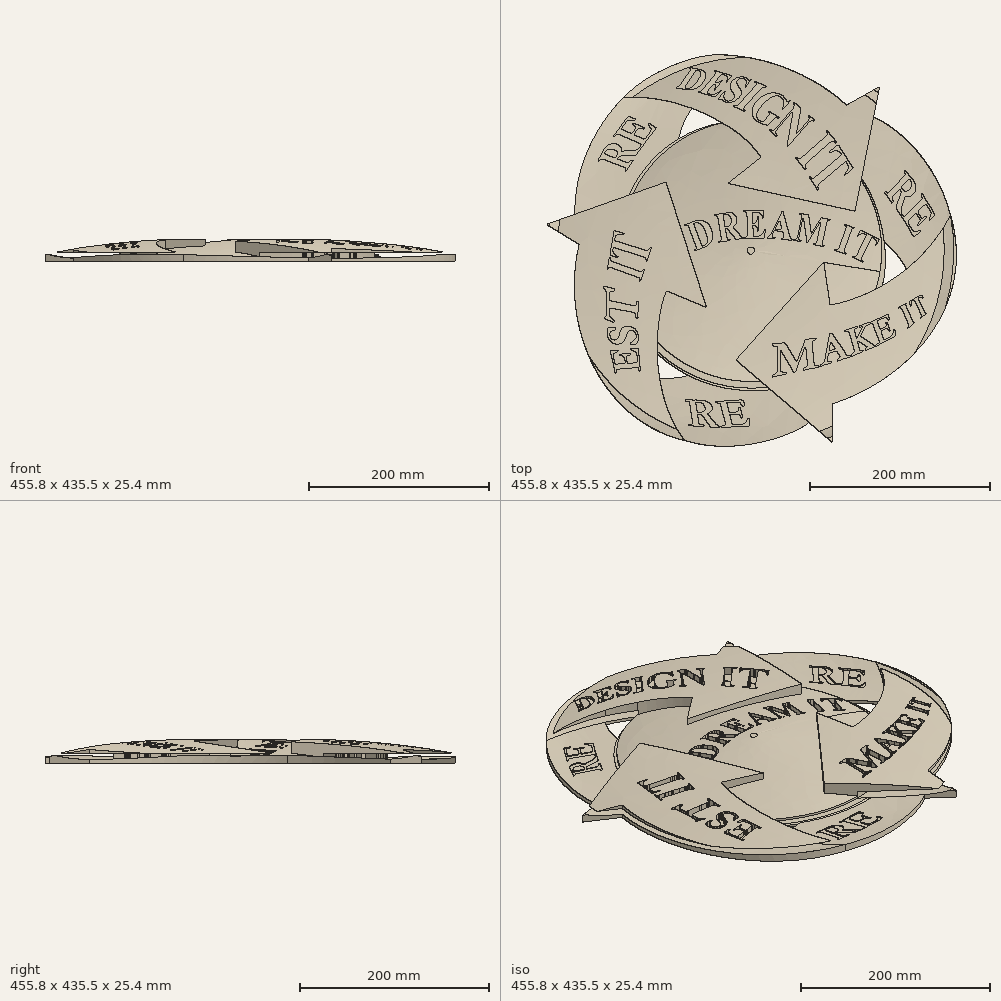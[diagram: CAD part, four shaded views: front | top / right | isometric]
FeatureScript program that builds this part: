
annotation { "Feature Type Name" : "Feature", "Feature Type Description" : "" }
export const myFeature = defineFeature(function(context is Context, id is Id, definition is map)
    precondition{}
    {
        {
            var Q0;
            Q0=qCreatedBy(makeId("Top.planeOp"),FACE);
            var sketch = newSketch(context, id + "F0", { "sketchPlane" : qUnion([Q0])});
            skLineSegment(sketch, "E0", {"start": v(-151.8, -139.59) * mm, "end": v(-151.75, -139.73) * mm});
            skLineSegment(sketch, "E1", {"start": v(-151.75, -139.73) * mm, "end": v(-151.63, -140.16) * mm});
            skLineSegment(sketch, "E2", {"start": v(-151.63, -140.16) * mm, "end": v(-151.45, -140.65) * mm});
            skLineSegment(sketch, "E3", {"start": v(-151.45, -140.65) * mm, "end": v(-151.17, -140.98) * mm});
            skLineSegment(sketch, "E4", {"start": v(-151.17, -140.98) * mm, "end": v(-150.8, -141.1) * mm});
            skLineSegment(sketch, "E5", {"start": v(-150.8, -141.1) * mm, "end": v(-150.68, -141.1) * mm});
            skLineSegment(sketch, "E6", {"start": v(-150.68, -141.1) * mm, "end": v(-150.47, -141.09) * mm});
            skLineSegment(sketch, "E7", {"start": v(-150.47, -141.09) * mm, "end": v(-149.83, -141.24) * mm});
            skLineSegment(sketch, "E8", {"start": v(-149.83, -141.24) * mm, "end": v(-149.27, -141.68) * mm});
            skLineSegment(sketch, "E9", {"start": v(-149.27, -141.68) * mm, "end": v(-148.9, -142.3) * mm});
            skLineSegment(sketch, "E10", {"start": v(-148.9, -142.3) * mm, "end": v(-148.7, -142.85) * mm});
            skLineSegment(sketch, "E11", {"start": v(-148.7, -142.85) * mm, "end": v(-148.64, -143.03) * mm});
            skLineSegment(sketch, "E12", {"start": v(-148.64, -143.03) * mm, "end": v(-148.31, -144.03) * mm});
            skLineSegment(sketch, "E13", {"start": v(-148.31, -144.03) * mm, "end": v(-145.08, -154.14) * mm});
            skLineSegment(sketch, "E14", {"start": v(-145.08, -154.14) * mm, "end": v(-144.77, -155.15) * mm});
            skLineSegment(sketch, "E15", {"start": v(-144.77, -155.15) * mm, "end": v(-144.7, -155.39) * mm});
            skLineSegment(sketch, "E16", {"start": v(-144.7, -155.39) * mm, "end": v(-144.47, -156.1) * mm});
            skLineSegment(sketch, "E17", {"start": v(-144.47, -156.1) * mm, "end": v(-144.28, -157.04) * mm});
            skLineSegment(sketch, "E18", {"start": v(-144.28, -157.04) * mm, "end": v(-144.42, -158) * mm});
            skLineSegment(sketch, "E19", {"start": v(-144.42, -158) * mm, "end": v(-144.88, -158.74) * mm});
            skLineSegment(sketch, "E20", {"start": v(-144.88, -158.74) * mm, "end": v(-145.09, -158.93) * mm});
            skLineSegment(sketch, "E21", {"start": v(-145.09, -158.93) * mm, "end": v(-145.16, -159) * mm});
            skLineSegment(sketch, "E22", {"start": v(-145.16, -159) * mm, "end": v(-145.3, -159.3) * mm});
            skLineSegment(sketch, "E23", {"start": v(-145.3, -159.3) * mm, "end": v(-145.19, -159.68) * mm});
            skLineSegment(sketch, "E24", {"start": v(-145.19, -159.68) * mm, "end": v(-144.84, -159.95) * mm});
            skLineSegment(sketch, "E25", {"start": v(-144.84, -159.95) * mm, "end": v(-144.44, -160.04) * mm});
            skLineSegment(sketch, "E26", {"start": v(-144.44, -160.04) * mm, "end": v(-144.3, -160.03) * mm});
            skLineSegment(sketch, "E27", {"start": v(-144.3, -160.03) * mm, "end": v(-144, -160) * mm});
            skLineSegment(sketch, "E28", {"start": v(-144, -160) * mm, "end": v(-142.46, -160) * mm});
            skLineSegment(sketch, "E29", {"start": v(-142.46, -160) * mm, "end": v(-140.92, -160.1) * mm});
            skLineSegment(sketch, "E30", {"start": v(-140.92, -160.1) * mm, "end": v(-140.61, -160.1) * mm});
            skLineSegment(sketch, "E31", {"start": v(-140.61, -160.1) * mm, "end": v(-140.44, -160.11) * mm});
            skLineSegment(sketch, "E32", {"start": v(-140.44, -160.11) * mm, "end": v(-138.74, -160.21) * mm});
            skLineSegment(sketch, "E33", {"start": v(-138.74, -160.21) * mm, "end": v(-138.56, -160.22) * mm});
            skLineSegment(sketch, "E34", {"start": v(-138.56, -160.22) * mm, "end": v(-138.47, -160.23) * mm});
            skLineSegment(sketch, "E35", {"start": v(-138.47, -160.23) * mm, "end": v(-138.2, -160.22) * mm});
            skLineSegment(sketch, "E36", {"start": v(-138.2, -160.22) * mm, "end": v(-137.86, -160.15) * mm});
            skLineSegment(sketch, "E37", {"start": v(-137.86, -160.15) * mm, "end": v(-137.59, -159.97) * mm});
            skLineSegment(sketch, "E38", {"start": v(-137.59, -159.97) * mm, "end": v(-137.45, -159.7) * mm});
            skLineSegment(sketch, "E39", {"start": v(-137.45, -159.7) * mm, "end": v(-137.43, -159.61) * mm});
            skLineSegment(sketch, "E40", {"start": v(-137.43, -159.61) * mm, "end": v(-137.4, -159.5) * mm});
            skLineSegment(sketch, "E41", {"start": v(-137.4, -159.5) * mm, "end": v(-137.44, -159.15) * mm});
            skLineSegment(sketch, "E42", {"start": v(-137.44, -159.15) * mm, "end": v(-137.65, -158.86) * mm});
            skLineSegment(sketch, "E43", {"start": v(-137.65, -158.86) * mm, "end": v(-138, -158.68) * mm});
            skLineSegment(sketch, "E44", {"start": v(-138, -158.68) * mm, "end": v(-138.3, -158.6) * mm});
            skLineSegment(sketch, "E45", {"start": v(-138.3, -158.6) * mm, "end": v(-138.4, -158.57) * mm});
            skLineSegment(sketch, "E46", {"start": v(-138.4, -158.57) * mm, "end": v(-138.41, -158.57) * mm});
            skLineSegment(sketch, "E47", {"start": v(-138.41, -158.57) * mm, "end": v(-138.58, -158.54) * mm});
            skLineSegment(sketch, "E48", {"start": v(-138.58, -158.54) * mm, "end": v(-138.6, -158.53) * mm});
            skLineSegment(sketch, "E49", {"start": v(-138.6, -158.53) * mm, "end": v(-139.01, -158.48) * mm});
            skLineSegment(sketch, "E50", {"start": v(-139.01, -158.48) * mm, "end": v(-140.22, -158.08) * mm});
            skLineSegment(sketch, "E51", {"start": v(-140.22, -158.08) * mm, "end": v(-141.43, -157.24) * mm});
            skLineSegment(sketch, "E52", {"start": v(-141.43, -157.24) * mm, "end": v(-142.24, -156) * mm});
            skLineSegment(sketch, "E53", {"start": v(-142.24, -156) * mm, "end": v(-142.6, -154.79) * mm});
            skLineSegment(sketch, "E54", {"start": v(-142.6, -154.79) * mm, "end": v(-142.65, -154.38) * mm});
            skLineSegment(sketch, "E55", {"start": v(-142.65, -154.38) * mm, "end": v(-142.66, -154.3) * mm});
            skLineSegment(sketch, "E56", {"start": v(-142.66, -154.3) * mm, "end": v(-142.89, -153.47) * mm});
            skLineSegment(sketch, "E57", {"start": v(-142.89, -153.47) * mm, "end": v(-142.91, -153.38) * mm});
            skLineSegment(sketch, "E58", {"start": v(-142.91, -153.38) * mm, "end": v(-142.96, -153.18) * mm});
            skLineSegment(sketch, "E59", {"start": v(-142.96, -153.18) * mm, "end": v(-143.1, -152.55) * mm});
            skLineSegment(sketch, "E60", {"start": v(-143.1, -152.55) * mm, "end": v(-143.03, -152.06) * mm});
            skLineSegment(sketch, "E61", {"start": v(-143.03, -152.06) * mm, "end": v(-142.65, -151.78) * mm});
            skLineSegment(sketch, "E62", {"start": v(-142.65, -151.78) * mm, "end": v(-142.06, -151.62) * mm});
            skLineSegment(sketch, "E63", {"start": v(-142.06, -151.62) * mm, "end": v(-141.85, -151.58) * mm});
            skLineSegment(sketch, "E64", {"start": v(-141.85, -151.58) * mm, "end": v(-140.51, -151.31) * mm});
            skLineSegment(sketch, "E65", {"start": v(-140.51, -151.31) * mm, "end": v(-127.08, -148.66) * mm});
            skLineSegment(sketch, "E66", {"start": v(-127.08, -148.66) * mm, "end": v(-125.74, -148.38) * mm});
            skLineSegment(sketch, "E67", {"start": v(-125.74, -148.38) * mm, "end": v(-125.4, -148.3) * mm});
            skLineSegment(sketch, "E68", {"start": v(-125.4, -148.3) * mm, "end": v(-124.31, -148.2) * mm});
            skLineSegment(sketch, "E69", {"start": v(-124.31, -148.2) * mm, "end": v(-123.07, -148.35) * mm});
            skLineSegment(sketch, "E70", {"start": v(-123.07, -148.35) * mm, "end": v(-122.03, -149) * mm});
            skLineSegment(sketch, "E71", {"start": v(-122.03, -149) * mm, "end": v(-121.37, -149.93) * mm});
            skLineSegment(sketch, "E72", {"start": v(-121.37, -149.93) * mm, "end": v(-121.23, -150.27) * mm});
            skLineSegment(sketch, "E73", {"start": v(-121.23, -150.27) * mm, "end": v(-121.18, -150.4) * mm});
            skLineSegment(sketch, "E74", {"start": v(-121.18, -150.4) * mm, "end": v(-121, -150.73) * mm});
            skLineSegment(sketch, "E75", {"start": v(-121, -150.73) * mm, "end": v(-120.67, -151.14) * mm});
            skLineSegment(sketch, "E76", {"start": v(-120.67, -151.14) * mm, "end": v(-120.24, -151.37) * mm});
            skLineSegment(sketch, "E77", {"start": v(-120.24, -151.37) * mm, "end": v(-119.82, -151.36) * mm});
            skLineSegment(sketch, "E78", {"start": v(-119.82, -151.36) * mm, "end": v(-119.7, -151.3) * mm});
            skLineSegment(sketch, "E79", {"start": v(-119.7, -151.3) * mm, "end": v(-119.58, -151.26) * mm});
            skLineSegment(sketch, "E80", {"start": v(-119.58, -151.26) * mm, "end": v(-119.27, -150.96) * mm});
            skLineSegment(sketch, "E81", {"start": v(-119.27, -150.96) * mm, "end": v(-119.2, -150.51) * mm});
            skLineSegment(sketch, "E82", {"start": v(-119.2, -150.51) * mm, "end": v(-119.34, -150.02) * mm});
            skLineSegment(sketch, "E83", {"start": v(-119.34, -150.02) * mm, "end": v(-119.46, -149.65) * mm});
            skLineSegment(sketch, "E84", {"start": v(-119.46, -149.65) * mm, "end": v(-119.49, -149.52) * mm});
            skLineSegment(sketch, "E85", {"start": v(-119.49, -149.52) * mm, "end": v(-119.5, -149.5) * mm});
            skLineSegment(sketch, "E86", {"start": v(-119.5, -149.5) * mm, "end": v(-119.6, -149.16) * mm});
            skLineSegment(sketch, "E87", {"start": v(-119.6, -149.16) * mm, "end": v(-119.61, -149.13) * mm});
            skLineSegment(sketch, "E88", {"start": v(-119.61, -149.13) * mm, "end": v(-119.84, -148.5) * mm});
            skLineSegment(sketch, "E89", {"start": v(-119.84, -148.5) * mm, "end": v(-120.65, -145.27) * mm});
            skLineSegment(sketch, "E90", {"start": v(-120.65, -145.27) * mm, "end": v(-121.15, -141.98) * mm});
            skLineSegment(sketch, "E91", {"start": v(-121.15, -141.98) * mm, "end": v(-121.24, -141.32) * mm});
            skLineSegment(sketch, "E92", {"start": v(-121.24, -141.32) * mm, "end": v(-121.26, -141.19) * mm});
            skLineSegment(sketch, "E93", {"start": v(-121.26, -141.19) * mm, "end": v(-121.23, -140.77) * mm});
            skLineSegment(sketch, "E94", {"start": v(-121.23, -140.77) * mm, "end": v(-121.23, -140.2) * mm});
            skLineSegment(sketch, "E95", {"start": v(-121.23, -140.2) * mm, "end": v(-121.43, -139.74) * mm});
            skLineSegment(sketch, "E96", {"start": v(-121.43, -139.74) * mm, "end": v(-121.87, -139.53) * mm});
            skLineSegment(sketch, "E97", {"start": v(-121.87, -139.53) * mm, "end": v(-122.02, -139.52) * mm});
            skLineSegment(sketch, "E98", {"start": v(-122.02, -139.52) * mm, "end": v(-122.2, -139.51) * mm});
            skLineSegment(sketch, "E99", {"start": v(-122.2, -139.51) * mm, "end": v(-122.73, -139.67) * mm});
            skLineSegment(sketch, "E100", {"start": v(-122.73, -139.67) * mm, "end": v(-123.01, -140.12) * mm});
            skLineSegment(sketch, "E101", {"start": v(-123.01, -140.12) * mm, "end": v(-123.04, -140.72) * mm});
            skLineSegment(sketch, "E102", {"start": v(-123.04, -140.72) * mm, "end": v(-123.01, -141.18) * mm});
            skLineSegment(sketch, "E103", {"start": v(-123.01, -141.18) * mm, "end": v(-123.01, -141.33) * mm});
            skLineSegment(sketch, "E104", {"start": v(-123.01, -141.33) * mm, "end": v(-123.01, -141.53) * mm});
            skLineSegment(sketch, "E105", {"start": v(-123.01, -141.53) * mm, "end": v(-123.1, -142.15) * mm});
            skLineSegment(sketch, "E106", {"start": v(-123.1, -142.15) * mm, "end": v(-123.4, -142.78) * mm});
            skLineSegment(sketch, "E107", {"start": v(-123.4, -142.78) * mm, "end": v(-123.92, -143.22) * mm});
            skLineSegment(sketch, "E108", {"start": v(-123.92, -143.22) * mm, "end": v(-124.51, -143.44) * mm});
            skLineSegment(sketch, "E109", {"start": v(-124.51, -143.44) * mm, "end": v(-124.71, -143.47) * mm});
            skLineSegment(sketch, "E110", {"start": v(-124.71, -143.47) * mm, "end": v(-124.83, -143.48) * mm});
            skLineSegment(sketch, "E111", {"start": v(-124.83, -143.48) * mm, "end": v(-125.99, -143.77) * mm});
            skLineSegment(sketch, "E112", {"start": v(-125.99, -143.77) * mm, "end": v(-126.1, -143.79) * mm});
            skLineSegment(sketch, "E113", {"start": v(-126.1, -143.79) * mm, "end": v(-126.78, -143.92) * mm});
            skLineSegment(sketch, "E114", {"start": v(-126.78, -143.92) * mm, "end": v(-133.5, -145.17) * mm});
            skLineSegment(sketch, "E115", {"start": v(-133.5, -145.17) * mm, "end": v(-134.18, -145.3) * mm});
            skLineSegment(sketch, "E116", {"start": v(-134.18, -145.3) * mm, "end": v(-134.94, -145.44) * mm});
            skLineSegment(sketch, "E117", {"start": v(-134.94, -145.44) * mm, "end": v(-142.5, -146.82) * mm});
            skLineSegment(sketch, "E118", {"start": v(-142.5, -146.82) * mm, "end": v(-143.26, -146.96) * mm});
            skLineSegment(sketch, "E119", {"start": v(-143.26, -146.96) * mm, "end": v(-143.48, -147) * mm});
            skLineSegment(sketch, "E120", {"start": v(-143.48, -147) * mm, "end": v(-144.14, -147.09) * mm});
            skLineSegment(sketch, "E121", {"start": v(-144.14, -147.09) * mm, "end": v(-144.64, -147) * mm});
            skLineSegment(sketch, "E122", {"start": v(-144.64, -147) * mm, "end": v(-144.94, -146.6) * mm});
            skLineSegment(sketch, "E123", {"start": v(-144.94, -146.6) * mm, "end": v(-145.17, -145.96) * mm});
            skLineSegment(sketch, "E124", {"start": v(-145.17, -145.96) * mm, "end": v(-145.23, -145.75) * mm});
            skLineSegment(sketch, "E125", {"start": v(-145.23, -145.75) * mm, "end": v(-145.3, -145.54) * mm});
            skLineSegment(sketch, "E126", {"start": v(-145.3, -145.54) * mm, "end": v(-146.02, -143.44) * mm});
            skLineSegment(sketch, "E127", {"start": v(-146.02, -143.44) * mm, "end": v(-146.1, -143.24) * mm});
            skLineSegment(sketch, "E128", {"start": v(-146.1, -143.24) * mm, "end": v(-146.18, -143.02) * mm});
            skLineSegment(sketch, "E129", {"start": v(-146.18, -143.02) * mm, "end": v(-146.12, -142.12) * mm});
            skLineSegment(sketch, "E130", {"start": v(-146.12, -142.12) * mm, "end": v(-145.5, -141.47) * mm});
            skLineSegment(sketch, "E131", {"start": v(-145.5, -141.47) * mm, "end": v(-145.3, -141.39) * mm});
            skLineSegment(sketch, "E132", {"start": v(-145.3, -141.39) * mm, "end": v(-145.1, -141.3) * mm});
            skLineSegment(sketch, "E133", {"start": v(-145.1, -141.3) * mm, "end": v(-144.15, -140.72) * mm});
            skLineSegment(sketch, "E134", {"start": v(-144.15, -140.72) * mm, "end": v(-143.23, -140.1) * mm});
            skLineSegment(sketch, "E135", {"start": v(-143.23, -140.1) * mm, "end": v(-143.05, -139.97) * mm});
            skLineSegment(sketch, "E136", {"start": v(-143.05, -139.97) * mm, "end": v(-142.98, -139.92) * mm});
            skLineSegment(sketch, "E137", {"start": v(-142.98, -139.92) * mm, "end": v(-142.76, -139.77) * mm});
            skLineSegment(sketch, "E138", {"start": v(-142.76, -139.77) * mm, "end": v(-142.53, -139.55) * mm});
            skLineSegment(sketch, "E139", {"start": v(-142.53, -139.55) * mm, "end": v(-142.43, -139.25) * mm});
            skLineSegment(sketch, "E140", {"start": v(-142.43, -139.25) * mm, "end": v(-142.51, -138.94) * mm});
            skLineSegment(sketch, "E141", {"start": v(-142.51, -138.94) * mm, "end": v(-142.56, -138.85) * mm});
            skLineSegment(sketch, "E142", {"start": v(-142.56, -138.85) * mm, "end": v(-142.63, -138.73) * mm});
            skLineSegment(sketch, "E143", {"start": v(-142.63, -138.73) * mm, "end": v(-143.02, -138.33) * mm});
            skLineSegment(sketch, "E144", {"start": v(-143.02, -138.33) * mm, "end": v(-143.57, -138.23) * mm});
            skLineSegment(sketch, "E145", {"start": v(-143.57, -138.23) * mm, "end": v(-143.7, -138.25) * mm});
            skLineSegment(sketch, "E146", {"start": v(-143.7, -138.25) * mm, "end": v(-144.36, -138.37) * mm});
            skLineSegment(sketch, "E147", {"start": v(-144.36, -138.37) * mm, "end": v(-151.08, -139.47) * mm});
            skLineSegment(sketch, "E148", {"start": v(-151.08, -139.47) * mm, "end": v(-151.8, -139.59) * mm});
            skLineSegment(sketch, "E149", {"start": v(105.73, 98.84) * mm, "end": v(105.54, 98.8) * mm});
            skLineSegment(sketch, "E150", {"start": v(105.54, 98.8) * mm, "end": v(104.74, 98.33) * mm});
            skLineSegment(sketch, "E151", {"start": v(104.74, 98.33) * mm, "end": v(104.04, 97.71) * mm});
            skLineSegment(sketch, "E152", {"start": v(104.04, 97.71) * mm, "end": v(103.9, 97.6) * mm});
            skLineSegment(sketch, "E153", {"start": v(103.9, 97.6) * mm, "end": v(101.67, 95.71) * mm});
            skLineSegment(sketch, "E154", {"start": v(101.67, 95.71) * mm, "end": v(79.4, 76.9) * mm});
            skLineSegment(sketch, "E155", {"start": v(79.4, 76.9) * mm, "end": v(77.18, 75) * mm});
            skLineSegment(sketch, "E156", {"start": v(77.18, 75) * mm, "end": v(77.04, 74.89) * mm});
            skLineSegment(sketch, "E157", {"start": v(77.04, 74.89) * mm, "end": v(75.67, 73.59) * mm});
            skLineSegment(sketch, "E158", {"start": v(75.67, 73.59) * mm, "end": v(75.55, 73.44) * mm});
            skLineSegment(sketch, "E159", {"start": v(75.55, 73.44) * mm, "end": v(75.35, 73.22) * mm});
            skLineSegment(sketch, "E160", {"start": v(75.35, 73.22) * mm, "end": v(74.85, 72.44) * mm});
            skLineSegment(sketch, "E161", {"start": v(74.85, 72.44) * mm, "end": v(74.5, 71.37) * mm});
            skLineSegment(sketch, "E162", {"start": v(74.5, 71.37) * mm, "end": v(74.5, 70.25) * mm});
            skLineSegment(sketch, "E163", {"start": v(74.5, 70.25) * mm, "end": v(74.75, 69.35) * mm});
            skLineSegment(sketch, "E164", {"start": v(74.75, 69.35) * mm, "end": v(74.89, 69.07) * mm});
            skLineSegment(sketch, "E165", {"start": v(74.89, 69.07) * mm, "end": v(74.94, 68.97) * mm});
            skLineSegment(sketch, "E166", {"start": v(74.94, 68.97) * mm, "end": v(75.48, 67.9) * mm});
            skLineSegment(sketch, "E167", {"start": v(75.48, 67.9) * mm, "end": v(75.52, 67.8) * mm});
            skLineSegment(sketch, "E168", {"start": v(75.52, 67.8) * mm, "end": v(75.55, 67.72) * mm});
            skLineSegment(sketch, "E169", {"start": v(75.55, 67.72) * mm, "end": v(75.51, 67.4) * mm});
            skLineSegment(sketch, "E170", {"start": v(75.51, 67.4) * mm, "end": v(75.3, 67.13) * mm});
            skLineSegment(sketch, "E171", {"start": v(75.3, 67.13) * mm, "end": v(75.23, 67.1) * mm});
            skLineSegment(sketch, "E172", {"start": v(75.23, 67.1) * mm, "end": v(75.17, 67.05) * mm});
            skLineSegment(sketch, "E173", {"start": v(75.17, 67.05) * mm, "end": v(74.84, 66.98) * mm});
            skLineSegment(sketch, "E174", {"start": v(74.84, 66.98) * mm, "end": v(74.55, 67.1) * mm});
            skLineSegment(sketch, "E175", {"start": v(74.55, 67.1) * mm, "end": v(74.5, 67.16) * mm});
            skLineSegment(sketch, "E176", {"start": v(74.5, 67.16) * mm, "end": v(74.44, 67.23) * mm});
            skLineSegment(sketch, "E177", {"start": v(74.44, 67.23) * mm, "end": v(73.93, 67.9) * mm});
            skLineSegment(sketch, "E178", {"start": v(73.93, 67.9) * mm, "end": v(73.88, 67.98) * mm});
            skLineSegment(sketch, "E179", {"start": v(73.88, 67.98) * mm, "end": v(73.17, 69.05) * mm});
            skLineSegment(sketch, "E180", {"start": v(73.17, 69.05) * mm, "end": v(69.74, 74.47) * mm});
            skLineSegment(sketch, "E181", {"start": v(69.74, 74.47) * mm, "end": v(66.2, 79.83) * mm});
            skLineSegment(sketch, "E182", {"start": v(66.2, 79.83) * mm, "end": v(65.44, 80.86) * mm});
            skLineSegment(sketch, "E183", {"start": v(65.44, 80.86) * mm, "end": v(65.4, 80.92) * mm});
            skLineSegment(sketch, "E184", {"start": v(65.4, 80.92) * mm, "end": v(65.05, 81.5) * mm});
            skLineSegment(sketch, "E185", {"start": v(65.05, 81.5) * mm, "end": v(65.01, 81.55) * mm});
            skLineSegment(sketch, "E186", {"start": v(65.01, 81.55) * mm, "end": v(64.95, 81.64) * mm});
            skLineSegment(sketch, "E187", {"start": v(64.95, 81.64) * mm, "end": v(64.91, 82.03) * mm});
            skLineSegment(sketch, "E188", {"start": v(64.91, 82.03) * mm, "end": v(65.14, 82.36) * mm});
            skLineSegment(sketch, "E189", {"start": v(65.14, 82.36) * mm, "end": v(65.2, 82.43) * mm});
            skLineSegment(sketch, "E190", {"start": v(65.2, 82.43) * mm, "end": v(65.28, 82.5) * mm});
            skLineSegment(sketch, "E191", {"start": v(65.28, 82.5) * mm, "end": v(65.66, 82.64) * mm});
            skLineSegment(sketch, "E192", {"start": v(65.66, 82.64) * mm, "end": v(66.03, 82.48) * mm});
            skLineSegment(sketch, "E193", {"start": v(66.03, 82.48) * mm, "end": v(66.1, 82.4) * mm});
            skLineSegment(sketch, "E194", {"start": v(66.1, 82.4) * mm, "end": v(66.17, 82.33) * mm});
            skLineSegment(sketch, "E195", {"start": v(66.17, 82.33) * mm, "end": v(66.8, 81.53) * mm});
            skLineSegment(sketch, "E196", {"start": v(66.8, 81.53) * mm, "end": v(66.86, 81.45) * mm});
            skLineSegment(sketch, "E197", {"start": v(66.86, 81.45) * mm, "end": v(67.04, 81.22) * mm});
            skLineSegment(sketch, "E198", {"start": v(67.04, 81.22) * mm, "end": v(67.73, 80.62) * mm});
            skLineSegment(sketch, "E199", {"start": v(67.73, 80.62) * mm, "end": v(68.66, 80.26) * mm});
            skLineSegment(sketch, "E200", {"start": v(68.66, 80.26) * mm, "end": v(69.64, 80.38) * mm});
            skLineSegment(sketch, "E201", {"start": v(69.64, 80.38) * mm, "end": v(70.47, 80.78) * mm});
            skLineSegment(sketch, "E202", {"start": v(70.47, 80.78) * mm, "end": v(70.7, 80.96) * mm});
            skLineSegment(sketch, "E203", {"start": v(70.7, 80.96) * mm, "end": v(71.53, 81.56) * mm});
            skLineSegment(sketch, "E204", {"start": v(71.53, 81.56) * mm, "end": v(75.47, 84.77) * mm});
            skLineSegment(sketch, "E205", {"start": v(75.47, 84.77) * mm, "end": v(79.35, 88.06) * mm});
            skLineSegment(sketch, "E206", {"start": v(79.35, 88.06) * mm, "end": v(80.13, 88.7) * mm});
            skLineSegment(sketch, "E207", {"start": v(80.13, 88.7) * mm, "end": v(80.9, 89.34) * mm});
            skLineSegment(sketch, "E208", {"start": v(80.9, 89.34) * mm, "end": v(88.58, 95.77) * mm});
            skLineSegment(sketch, "E209", {"start": v(88.58, 95.77) * mm, "end": v(89.34, 96.42) * mm});
            skLineSegment(sketch, "E210", {"start": v(89.34, 96.42) * mm, "end": v(90.1, 97.07) * mm});
            skLineSegment(sketch, "E211", {"start": v(90.1, 97.07) * mm, "end": v(93.95, 100.27) * mm});
            skLineSegment(sketch, "E212", {"start": v(93.95, 100.27) * mm, "end": v(97.76, 103.54) * mm});
            skLineSegment(sketch, "E213", {"start": v(97.76, 103.54) * mm, "end": v(98.5, 104.22) * mm});
            skLineSegment(sketch, "E214", {"start": v(98.5, 104.22) * mm, "end": v(98.6, 104.32) * mm});
            skLineSegment(sketch, "E215", {"start": v(98.6, 104.32) * mm, "end": v(99.65, 105.18) * mm});
            skLineSegment(sketch, "E216", {"start": v(99.65, 105.18) * mm, "end": v(99.76, 105.26) * mm});
            skLineSegment(sketch, "E217", {"start": v(99.76, 105.26) * mm, "end": v(99.92, 105.39) * mm});
            skLineSegment(sketch, "E218", {"start": v(99.92, 105.39) * mm, "end": v(100.38, 105.8) * mm});
            skLineSegment(sketch, "E219", {"start": v(100.38, 105.8) * mm, "end": v(100.67, 106.26) * mm});
            skLineSegment(sketch, "E220", {"start": v(100.67, 106.26) * mm, "end": v(100.64, 106.77) * mm});
            skLineSegment(sketch, "E221", {"start": v(100.64, 106.77) * mm, "end": v(100.4, 107.29) * mm});
            skLineSegment(sketch, "E222", {"start": v(100.4, 107.29) * mm, "end": v(100.31, 107.45) * mm});
            skLineSegment(sketch, "E223", {"start": v(100.31, 107.45) * mm, "end": v(100, 108) * mm});
            skLineSegment(sketch, "E224", {"start": v(100, 108) * mm, "end": v(98.8, 109.5) * mm});
            skLineSegment(sketch, "E225", {"start": v(98.8, 109.5) * mm, "end": v(97, 110.8) * mm});
            skLineSegment(sketch, "E226", {"start": v(97, 110.8) * mm, "end": v(94.86, 111.22) * mm});
            skLineSegment(sketch, "E227", {"start": v(94.86, 111.22) * mm, "end": v(92.94, 110.85) * mm});
            skLineSegment(sketch, "E228", {"start": v(92.94, 110.85) * mm, "end": v(92.36, 110.6) * mm});
            skLineSegment(sketch, "E229", {"start": v(92.36, 110.6) * mm, "end": v(92.05, 110.46) * mm});
            skLineSegment(sketch, "E230", {"start": v(92.05, 110.46) * mm, "end": v(88.96, 109.04) * mm});
            skLineSegment(sketch, "E231", {"start": v(88.96, 109.04) * mm, "end": v(88.65, 108.9) * mm});
            skLineSegment(sketch, "E232", {"start": v(88.65, 108.9) * mm, "end": v(88.57, 108.86) * mm});
            skLineSegment(sketch, "E233", {"start": v(88.57, 108.86) * mm, "end": v(88.17, 108.74) * mm});
            skLineSegment(sketch, "E234", {"start": v(88.17, 108.74) * mm, "end": v(87.8, 108.86) * mm});
            skLineSegment(sketch, "E235", {"start": v(87.8, 108.86) * mm, "end": v(87.74, 108.95) * mm});
            skLineSegment(sketch, "E236", {"start": v(87.74, 108.95) * mm, "end": v(87.68, 109.02) * mm});
            skLineSegment(sketch, "E237", {"start": v(87.68, 109.02) * mm, "end": v(87.6, 109.43) * mm});
            skLineSegment(sketch, "E238", {"start": v(87.6, 109.43) * mm, "end": v(87.76, 109.82) * mm});
            skLineSegment(sketch, "E239", {"start": v(87.76, 109.82) * mm, "end": v(87.82, 109.89) * mm});
            skLineSegment(sketch, "E240", {"start": v(87.82, 109.89) * mm, "end": v(87.86, 109.94) * mm});
            skLineSegment(sketch, "E241", {"start": v(87.86, 109.94) * mm, "end": v(88.34, 110.43) * mm});
            skLineSegment(sketch, "E242", {"start": v(88.34, 110.43) * mm, "end": v(88.4, 110.47) * mm});
            skLineSegment(sketch, "E243", {"start": v(88.4, 110.47) * mm, "end": v(88.97, 110.95) * mm});
            skLineSegment(sketch, "E244", {"start": v(88.97, 110.95) * mm, "end": v(94.68, 115.74) * mm});
            skLineSegment(sketch, "E245", {"start": v(94.68, 115.74) * mm, "end": v(95.25, 116.22) * mm});
            skLineSegment(sketch, "E246", {"start": v(95.25, 116.22) * mm, "end": v(95.33, 116.29) * mm});
            skLineSegment(sketch, "E247", {"start": v(95.33, 116.29) * mm, "end": v(96.17, 116.86) * mm});
            skLineSegment(sketch, "E248", {"start": v(96.17, 116.86) * mm, "end": v(96.25, 116.9) * mm});
            skLineSegment(sketch, "E249", {"start": v(96.25, 116.9) * mm, "end": v(96.38, 117) * mm});
            skLineSegment(sketch, "E250", {"start": v(96.38, 117) * mm, "end": v(96.82, 117.17) * mm});
            skLineSegment(sketch, "E251", {"start": v(96.82, 117.17) * mm, "end": v(97.27, 117.16) * mm});
            skLineSegment(sketch, "E252", {"start": v(97.27, 117.16) * mm, "end": v(97.65, 116.9) * mm});
            skLineSegment(sketch, "E253", {"start": v(97.65, 116.9) * mm, "end": v(97.94, 116.53) * mm});
            skLineSegment(sketch, "E254", {"start": v(97.94, 116.53) * mm, "end": v(98.02, 116.4) * mm});
            skLineSegment(sketch, "E255", {"start": v(98.02, 116.4) * mm, "end": v(98.65, 115.38) * mm});
            skLineSegment(sketch, "E256", {"start": v(98.65, 115.38) * mm, "end": v(105.04, 105.31) * mm});
            skLineSegment(sketch, "E257", {"start": v(105.04, 105.31) * mm, "end": v(105.7, 104.32) * mm});
            skLineSegment(sketch, "E258", {"start": v(105.7, 104.32) * mm, "end": v(106.34, 103.35) * mm});
            skLineSegment(sketch, "E259", {"start": v(106.34, 103.35) * mm, "end": v(112.65, 93.55) * mm});
            skLineSegment(sketch, "E260", {"start": v(112.65, 93.55) * mm, "end": v(113.29, 92.57) * mm});
            skLineSegment(sketch, "E261", {"start": v(113.29, 92.57) * mm, "end": v(113.39, 92.41) * mm});
            skLineSegment(sketch, "E262", {"start": v(113.39, 92.41) * mm, "end": v(113.62, 91.88) * mm});
            skLineSegment(sketch, "E263", {"start": v(113.62, 91.88) * mm, "end": v(113.66, 91.33) * mm});
            skLineSegment(sketch, "E264", {"start": v(113.66, 91.33) * mm, "end": v(113.42, 90.84) * mm});
            skLineSegment(sketch, "E265", {"start": v(113.42, 90.84) * mm, "end": v(113.06, 90.47) * mm});
            skLineSegment(sketch, "E266", {"start": v(113.06, 90.47) * mm, "end": v(112.93, 90.36) * mm});
            skLineSegment(sketch, "E267", {"start": v(112.93, 90.36) * mm, "end": v(112.3, 89.83) * mm});
            skLineSegment(sketch, "E268", {"start": v(112.3, 89.83) * mm, "end": v(106, 84.53) * mm});
            skLineSegment(sketch, "E269", {"start": v(106, 84.53) * mm, "end": v(105.37, 84) * mm});
            skLineSegment(sketch, "E270", {"start": v(105.37, 84) * mm, "end": v(105.32, 83.96) * mm});
            skLineSegment(sketch, "E271", {"start": v(105.32, 83.96) * mm, "end": v(104.76, 83.57) * mm});
            skLineSegment(sketch, "E272", {"start": v(104.76, 83.57) * mm, "end": v(104.7, 83.54) * mm});
            skLineSegment(sketch, "E273", {"start": v(104.7, 83.54) * mm, "end": v(104.65, 83.51) * mm});
            skLineSegment(sketch, "E274", {"start": v(104.65, 83.51) * mm, "end": v(104.18, 83.6) * mm});
            skLineSegment(sketch, "E275", {"start": v(104.18, 83.6) * mm, "end": v(104.15, 83.64) * mm});
            skLineSegment(sketch, "E276", {"start": v(104.15, 83.64) * mm, "end": v(104.1, 83.68) * mm});
            skLineSegment(sketch, "E277", {"start": v(104.1, 83.68) * mm, "end": v(104.03, 84.15) * mm});
            skLineSegment(sketch, "E278", {"start": v(104.03, 84.15) * mm, "end": v(104.06, 84.2) * mm});
            skLineSegment(sketch, "E279", {"start": v(104.06, 84.2) * mm, "end": v(104.12, 84.3) * mm});
            skLineSegment(sketch, "E280", {"start": v(104.12, 84.3) * mm, "end": v(104.8, 85.28) * mm});
            skLineSegment(sketch, "E281", {"start": v(104.8, 85.28) * mm, "end": v(104.88, 85.37) * mm});
            skLineSegment(sketch, "E282", {"start": v(104.88, 85.37) * mm, "end": v(105.05, 85.63) * mm});
            skLineSegment(sketch, "E283", {"start": v(105.05, 85.63) * mm, "end": v(105.97, 86.87) * mm});
            skLineSegment(sketch, "E284", {"start": v(105.97, 86.87) * mm, "end": v(106.84, 88.14) * mm});
            skLineSegment(sketch, "E285", {"start": v(106.84, 88.14) * mm, "end": v(106.98, 88.4) * mm});
            skLineSegment(sketch, "E286", {"start": v(106.98, 88.4) * mm, "end": v(107.35, 89.08) * mm});
            skLineSegment(sketch, "E287", {"start": v(107.35, 89.08) * mm, "end": v(108.2, 91.22) * mm});
            skLineSegment(sketch, "E288", {"start": v(108.2, 91.22) * mm, "end": v(108.46, 93.73) * mm});
            skLineSegment(sketch, "E289", {"start": v(108.46, 93.73) * mm, "end": v(107.67, 96.18) * mm});
            skLineSegment(sketch, "E290", {"start": v(107.67, 96.18) * mm, "end": v(106.28, 98.23) * mm});
            skLineSegment(sketch, "E291", {"start": v(106.28, 98.23) * mm, "end": v(105.73, 98.84) * mm});
            skLineSegment(sketch, "E292", {"start": v(46.57, 154.33) * mm, "end": v(46.16, 154.08) * mm});
            skLineSegment(sketch, "E293", {"start": v(46.16, 154.08) * mm, "end": v(45.72, 153.66) * mm});
            skLineSegment(sketch, "E294", {"start": v(45.72, 153.66) * mm, "end": v(45.35, 153.18) * mm});
            skLineSegment(sketch, "E295", {"start": v(45.35, 153.18) * mm, "end": v(45.07, 152.82) * mm});
            skLineSegment(sketch, "E296", {"start": v(45.07, 152.82) * mm, "end": v(44.97, 152.7) * mm});
            skLineSegment(sketch, "E297", {"start": v(44.97, 152.7) * mm, "end": v(43.76, 151.3) * mm});
            skLineSegment(sketch, "E298", {"start": v(43.76, 151.3) * mm, "end": v(31.65, 137.29) * mm});
            skLineSegment(sketch, "E299", {"start": v(31.65, 137.29) * mm, "end": v(30.44, 135.89) * mm});
            skLineSegment(sketch, "E300", {"start": v(30.44, 135.89) * mm, "end": v(30.25, 135.66) * mm});
            skLineSegment(sketch, "E301", {"start": v(30.25, 135.66) * mm, "end": v(29.33, 134.54) * mm});
            skLineSegment(sketch, "E302", {"start": v(29.33, 134.54) * mm, "end": v(28.51, 133.33) * mm});
            skLineSegment(sketch, "E303", {"start": v(28.51, 133.33) * mm, "end": v(28.37, 133.08) * mm});
            skLineSegment(sketch, "E304", {"start": v(28.37, 133.08) * mm, "end": v(28.21, 132.8) * mm});
            skLineSegment(sketch, "E305", {"start": v(28.21, 132.8) * mm, "end": v(27.87, 131.9) * mm});
            skLineSegment(sketch, "E306", {"start": v(27.87, 131.9) * mm, "end": v(27.74, 130.73) * mm});
            skLineSegment(sketch, "E307", {"start": v(27.74, 130.73) * mm, "end": v(28, 129.6) * mm});
            skLineSegment(sketch, "E308", {"start": v(28, 129.6) * mm, "end": v(28.47, 128.74) * mm});
            skLineSegment(sketch, "E309", {"start": v(28.47, 128.74) * mm, "end": v(28.68, 128.5) * mm});
            skLineSegment(sketch, "E310", {"start": v(28.68, 128.5) * mm, "end": v(28.73, 128.42) * mm});
            skLineSegment(sketch, "E311", {"start": v(28.73, 128.42) * mm, "end": v(29.24, 127.76) * mm});
            skLineSegment(sketch, "E312", {"start": v(29.24, 127.76) * mm, "end": v(29.27, 127.69) * mm});
            skLineSegment(sketch, "E313", {"start": v(29.27, 127.69) * mm, "end": v(29.29, 127.66) * mm});
            skLineSegment(sketch, "E314", {"start": v(29.29, 127.66) * mm, "end": v(29.23, 127.43) * mm});
            skLineSegment(sketch, "E315", {"start": v(29.23, 127.43) * mm, "end": v(29.1, 127.2) * mm});
            skLineSegment(sketch, "E316", {"start": v(29.1, 127.2) * mm, "end": v(29.07, 127.16) * mm});
            skLineSegment(sketch, "E317", {"start": v(29.07, 127.16) * mm, "end": v(29.04, 127.12) * mm});
            skLineSegment(sketch, "E318", {"start": v(29.04, 127.12) * mm, "end": v(28.84, 126.98) * mm});
            skLineSegment(sketch, "E319", {"start": v(28.84, 126.98) * mm, "end": v(28.59, 126.97) * mm});
            skLineSegment(sketch, "E320", {"start": v(28.59, 126.97) * mm, "end": v(28.53, 127) * mm});
            skLineSegment(sketch, "E321", {"start": v(28.53, 127) * mm, "end": v(28.5, 127.02) * mm});
            skLineSegment(sketch, "E322", {"start": v(28.5, 127.02) * mm, "end": v(28.21, 127.2) * mm});
            skLineSegment(sketch, "E323", {"start": v(28.21, 127.2) * mm, "end": v(28.19, 127.21) * mm});
            skLineSegment(sketch, "E324", {"start": v(28.19, 127.21) * mm, "end": v(27.6, 127.73) * mm});
            skLineSegment(sketch, "E325", {"start": v(27.6, 127.73) * mm, "end": v(21.75, 132.92) * mm});
            skLineSegment(sketch, "E326", {"start": v(21.75, 132.92) * mm, "end": v(21.17, 133.44) * mm});
            skLineSegment(sketch, "E327", {"start": v(21.17, 133.44) * mm, "end": v(21.1, 133.5) * mm});
            skLineSegment(sketch, "E328", {"start": v(21.1, 133.5) * mm, "end": v(20.85, 133.84) * mm});
            skLineSegment(sketch, "E329", {"start": v(20.85, 133.84) * mm, "end": v(20.85, 134.23) * mm});
            skLineSegment(sketch, "E330", {"start": v(20.85, 134.23) * mm, "end": v(20.9, 134.32) * mm});
            skLineSegment(sketch, "E331", {"start": v(20.9, 134.32) * mm, "end": v(20.98, 134.42) * mm});
            skLineSegment(sketch, "E332", {"start": v(20.98, 134.42) * mm, "end": v(21.4, 134.59) * mm});
            skLineSegment(sketch, "E333", {"start": v(21.4, 134.59) * mm, "end": v(21.88, 134.44) * mm});
            skLineSegment(sketch, "E334", {"start": v(21.88, 134.44) * mm, "end": v(21.98, 134.4) * mm});
            skLineSegment(sketch, "E335", {"start": v(21.98, 134.4) * mm, "end": v(22.4, 134.2) * mm});
            skLineSegment(sketch, "E336", {"start": v(22.4, 134.2) * mm, "end": v(23.7, 133.75) * mm});
            skLineSegment(sketch, "E337", {"start": v(23.7, 133.75) * mm, "end": v(25.05, 133.66) * mm});
            skLineSegment(sketch, "E338", {"start": v(25.05, 133.66) * mm, "end": v(26.27, 134.2) * mm});
            skLineSegment(sketch, "E339", {"start": v(26.27, 134.2) * mm, "end": v(27.3, 135.1) * mm});
            skLineSegment(sketch, "E340", {"start": v(27.3, 135.1) * mm, "end": v(27.6, 135.43) * mm});
            skLineSegment(sketch, "E341", {"start": v(27.6, 135.43) * mm, "end": v(28.47, 136.37) * mm});
            skLineSegment(sketch, "E342", {"start": v(28.47, 136.37) * mm, "end": v(36.83, 145.9) * mm});
            skLineSegment(sketch, "E343", {"start": v(36.83, 145.9) * mm, "end": v(37.67, 146.86) * mm});
            skLineSegment(sketch, "E344", {"start": v(37.67, 146.86) * mm, "end": v(38.43, 147.74) * mm});
            skLineSegment(sketch, "E345", {"start": v(38.43, 147.74) * mm, "end": v(46.04, 156.58) * mm});
            skLineSegment(sketch, "E346", {"start": v(46.04, 156.58) * mm, "end": v(46.8, 157.46) * mm});
            skLineSegment(sketch, "E347", {"start": v(46.8, 157.46) * mm, "end": v(47.22, 157.94) * mm});
            skLineSegment(sketch, "E348", {"start": v(47.22, 157.94) * mm, "end": v(48.22, 160.53) * mm});
            skLineSegment(sketch, "E349", {"start": v(48.22, 160.53) * mm, "end": v(47.77, 163.29) * mm});
            skLineSegment(sketch, "E350", {"start": v(47.77, 163.29) * mm, "end": v(47.46, 163.86) * mm});
            skLineSegment(sketch, "E351", {"start": v(47.46, 163.86) * mm, "end": v(47.4, 163.95) * mm});
            skLineSegment(sketch, "E352", {"start": v(47.4, 163.95) * mm, "end": v(47.19, 164.4) * mm});
            skLineSegment(sketch, "E353", {"start": v(47.19, 164.4) * mm, "end": v(47.3, 164.85) * mm});
            skLineSegment(sketch, "E354", {"start": v(47.3, 164.85) * mm, "end": v(47.39, 164.93) * mm});
            skLineSegment(sketch, "E355", {"start": v(47.39, 164.93) * mm, "end": v(47.49, 165.02) * mm});
            skLineSegment(sketch, "E356", {"start": v(47.49, 165.02) * mm, "end": v(47.97, 165.05) * mm});
            skLineSegment(sketch, "E357", {"start": v(47.97, 165.05) * mm, "end": v(48.38, 164.76) * mm});
            skLineSegment(sketch, "E358", {"start": v(48.38, 164.76) * mm, "end": v(48.45, 164.7) * mm});
            skLineSegment(sketch, "E359", {"start": v(48.45, 164.7) * mm, "end": v(49, 164.21) * mm});
            skLineSegment(sketch, "E360", {"start": v(49, 164.21) * mm, "end": v(54.55, 159.35) * mm});
            skLineSegment(sketch, "E361", {"start": v(54.55, 159.35) * mm, "end": v(55.12, 158.88) * mm});
            skLineSegment(sketch, "E362", {"start": v(55.12, 158.88) * mm, "end": v(55.24, 158.77) * mm});
            skLineSegment(sketch, "E363", {"start": v(55.24, 158.77) * mm, "end": v(55.55, 158.36) * mm});
            skLineSegment(sketch, "E364", {"start": v(55.55, 158.36) * mm, "end": v(55.73, 157.82) * mm});
            skLineSegment(sketch, "E365", {"start": v(55.73, 157.82) * mm, "end": v(55.73, 157.24) * mm});
            skLineSegment(sketch, "E366", {"start": v(55.73, 157.24) * mm, "end": v(55.67, 156.79) * mm});
            skLineSegment(sketch, "E367", {"start": v(55.67, 156.79) * mm, "end": v(55.64, 156.64) * mm});
            skLineSegment(sketch, "E368", {"start": v(55.64, 156.64) * mm, "end": v(55.42, 155.48) * mm});
            skLineSegment(sketch, "E369", {"start": v(55.42, 155.48) * mm, "end": v(53.24, 143.87) * mm});
            skLineSegment(sketch, "E370", {"start": v(53.24, 143.87) * mm, "end": v(53.03, 142.7) * mm});
            skLineSegment(sketch, "E371", {"start": v(53.03, 142.7) * mm, "end": v(52.85, 141.74) * mm});
            skLineSegment(sketch, "E372", {"start": v(52.85, 141.74) * mm, "end": v(51.08, 132.15) * mm});
            skLineSegment(sketch, "E373", {"start": v(51.08, 132.15) * mm, "end": v(50.9, 131.18) * mm});
            skLineSegment(sketch, "E374", {"start": v(50.9, 131.18) * mm, "end": v(50.89, 131.08) * mm});
            skLineSegment(sketch, "E375", {"start": v(50.89, 131.08) * mm, "end": v(50.79, 130.5) * mm});
            skLineSegment(sketch, "E376", {"start": v(50.79, 130.5) * mm, "end": v(50.97, 129.83) * mm});
            skLineSegment(sketch, "E377", {"start": v(50.97, 129.83) * mm, "end": v(51.1, 129.69) * mm});
            skLineSegment(sketch, "E378", {"start": v(51.1, 129.69) * mm, "end": v(51.24, 129.84) * mm});
            skLineSegment(sketch, "E379", {"start": v(51.24, 129.84) * mm, "end": v(52.62, 131.3) * mm});
            skLineSegment(sketch, "E380", {"start": v(52.62, 131.3) * mm, "end": v(52.75, 131.44) * mm});
            skLineSegment(sketch, "E381", {"start": v(52.75, 131.44) * mm, "end": v(53.53, 132.35) * mm});
            skLineSegment(sketch, "E382", {"start": v(53.53, 132.35) * mm, "end": v(61.37, 141.45) * mm});
            skLineSegment(sketch, "E383", {"start": v(61.37, 141.45) * mm, "end": v(62.14, 142.36) * mm});
            skLineSegment(sketch, "E384", {"start": v(62.14, 142.36) * mm, "end": v(62.3, 142.54) * mm});
            skLineSegment(sketch, "E385", {"start": v(62.3, 142.54) * mm, "end": v(63.75, 144.45) * mm});
            skLineSegment(sketch, "E386", {"start": v(63.75, 144.45) * mm, "end": v(63.89, 144.65) * mm});
            skLineSegment(sketch, "E387", {"start": v(63.89, 144.65) * mm, "end": v(64.08, 144.94) * mm});
            skLineSegment(sketch, "E388", {"start": v(64.08, 144.94) * mm, "end": v(64.54, 145.88) * mm});
            skLineSegment(sketch, "E389", {"start": v(64.54, 145.88) * mm, "end": v(64.77, 147.11) * mm});
            skLineSegment(sketch, "E390", {"start": v(64.77, 147.11) * mm, "end": v(64.54, 148.34) * mm});
            skLineSegment(sketch, "E391", {"start": v(64.54, 148.34) * mm, "end": v(64, 149.28) * mm});
            skLineSegment(sketch, "E392", {"start": v(64, 149.28) * mm, "end": v(63.78, 149.55) * mm});
            skLineSegment(sketch, "E393", {"start": v(63.78, 149.55) * mm, "end": v(63.73, 149.6) * mm});
            skLineSegment(sketch, "E394", {"start": v(63.73, 149.6) * mm, "end": v(63.57, 149.77) * mm});
            skLineSegment(sketch, "E395", {"start": v(63.57, 149.77) * mm, "end": v(63.4, 150) * mm});
            skLineSegment(sketch, "E396", {"start": v(63.4, 150) * mm, "end": v(63.35, 150.27) * mm});
            skLineSegment(sketch, "E397", {"start": v(63.35, 150.27) * mm, "end": v(63.46, 150.52) * mm});
            skLineSegment(sketch, "E398", {"start": v(63.46, 150.52) * mm, "end": v(63.52, 150.58) * mm});
            skLineSegment(sketch, "E399", {"start": v(63.52, 150.58) * mm, "end": v(63.62, 150.67) * mm});
            skLineSegment(sketch, "E400", {"start": v(63.62, 150.67) * mm, "end": v(64.1, 150.75) * mm});
            skLineSegment(sketch, "E401", {"start": v(64.1, 150.75) * mm, "end": v(64.55, 150.51) * mm});
            skLineSegment(sketch, "E402", {"start": v(64.55, 150.51) * mm, "end": v(64.62, 150.45) * mm});
            skLineSegment(sketch, "E403", {"start": v(64.62, 150.45) * mm, "end": v(65.16, 149.99) * mm});
            skLineSegment(sketch, "E404", {"start": v(65.16, 149.99) * mm, "end": v(70.44, 145.38) * mm});
            skLineSegment(sketch, "E405", {"start": v(70.44, 145.38) * mm, "end": v(70.97, 144.9) * mm});
            skLineSegment(sketch, "E406", {"start": v(70.97, 144.9) * mm, "end": v(71.03, 144.85) * mm});
            skLineSegment(sketch, "E407", {"start": v(71.03, 144.85) * mm, "end": v(71.28, 144.53) * mm});
            skLineSegment(sketch, "E408", {"start": v(71.28, 144.53) * mm, "end": v(71.28, 144.12) * mm});
            skLineSegment(sketch, "E409", {"start": v(71.28, 144.12) * mm, "end": v(71.23, 144.03) * mm});
            skLineSegment(sketch, "E410", {"start": v(71.23, 144.03) * mm, "end": v(71.15, 143.93) * mm});
            skLineSegment(sketch, "E411", {"start": v(71.15, 143.93) * mm, "end": v(70.73, 143.67) * mm});
            skLineSegment(sketch, "E412", {"start": v(70.73, 143.67) * mm, "end": v(70.25, 143.75) * mm});
            skLineSegment(sketch, "E413", {"start": v(70.25, 143.75) * mm, "end": v(70.15, 143.81) * mm});
            skLineSegment(sketch, "E414", {"start": v(70.15, 143.81) * mm, "end": v(69.79, 144.05) * mm});
            skLineSegment(sketch, "E415", {"start": v(69.79, 144.05) * mm, "end": v(68.5, 144.46) * mm});
            skLineSegment(sketch, "E416", {"start": v(68.5, 144.46) * mm, "end": v(67.05, 144.29) * mm});
            skLineSegment(sketch, "E417", {"start": v(67.05, 144.29) * mm, "end": v(65.77, 143.52) * mm});
            skLineSegment(sketch, "E418", {"start": v(41.97, 116.25) * mm, "end": v(41.94, 116.21) * mm});
            skLineSegment(sketch, "E419", {"start": v(41.94, 116.21) * mm, "end": v(41.6, 115.83) * mm});
            skLineSegment(sketch, "E420", {"start": v(41.6, 115.83) * mm, "end": v(41.56, 115.79) * mm});
            skLineSegment(sketch, "E421", {"start": v(41.56, 115.79) * mm, "end": v(41.5, 115.72) * mm});
            skLineSegment(sketch, "E422", {"start": v(41.5, 115.72) * mm, "end": v(41.13, 115.35) * mm});
            skLineSegment(sketch, "E423", {"start": v(41.13, 115.35) * mm, "end": v(40.67, 115.23) * mm});
            skLineSegment(sketch, "E424", {"start": v(40.67, 115.23) * mm, "end": v(40.56, 115.28) * mm});
            skLineSegment(sketch, "E425", {"start": v(40.56, 115.28) * mm, "end": v(40.44, 115.33) * mm});
            skLineSegment(sketch, "E426", {"start": v(40.44, 115.33) * mm, "end": v(40.2, 115.75) * mm});
            skLineSegment(sketch, "E427", {"start": v(40.2, 115.75) * mm, "end": v(40.25, 116.26) * mm});
            skLineSegment(sketch, "E428", {"start": v(40.25, 116.26) * mm, "end": v(40.27, 116.35) * mm});
            skLineSegment(sketch, "E429", {"start": v(40.27, 116.35) * mm, "end": v(40.33, 116.74) * mm});
            skLineSegment(sketch, "E430", {"start": v(46.64, 152.37) * mm, "end": v(46.67, 152.54) * mm});
            skLineSegment(sketch, "E431", {"start": v(46.67, 152.54) * mm, "end": v(46.81, 153.38) * mm});
            skLineSegment(sketch, "E432", {"start": v(46.81, 153.38) * mm, "end": v(46.76, 154.23) * mm});
            skLineSegment(sketch, "E433", {"start": v(1.37, 155.24) * mm, "end": v(1.38, 155.95) * mm});
            skLineSegment(sketch, "E434", {"start": v(1.38, 155.95) * mm, "end": v(2.2, 159.22) * mm});
            skLineSegment(sketch, "E435", {"start": v(2.2, 159.22) * mm, "end": v(3.74, 162.2) * mm});
            skLineSegment(sketch, "E436", {"start": v(3.74, 162.2) * mm, "end": v(4.12, 162.76) * mm});
            skLineSegment(sketch, "E437", {"start": v(4.12, 162.76) * mm, "end": v(4.94, 164.01) * mm});
            skLineSegment(sketch, "E438", {"start": v(4.94, 164.01) * mm, "end": v(7.87, 167.45) * mm});
            skLineSegment(sketch, "E439", {"start": v(7.87, 167.45) * mm, "end": v(12.3, 171.14) * mm});
            skLineSegment(sketch, "E440", {"start": v(12.3, 171.14) * mm, "end": v(17.41, 173.76) * mm});
            skLineSegment(sketch, "E441", {"start": v(17.41, 173.76) * mm, "end": v(21.77, 175.05) * mm});
            skLineSegment(sketch, "E442", {"start": v(21.77, 175.05) * mm, "end": v(23.25, 175.28) * mm});
            skLineSegment(sketch, "E443", {"start": v(23.25, 175.28) * mm, "end": v(24.03, 175.4) * mm});
            skLineSegment(sketch, "E444", {"start": v(24.03, 175.4) * mm, "end": v(26.41, 175.46) * mm});
            skLineSegment(sketch, "E445", {"start": v(26.41, 175.46) * mm, "end": v(29.44, 175.03) * mm});
            skLineSegment(sketch, "E446", {"start": v(29.44, 175.03) * mm, "end": v(32.35, 174.05) * mm});
            skLineSegment(sketch, "E447", {"start": v(32.35, 174.05) * mm, "end": v(34.47, 172.97) * mm});
            skLineSegment(sketch, "E448", {"start": v(34.47, 172.97) * mm, "end": v(35.14, 172.54) * mm});
            skLineSegment(sketch, "E449", {"start": v(35.14, 172.54) * mm, "end": v(35.56, 172.19) * mm});
            skLineSegment(sketch, "E450", {"start": v(35.56, 172.19) * mm, "end": v(37.43, 170.2) * mm});
            skLineSegment(sketch, "E451", {"start": v(37.43, 170.2) * mm, "end": v(38.98, 167.97) * mm});
            skLineSegment(sketch, "E452", {"start": v(38.98, 167.97) * mm, "end": v(39.24, 167.47) * mm});
            skLineSegment(sketch, "E453", {"start": v(39.24, 167.47) * mm, "end": v(39.4, 167.18) * mm});
            skLineSegment(sketch, "E454", {"start": v(39.4, 167.18) * mm, "end": v(39.96, 166.33) * mm});
            skLineSegment(sketch, "E455", {"start": v(39.96, 166.33) * mm, "end": v(40.66, 165.83) * mm});
            skLineSegment(sketch, "E456", {"start": v(40.66, 165.83) * mm, "end": v(41.56, 165.86) * mm});
            skLineSegment(sketch, "E457", {"start": v(41.56, 165.86) * mm, "end": v(42.55, 166.23) * mm});
            skLineSegment(sketch, "E458", {"start": v(42.55, 166.23) * mm, "end": v(42.87, 166.37) * mm});
            skLineSegment(sketch, "E459", {"start": v(42.87, 166.37) * mm, "end": v(42.94, 166.4) * mm});
            skLineSegment(sketch, "E460", {"start": v(42.94, 166.4) * mm, "end": v(43.74, 166.68) * mm});
            skLineSegment(sketch, "E461", {"start": v(43.74, 166.68) * mm, "end": v(43.82, 166.7) * mm});
            skLineSegment(sketch, "E462", {"start": v(43.82, 166.7) * mm, "end": v(43.83, 166.7) * mm});
            skLineSegment(sketch, "E463", {"start": v(43.83, 166.7) * mm, "end": v(44, 166.64) * mm});
            skLineSegment(sketch, "E464", {"start": v(44, 166.64) * mm, "end": v(44.02, 166.63) * mm});
            skLineSegment(sketch, "E465", {"start": v(44.02, 166.63) * mm, "end": v(44.07, 166.56) * mm});
            skLineSegment(sketch, "E466", {"start": v(44.07, 166.56) * mm, "end": v(44.15, 166.31) * mm});
            skLineSegment(sketch, "E467", {"start": v(44.15, 166.31) * mm, "end": v(44.07, 166.06) * mm});
            skLineSegment(sketch, "E468", {"start": v(44.07, 166.06) * mm, "end": v(43.89, 165.84) * mm});
            skLineSegment(sketch, "E469", {"start": v(43.89, 165.84) * mm, "end": v(43.73, 165.69) * mm});
            skLineSegment(sketch, "E470", {"start": v(43.73, 165.69) * mm, "end": v(43.68, 165.63) * mm});
            skLineSegment(sketch, "E471", {"start": v(43.68, 165.63) * mm, "end": v(43.09, 164.97) * mm});
            skLineSegment(sketch, "E472", {"start": v(43.09, 164.97) * mm, "end": v(37.09, 158.37) * mm});
            skLineSegment(sketch, "E473", {"start": v(37.09, 158.37) * mm, "end": v(36.49, 157.71) * mm});
            skLineSegment(sketch, "E474", {"start": v(36.49, 157.71) * mm, "end": v(36.43, 157.65) * mm});
            skLineSegment(sketch, "E475", {"start": v(36.43, 157.65) * mm, "end": v(35.82, 157.05) * mm});
            skLineSegment(sketch, "E476", {"start": v(35.82, 157.05) * mm, "end": v(35.75, 157) * mm});
            skLineSegment(sketch, "E477", {"start": v(35.75, 157) * mm, "end": v(35.71, 156.96) * mm});
            skLineSegment(sketch, "E478", {"start": v(35.71, 156.96) * mm, "end": v(35.5, 156.85) * mm});
            skLineSegment(sketch, "E479", {"start": v(35.5, 156.85) * mm, "end": v(35.25, 156.85) * mm});
            skLineSegment(sketch, "E480", {"start": v(35.25, 156.85) * mm, "end": v(35.2, 156.88) * mm});
            skLineSegment(sketch, "E481", {"start": v(35.2, 156.88) * mm, "end": v(35.11, 156.92) * mm});
            skLineSegment(sketch, "E482", {"start": v(35.11, 156.92) * mm, "end": v(34.94, 157.18) * mm});
            skLineSegment(sketch, "E483", {"start": v(34.94, 157.18) * mm, "end": v(34.98, 157.5) * mm});
            skLineSegment(sketch, "E484", {"start": v(34.98, 157.5) * mm, "end": v(35.02, 157.56) * mm});
            skLineSegment(sketch, "E485", {"start": v(35.02, 157.56) * mm, "end": v(35.2, 157.94) * mm});
            skLineSegment(sketch, "E486", {"start": v(35.2, 157.94) * mm, "end": v(36.02, 159.93) * mm});
            skLineSegment(sketch, "E487", {"start": v(36.02, 159.93) * mm, "end": v(36.62, 161.98) * mm});
            skLineSegment(sketch, "E488", {"start": v(36.62, 161.98) * mm, "end": v(36.7, 162.4) * mm});
            skLineSegment(sketch, "E489", {"start": v(36.7, 162.4) * mm, "end": v(36.86, 163.22) * mm});
            skLineSegment(sketch, "E490", {"start": v(36.86, 163.22) * mm, "end": v(36.77, 165.78) * mm});
            skLineSegment(sketch, "E491", {"start": v(36.77, 165.78) * mm, "end": v(35.67, 168.65) * mm});
            skLineSegment(sketch, "E492", {"start": v(35.67, 168.65) * mm, "end": v(33.56, 170.79) * mm});
            skLineSegment(sketch, "E493", {"start": v(33.56, 170.79) * mm, "end": v(31.34, 171.83) * mm});
            skLineSegment(sketch, "E494", {"start": v(31.34, 171.83) * mm, "end": v(30.57, 171.98) * mm});
            skLineSegment(sketch, "E495", {"start": v(30.57, 171.98) * mm, "end": v(30.15, 172.06) * mm});
            skLineSegment(sketch, "E496", {"start": v(30.15, 172.06) * mm, "end": v(28.1, 172.05) * mm});
            skLineSegment(sketch, "E497", {"start": v(28.1, 172.05) * mm, "end": v(26.1, 171.61) * mm});
            skLineSegment(sketch, "E498", {"start": v(26.1, 171.61) * mm, "end": v(25.71, 171.48) * mm});
            skLineSegment(sketch, "E499", {"start": v(25.71, 171.48) * mm, "end": v(25.33, 171.36) * mm});
            skLineSegment(sketch, "E500", {"start": v(25.33, 171.36) * mm, "end": v(23.52, 170.58) * mm});
            skLineSegment(sketch, "E501", {"start": v(23.52, 170.58) * mm, "end": v(21.81, 169.6) * mm});
            skLineSegment(sketch, "E502", {"start": v(21.81, 169.6) * mm, "end": v(21.48, 169.38) * mm});
            skLineSegment(sketch, "E503", {"start": v(21.48, 169.38) * mm, "end": v(20.17, 168.48) * mm});
            skLineSegment(sketch, "E504", {"start": v(20.17, 168.48) * mm, "end": v(14.28, 163.26) * mm});
            skLineSegment(sketch, "E505", {"start": v(14.28, 163.26) * mm, "end": v(9.34, 157.15) * mm});
            skLineSegment(sketch, "E506", {"start": v(9.34, 157.15) * mm, "end": v(8.49, 155.8) * mm});
            skLineSegment(sketch, "E507", {"start": v(8.49, 155.8) * mm, "end": v(8.3, 155.5) * mm});
            skLineSegment(sketch, "E508", {"start": v(8.3, 155.5) * mm, "end": v(7.5, 154) * mm});
            skLineSegment(sketch, "E509", {"start": v(7.5, 154) * mm, "end": v(6.88, 152.4) * mm});
            skLineSegment(sketch, "E510", {"start": v(6.88, 152.4) * mm, "end": v(6.79, 152.06) * mm});
            skLineSegment(sketch, "E511", {"start": v(6.79, 152.06) * mm, "end": v(6.63, 151.5) * mm});
            skLineSegment(sketch, "E512", {"start": v(6.63, 151.5) * mm, "end": v(6.5, 149.73) * mm});
            skLineSegment(sketch, "E513", {"start": v(6.5, 149.73) * mm, "end": v(6.98, 147.64) * mm});
            skLineSegment(sketch, "E514", {"start": v(6.98, 147.64) * mm, "end": v(8.17, 145.86) * mm});
            skLineSegment(sketch, "E515", {"start": v(8.17, 145.86) * mm, "end": v(9.56, 144.73) * mm});
            skLineSegment(sketch, "E516", {"start": v(9.56, 144.73) * mm, "end": v(10.07, 144.45) * mm});
            skLineSegment(sketch, "E517", {"start": v(10.07, 144.45) * mm, "end": v(10.2, 144.39) * mm});
            skLineSegment(sketch, "E518", {"start": v(10.2, 144.39) * mm, "end": v(11.45, 143.84) * mm});
            skLineSegment(sketch, "E519", {"start": v(11.45, 143.84) * mm, "end": v(11.57, 143.78) * mm});
            skLineSegment(sketch, "E520", {"start": v(11.57, 143.78) * mm, "end": v(11.83, 143.67) * mm});
            skLineSegment(sketch, "E521", {"start": v(11.83, 143.67) * mm, "end": v(12.68, 143.45) * mm});
            skLineSegment(sketch, "E522", {"start": v(12.68, 143.45) * mm, "end": v(13.68, 143.46) * mm});
            skLineSegment(sketch, "E523", {"start": v(13.68, 143.46) * mm, "end": v(14.61, 143.88) * mm});
            skLineSegment(sketch, "E524", {"start": v(14.61, 143.88) * mm, "end": v(15.3, 144.5) * mm});
            skLineSegment(sketch, "E525", {"start": v(15.3, 144.5) * mm, "end": v(15.49, 144.74) * mm});
            skLineSegment(sketch, "E526", {"start": v(15.49, 144.74) * mm, "end": v(15.83, 145.19) * mm});
            skLineSegment(sketch, "E527", {"start": v(15.83, 145.19) * mm, "end": v(17.72, 147.3) * mm});
            skLineSegment(sketch, "E528", {"start": v(17.72, 147.3) * mm, "end": v(19.65, 149.37) * mm});
            skLineSegment(sketch, "E529", {"start": v(19.65, 149.37) * mm, "end": v(20.02, 149.8) * mm});
            skLineSegment(sketch, "E530", {"start": v(20.02, 149.8) * mm, "end": v(20.27, 150.1) * mm});
            skLineSegment(sketch, "E531", {"start": v(20.27, 150.1) * mm, "end": v(20.95, 151.02) * mm});
            skLineSegment(sketch, "E532", {"start": v(20.95, 151.02) * mm, "end": v(21.24, 151.98) * mm});
            skLineSegment(sketch, "E533", {"start": v(21.24, 151.98) * mm, "end": v(20.89, 152.92) * mm});
            skLineSegment(sketch, "E534", {"start": v(20.89, 152.92) * mm, "end": v(20.16, 153.82) * mm});
            skLineSegment(sketch, "E535", {"start": v(20.16, 153.82) * mm, "end": v(19.9, 154.1) * mm});
            skLineSegment(sketch, "E536", {"start": v(19.9, 154.1) * mm, "end": v(19.86, 154.14) * mm});
            skLineSegment(sketch, "E537", {"start": v(19.86, 154.14) * mm, "end": v(19.69, 154.58) * mm});
            skLineSegment(sketch, "E538", {"start": v(19.69, 154.58) * mm, "end": v(19.67, 154.62) * mm});
            skLineSegment(sketch, "E539", {"start": v(19.67, 154.62) * mm, "end": v(19.77, 154.73) * mm});
            skLineSegment(sketch, "E540", {"start": v(19.77, 154.73) * mm, "end": v(20.24, 154.92) * mm});
            skLineSegment(sketch, "E541", {"start": v(20.24, 154.92) * mm, "end": v(20.72, 154.79) * mm});
            skLineSegment(sketch, "E542", {"start": v(20.72, 154.79) * mm, "end": v(20.8, 154.73) * mm});
            skLineSegment(sketch, "E543", {"start": v(20.8, 154.73) * mm, "end": v(21.65, 154.2) * mm});
            skLineSegment(sketch, "E544", {"start": v(21.65, 154.2) * mm, "end": v(30.07, 148.9) * mm});
            skLineSegment(sketch, "E545", {"start": v(30.07, 148.9) * mm, "end": v(30.91, 148.37) * mm});
            skLineSegment(sketch, "E546", {"start": v(30.91, 148.37) * mm, "end": v(30.98, 148.34) * mm});
            skLineSegment(sketch, "E547", {"start": v(30.98, 148.34) * mm, "end": v(31.17, 148.2) * mm});
            skLineSegment(sketch, "E548", {"start": v(31.17, 148.2) * mm, "end": v(31.39, 148) * mm});
            skLineSegment(sketch, "E549", {"start": v(31.39, 148) * mm, "end": v(31.5, 147.74) * mm});
            skLineSegment(sketch, "E550", {"start": v(31.5, 147.74) * mm, "end": v(31.45, 147.5) * mm});
            skLineSegment(sketch, "E551", {"start": v(31.45, 147.5) * mm, "end": v(31.41, 147.42) * mm});
            skLineSegment(sketch, "E552", {"start": v(31.41, 147.42) * mm, "end": v(31.37, 147.35) * mm});
            skLineSegment(sketch, "E553", {"start": v(31.37, 147.35) * mm, "end": v(31.17, 147.18) * mm});
            skLineSegment(sketch, "E554", {"start": v(31.17, 147.18) * mm, "end": v(30.9, 147.14) * mm});
            skLineSegment(sketch, "E555", {"start": v(30.9, 147.14) * mm, "end": v(30.6, 147.24) * mm});
            skLineSegment(sketch, "E556", {"start": v(30.6, 147.24) * mm, "end": v(30.4, 147.34) * mm});
            skLineSegment(sketch, "E557", {"start": v(30.4, 147.34) * mm, "end": v(30.33, 147.37) * mm});
            skLineSegment(sketch, "E558", {"start": v(30.33, 147.37) * mm, "end": v(30.04, 147.5) * mm});
            skLineSegment(sketch, "E559", {"start": v(30.04, 147.5) * mm, "end": v(29.1, 147.72) * mm});
            skLineSegment(sketch, "E560", {"start": v(29.1, 147.72) * mm, "end": v(28, 147.6) * mm});
            skLineSegment(sketch, "E561", {"start": v(28, 147.6) * mm, "end": v(27, 147.1) * mm});
            skLineSegment(sketch, "E562", {"start": v(27, 147.1) * mm, "end": v(26.3, 146.51) * mm});
            skLineSegment(sketch, "E563", {"start": v(26.3, 146.51) * mm, "end": v(26.08, 146.3) * mm});
            skLineSegment(sketch, "E564", {"start": v(26.08, 146.3) * mm, "end": v(25.65, 145.84) * mm});
            skLineSegment(sketch, "E565", {"start": v(25.65, 145.84) * mm, "end": v(21.35, 141.16) * mm});
            skLineSegment(sketch, "E566", {"start": v(21.35, 141.16) * mm, "end": v(20.94, 140.68) * mm});
            skLineSegment(sketch, "E567", {"start": v(20.94, 140.68) * mm, "end": v(20.8, 140.52) * mm});
            skLineSegment(sketch, "E568", {"start": v(20.8, 140.52) * mm, "end": v(20.32, 140.1) * mm});
            skLineSegment(sketch, "E569", {"start": v(20.32, 140.1) * mm, "end": v(19.65, 139.79) * mm});
            skLineSegment(sketch, "E570", {"start": v(19.65, 139.79) * mm, "end": v(18.91, 139.67) * mm});
            skLineSegment(sketch, "E571", {"start": v(18.91, 139.67) * mm, "end": v(18.28, 139.68) * mm});
            skLineSegment(sketch, "E572", {"start": v(18.28, 139.68) * mm, "end": v(18.07, 139.7) * mm});
            skLineSegment(sketch, "E573", {"start": v(18.07, 139.7) * mm, "end": v(17.14, 139.78) * mm});
            skLineSegment(sketch, "E574", {"start": v(17.14, 139.78) * mm, "end": v(14.4, 140.36) * mm});
            skLineSegment(sketch, "E575", {"start": v(14.4, 140.36) * mm, "end": v(10.99, 141.61) * mm});
            skLineSegment(sketch, "E576", {"start": v(10.99, 141.61) * mm, "end": v(7.8, 143.34) * mm});
            skLineSegment(sketch, "E577", {"start": v(7.8, 143.34) * mm, "end": v(5.5, 144.9) * mm});
            skLineSegment(sketch, "E578", {"start": v(5.5, 144.9) * mm, "end": v(4.78, 145.46) * mm});
            skLineSegment(sketch, "E579", {"start": v(4.78, 145.46) * mm, "end": v(4.52, 145.66) * mm});
            skLineSegment(sketch, "E580", {"start": v(4.52, 145.66) * mm, "end": v(3.54, 146.91) * mm});
            skLineSegment(sketch, "E581", {"start": v(3.54, 146.91) * mm, "end": v(2.78, 148.35) * mm});
            skLineSegment(sketch, "E582", {"start": v(2.78, 148.35) * mm, "end": v(2.64, 148.64) * mm});
            skLineSegment(sketch, "E583", {"start": v(2.64, 148.64) * mm, "end": v(2.38, 149.16) * mm});
            skLineSegment(sketch, "E584", {"start": v(2.38, 149.16) * mm, "end": v(1.65, 151.87) * mm});
            skLineSegment(sketch, "E585", {"start": v(1.65, 151.87) * mm, "end": v(1.4, 154.68) * mm});
            skLineSegment(sketch, "E586", {"start": v(1.4, 154.68) * mm, "end": v(1.37, 155.24) * mm});
            skLineSegment(sketch, "E587", {"start": v(85, 129.93) * mm, "end": v(85, 130.2) * mm});
            skLineSegment(sketch, "E588", {"start": v(85, 130.2) * mm, "end": v(84.65, 131.37) * mm});
            skLineSegment(sketch, "E589", {"start": v(84.65, 131.37) * mm, "end": v(84.02, 132.39) * mm});
            skLineSegment(sketch, "E590", {"start": v(84.02, 132.39) * mm, "end": v(83.88, 132.59) * mm});
            skLineSegment(sketch, "E591", {"start": v(83.88, 132.59) * mm, "end": v(83.82, 132.68) * mm});
            skLineSegment(sketch, "E592", {"start": v(83.82, 132.68) * mm, "end": v(83.67, 133.15) * mm});
            skLineSegment(sketch, "E593", {"start": v(83.67, 133.15) * mm, "end": v(83.86, 133.59) * mm});
            skLineSegment(sketch, "E594", {"start": v(83.86, 133.59) * mm, "end": v(83.96, 133.66) * mm});
            skLineSegment(sketch, "E595", {"start": v(83.96, 133.66) * mm, "end": v(84.07, 133.74) * mm});
            skLineSegment(sketch, "E596", {"start": v(84.07, 133.74) * mm, "end": v(84.55, 133.74) * mm});
            skLineSegment(sketch, "E597", {"start": v(84.55, 133.74) * mm, "end": v(84.92, 133.4) * mm});
            skLineSegment(sketch, "E598", {"start": v(84.92, 133.4) * mm, "end": v(84.99, 133.33) * mm});
            skLineSegment(sketch, "E599", {"start": v(84.99, 133.33) * mm, "end": v(85.56, 132.62) * mm});
            skLineSegment(sketch, "E600", {"start": v(85.56, 132.62) * mm, "end": v(91.3, 125.59) * mm});
            skLineSegment(sketch, "E601", {"start": v(91.3, 125.59) * mm, "end": v(91.87, 124.88) * mm});
            skLineSegment(sketch, "E602", {"start": v(91.87, 124.88) * mm, "end": v(92.12, 124.58) * mm});
            skLineSegment(sketch, "E603", {"start": v(92.12, 124.58) * mm, "end": v(94.6, 121.51) * mm});
            skLineSegment(sketch, "E604", {"start": v(94.6, 121.51) * mm, "end": v(94.84, 121.2) * mm});
            skLineSegment(sketch, "E605", {"start": v(94.84, 121.2) * mm, "end": v(94.9, 121.13) * mm});
            skLineSegment(sketch, "E606", {"start": v(94.9, 121.13) * mm, "end": v(95.1, 120.9) * mm});
            skLineSegment(sketch, "E607", {"start": v(95.1, 120.9) * mm, "end": v(95.29, 120.57) * mm});
            skLineSegment(sketch, "E608", {"start": v(95.29, 120.57) * mm, "end": v(95.3, 120.21) * mm});
            skLineSegment(sketch, "E609", {"start": v(95.3, 120.21) * mm, "end": v(95.12, 119.9) * mm});
            skLineSegment(sketch, "E610", {"start": v(95.12, 119.9) * mm, "end": v(95.04, 119.8) * mm});
            skLineSegment(sketch, "E611", {"start": v(95.04, 119.8) * mm, "end": v(94.96, 119.73) * mm});
            skLineSegment(sketch, "E612", {"start": v(94.96, 119.73) * mm, "end": v(94.64, 119.55) * mm});
            skLineSegment(sketch, "E613", {"start": v(94.64, 119.55) * mm, "end": v(94.31, 119.56) * mm});
            skLineSegment(sketch, "E614", {"start": v(94.31, 119.56) * mm, "end": v(94, 119.76) * mm});
            skLineSegment(sketch, "E615", {"start": v(94, 119.76) * mm, "end": v(93.77, 119.97) * mm});
            skLineSegment(sketch, "E616", {"start": v(93.77, 119.97) * mm, "end": v(93.7, 120.04) * mm});
            skLineSegment(sketch, "E617", {"start": v(93.7, 120.04) * mm, "end": v(93.36, 120.34) * mm});
            skLineSegment(sketch, "E618", {"start": v(93.36, 120.34) * mm, "end": v(92.29, 121.17) * mm});
            skLineSegment(sketch, "E619", {"start": v(92.29, 121.17) * mm, "end": v(91.15, 121.58) * mm});
            skLineSegment(sketch, "E620", {"start": v(91.15, 121.58) * mm, "end": v(89.96, 121.28) * mm});
            skLineSegment(sketch, "E621", {"start": v(89.96, 121.28) * mm, "end": v(88.79, 120.55) * mm});
            skLineSegment(sketch, "E622", {"start": v(88.79, 120.55) * mm, "end": v(88.42, 120.27) * mm});
            skLineSegment(sketch, "E623", {"start": v(88.42, 120.27) * mm, "end": v(88.07, 120) * mm});
            skLineSegment(sketch, "E624", {"start": v(88.07, 120) * mm, "end": v(84.68, 117.15) * mm});
            skLineSegment(sketch, "E625", {"start": v(84.68, 117.15) * mm, "end": v(84.35, 116.86) * mm});
            skLineSegment(sketch, "E626", {"start": v(84.35, 116.86) * mm, "end": v(83.28, 115.9) * mm});
            skLineSegment(sketch, "E627", {"start": v(83.28, 115.9) * mm, "end": v(72.6, 106.33) * mm});
            skLineSegment(sketch, "E628", {"start": v(72.6, 106.33) * mm, "end": v(71.52, 105.37) * mm});
            skLineSegment(sketch, "E629", {"start": v(71.52, 105.37) * mm, "end": v(70.71, 104.66) * mm});
            skLineSegment(sketch, "E630", {"start": v(70.71, 104.66) * mm, "end": v(62.64, 97.55) * mm});
            skLineSegment(sketch, "E631", {"start": v(62.64, 97.55) * mm, "end": v(61.85, 96.82) * mm});
            skLineSegment(sketch, "E632", {"start": v(61.85, 96.82) * mm, "end": v(61.54, 96.54) * mm});
            skLineSegment(sketch, "E633", {"start": v(61.54, 96.54) * mm, "end": v(60.74, 95.56) * mm});
            skLineSegment(sketch, "E634", {"start": v(60.74, 95.56) * mm, "end": v(60.28, 94.33) * mm});
            skLineSegment(sketch, "E635", {"start": v(60.28, 94.33) * mm, "end": v(60.45, 93) * mm});
            skLineSegment(sketch, "E636", {"start": v(60.45, 93) * mm, "end": v(60.97, 91.79) * mm});
            skLineSegment(sketch, "E637", {"start": v(60.97, 91.79) * mm, "end": v(61.19, 91.4) * mm});
            skLineSegment(sketch, "E638", {"start": v(61.19, 91.4) * mm, "end": v(61.27, 91.28) * mm});
            skLineSegment(sketch, "E639", {"start": v(61.27, 91.28) * mm, "end": v(61.5, 90.67) * mm});
            skLineSegment(sketch, "E640", {"start": v(61.5, 90.67) * mm, "end": v(61.26, 90.1) * mm});
            skLineSegment(sketch, "E641", {"start": v(61.26, 90.1) * mm, "end": v(61.12, 90) * mm});
            skLineSegment(sketch, "E642", {"start": v(61.12, 90) * mm, "end": v(61.02, 89.92) * mm});
            skLineSegment(sketch, "E643", {"start": v(61.02, 89.92) * mm, "end": v(60.66, 89.8) * mm});
            skLineSegment(sketch, "E644", {"start": v(60.66, 89.8) * mm, "end": v(60.32, 89.93) * mm});
            skLineSegment(sketch, "E645", {"start": v(60.32, 89.93) * mm, "end": v(60.06, 90.22) * mm});
            skLineSegment(sketch, "E646", {"start": v(60.06, 90.22) * mm, "end": v(59.9, 90.46) * mm});
            skLineSegment(sketch, "E647", {"start": v(59.9, 90.46) * mm, "end": v(59.83, 90.54) * mm});
            skLineSegment(sketch, "E648", {"start": v(59.83, 90.54) * mm, "end": v(59.06, 91.51) * mm});
            skLineSegment(sketch, "E649", {"start": v(59.06, 91.51) * mm, "end": v(51.37, 101.26) * mm});
            skLineSegment(sketch, "E650", {"start": v(51.37, 101.26) * mm, "end": v(50.6, 102.24) * mm});
            skLineSegment(sketch, "E651", {"start": v(50.6, 102.24) * mm, "end": v(50.55, 102.3) * mm});
            skLineSegment(sketch, "E652", {"start": v(50.55, 102.3) * mm, "end": v(50.06, 103) * mm});
            skLineSegment(sketch, "E653", {"start": v(50.06, 103) * mm, "end": v(50.02, 103.08) * mm});
            skLineSegment(sketch, "E654", {"start": v(50.02, 103.08) * mm, "end": v(49.97, 103.17) * mm});
            skLineSegment(sketch, "E655", {"start": v(49.97, 103.17) * mm, "end": v(49.98, 103.58) * mm});
            skLineSegment(sketch, "E656", {"start": v(49.98, 103.58) * mm, "end": v(50.24, 103.9) * mm});
            skLineSegment(sketch, "E657", {"start": v(50.24, 103.9) * mm, "end": v(50.32, 103.96) * mm});
            skLineSegment(sketch, "E658", {"start": v(50.32, 103.96) * mm, "end": v(50.38, 104) * mm});
            skLineSegment(sketch, "E659", {"start": v(50.38, 104) * mm, "end": v(50.7, 104.05) * mm});
            skLineSegment(sketch, "E660", {"start": v(50.7, 104.05) * mm, "end": v(50.99, 103.9) * mm});
            skLineSegment(sketch, "E661", {"start": v(50.99, 103.9) * mm, "end": v(51.04, 103.85) * mm});
            skLineSegment(sketch, "E662", {"start": v(51.04, 103.85) * mm, "end": v(51.07, 103.83) * mm});
            skLineSegment(sketch, "E663", {"start": v(51.07, 103.83) * mm, "end": v(51.29, 103.57) * mm});
            skLineSegment(sketch, "E664", {"start": v(51.29, 103.57) * mm, "end": v(51.31, 103.54) * mm});
            skLineSegment(sketch, "E665", {"start": v(51.31, 103.54) * mm, "end": v(51.63, 103.24) * mm});
            skLineSegment(sketch, "E666", {"start": v(51.63, 103.24) * mm, "end": v(52.7, 102.43) * mm});
            skLineSegment(sketch, "E667", {"start": v(52.7, 102.43) * mm, "end": v(53.9, 102) * mm});
            skLineSegment(sketch, "E668", {"start": v(53.9, 102) * mm, "end": v(55.13, 102.3) * mm});
            skLineSegment(sketch, "E669", {"start": v(55.13, 102.3) * mm, "end": v(56.28, 103.04) * mm});
            skLineSegment(sketch, "E670", {"start": v(56.28, 103.04) * mm, "end": v(56.62, 103.32) * mm});
            skLineSegment(sketch, "E671", {"start": v(56.62, 103.32) * mm, "end": v(57.25, 103.83) * mm});
            skLineSegment(sketch, "E672", {"start": v(57.25, 103.83) * mm, "end": v(63.31, 109.12) * mm});
            skLineSegment(sketch, "E673", {"start": v(63.31, 109.12) * mm, "end": v(63.92, 109.65) * mm});
            skLineSegment(sketch, "E674", {"start": v(63.92, 109.65) * mm, "end": v(65.35, 110.9) * mm});
            skLineSegment(sketch, "E675", {"start": v(65.35, 110.9) * mm, "end": v(79.6, 123.5) * mm});
            skLineSegment(sketch, "E676", {"start": v(79.6, 123.5) * mm, "end": v(81.01, 124.76) * mm});
            skLineSegment(sketch, "E677", {"start": v(81.01, 124.76) * mm, "end": v(81.27, 124.99) * mm});
            skLineSegment(sketch, "E678", {"start": v(81.27, 124.99) * mm, "end": v(83.75, 127.36) * mm});
            skLineSegment(sketch, "E679", {"start": v(83.75, 127.36) * mm, "end": v(83.99, 127.6) * mm});
            skLineSegment(sketch, "E680", {"start": v(83.99, 127.6) * mm, "end": v(84.15, 127.76) * mm});
            skLineSegment(sketch, "E681", {"start": v(84.15, 127.76) * mm, "end": v(84.75, 128.67) * mm});
            skLineSegment(sketch, "E682", {"start": v(84.75, 128.67) * mm, "end": v(85, 129.7) * mm});
            skLineSegment(sketch, "E683", {"start": v(85, 129.7) * mm, "end": v(85, 129.93) * mm});
            skLineSegment(sketch, "E684", {"start": v(-131.23, -60.85) * mm, "end": v(-131.2, -60.86) * mm});
            skLineSegment(sketch, "E685", {"start": v(-131.2, -60.86) * mm, "end": v(-130.88, -61) * mm});
            skLineSegment(sketch, "E686", {"start": v(-130.88, -61) * mm, "end": v(-130.85, -61) * mm});
            skLineSegment(sketch, "E687", {"start": v(-130.85, -61) * mm, "end": v(-130.6, -61.04) * mm});
            skLineSegment(sketch, "E688", {"start": v(-130.6, -61.04) * mm, "end": v(-129.87, -61.14) * mm});
            skLineSegment(sketch, "E689", {"start": v(-129.87, -61.14) * mm, "end": v(-129.12, -61.21) * mm});
            skLineSegment(sketch, "E690", {"start": v(-129.12, -61.21) * mm, "end": v(-128.55, -61.18) * mm});
            skLineSegment(sketch, "E691", {"start": v(-128.55, -61.18) * mm, "end": v(-128.13, -61.02) * mm});
            skLineSegment(sketch, "E692", {"start": v(-128.13, -61.02) * mm, "end": v(-127.8, -60.7) * mm});
            skLineSegment(sketch, "E693", {"start": v(-127.8, -60.7) * mm, "end": v(-127.55, -60.2) * mm});
            skLineSegment(sketch, "E694", {"start": v(-127.55, -60.2) * mm, "end": v(-127.3, -59.5) * mm});
            skLineSegment(sketch, "E695", {"start": v(-127.3, -59.5) * mm, "end": v(-127.11, -58.8) * mm});
            skLineSegment(sketch, "E696", {"start": v(-127.11, -58.8) * mm, "end": v(-127.05, -58.57) * mm});
            skLineSegment(sketch, "E697", {"start": v(-127.05, -58.57) * mm, "end": v(-127.02, -58.47) * mm});
            skLineSegment(sketch, "E698", {"start": v(-127.02, -58.47) * mm, "end": v(-126.76, -57.48) * mm});
            skLineSegment(sketch, "E699", {"start": v(-126.76, -57.48) * mm, "end": v(-126.75, -57.38) * mm});
            skLineSegment(sketch, "E700", {"start": v(-126.75, -57.38) * mm, "end": v(-126.72, -57.18) * mm});
            skLineSegment(sketch, "E701", {"start": v(-126.72, -57.18) * mm, "end": v(-126.36, -56.58) * mm});
            skLineSegment(sketch, "E702", {"start": v(-126.36, -56.58) * mm, "end": v(-125.66, -56.43) * mm});
            skLineSegment(sketch, "E703", {"start": v(-125.66, -56.43) * mm, "end": v(-125.47, -56.46) * mm});
            skLineSegment(sketch, "E704", {"start": v(-125.47, -56.46) * mm, "end": v(-125.28, -56.49) * mm});
            skLineSegment(sketch, "E705", {"start": v(-125.28, -56.49) * mm, "end": v(-124.67, -56.86) * mm});
            skLineSegment(sketch, "E706", {"start": v(-124.67, -56.86) * mm, "end": v(-124.49, -57.54) * mm});
            skLineSegment(sketch, "E707", {"start": v(-124.49, -57.54) * mm, "end": v(-124.5, -57.73) * mm});
            skLineSegment(sketch, "E708", {"start": v(-124.5, -57.73) * mm, "end": v(-124.56, -58.34) * mm});
            skLineSegment(sketch, "E709", {"start": v(-124.56, -58.34) * mm, "end": v(-125.11, -64.47) * mm});
            skLineSegment(sketch, "E710", {"start": v(-125.11, -64.47) * mm, "end": v(-125.17, -65.09) * mm});
            skLineSegment(sketch, "E711", {"start": v(-125.17, -65.09) * mm, "end": v(-125.24, -65.85) * mm});
            skLineSegment(sketch, "E712", {"start": v(-125.24, -65.85) * mm, "end": v(-125.53, -69.68) * mm});
            skLineSegment(sketch, "E713", {"start": v(-125.53, -69.68) * mm, "end": v(-125.5, -73.52) * mm});
            skLineSegment(sketch, "E714", {"start": v(-125.5, -73.52) * mm, "end": v(-125.4, -74.3) * mm});
            skLineSegment(sketch, "E715", {"start": v(-125.4, -74.3) * mm, "end": v(-125.4, -74.39) * mm});
            skLineSegment(sketch, "E716", {"start": v(-125.4, -74.39) * mm, "end": v(-125.35, -74.68) * mm});
            skLineSegment(sketch, "E717", {"start": v(-125.35, -74.68) * mm, "end": v(-125.31, -75.09) * mm});
            skLineSegment(sketch, "E718", {"start": v(-125.31, -75.09) * mm, "end": v(-125.43, -75.45) * mm});
            skLineSegment(sketch, "E719", {"start": v(-125.43, -75.45) * mm, "end": v(-125.72, -75.65) * mm});
            skLineSegment(sketch, "E720", {"start": v(-125.72, -75.65) * mm, "end": v(-125.83, -75.67) * mm});
            skLineSegment(sketch, "E721", {"start": v(-125.83, -75.67) * mm, "end": v(-125.99, -75.7) * mm});
            skLineSegment(sketch, "E722", {"start": v(-125.99, -75.7) * mm, "end": v(-126.7, -75.52) * mm});
            skLineSegment(sketch, "E723", {"start": v(-126.7, -75.52) * mm, "end": v(-127.26, -74.98) * mm});
            skLineSegment(sketch, "E724", {"start": v(-127.26, -74.98) * mm, "end": v(-127.34, -74.84) * mm});
            skLineSegment(sketch, "E725", {"start": v(-127.34, -74.84) * mm, "end": v(-127.48, -74.6) * mm});
            skLineSegment(sketch, "E726", {"start": v(-127.48, -74.6) * mm, "end": v(-127.83, -73.38) * mm});
            skLineSegment(sketch, "E727", {"start": v(-127.83, -73.38) * mm, "end": v(-128.02, -72.11) * mm});
            skLineSegment(sketch, "E728", {"start": v(-128.02, -72.11) * mm, "end": v(-128.08, -71.87) * mm});
            skLineSegment(sketch, "E729", {"start": v(-128.08, -71.87) * mm, "end": v(-128.13, -71.64) * mm});
            skLineSegment(sketch, "E730", {"start": v(-128.13, -71.64) * mm, "end": v(-128.3, -70.96) * mm});
            skLineSegment(sketch, "E731", {"start": v(-128.3, -70.96) * mm, "end": v(-128.5, -70.27) * mm});
            skLineSegment(sketch, "E732", {"start": v(-128.5, -70.27) * mm, "end": v(-128.7, -69.76) * mm});
            skLineSegment(sketch, "E733", {"start": v(-128.7, -69.76) * mm, "end": v(-128.96, -69.38) * mm});
            skLineSegment(sketch, "E734", {"start": v(-128.96, -69.38) * mm, "end": v(-129.32, -69.1) * mm});
            skLineSegment(sketch, "E735", {"start": v(-129.32, -69.1) * mm, "end": v(-129.8, -68.9) * mm});
            skLineSegment(sketch, "E736", {"start": v(-129.8, -68.9) * mm, "end": v(-130.46, -68.71) * mm});
            skLineSegment(sketch, "E737", {"start": v(-130.46, -68.71) * mm, "end": v(-131.1, -68.57) * mm});
            skLineSegment(sketch, "E738", {"start": v(-131.1, -68.57) * mm, "end": v(-131.33, -68.52) * mm});
            skLineSegment(sketch, "E739", {"start": v(-131.33, -68.52) * mm, "end": v(-131.72, -68.43) * mm});
            skLineSegment(sketch, "E740", {"start": v(-131.72, -68.43) * mm, "end": v(-133.7, -67.93) * mm});
            skLineSegment(sketch, "E741", {"start": v(-133.7, -67.93) * mm, "end": v(-135.72, -67.59) * mm});
            skLineSegment(sketch, "E742", {"start": v(-135.72, -67.59) * mm, "end": v(-136.14, -67.58) * mm});
            skLineSegment(sketch, "E743", {"start": v(-136.14, -67.58) * mm, "end": v(-136.95, -67.34) * mm});
            skLineSegment(sketch, "E744", {"start": v(-136.95, -67.34) * mm, "end": v(-141.05, -66.49) * mm});
            skLineSegment(sketch, "E745", {"start": v(-141.05, -66.49) * mm, "end": v(-145.19, -65.8) * mm});
            skLineSegment(sketch, "E746", {"start": v(-145.19, -65.8) * mm, "end": v(-146.01, -65.63) * mm});
            skLineSegment(sketch, "E747", {"start": v(-146.01, -65.63) * mm, "end": v(-146.77, -65.48) * mm});
            skLineSegment(sketch, "E748", {"start": v(-146.77, -65.48) * mm, "end": v(-154.37, -64.18) * mm});
            skLineSegment(sketch, "E749", {"start": v(-154.37, -64.18) * mm, "end": v(-155.13, -64.05) * mm});
            skLineSegment(sketch, "E750", {"start": v(-155.13, -64.05) * mm, "end": v(-155.38, -64) * mm});
            skLineSegment(sketch, "E751", {"start": v(-155.38, -64) * mm, "end": v(-156.15, -63.94) * mm});
            skLineSegment(sketch, "E752", {"start": v(-156.15, -63.94) * mm, "end": v(-156.76, -64.1) * mm});
            skLineSegment(sketch, "E753", {"start": v(-156.76, -64.1) * mm, "end": v(-157.05, -64.65) * mm});
            skLineSegment(sketch, "E754", {"start": v(-157.05, -64.65) * mm, "end": v(-157.12, -65.4) * mm});
            skLineSegment(sketch, "E755", {"start": v(-157.12, -65.4) * mm, "end": v(-157.12, -65.65) * mm});
            skLineSegment(sketch, "E756", {"start": v(-157.12, -65.65) * mm, "end": v(-157.11, -66.16) * mm});
            skLineSegment(sketch, "E757", {"start": v(-157.11, -66.16) * mm, "end": v(-156.87, -71.3) * mm});
            skLineSegment(sketch, "E758", {"start": v(-156.87, -71.3) * mm, "end": v(-156.84, -71.81) * mm});
            skLineSegment(sketch, "E759", {"start": v(-156.84, -71.81) * mm, "end": v(-156.83, -72.05) * mm});
            skLineSegment(sketch, "E760", {"start": v(-156.83, -72.05) * mm, "end": v(-156.68, -72.75) * mm});
            skLineSegment(sketch, "E761", {"start": v(-156.68, -72.75) * mm, "end": v(-156.3, -73.58) * mm});
            skLineSegment(sketch, "E762", {"start": v(-156.3, -73.58) * mm, "end": v(-155.78, -74.32) * mm});
            skLineSegment(sketch, "E763", {"start": v(-155.78, -74.32) * mm, "end": v(-155.3, -74.84) * mm});
            skLineSegment(sketch, "E764", {"start": v(-155.3, -74.84) * mm, "end": v(-155.14, -75) * mm});
            skLineSegment(sketch, "E765", {"start": v(-155.14, -75) * mm, "end": v(-154.9, -75.24) * mm});
            skLineSegment(sketch, "E766", {"start": v(-154.9, -75.24) * mm, "end": v(-152.38, -77.57) * mm});
            skLineSegment(sketch, "E767", {"start": v(-152.38, -77.57) * mm, "end": v(-152.13, -77.8) * mm});
            skLineSegment(sketch, "E768", {"start": v(-152.13, -77.8) * mm, "end": v(-152.02, -77.9) * mm});
            skLineSegment(sketch, "E769", {"start": v(-152.02, -77.9) * mm, "end": v(-151.67, -78.41) * mm});
            skLineSegment(sketch, "E770", {"start": v(-151.67, -78.41) * mm, "end": v(-151.76, -79.03) * mm});
            skLineSegment(sketch, "E771", {"start": v(-151.76, -79.03) * mm, "end": v(-151.87, -79.19) * mm});
            skLineSegment(sketch, "E772", {"start": v(-151.87, -79.19) * mm, "end": v(-151.98, -79.34) * mm});
            skLineSegment(sketch, "E773", {"start": v(-151.98, -79.34) * mm, "end": v(-152.51, -79.76) * mm});
            skLineSegment(sketch, "E774", {"start": v(-152.51, -79.76) * mm, "end": v(-153.2, -79.7) * mm});
            skLineSegment(sketch, "E775", {"start": v(-153.2, -79.7) * mm, "end": v(-153.38, -79.62) * mm});
            skLineSegment(sketch, "E776", {"start": v(-153.38, -79.62) * mm, "end": v(-153.94, -79.35) * mm});
            skLineSegment(sketch, "E777", {"start": v(-153.94, -79.35) * mm, "end": v(-156.8, -78.06) * mm});
            skLineSegment(sketch, "E778", {"start": v(-156.8, -78.06) * mm, "end": v(-159.73, -77) * mm});
            skLineSegment(sketch, "E779", {"start": v(-159.73, -77) * mm, "end": v(-160.34, -76.83) * mm});
            skLineSegment(sketch, "E780", {"start": v(-160.34, -76.83) * mm, "end": v(-160.47, -76.8) * mm});
            skLineSegment(sketch, "E781", {"start": v(-160.47, -76.8) * mm, "end": v(-161.05, -76.48) * mm});
            skLineSegment(sketch, "E782", {"start": v(-161.05, -76.48) * mm, "end": v(-161.57, -76.04) * mm});
            skLineSegment(sketch, "E783", {"start": v(-161.57, -76.04) * mm, "end": v(-161.66, -75.94) * mm});
            skLineSegment(sketch, "E784", {"start": v(-161.66, -75.94) * mm, "end": v(-161.8, -75.8) * mm});
            skLineSegment(sketch, "E785", {"start": v(-161.8, -75.8) * mm, "end": v(-162.13, -75.3) * mm});
            skLineSegment(sketch, "E786", {"start": v(-162.13, -75.3) * mm, "end": v(-162.26, -74.67) * mm});
            skLineSegment(sketch, "E787", {"start": v(-162.26, -74.67) * mm, "end": v(-162.03, -74.1) * mm});
            skLineSegment(sketch, "E788", {"start": v(-162.03, -74.1) * mm, "end": v(-161.6, -73.77) * mm});
            skLineSegment(sketch, "E789", {"start": v(-161.6, -73.77) * mm, "end": v(-161.44, -73.7) * mm});
            skLineSegment(sketch, "E790", {"start": v(-161.44, -73.7) * mm, "end": v(-161.23, -73.62) * mm});
            skLineSegment(sketch, "E791", {"start": v(-161.23, -73.62) * mm, "end": v(-160.65, -73.24) * mm});
            skLineSegment(sketch, "E792", {"start": v(-160.65, -73.24) * mm, "end": v(-160.22, -72.64) * mm});
            skLineSegment(sketch, "E793", {"start": v(-160.22, -72.64) * mm, "end": v(-160.06, -71.92) * mm});
            skLineSegment(sketch, "E794", {"start": v(-160.06, -71.92) * mm, "end": v(-160.04, -71.3) * mm});
            skLineSegment(sketch, "E795", {"start": v(-160.04, -71.3) * mm, "end": v(-160.05, -71.1) * mm});
            skLineSegment(sketch, "E796", {"start": v(-160.05, -71.1) * mm, "end": v(-160.1, -69.81) * mm});
            skLineSegment(sketch, "E797", {"start": v(-160.1, -69.81) * mm, "end": v(-160.52, -56.96) * mm});
            skLineSegment(sketch, "E798", {"start": v(-160.52, -56.96) * mm, "end": v(-160.56, -55.68) * mm});
            skLineSegment(sketch, "E799", {"start": v(-160.56, -55.68) * mm, "end": v(-160.59, -54.94) * mm});
            skLineSegment(sketch, "E800", {"start": v(-160.59, -54.94) * mm, "end": v(-160.86, -47.57) * mm});
            skLineSegment(sketch, "E801", {"start": v(-160.86, -47.57) * mm, "end": v(-160.88, -46.83) * mm});
            skLineSegment(sketch, "E802", {"start": v(-160.88, -46.83) * mm, "end": v(-160.89, -46.63) * mm});
            skLineSegment(sketch, "E803", {"start": v(-160.89, -46.63) * mm, "end": v(-161.1, -44.59) * mm});
            skLineSegment(sketch, "E804", {"start": v(-161.1, -44.59) * mm, "end": v(-161.13, -44.38) * mm});
            skLineSegment(sketch, "E805", {"start": v(-161.13, -44.38) * mm, "end": v(-161.16, -44.18) * mm});
            skLineSegment(sketch, "E806", {"start": v(-161.16, -44.18) * mm, "end": v(-161.48, -43.3) * mm});
            skLineSegment(sketch, "E807", {"start": v(-161.48, -43.3) * mm, "end": v(-162.1, -42.66) * mm});
            skLineSegment(sketch, "E808", {"start": v(-162.1, -42.66) * mm, "end": v(-162.29, -42.58) * mm});
            skLineSegment(sketch, "E809", {"start": v(-162.29, -42.58) * mm, "end": v(-162.51, -42.48) * mm});
            skLineSegment(sketch, "E810", {"start": v(-162.51, -42.48) * mm, "end": v(-163.12, -42.03) * mm});
            skLineSegment(sketch, "E811", {"start": v(-163.12, -42.03) * mm, "end": v(-163.6, -41.33) * mm});
            skLineSegment(sketch, "E812", {"start": v(-163.6, -41.33) * mm, "end": v(-163.76, -40.47) * mm});
            skLineSegment(sketch, "E813", {"start": v(-163.76, -40.47) * mm, "end": v(-163.7, -39.7) * mm});
            skLineSegment(sketch, "E814", {"start": v(-163.7, -39.7) * mm, "end": v(-163.65, -39.45) * mm});
            skLineSegment(sketch, "E815", {"start": v(-163.65, -39.45) * mm, "end": v(-163.24, -39.46) * mm});
            skLineSegment(sketch, "E816", {"start": v(-163.24, -39.46) * mm, "end": v(-161.31, -39.81) * mm});
            skLineSegment(sketch, "E817", {"start": v(-161.31, -39.81) * mm, "end": v(-159.43, -40.3) * mm});
            skLineSegment(sketch, "E818", {"start": v(-159.43, -40.3) * mm, "end": v(-159.06, -40.39) * mm});
            skLineSegment(sketch, "E819", {"start": v(-159.06, -40.39) * mm, "end": v(-158.54, -40.5) * mm});
            skLineSegment(sketch, "E820", {"start": v(-158.54, -40.5) * mm, "end": v(-153.37, -41.72) * mm});
            skLineSegment(sketch, "E821", {"start": v(-153.37, -41.72) * mm, "end": v(-152.85, -41.83) * mm});
            skLineSegment(sketch, "E822", {"start": v(-152.85, -41.83) * mm, "end": v(-152.67, -41.86) * mm});
            skLineSegment(sketch, "E823", {"start": v(-152.67, -41.86) * mm, "end": v(-152.17, -42.06) * mm});
            skLineSegment(sketch, "E824", {"start": v(-152.17, -42.06) * mm, "end": v(-151.68, -42.43) * mm});
            skLineSegment(sketch, "E825", {"start": v(-151.68, -42.43) * mm, "end": v(-151.35, -42.94) * mm});
            skLineSegment(sketch, "E826", {"start": v(-151.35, -42.94) * mm, "end": v(-151.17, -43.42) * mm});
            skLineSegment(sketch, "E827", {"start": v(-151.17, -43.42) * mm, "end": v(-151.12, -43.58) * mm});
            skLineSegment(sketch, "E828", {"start": v(-151.12, -43.58) * mm, "end": v(-151.08, -43.74) * mm});
            skLineSegment(sketch, "E829", {"start": v(-151.08, -43.74) * mm, "end": v(-151.12, -44.38) * mm});
            skLineSegment(sketch, "E830", {"start": v(-151.12, -44.38) * mm, "end": v(-151.58, -44.8) * mm});
            skLineSegment(sketch, "E831", {"start": v(-151.58, -44.8) * mm, "end": v(-151.74, -44.85) * mm});
            skLineSegment(sketch, "E832", {"start": v(-151.74, -44.85) * mm, "end": v(-152.06, -44.94) * mm});
            skLineSegment(sketch, "E833", {"start": v(-152.06, -44.94) * mm, "end": v(-153.6, -45.4) * mm});
            skLineSegment(sketch, "E834", {"start": v(-153.6, -45.4) * mm, "end": v(-155.2, -45.76) * mm});
            skLineSegment(sketch, "E835", {"start": v(-155.2, -45.76) * mm, "end": v(-155.52, -45.8) * mm});
            skLineSegment(sketch, "E836", {"start": v(-155.52, -45.8) * mm, "end": v(-155.78, -45.83) * mm});
            skLineSegment(sketch, "E837", {"start": v(-155.78, -45.83) * mm, "end": v(-156.56, -46) * mm});
            skLineSegment(sketch, "E838", {"start": v(-156.56, -46) * mm, "end": v(-157.16, -46.35) * mm});
            skLineSegment(sketch, "E839", {"start": v(-157.16, -46.35) * mm, "end": v(-157.45, -47) * mm});
            skLineSegment(sketch, "E840", {"start": v(-157.45, -47) * mm, "end": v(-157.55, -47.77) * mm});
            skLineSegment(sketch, "E841", {"start": v(-157.55, -47.77) * mm, "end": v(-157.56, -48.03) * mm});
            skLineSegment(sketch, "E842", {"start": v(-157.56, -48.03) * mm, "end": v(-157.59, -48.58) * mm});
            skLineSegment(sketch, "E843", {"start": v(-157.59, -48.58) * mm, "end": v(-157.45, -51.32) * mm});
            skLineSegment(sketch, "E844", {"start": v(-157.45, -51.32) * mm, "end": v(-157.21, -54.05) * mm});
            skLineSegment(sketch, "E845", {"start": v(-157.21, -54.05) * mm, "end": v(-157.19, -54.6) * mm});
            skLineSegment(sketch, "E846", {"start": v(-157.19, -54.6) * mm, "end": v(-157.18, -54.72) * mm});
            skLineSegment(sketch, "E847", {"start": v(-157.18, -54.72) * mm, "end": v(-157.07, -55.1) * mm});
            skLineSegment(sketch, "E848", {"start": v(-157.07, -55.1) * mm, "end": v(-156.8, -55.4) * mm});
            skLineSegment(sketch, "E849", {"start": v(-156.8, -55.4) * mm, "end": v(-156.43, -55.56) * mm});
            skLineSegment(sketch, "E850", {"start": v(-156.43, -55.56) * mm, "end": v(-156.1, -55.64) * mm});
            skLineSegment(sketch, "E851", {"start": v(-156.1, -55.64) * mm, "end": v(-155.98, -55.67) * mm});
            skLineSegment(sketch, "E852", {"start": v(-155.98, -55.67) * mm, "end": v(-154.53, -55.97) * mm});
            skLineSegment(sketch, "E853", {"start": v(-154.53, -55.97) * mm, "end": v(-140.12, -59.02) * mm});
            skLineSegment(sketch, "E854", {"start": v(-140.12, -59.02) * mm, "end": v(-138.68, -59.32) * mm});
            skLineSegment(sketch, "E855", {"start": v(-138.68, -59.32) * mm, "end": v(-138.06, -59.45) * mm});
            skLineSegment(sketch, "E856", {"start": v(-138.06, -59.45) * mm, "end": v(-131.85, -60.72) * mm});
            skLineSegment(sketch, "E857", {"start": v(-131.85, -60.72) * mm, "end": v(-131.23, -60.85) * mm});
            skLineSegment(sketch, "E858", {"start": v(-151.99, 21.92) * mm, "end": v(-151.9, 22) * mm});
            skLineSegment(sketch, "E859", {"start": v(-151.9, 22) * mm, "end": v(-151.43, 22.15) * mm});
            skLineSegment(sketch, "E860", {"start": v(-151.43, 22.15) * mm, "end": v(-150.93, 22.09) * mm});
            skLineSegment(sketch, "E861", {"start": v(-150.93, 22.09) * mm, "end": v(-150.83, 22.06) * mm});
            skLineSegment(sketch, "E862", {"start": v(-150.83, 22.06) * mm, "end": v(-150.07, 21.84) * mm});
            skLineSegment(sketch, "E863", {"start": v(-150.07, 21.84) * mm, "end": v(-142.51, 19.63) * mm});
            skLineSegment(sketch, "E864", {"start": v(-142.51, 19.63) * mm, "end": v(-141.76, 19.4) * mm});
            skLineSegment(sketch, "E865", {"start": v(-141.76, 19.4) * mm, "end": v(-141.72, 19.4) * mm});
            skLineSegment(sketch, "E866", {"start": v(-141.72, 19.4) * mm, "end": v(-141.4, 19.31) * mm});
            skLineSegment(sketch, "E867", {"start": v(-141.4, 19.31) * mm, "end": v(-141.36, 19.3) * mm});
            skLineSegment(sketch, "E868", {"start": v(-141.36, 19.3) * mm, "end": v(-141.27, 19.28) * mm});
            skLineSegment(sketch, "E869", {"start": v(-141.27, 19.28) * mm, "end": v(-140.9, 19.08) * mm});
            skLineSegment(sketch, "E870", {"start": v(-140.9, 19.08) * mm, "end": v(-140.73, 18.72) * mm});
            skLineSegment(sketch, "E871", {"start": v(-140.73, 18.72) * mm, "end": v(-140.74, 18.62) * mm});
            skLineSegment(sketch, "E872", {"start": v(-140.74, 18.62) * mm, "end": v(-140.75, 18.51) * mm});
            skLineSegment(sketch, "E873", {"start": v(-140.75, 18.51) * mm, "end": v(-141, 18.2) * mm});
            skLineSegment(sketch, "E874", {"start": v(-141, 18.2) * mm, "end": v(-141.4, 18.1) * mm});
            skLineSegment(sketch, "E875", {"start": v(-141.4, 18.1) * mm, "end": v(-141.5, 18.11) * mm});
            skLineSegment(sketch, "E876", {"start": v(-141.5, 18.11) * mm, "end": v(-141.7, 18.13) * mm});
            skLineSegment(sketch, "E877", {"start": v(-141.7, 18.13) * mm, "end": v(-143.74, 18.33) * mm});
            skLineSegment(sketch, "E878", {"start": v(-143.74, 18.33) * mm, "end": v(-143.94, 18.35) * mm});
            skLineSegment(sketch, "E879", {"start": v(-143.94, 18.35) * mm, "end": v(-144.3, 18.39) * mm});
            skLineSegment(sketch, "E880", {"start": v(-144.3, 18.39) * mm, "end": v(-145.98, 18.35) * mm});
            skLineSegment(sketch, "E881", {"start": v(-145.98, 18.35) * mm, "end": v(-147.64, 17.95) * mm});
            skLineSegment(sketch, "E882", {"start": v(-147.64, 17.95) * mm, "end": v(-147.96, 17.8) * mm});
            skLineSegment(sketch, "E883", {"start": v(-147.96, 17.8) * mm, "end": v(-148.29, 17.66) * mm});
            skLineSegment(sketch, "E884", {"start": v(-148.29, 17.66) * mm, "end": v(-149.2, 17.09) * mm});
            skLineSegment(sketch, "E885", {"start": v(-149.2, 17.09) * mm, "end": v(-150.13, 16.16) * mm});
            skLineSegment(sketch, "E886", {"start": v(-150.13, 16.16) * mm, "end": v(-150.74, 15) * mm});
            skLineSegment(sketch, "E887", {"start": v(-150.74, 15) * mm, "end": v(-151, 13.94) * mm});
            skLineSegment(sketch, "E888", {"start": v(-151, 13.94) * mm, "end": v(-151.03, 13.58) * mm});
            skLineSegment(sketch, "E889", {"start": v(-151.03, 13.58) * mm, "end": v(-151.05, 13.37) * mm});
            skLineSegment(sketch, "E890", {"start": v(-151.05, 13.37) * mm, "end": v(-151.1, 12.77) * mm});
            skLineSegment(sketch, "E891", {"start": v(-151.1, 12.77) * mm, "end": v(-151.13, 12.15) * mm});
            skLineSegment(sketch, "E892", {"start": v(-151.13, 12.15) * mm, "end": v(-151.09, 11.7) * mm});
            skLineSegment(sketch, "E893", {"start": v(-151.09, 11.7) * mm, "end": v(-150.96, 11.35) * mm});
            skLineSegment(sketch, "E894", {"start": v(-150.96, 11.35) * mm, "end": v(-150.7, 11.08) * mm});
            skLineSegment(sketch, "E895", {"start": v(-150.7, 11.08) * mm, "end": v(-150.3, 10.87) * mm});
            skLineSegment(sketch, "E896", {"start": v(-150.3, 10.87) * mm, "end": v(-149.74, 10.65) * mm});
            skLineSegment(sketch, "E897", {"start": v(-149.74, 10.65) * mm, "end": v(-149.16, 10.47) * mm});
            skLineSegment(sketch, "E898", {"start": v(-149.16, 10.47) * mm, "end": v(-148.96, 10.4) * mm});
            skLineSegment(sketch, "E899", {"start": v(-148.96, 10.4) * mm, "end": v(-146.58, 9.67) * mm});
            skLineSegment(sketch, "E900", {"start": v(-146.58, 9.67) * mm, "end": v(-122.74, 2.29) * mm});
            skLineSegment(sketch, "E901", {"start": v(-122.74, 2.29) * mm, "end": v(-120.36, 1.55) * mm});
            skLineSegment(sketch, "E902", {"start": v(-120.36, 1.55) * mm, "end": v(-120, 1.44) * mm});
            skLineSegment(sketch, "E903", {"start": v(-120, 1.44) * mm, "end": v(-118.24, 0.8) * mm});
            skLineSegment(sketch, "E904", {"start": v(-118.24, 0.8) * mm, "end": v(-116.43, 0.32) * mm});
            skLineSegment(sketch, "E905", {"start": v(-116.43, 0.32) * mm, "end": v(-116.05, 0.28) * mm});
            skLineSegment(sketch, "E906", {"start": v(-116.05, 0.28) * mm, "end": v(-115.7, 0.25) * mm});
            skLineSegment(sketch, "E907", {"start": v(-115.7, 0.25) * mm, "end": v(-114.67, 0.26) * mm});
            skLineSegment(sketch, "E908", {"start": v(-114.67, 0.26) * mm, "end": v(-113.65, 0.58) * mm});
            skLineSegment(sketch, "E909", {"start": v(-113.65, 0.58) * mm, "end": v(-112.88, 1.31) * mm});
            skLineSegment(sketch, "E910", {"start": v(-112.88, 1.31) * mm, "end": v(-112.37, 2.22) * mm});
            skLineSegment(sketch, "E911", {"start": v(-112.37, 2.22) * mm, "end": v(-112.24, 2.53) * mm});
            skLineSegment(sketch, "E912", {"start": v(-112.24, 2.53) * mm, "end": v(-112.21, 2.6) * mm});
            skLineSegment(sketch, "E913", {"start": v(-112.21, 2.6) * mm, "end": v(-111.98, 3.24) * mm});
            skLineSegment(sketch, "E914", {"start": v(-111.98, 3.24) * mm, "end": v(-111.95, 3.3) * mm});
            skLineSegment(sketch, "E915", {"start": v(-111.95, 3.3) * mm, "end": v(-111.9, 3.4) * mm});
            skLineSegment(sketch, "E916", {"start": v(-111.9, 3.4) * mm, "end": v(-111.57, 3.6) * mm});
            skLineSegment(sketch, "E917", {"start": v(-111.57, 3.6) * mm, "end": v(-111.16, 3.57) * mm});
            skLineSegment(sketch, "E918", {"start": v(-111.16, 3.57) * mm, "end": v(-111.07, 3.54) * mm});
            skLineSegment(sketch, "E919", {"start": v(-111.07, 3.54) * mm, "end": v(-111, 3.51) * mm});
            skLineSegment(sketch, "E920", {"start": v(-111, 3.51) * mm, "end": v(-110.74, 3.3) * mm});
            skLineSegment(sketch, "E921", {"start": v(-110.74, 3.3) * mm, "end": v(-110.64, 2.99) * mm});
            skLineSegment(sketch, "E922", {"start": v(-110.64, 2.99) * mm, "end": v(-110.65, 2.92) * mm});
            skLineSegment(sketch, "E923", {"start": v(-110.65, 2.92) * mm, "end": v(-110.67, 2.82) * mm});
            skLineSegment(sketch, "E924", {"start": v(-110.67, 2.82) * mm, "end": v(-110.96, 1.83) * mm});
            skLineSegment(sketch, "E925", {"start": v(-110.96, 1.83) * mm, "end": v(-110.99, 1.73) * mm});
            skLineSegment(sketch, "E926", {"start": v(-110.99, 1.73) * mm, "end": v(-111.34, 0.6) * mm});
            skLineSegment(sketch, "E927", {"start": v(-111.34, 0.6) * mm, "end": v(-114.87, -10.65) * mm});
            skLineSegment(sketch, "E928", {"start": v(-114.87, -10.65) * mm, "end": v(-115.22, -11.77) * mm});
            skLineSegment(sketch, "E929", {"start": v(-115.22, -11.77) * mm, "end": v(-115.25, -11.85) * mm});
            skLineSegment(sketch, "E930", {"start": v(-115.25, -11.85) * mm, "end": v(-115.32, -12.1) * mm});
            skLineSegment(sketch, "E931", {"start": v(-115.32, -12.1) * mm, "end": v(-115.46, -12.42) * mm});
            skLineSegment(sketch, "E932", {"start": v(-115.46, -12.42) * mm, "end": v(-115.7, -12.62) * mm});
            skLineSegment(sketch, "E933", {"start": v(-115.7, -12.62) * mm, "end": v(-116.03, -12.63) * mm});
            skLineSegment(sketch, "E934", {"start": v(-116.03, -12.63) * mm, "end": v(-116.13, -12.6) * mm});
            skLineSegment(sketch, "E935", {"start": v(-116.13, -12.6) * mm, "end": v(-116.22, -12.57) * mm});
            skLineSegment(sketch, "E936", {"start": v(-116.22, -12.57) * mm, "end": v(-116.48, -12.4) * mm});
            skLineSegment(sketch, "E937", {"start": v(-116.48, -12.4) * mm, "end": v(-116.58, -12.13) * mm});
            skLineSegment(sketch, "E938", {"start": v(-116.58, -12.13) * mm, "end": v(-116.55, -11.8) * mm});
            skLineSegment(sketch, "E939", {"start": v(-116.55, -11.8) * mm, "end": v(-116.5, -11.53) * mm});
            skLineSegment(sketch, "E940", {"start": v(-116.5, -11.53) * mm, "end": v(-116.48, -11.44) * mm});
            skLineSegment(sketch, "E941", {"start": v(-116.48, -11.44) * mm, "end": v(-116.43, -11.06) * mm});
            skLineSegment(sketch, "E942", {"start": v(-116.43, -11.06) * mm, "end": v(-116.41, -9.9) * mm});
            skLineSegment(sketch, "E943", {"start": v(-116.41, -9.9) * mm, "end": v(-116.76, -8.79) * mm});
            skLineSegment(sketch, "E944", {"start": v(-116.76, -8.79) * mm, "end": v(-117.6, -7.96) * mm});
            skLineSegment(sketch, "E945", {"start": v(-117.6, -7.96) * mm, "end": v(-118.68, -7.4) * mm});
            skLineSegment(sketch, "E946", {"start": v(-118.68, -7.4) * mm, "end": v(-119.05, -7.26) * mm});
            skLineSegment(sketch, "E947", {"start": v(-119.05, -7.26) * mm, "end": v(-120.62, -6.65) * mm});
            skLineSegment(sketch, "E948", {"start": v(-120.62, -6.65) * mm, "end": v(-128.57, -3.96) * mm});
            skLineSegment(sketch, "E949", {"start": v(-128.57, -3.96) * mm, "end": v(-136.57, -1.45) * mm});
            skLineSegment(sketch, "E950", {"start": v(-136.57, -1.45) * mm, "end": v(-138.16, -0.92) * mm});
            skLineSegment(sketch, "E951", {"start": v(-138.16, -0.92) * mm, "end": v(-139.26, -0.55) * mm});
            skLineSegment(sketch, "E952", {"start": v(-139.26, -0.55) * mm, "end": v(-150.35, 2.99) * mm});
            skLineSegment(sketch, "E953", {"start": v(-150.35, 2.99) * mm, "end": v(-151.46, 3.34) * mm});
            skLineSegment(sketch, "E954", {"start": v(-151.46, 3.34) * mm, "end": v(-151.65, 3.4) * mm});
            skLineSegment(sketch, "E955", {"start": v(-151.65, 3.4) * mm, "end": v(-152.22, 3.55) * mm});
            skLineSegment(sketch, "E956", {"start": v(-152.22, 3.55) * mm, "end": v(-152.64, 3.52) * mm});
            skLineSegment(sketch, "E957", {"start": v(-152.64, 3.52) * mm, "end": v(-152.86, 3.18) * mm});
            skLineSegment(sketch, "E958", {"start": v(-152.86, 3.18) * mm, "end": v(-153, 2.62) * mm});
            skLineSegment(sketch, "E959", {"start": v(-153, 2.62) * mm, "end": v(-153.04, 2.44) * mm});
            skLineSegment(sketch, "E960", {"start": v(-153.04, 2.44) * mm, "end": v(-153.07, 2.3) * mm});
            skLineSegment(sketch, "E961", {"start": v(-153.07, 2.3) * mm, "end": v(-153.39, 0.98) * mm});
            skLineSegment(sketch, "E962", {"start": v(-153.39, 0.98) * mm, "end": v(-153.4, 0.84) * mm});
            skLineSegment(sketch, "E963", {"start": v(-153.4, 0.84) * mm, "end": v(-153.46, 0.52) * mm});
            skLineSegment(sketch, "E964", {"start": v(-153.46, 0.52) * mm, "end": v(-153.39, -0.97) * mm});
            skLineSegment(sketch, "E965", {"start": v(-153.39, -0.97) * mm, "end": v(-152.8, -2.37) * mm});
            skLineSegment(sketch, "E966", {"start": v(-152.8, -2.37) * mm, "end": v(-152.6, -2.64) * mm});
            skLineSegment(sketch, "E967", {"start": v(-152.6, -2.64) * mm, "end": v(-152.26, -3.1) * mm});
            skLineSegment(sketch, "E968", {"start": v(-152.26, -3.1) * mm, "end": v(-150.36, -5.05) * mm});
            skLineSegment(sketch, "E969", {"start": v(-150.36, -5.05) * mm, "end": v(-148.12, -6.59) * mm});
            skLineSegment(sketch, "E970", {"start": v(-148.12, -6.59) * mm, "end": v(-147.62, -6.83) * mm});
            skLineSegment(sketch, "E971", {"start": v(-147.62, -6.83) * mm, "end": v(-147.52, -6.88) * mm});
            skLineSegment(sketch, "E972", {"start": v(-147.52, -6.88) * mm, "end": v(-147.2, -7) * mm});
            skLineSegment(sketch, "E973", {"start": v(-147.2, -7) * mm, "end": v(-146.8, -7.18) * mm});
            skLineSegment(sketch, "E974", {"start": v(-146.8, -7.18) * mm, "end": v(-146.41, -7.45) * mm});
            skLineSegment(sketch, "E975", {"start": v(-146.41, -7.45) * mm, "end": v(-146.18, -7.78) * mm});
            skLineSegment(sketch, "E976", {"start": v(-146.18, -7.78) * mm, "end": v(-146.13, -7.9) * mm});
            skLineSegment(sketch, "E977", {"start": v(-146.13, -7.9) * mm, "end": v(-146.25, -8) * mm});
            skLineSegment(sketch, "E978", {"start": v(-146.25, -8) * mm, "end": v(-146.74, -8.12) * mm});
            skLineSegment(sketch, "E979", {"start": v(-146.74, -8.12) * mm, "end": v(-147.31, -8) * mm});
            skLineSegment(sketch, "E980", {"start": v(-147.31, -8) * mm, "end": v(-147.87, -7.77) * mm});
            skLineSegment(sketch, "E981", {"start": v(-147.87, -7.77) * mm, "end": v(-148.3, -7.7) * mm});
            skLineSegment(sketch, "E982", {"start": v(-148.3, -7.7) * mm, "end": v(-148.43, -7.73) * mm});
            skLineSegment(sketch, "E983", {"start": v(-148.43, -7.73) * mm, "end": v(-149, -7.52) * mm});
            skLineSegment(sketch, "E984", {"start": v(-149, -7.52) * mm, "end": v(-154.82, -5.48) * mm});
            skLineSegment(sketch, "E985", {"start": v(-154.82, -5.48) * mm, "end": v(-155.4, -5.28) * mm});
            skLineSegment(sketch, "E986", {"start": v(-155.4, -5.28) * mm, "end": v(-155.57, -5.23) * mm});
            skLineSegment(sketch, "E987", {"start": v(-155.57, -5.23) * mm, "end": v(-156.04, -5) * mm});
            skLineSegment(sketch, "E988", {"start": v(-156.04, -5) * mm, "end": v(-156.42, -4.65) * mm});
            skLineSegment(sketch, "E989", {"start": v(-156.42, -4.65) * mm, "end": v(-156.58, -4.12) * mm});
            skLineSegment(sketch, "E990", {"start": v(-156.58, -4.12) * mm, "end": v(-156.55, -3.56) * mm});
            skLineSegment(sketch, "E991", {"start": v(-156.55, -3.56) * mm, "end": v(-156.52, -3.38) * mm});
            skLineSegment(sketch, "E992", {"start": v(-156.52, -3.38) * mm, "end": v(-156.12, -1.27) * mm});
            skLineSegment(sketch, "E993", {"start": v(-156.12, -1.27) * mm, "end": v(-152.36, 19.81) * mm});
            skLineSegment(sketch, "E994", {"start": v(-152.36, 19.81) * mm, "end": v(-151.99, 21.92) * mm});
            skLineSegment(sketch, "E995", {"start": v(-126.28, -109) * mm, "end": v(-126.13, -109.02) * mm});
            skLineSegment(sketch, "E996", {"start": v(-126.13, -109.02) * mm, "end": v(-125.65, -109.14) * mm});
            skLineSegment(sketch, "E997", {"start": v(-125.65, -109.14) * mm, "end": v(-125.21, -109.44) * mm});
            skLineSegment(sketch, "E998", {"start": v(-125.21, -109.44) * mm, "end": v(-124.94, -109.91) * mm});
            skLineSegment(sketch, "E999", {"start": v(-124.94, -109.91) * mm, "end": v(-124.83, -110.4) * mm});
            skLineSegment(sketch, "E1000", {"start": v(-124.83, -110.4) * mm, "end": v(-124.82, -110.56) * mm});
            skLineSegment(sketch, "E1001", {"start": v(-124.82, -110.56) * mm, "end": v(-124.79, -111.14) * mm});
            skLineSegment(sketch, "E1002", {"start": v(-124.79, -111.14) * mm, "end": v(-124.34, -116.94) * mm});
            skLineSegment(sketch, "E1003", {"start": v(-124.34, -116.94) * mm, "end": v(-124.3, -117.53) * mm});
            skLineSegment(sketch, "E1004", {"start": v(-124.3, -117.53) * mm, "end": v(-124.28, -117.71) * mm});
            skLineSegment(sketch, "E1005", {"start": v(-124.28, -117.71) * mm, "end": v(-124.11, -119.58) * mm});
            skLineSegment(sketch, "E1006", {"start": v(-124.11, -119.58) * mm, "end": v(-124.1, -119.77) * mm});
            skLineSegment(sketch, "E1007", {"start": v(-124.1, -119.77) * mm, "end": v(-124.05, -120.62) * mm});
            skLineSegment(sketch, "E1008", {"start": v(-124.05, -120.62) * mm, "end": v(-123.76, -124.9) * mm});
            skLineSegment(sketch, "E1009", {"start": v(-123.76, -124.9) * mm, "end": v(-123.2, -129.13) * mm});
            skLineSegment(sketch, "E1010", {"start": v(-123.2, -129.13) * mm, "end": v(-123.01, -129.97) * mm});
            skLineSegment(sketch, "E1011", {"start": v(-123.01, -129.97) * mm, "end": v(-122.96, -130.22) * mm});
            skLineSegment(sketch, "E1012", {"start": v(-122.96, -130.22) * mm, "end": v(-122.62, -132.77) * mm});
            skLineSegment(sketch, "E1013", {"start": v(-122.62, -132.77) * mm, "end": v(-122.6, -133.03) * mm});
            skLineSegment(sketch, "E1014", {"start": v(-122.6, -133.03) * mm, "end": v(-122.58, -133.14) * mm});
            skLineSegment(sketch, "E1015", {"start": v(-122.58, -133.14) * mm, "end": v(-122.7, -133.6) * mm});
            skLineSegment(sketch, "E1016", {"start": v(-122.7, -133.6) * mm, "end": v(-123.12, -133.85) * mm});
            skLineSegment(sketch, "E1017", {"start": v(-123.12, -133.85) * mm, "end": v(-123.26, -133.86) * mm});
            skLineSegment(sketch, "E1018", {"start": v(-123.26, -133.86) * mm, "end": v(-123.36, -133.86) * mm});
            skLineSegment(sketch, "E1019", {"start": v(-123.36, -133.86) * mm, "end": v(-123.84, -133.8) * mm});
            skLineSegment(sketch, "E1020", {"start": v(-123.84, -133.8) * mm, "end": v(-124.18, -133.47) * mm});
            skLineSegment(sketch, "E1021", {"start": v(-124.18, -133.47) * mm, "end": v(-124.21, -133.34) * mm});
            skLineSegment(sketch, "E1022", {"start": v(-124.21, -133.34) * mm, "end": v(-124.27, -133.14) * mm});
            skLineSegment(sketch, "E1023", {"start": v(-124.27, -133.14) * mm, "end": v(-124.85, -131.17) * mm});
            skLineSegment(sketch, "E1024", {"start": v(-124.85, -131.17) * mm, "end": v(-124.9, -130.98) * mm});
            skLineSegment(sketch, "E1025", {"start": v(-124.9, -130.98) * mm, "end": v(-124.95, -130.83) * mm});
            skLineSegment(sketch, "E1026", {"start": v(-124.95, -130.83) * mm, "end": v(-125.14, -130.43) * mm});
            skLineSegment(sketch, "E1027", {"start": v(-125.14, -130.43) * mm, "end": v(-125.47, -130.07) * mm});
            skLineSegment(sketch, "E1028", {"start": v(-125.47, -130.07) * mm, "end": v(-125.94, -129.9) * mm});
            skLineSegment(sketch, "E1029", {"start": v(-125.94, -129.9) * mm, "end": v(-126.41, -129.87) * mm});
            skLineSegment(sketch, "E1030", {"start": v(-126.41, -129.87) * mm, "end": v(-126.57, -129.9) * mm});
            skLineSegment(sketch, "E1031", {"start": v(-126.57, -129.9) * mm, "end": v(-128.34, -130.1) * mm});
            skLineSegment(sketch, "E1032", {"start": v(-128.34, -130.1) * mm, "end": v(-137.2, -130.92) * mm});
            skLineSegment(sketch, "E1033", {"start": v(-137.2, -130.92) * mm, "end": v(-146.09, -131.64) * mm});
            skLineSegment(sketch, "E1034", {"start": v(-146.09, -131.64) * mm, "end": v(-147.86, -131.8) * mm});
            skLineSegment(sketch, "E1035", {"start": v(-147.86, -131.8) * mm, "end": v(-148.11, -131.83) * mm});
            skLineSegment(sketch, "E1036", {"start": v(-148.11, -131.83) * mm, "end": v(-148.84, -132) * mm});
            skLineSegment(sketch, "E1037", {"start": v(-148.84, -132) * mm, "end": v(-149.38, -132.47) * mm});
            skLineSegment(sketch, "E1038", {"start": v(-149.38, -132.47) * mm, "end": v(-149.57, -133.34) * mm});
            skLineSegment(sketch, "E1039", {"start": v(-149.57, -133.34) * mm, "end": v(-149.52, -134.42) * mm});
            skLineSegment(sketch, "E1040", {"start": v(-149.52, -134.42) * mm, "end": v(-149.48, -134.77) * mm});
            skLineSegment(sketch, "E1041", {"start": v(-149.48, -134.77) * mm, "end": v(-149.47, -134.94) * mm});
            skLineSegment(sketch, "E1042", {"start": v(-149.47, -134.94) * mm, "end": v(-149.5, -135.43) * mm});
            skLineSegment(sketch, "E1043", {"start": v(-149.5, -135.43) * mm, "end": v(-149.7, -135.86) * mm});
            skLineSegment(sketch, "E1044", {"start": v(-149.7, -135.86) * mm, "end": v(-150.1, -136.06) * mm});
            skLineSegment(sketch, "E1045", {"start": v(-150.1, -136.06) * mm, "end": v(-150.54, -136.06) * mm});
            skLineSegment(sketch, "E1046", {"start": v(-150.54, -136.06) * mm, "end": v(-150.67, -136.03) * mm});
            skLineSegment(sketch, "E1047", {"start": v(-150.67, -136.03) * mm, "end": v(-150.8, -136) * mm});
            skLineSegment(sketch, "E1048", {"start": v(-150.8, -136) * mm, "end": v(-151.19, -135.7) * mm});
            skLineSegment(sketch, "E1049", {"start": v(-151.19, -135.7) * mm, "end": v(-151.34, -135.25) * mm});
            skLineSegment(sketch, "E1050", {"start": v(-151.34, -135.25) * mm, "end": v(-151.35, -135.14) * mm});
            skLineSegment(sketch, "E1051", {"start": v(-151.35, -135.14) * mm, "end": v(-151.46, -133.8) * mm});
            skLineSegment(sketch, "E1052", {"start": v(-151.46, -133.8) * mm, "end": v(-152.06, -129.84) * mm});
            skLineSegment(sketch, "E1053", {"start": v(-152.06, -129.84) * mm, "end": v(-153.16, -124.62) * mm});
            skLineSegment(sketch, "E1054", {"start": v(-153.16, -124.62) * mm, "end": v(-154.45, -119.44) * mm});
            skLineSegment(sketch, "E1055", {"start": v(-154.45, -119.44) * mm, "end": v(-155.4, -115.56) * mm});
            skLineSegment(sketch, "E1056", {"start": v(-155.4, -115.56) * mm, "end": v(-155.68, -114.25) * mm});
            skLineSegment(sketch, "E1057", {"start": v(-155.68, -114.25) * mm, "end": v(-155.73, -114) * mm});
            skLineSegment(sketch, "E1058", {"start": v(-155.73, -114) * mm, "end": v(-155.88, -113.23) * mm});
            skLineSegment(sketch, "E1059", {"start": v(-155.88, -113.23) * mm, "end": v(-155.96, -112.43) * mm});
            skLineSegment(sketch, "E1060", {"start": v(-155.96, -112.43) * mm, "end": v(-155.9, -111.82) * mm});
            skLineSegment(sketch, "E1061", {"start": v(-155.9, -111.82) * mm, "end": v(-155.69, -111.39) * mm});
            skLineSegment(sketch, "E1062", {"start": v(-155.69, -111.39) * mm, "end": v(-155.3, -111.09) * mm});
            skLineSegment(sketch, "E1063", {"start": v(-155.3, -111.09) * mm, "end": v(-154.7, -110.9) * mm});
            skLineSegment(sketch, "E1064", {"start": v(-154.7, -110.9) * mm, "end": v(-153.9, -110.8) * mm});
            skLineSegment(sketch, "E1065", {"start": v(-153.9, -110.8) * mm, "end": v(-153.1, -110.76) * mm});
            skLineSegment(sketch, "E1066", {"start": v(-153.1, -110.76) * mm, "end": v(-152.84, -110.75) * mm});
            skLineSegment(sketch, "E1067", {"start": v(-152.84, -110.75) * mm, "end": v(-152.5, -110.75) * mm});
            skLineSegment(sketch, "E1068", {"start": v(-152.5, -110.75) * mm, "end": v(-149.07, -110.61) * mm});
            skLineSegment(sketch, "E1069", {"start": v(-149.07, -110.61) * mm, "end": v(-148.73, -110.6) * mm});
            skLineSegment(sketch, "E1070", {"start": v(-148.73, -110.6) * mm, "end": v(-148.64, -110.6) * mm});
            skLineSegment(sketch, "E1071", {"start": v(-148.64, -110.6) * mm, "end": v(-148.37, -110.6) * mm});
            skLineSegment(sketch, "E1072", {"start": v(-148.37, -110.6) * mm, "end": v(-148.05, -110.67) * mm});
            skLineSegment(sketch, "E1073", {"start": v(-148.05, -110.67) * mm, "end": v(-147.79, -110.85) * mm});
            skLineSegment(sketch, "E1074", {"start": v(-147.79, -110.85) * mm, "end": v(-147.65, -111.14) * mm});
            skLineSegment(sketch, "E1075", {"start": v(-147.65, -111.14) * mm, "end": v(-147.63, -111.24) * mm});
            skLineSegment(sketch, "E1076", {"start": v(-147.63, -111.24) * mm, "end": v(-147.6, -111.38) * mm});
            skLineSegment(sketch, "E1077", {"start": v(-147.6, -111.38) * mm, "end": v(-147.7, -111.94) * mm});
            skLineSegment(sketch, "E1078", {"start": v(-147.7, -111.94) * mm, "end": v(-148.08, -112.35) * mm});
            skLineSegment(sketch, "E1079", {"start": v(-148.08, -112.35) * mm, "end": v(-148.2, -112.42) * mm});
            skLineSegment(sketch, "E1080", {"start": v(-148.2, -112.42) * mm, "end": v(-148.36, -112.49) * mm});
            skLineSegment(sketch, "E1081", {"start": v(-148.36, -112.49) * mm, "end": v(-149.9, -113.24) * mm});
            skLineSegment(sketch, "E1082", {"start": v(-149.9, -113.24) * mm, "end": v(-150.05, -113.3) * mm});
            skLineSegment(sketch, "E1083", {"start": v(-150.05, -113.3) * mm, "end": v(-150.24, -113.4) * mm});
            skLineSegment(sketch, "E1084", {"start": v(-150.24, -113.4) * mm, "end": v(-150.8, -113.65) * mm});
            skLineSegment(sketch, "E1085", {"start": v(-150.8, -113.65) * mm, "end": v(-151.37, -113.98) * mm});
            skLineSegment(sketch, "E1086", {"start": v(-151.37, -113.98) * mm, "end": v(-151.8, -114.3) * mm});
            skLineSegment(sketch, "E1087", {"start": v(-151.8, -114.3) * mm, "end": v(-152.1, -114.67) * mm});
            skLineSegment(sketch, "E1088", {"start": v(-152.1, -114.67) * mm, "end": v(-152.3, -115.1) * mm});
            skLineSegment(sketch, "E1089", {"start": v(-152.3, -115.1) * mm, "end": v(-152.42, -115.62) * mm});
            skLineSegment(sketch, "E1090", {"start": v(-152.42, -115.62) * mm, "end": v(-152.47, -116.27) * mm});
            skLineSegment(sketch, "E1091", {"start": v(-152.47, -116.27) * mm, "end": v(-152.49, -116.87) * mm});
            skLineSegment(sketch, "E1092", {"start": v(-152.49, -116.87) * mm, "end": v(-152.49, -117.08) * mm});
            skLineSegment(sketch, "E1093", {"start": v(-152.49, -117.08) * mm, "end": v(-152.5, -117.75) * mm});
            skLineSegment(sketch, "E1094", {"start": v(-152.5, -117.75) * mm, "end": v(-152.08, -121.06) * mm});
            skLineSegment(sketch, "E1095", {"start": v(-152.08, -121.06) * mm, "end": v(-151.38, -124.32) * mm});
            skLineSegment(sketch, "E1096", {"start": v(-151.38, -124.32) * mm, "end": v(-151.25, -124.97) * mm});
            skLineSegment(sketch, "E1097", {"start": v(-151.25, -124.97) * mm, "end": v(-151.22, -125.1) * mm});
            skLineSegment(sketch, "E1098", {"start": v(-151.22, -125.1) * mm, "end": v(-151.1, -125.47) * mm});
            skLineSegment(sketch, "E1099", {"start": v(-151.1, -125.47) * mm, "end": v(-150.85, -125.84) * mm});
            skLineSegment(sketch, "E1100", {"start": v(-150.85, -125.84) * mm, "end": v(-150.46, -126.07) * mm});
            skLineSegment(sketch, "E1101", {"start": v(-150.46, -126.07) * mm, "end": v(-150.02, -126.13) * mm});
            skLineSegment(sketch, "E1102", {"start": v(-150.02, -126.13) * mm, "end": v(-149.88, -126.12) * mm});
            skLineSegment(sketch, "E1103", {"start": v(-149.88, -126.12) * mm, "end": v(-149.09, -126.06) * mm});
            skLineSegment(sketch, "E1104", {"start": v(-149.09, -126.06) * mm, "end": v(-141.22, -125.61) * mm});
            skLineSegment(sketch, "E1105", {"start": v(-141.22, -125.61) * mm, "end": v(-140.43, -125.57) * mm});
            skLineSegment(sketch, "E1106", {"start": v(-140.43, -125.57) * mm, "end": v(-140.3, -125.56) * mm});
            skLineSegment(sketch, "E1107", {"start": v(-140.3, -125.56) * mm, "end": v(-139.92, -125.47) * mm});
            skLineSegment(sketch, "E1108", {"start": v(-139.92, -125.47) * mm, "end": v(-139.61, -125.23) * mm});
            skLineSegment(sketch, "E1109", {"start": v(-139.61, -125.23) * mm, "end": v(-139.5, -124.86) * mm});
            skLineSegment(sketch, "E1110", {"start": v(-139.5, -124.86) * mm, "end": v(-139.5, -124.48) * mm});
            skLineSegment(sketch, "E1111", {"start": v(-139.5, -124.48) * mm, "end": v(-139.52, -124.36) * mm});
            skLineSegment(sketch, "E1112", {"start": v(-139.52, -124.36) * mm, "end": v(-139.58, -124.04) * mm});
            skLineSegment(sketch, "E1113", {"start": v(-139.58, -124.04) * mm, "end": v(-140.1, -120.83) * mm});
            skLineSegment(sketch, "E1114", {"start": v(-140.1, -120.83) * mm, "end": v(-140.13, -120.5) * mm});
            skLineSegment(sketch, "E1115", {"start": v(-140.13, -120.5) * mm, "end": v(-140.17, -120.12) * mm});
            skLineSegment(sketch, "E1116", {"start": v(-140.17, -120.12) * mm, "end": v(-140.52, -118.96) * mm});
            skLineSegment(sketch, "E1117", {"start": v(-140.52, -118.96) * mm, "end": v(-141.3, -117.83) * mm});
            skLineSegment(sketch, "E1118", {"start": v(-141.3, -117.83) * mm, "end": v(-142.46, -117.1) * mm});
            skLineSegment(sketch, "E1119", {"start": v(-142.46, -117.1) * mm, "end": v(-143.6, -116.79) * mm});
            skLineSegment(sketch, "E1120", {"start": v(-143.6, -116.79) * mm, "end": v(-144, -116.75) * mm});
            skLineSegment(sketch, "E1121", {"start": v(-144, -116.75) * mm, "end": v(-144.11, -116.73) * mm});
            skLineSegment(sketch, "E1122", {"start": v(-144.11, -116.73) * mm, "end": v(-145.3, -116.54) * mm});
            skLineSegment(sketch, "E1123", {"start": v(-145.3, -116.54) * mm, "end": v(-145.41, -116.52) * mm});
            skLineSegment(sketch, "E1124", {"start": v(-145.41, -116.52) * mm, "end": v(-145.54, -116.49) * mm});
            skLineSegment(sketch, "E1125", {"start": v(-145.54, -116.49) * mm, "end": v(-145.87, -116.14) * mm});
            skLineSegment(sketch, "E1126", {"start": v(-145.87, -116.14) * mm, "end": v(-145.96, -115.64) * mm});
            skLineSegment(sketch, "E1127", {"start": v(-145.96, -115.64) * mm, "end": v(-145.96, -115.54) * mm});
            skLineSegment(sketch, "E1128", {"start": v(-145.96, -115.54) * mm, "end": v(-145.97, -115.43) * mm});
            skLineSegment(sketch, "E1129", {"start": v(-145.97, -115.43) * mm, "end": v(-145.77, -115.09) * mm});
            skLineSegment(sketch, "E1130", {"start": v(-145.77, -115.09) * mm, "end": v(-145.38, -114.96) * mm});
            skLineSegment(sketch, "E1131", {"start": v(-145.38, -114.96) * mm, "end": v(-145.29, -114.96) * mm});
            skLineSegment(sketch, "E1132", {"start": v(-145.29, -114.96) * mm, "end": v(-144.4, -114.91) * mm});
            skLineSegment(sketch, "E1133", {"start": v(-144.4, -114.91) * mm, "end": v(-135.5, -114.47) * mm});
            skLineSegment(sketch, "E1134", {"start": v(-135.5, -114.47) * mm, "end": v(-134.6, -114.43) * mm});
            skLineSegment(sketch, "E1135", {"start": v(-134.6, -114.43) * mm, "end": v(-134.5, -114.42) * mm});
            skLineSegment(sketch, "E1136", {"start": v(-134.5, -114.42) * mm, "end": v(-134.03, -114.52) * mm});
            skLineSegment(sketch, "E1137", {"start": v(-134.03, -114.52) * mm, "end": v(-133.72, -114.9) * mm});
            skLineSegment(sketch, "E1138", {"start": v(-133.72, -114.9) * mm, "end": v(-133.7, -115.03) * mm});
            skLineSegment(sketch, "E1139", {"start": v(-133.7, -115.03) * mm, "end": v(-133.67, -115.18) * mm});
            skLineSegment(sketch, "E1140", {"start": v(-133.67, -115.18) * mm, "end": v(-133.83, -115.73) * mm});
            skLineSegment(sketch, "E1141", {"start": v(-133.83, -115.73) * mm, "end": v(-134.3, -116.04) * mm});
            skLineSegment(sketch, "E1142", {"start": v(-134.3, -116.04) * mm, "end": v(-134.43, -116.08) * mm});
            skLineSegment(sketch, "E1143", {"start": v(-134.43, -116.08) * mm, "end": v(-134.61, -116.13) * mm});
            skLineSegment(sketch, "E1144", {"start": v(-134.61, -116.13) * mm, "end": v(-136.44, -116.56) * mm});
            skLineSegment(sketch, "E1145", {"start": v(-136.44, -116.56) * mm, "end": v(-136.63, -116.6) * mm});
            skLineSegment(sketch, "E1146", {"start": v(-136.63, -116.6) * mm, "end": v(-136.86, -116.67) * mm});
            skLineSegment(sketch, "E1147", {"start": v(-136.86, -116.67) * mm, "end": v(-137.52, -116.92) * mm});
            skLineSegment(sketch, "E1148", {"start": v(-137.52, -116.92) * mm, "end": v(-138.06, -117.36) * mm});
            skLineSegment(sketch, "E1149", {"start": v(-138.06, -117.36) * mm, "end": v(-138.31, -118) * mm});
            skLineSegment(sketch, "E1150", {"start": v(-138.31, -118) * mm, "end": v(-138.34, -118.7) * mm});
            skLineSegment(sketch, "E1151", {"start": v(-138.34, -118.7) * mm, "end": v(-138.32, -118.94) * mm});
            skLineSegment(sketch, "E1152", {"start": v(-138.32, -118.94) * mm, "end": v(-138.3, -119.38) * mm});
            skLineSegment(sketch, "E1153", {"start": v(-138.3, -119.38) * mm, "end": v(-137.97, -121.58) * mm});
            skLineSegment(sketch, "E1154", {"start": v(-137.97, -121.58) * mm, "end": v(-137.53, -123.77) * mm});
            skLineSegment(sketch, "E1155", {"start": v(-137.53, -123.77) * mm, "end": v(-137.44, -124.2) * mm});
            skLineSegment(sketch, "E1156", {"start": v(-137.44, -124.2) * mm, "end": v(-137.41, -124.34) * mm});
            skLineSegment(sketch, "E1157", {"start": v(-137.41, -124.34) * mm, "end": v(-137.26, -124.75) * mm});
            skLineSegment(sketch, "E1158", {"start": v(-137.26, -124.75) * mm, "end": v(-136.98, -125.1) * mm});
            skLineSegment(sketch, "E1159", {"start": v(-136.98, -125.1) * mm, "end": v(-136.58, -125.25) * mm});
            skLineSegment(sketch, "E1160", {"start": v(-136.58, -125.25) * mm, "end": v(-136.16, -125.26) * mm});
            skLineSegment(sketch, "E1161", {"start": v(-136.16, -125.26) * mm, "end": v(-136.03, -125.24) * mm});
            skLineSegment(sketch, "E1162", {"start": v(-136.03, -125.24) * mm, "end": v(-135.37, -125.15) * mm});
            skLineSegment(sketch, "E1163", {"start": v(-135.37, -125.15) * mm, "end": v(-128.7, -124.75) * mm});
            skLineSegment(sketch, "E1164", {"start": v(-128.7, -124.75) * mm, "end": v(-128.03, -124.72) * mm});
            skLineSegment(sketch, "E1165", {"start": v(-128.03, -124.72) * mm, "end": v(-127.77, -124.7) * mm});
            skLineSegment(sketch, "E1166", {"start": v(-127.77, -124.7) * mm, "end": v(-126.97, -124.56) * mm});
            skLineSegment(sketch, "E1167", {"start": v(-126.97, -124.56) * mm, "end": v(-126.34, -124.17) * mm});
            skLineSegment(sketch, "E1168", {"start": v(-126.34, -124.17) * mm, "end": v(-126.08, -123.47) * mm});
            skLineSegment(sketch, "E1169", {"start": v(-126.08, -123.47) * mm, "end": v(-126.07, -122.65) * mm});
            skLineSegment(sketch, "E1170", {"start": v(-126.07, -122.65) * mm, "end": v(-126.1, -122.38) * mm});
            skLineSegment(sketch, "E1171", {"start": v(-126.1, -122.38) * mm, "end": v(-126.15, -121.88) * mm});
            skLineSegment(sketch, "E1172", {"start": v(-126.15, -121.88) * mm, "end": v(-126.58, -116.94) * mm});
            skLineSegment(sketch, "E1173", {"start": v(-126.58, -116.94) * mm, "end": v(-126.65, -116.45) * mm});
            skLineSegment(sketch, "E1174", {"start": v(-126.65, -116.45) * mm, "end": v(-126.71, -116.03) * mm});
            skLineSegment(sketch, "E1175", {"start": v(-126.71, -116.03) * mm, "end": v(-127.09, -114.79) * mm});
            skLineSegment(sketch, "E1176", {"start": v(-127.09, -114.79) * mm, "end": v(-127.84, -113.4) * mm});
            skLineSegment(sketch, "E1177", {"start": v(-127.84, -113.4) * mm, "end": v(-128.93, -112.27) * mm});
            skLineSegment(sketch, "E1178", {"start": v(-128.93, -112.27) * mm, "end": v(-129.97, -111.56) * mm});
            skLineSegment(sketch, "E1179", {"start": v(-129.97, -111.56) * mm, "end": v(-130.34, -111.37) * mm});
            skLineSegment(sketch, "E1180", {"start": v(-130.34, -111.37) * mm, "end": v(-130.54, -111.27) * mm});
            skLineSegment(sketch, "E1181", {"start": v(-130.54, -111.27) * mm, "end": v(-132.6, -110.43) * mm});
            skLineSegment(sketch, "E1182", {"start": v(-132.6, -110.43) * mm, "end": v(-132.8, -110.35) * mm});
            skLineSegment(sketch, "E1183", {"start": v(-132.8, -110.35) * mm, "end": v(-132.94, -110.3) * mm});
            skLineSegment(sketch, "E1184", {"start": v(-132.94, -110.3) * mm, "end": v(-133.47, -109.9) * mm});
            skLineSegment(sketch, "E1185", {"start": v(-133.47, -109.9) * mm, "end": v(-133.73, -109.3) * mm});
            skLineSegment(sketch, "E1186", {"start": v(-133.73, -109.3) * mm, "end": v(-133.73, -109.15) * mm});
            skLineSegment(sketch, "E1187", {"start": v(-133.73, -109.15) * mm, "end": v(-133.73, -109.04) * mm});
            skLineSegment(sketch, "E1188", {"start": v(-133.73, -109.04) * mm, "end": v(-133.71, -108.72) * mm});
            skLineSegment(sketch, "E1189", {"start": v(-133.71, -108.72) * mm, "end": v(-133.59, -108.41) * mm});
            skLineSegment(sketch, "E1190", {"start": v(-133.59, -108.41) * mm, "end": v(-133.3, -108.26) * mm});
            skLineSegment(sketch, "E1191", {"start": v(-133.3, -108.26) * mm, "end": v(-132.94, -108.24) * mm});
            skLineSegment(sketch, "E1192", {"start": v(-132.94, -108.24) * mm, "end": v(-132.82, -108.26) * mm});
            skLineSegment(sketch, "E1193", {"start": v(-132.82, -108.26) * mm, "end": v(-132.28, -108.33) * mm});
            skLineSegment(sketch, "E1194", {"start": v(-132.28, -108.33) * mm, "end": v(-126.83, -108.95) * mm});
            skLineSegment(sketch, "E1195", {"start": v(-126.83, -108.95) * mm, "end": v(-126.28, -109) * mm});
            skLineSegment(sketch, "E1196", {"start": v(-132.85, -84.54) * mm, "end": v(-132.57, -84.7) * mm});
            skLineSegment(sketch, "E1197", {"start": v(-132.57, -84.7) * mm, "end": v(-131.7, -85.14) * mm});
            skLineSegment(sketch, "E1198", {"start": v(-131.7, -85.14) * mm, "end": v(-130.54, -85.75) * mm});
            skLineSegment(sketch, "E1199", {"start": v(-130.54, -85.75) * mm, "end": v(-129.44, -86.47) * mm});
            skLineSegment(sketch, "E1200", {"start": v(-129.44, -86.47) * mm, "end": v(-128.66, -87.12) * mm});
            skLineSegment(sketch, "E1201", {"start": v(-128.66, -87.12) * mm, "end": v(-128.44, -87.37) * mm});
            skLineSegment(sketch, "E1202", {"start": v(-128.44, -87.37) * mm, "end": v(-127.8, -88.06) * mm});
            skLineSegment(sketch, "E1203", {"start": v(-127.8, -88.06) * mm, "end": v(-126.3, -90.49) * mm});
            skLineSegment(sketch, "E1204", {"start": v(-126.3, -90.49) * mm, "end": v(-125.24, -93.82) * mm});
            skLineSegment(sketch, "E1205", {"start": v(-125.24, -93.82) * mm, "end": v(-125.07, -97.32) * mm});
            skLineSegment(sketch, "E1206", {"start": v(-125.07, -97.32) * mm, "end": v(-125.4, -100.07) * mm});
            skLineSegment(sketch, "E1207", {"start": v(-125.4, -100.07) * mm, "end": v(-125.58, -100.97) * mm});
            skLineSegment(sketch, "E1208", {"start": v(-125.58, -100.97) * mm, "end": v(-125.65, -101.26) * mm});
            skLineSegment(sketch, "E1209", {"start": v(-125.65, -101.26) * mm, "end": v(-126.11, -102.7) * mm});
            skLineSegment(sketch, "E1210", {"start": v(-126.11, -102.7) * mm, "end": v(-126.87, -104.02) * mm});
            skLineSegment(sketch, "E1211", {"start": v(-126.87, -104.02) * mm, "end": v(-127.08, -104.26) * mm});
            skLineSegment(sketch, "E1212", {"start": v(-127.08, -104.26) * mm, "end": v(-127.53, -104.25) * mm});
            skLineSegment(sketch, "E1213", {"start": v(-127.53, -104.25) * mm, "end": v(-131.99, -104.21) * mm});
            skLineSegment(sketch, "E1214", {"start": v(-131.99, -104.21) * mm, "end": v(-132.43, -104.2) * mm});
            skLineSegment(sketch, "E1215", {"start": v(-132.43, -104.2) * mm, "end": v(-132.53, -104.2) * mm});
            skLineSegment(sketch, "E1216", {"start": v(-132.53, -104.2) * mm, "end": v(-132.83, -104.22) * mm});
            skLineSegment(sketch, "E1217", {"start": v(-132.83, -104.22) * mm, "end": v(-133.23, -104.2) * mm});
            skLineSegment(sketch, "E1218", {"start": v(-133.23, -104.2) * mm, "end": v(-133.56, -104.02) * mm});
            skLineSegment(sketch, "E1219", {"start": v(-133.56, -104.02) * mm, "end": v(-133.73, -103.7) * mm});
            skLineSegment(sketch, "E1220", {"start": v(-133.73, -103.7) * mm, "end": v(-133.75, -103.6) * mm});
            skLineSegment(sketch, "E1221", {"start": v(-133.75, -103.6) * mm, "end": v(-133.77, -103.45) * mm});
            skLineSegment(sketch, "E1222", {"start": v(-133.77, -103.45) * mm, "end": v(-133.8, -103.02) * mm});
            skLineSegment(sketch, "E1223", {"start": v(-133.8, -103.02) * mm, "end": v(-133.7, -102.51) * mm});
            skLineSegment(sketch, "E1224", {"start": v(-133.7, -102.51) * mm, "end": v(-133.41, -102.1) * mm});
            skLineSegment(sketch, "E1225", {"start": v(-133.41, -102.1) * mm, "end": v(-133, -101.85) * mm});
            skLineSegment(sketch, "E1226", {"start": v(-133, -101.85) * mm, "end": v(-132.85, -101.8) * mm});
            skLineSegment(sketch, "E1227", {"start": v(-132.85, -101.8) * mm, "end": v(-132.55, -101.71) * mm});
            skLineSegment(sketch, "E1228", {"start": v(-132.55, -101.71) * mm, "end": v(-131.15, -101.07) * mm});
            skLineSegment(sketch, "E1229", {"start": v(-131.15, -101.07) * mm, "end": v(-129.87, -100.22) * mm});
            skLineSegment(sketch, "E1230", {"start": v(-129.87, -100.22) * mm, "end": v(-129.63, -100.02) * mm});
            skLineSegment(sketch, "E1231", {"start": v(-129.63, -100.02) * mm, "end": v(-129.24, -99.7) * mm});
            skLineSegment(sketch, "E1232", {"start": v(-129.24, -99.7) * mm, "end": v(-128.26, -98.5) * mm});
            skLineSegment(sketch, "E1233", {"start": v(-128.26, -98.5) * mm, "end": v(-127.49, -96.74) * mm});
            skLineSegment(sketch, "E1234", {"start": v(-127.49, -96.74) * mm, "end": v(-127.33, -94.81) * mm});
            skLineSegment(sketch, "E1235", {"start": v(-127.33, -94.81) * mm, "end": v(-127.63, -93.3) * mm});
            skLineSegment(sketch, "E1236", {"start": v(-127.63, -93.3) * mm, "end": v(-127.82, -92.83) * mm});
            skLineSegment(sketch, "E1237", {"start": v(-127.82, -92.83) * mm, "end": v(-127.87, -92.7) * mm});
            skLineSegment(sketch, "E1238", {"start": v(-127.87, -92.7) * mm, "end": v(-128.44, -91.46) * mm});
            skLineSegment(sketch, "E1239", {"start": v(-128.44, -91.46) * mm, "end": v(-128.5, -91.34) * mm});
            skLineSegment(sketch, "E1240", {"start": v(-128.5, -91.34) * mm, "end": v(-128.67, -91.04) * mm});
            skLineSegment(sketch, "E1241", {"start": v(-128.67, -91.04) * mm, "end": v(-129.27, -90.2) * mm});
            skLineSegment(sketch, "E1242", {"start": v(-129.27, -90.2) * mm, "end": v(-130.21, -89.33) * mm});
            skLineSegment(sketch, "E1243", {"start": v(-130.21, -89.33) * mm, "end": v(-131.37, -88.8) * mm});
            skLineSegment(sketch, "E1244", {"start": v(-131.37, -88.8) * mm, "end": v(-132.41, -88.63) * mm});
            skLineSegment(sketch, "E1245", {"start": v(-132.41, -88.63) * mm, "end": v(-132.76, -88.64) * mm});
            skLineSegment(sketch, "E1246", {"start": v(-132.76, -88.64) * mm, "end": v(-133.12, -88.64) * mm});
            skLineSegment(sketch, "E1247", {"start": v(-133.12, -88.64) * mm, "end": v(-134.2, -88.84) * mm});
            skLineSegment(sketch, "E1248", {"start": v(-134.2, -88.84) * mm, "end": v(-135.4, -89.39) * mm});
            skLineSegment(sketch, "E1249", {"start": v(-135.4, -89.39) * mm, "end": v(-136.38, -90.28) * mm});
            skLineSegment(sketch, "E1250", {"start": v(-136.38, -90.28) * mm, "end": v(-136.98, -91.18) * mm});
            skLineSegment(sketch, "E1251", {"start": v(-136.98, -91.18) * mm, "end": v(-137.12, -91.5) * mm});
            skLineSegment(sketch, "E1252", {"start": v(-137.12, -91.5) * mm, "end": v(-137.26, -91.82) * mm});
            skLineSegment(sketch, "E1253", {"start": v(-137.26, -91.82) * mm, "end": v(-138.44, -95.03) * mm});
            skLineSegment(sketch, "E1254", {"start": v(-138.44, -95.03) * mm, "end": v(-138.56, -95.35) * mm});
            skLineSegment(sketch, "E1255", {"start": v(-138.56, -95.35) * mm, "end": v(-138.65, -95.6) * mm});
            skLineSegment(sketch, "E1256", {"start": v(-138.65, -95.6) * mm, "end": v(-139.57, -98) * mm});
            skLineSegment(sketch, "E1257", {"start": v(-139.57, -98) * mm, "end": v(-139.64, -98.24) * mm});
            skLineSegment(sketch, "E1258", {"start": v(-139.64, -98.24) * mm, "end": v(-139.86, -98.95) * mm});
            skLineSegment(sketch, "E1259", {"start": v(-139.86, -98.95) * mm, "end": v(-141.06, -100.95) * mm});
            skLineSegment(sketch, "E1260", {"start": v(-141.06, -100.95) * mm, "end": v(-143.16, -102.74) * mm});
            skLineSegment(sketch, "E1261", {"start": v(-143.16, -102.74) * mm, "end": v(-145.7, -103.7) * mm});
            skLineSegment(sketch, "E1262", {"start": v(-145.7, -103.7) * mm, "end": v(-147.73, -103.97) * mm});
            skLineSegment(sketch, "E1263", {"start": v(-147.73, -103.97) * mm, "end": v(-148.4, -103.95) * mm});
            skLineSegment(sketch, "E1264", {"start": v(-148.4, -103.95) * mm, "end": v(-149.27, -103.92) * mm});
            skLineSegment(sketch, "E1265", {"start": v(-149.27, -103.92) * mm, "end": v(-151.86, -103.37) * mm});
            skLineSegment(sketch, "E1266", {"start": v(-151.86, -103.37) * mm, "end": v(-154.8, -101.88) * mm});
            skLineSegment(sketch, "E1267", {"start": v(-154.8, -101.88) * mm, "end": v(-157.12, -99.52) * mm});
            skLineSegment(sketch, "E1268", {"start": v(-157.12, -99.52) * mm, "end": v(-158.43, -97.18) * mm});
            skLineSegment(sketch, "E1269", {"start": v(-158.43, -97.18) * mm, "end": v(-158.7, -96.34) * mm});
            skLineSegment(sketch, "E1270", {"start": v(-158.7, -96.34) * mm, "end": v(-158.95, -95.58) * mm});
            skLineSegment(sketch, "E1271", {"start": v(-158.95, -95.58) * mm, "end": v(-159.57, -91.71) * mm});
            skLineSegment(sketch, "E1272", {"start": v(-159.57, -91.71) * mm, "end": v(-159.34, -87.8) * mm});
            skLineSegment(sketch, "E1273", {"start": v(-159.34, -87.8) * mm, "end": v(-159.16, -87) * mm});
            skLineSegment(sketch, "E1274", {"start": v(-159.16, -87) * mm, "end": v(-159.1, -86.78) * mm});
            skLineSegment(sketch, "E1275", {"start": v(-159.1, -86.78) * mm, "end": v(-158.91, -86.09) * mm});
            skLineSegment(sketch, "E1276", {"start": v(-158.91, -86.09) * mm, "end": v(-158.59, -85.59) * mm});
            skLineSegment(sketch, "E1277", {"start": v(-158.59, -85.59) * mm, "end": v(-158.04, -85.38) * mm});
            skLineSegment(sketch, "E1278", {"start": v(-158.04, -85.38) * mm, "end": v(-157.33, -85.35) * mm});
            skLineSegment(sketch, "E1279", {"start": v(-157.33, -85.35) * mm, "end": v(-157.1, -85.35) * mm});
            skLineSegment(sketch, "E1280", {"start": v(-157.1, -85.35) * mm, "end": v(-156.64, -85.36) * mm});
            skLineSegment(sketch, "E1281", {"start": v(-156.64, -85.36) * mm, "end": v(-154.33, -85.3) * mm});
            skLineSegment(sketch, "E1282", {"start": v(-154.33, -85.3) * mm, "end": v(-152.02, -85.4) * mm});
            skLineSegment(sketch, "E1283", {"start": v(-152.02, -85.4) * mm, "end": v(-151.55, -85.47) * mm});
            skLineSegment(sketch, "E1284", {"start": v(-151.55, -85.47) * mm, "end": v(-151.43, -85.5) * mm});
            skLineSegment(sketch, "E1285", {"start": v(-151.43, -85.5) * mm, "end": v(-151.05, -85.58) * mm});
            skLineSegment(sketch, "E1286", {"start": v(-151.05, -85.58) * mm, "end": v(-150.63, -85.77) * mm});
            skLineSegment(sketch, "E1287", {"start": v(-150.63, -85.77) * mm, "end": v(-150.34, -86.11) * mm});
            skLineSegment(sketch, "E1288", {"start": v(-150.34, -86.11) * mm, "end": v(-150.24, -86.55) * mm});
            skLineSegment(sketch, "E1289", {"start": v(-150.24, -86.55) * mm, "end": v(-150.24, -86.7) * mm});
            skLineSegment(sketch, "E1290", {"start": v(-150.24, -86.7) * mm, "end": v(-150.24, -86.84) * mm});
            skLineSegment(sketch, "E1291", {"start": v(-150.24, -86.84) * mm, "end": v(-150.27, -87.28) * mm});
            skLineSegment(sketch, "E1292", {"start": v(-150.27, -87.28) * mm, "end": v(-150.42, -87.74) * mm});
            skLineSegment(sketch, "E1293", {"start": v(-150.42, -87.74) * mm, "end": v(-150.76, -88.08) * mm});
            skLineSegment(sketch, "E1294", {"start": v(-150.76, -88.08) * mm, "end": v(-151.2, -88.25) * mm});
            skLineSegment(sketch, "E1295", {"start": v(-151.2, -88.25) * mm, "end": v(-151.36, -88.28) * mm});
            skLineSegment(sketch, "E1296", {"start": v(-151.36, -88.28) * mm, "end": v(-151.57, -88.3) * mm});
            skLineSegment(sketch, "E1297", {"start": v(-151.57, -88.3) * mm, "end": v(-153.52, -88.94) * mm});
            skLineSegment(sketch, "E1298", {"start": v(-153.52, -88.94) * mm, "end": v(-153.7, -89.02) * mm});
            skLineSegment(sketch, "E1299", {"start": v(-153.7, -89.02) * mm, "end": v(-154.1, -89.19) * mm});
            skLineSegment(sketch, "E1300", {"start": v(-154.1, -89.19) * mm, "end": v(-155.16, -89.95) * mm});
            skLineSegment(sketch, "E1301", {"start": v(-155.16, -89.95) * mm, "end": v(-156.17, -91.25) * mm});
            skLineSegment(sketch, "E1302", {"start": v(-156.17, -91.25) * mm, "end": v(-156.66, -92.81) * mm});
            skLineSegment(sketch, "E1303", {"start": v(-156.66, -92.81) * mm, "end": v(-156.7, -94.12) * mm});
            skLineSegment(sketch, "E1304", {"start": v(-156.7, -94.12) * mm, "end": v(-156.6, -94.54) * mm});
            skLineSegment(sketch, "E1305", {"start": v(-156.6, -94.54) * mm, "end": v(-156.54, -94.89) * mm});
            skLineSegment(sketch, "E1306", {"start": v(-156.54, -94.89) * mm, "end": v(-156.18, -95.9) * mm});
            skLineSegment(sketch, "E1307", {"start": v(-156.18, -95.9) * mm, "end": v(-155.5, -97.07) * mm});
            skLineSegment(sketch, "E1308", {"start": v(-155.5, -97.07) * mm, "end": v(-154.55, -98.05) * mm});
            skLineSegment(sketch, "E1309", {"start": v(-154.55, -98.05) * mm, "end": v(-153.7, -98.68) * mm});
            skLineSegment(sketch, "E1310", {"start": v(-153.7, -98.68) * mm, "end": v(-153.4, -98.85) * mm});
            skLineSegment(sketch, "E1311", {"start": v(-153.4, -98.85) * mm, "end": v(-153.02, -99.06) * mm});
            skLineSegment(sketch, "E1312", {"start": v(-153.02, -99.06) * mm, "end": v(-151.72, -99.38) * mm});
            skLineSegment(sketch, "E1313", {"start": v(-151.72, -99.38) * mm, "end": v(-150.04, -99.2) * mm});
            skLineSegment(sketch, "E1314", {"start": v(-150.04, -99.2) * mm, "end": v(-148.53, -98.4) * mm});
            skLineSegment(sketch, "E1315", {"start": v(-148.53, -98.4) * mm, "end": v(-147.6, -97.42) * mm});
            skLineSegment(sketch, "E1316", {"start": v(-147.6, -97.42) * mm, "end": v(-147.4, -97.03) * mm});
            skLineSegment(sketch, "E1317", {"start": v(-147.4, -97.03) * mm, "end": v(-147.25, -96.78) * mm});
            skLineSegment(sketch, "E1318", {"start": v(-147.25, -96.78) * mm, "end": v(-146.67, -95.44) * mm});
            skLineSegment(sketch, "E1319", {"start": v(-146.67, -95.44) * mm, "end": v(-146.25, -94.05) * mm});
            skLineSegment(sketch, "E1320", {"start": v(-146.25, -94.05) * mm, "end": v(-146.19, -93.77) * mm});
            skLineSegment(sketch, "E1321", {"start": v(-146.19, -93.77) * mm, "end": v(-146.1, -93.38) * mm});
            skLineSegment(sketch, "E1322", {"start": v(-146.1, -93.38) * mm, "end": v(-145.5, -91.51) * mm});
            skLineSegment(sketch, "E1323", {"start": v(-145.5, -91.51) * mm, "end": v(-144.78, -89.69) * mm});
            skLineSegment(sketch, "E1324", {"start": v(-144.78, -89.69) * mm, "end": v(-144.64, -89.32) * mm});
            skLineSegment(sketch, "E1325", {"start": v(-144.64, -89.32) * mm, "end": v(-144.36, -88.52) * mm});
            skLineSegment(sketch, "E1326", {"start": v(-144.36, -88.52) * mm, "end": v(-142.88, -86.36) * mm});
            skLineSegment(sketch, "E1327", {"start": v(-142.88, -86.36) * mm, "end": v(-140.43, -84.67) * mm});
            skLineSegment(sketch, "E1328", {"start": v(-140.43, -84.67) * mm, "end": v(-137.6, -84.02) * mm});
            skLineSegment(sketch, "E1329", {"start": v(-137.6, -84.02) * mm, "end": v(-135.38, -84.05) * mm});
            skLineSegment(sketch, "E1330", {"start": v(-135.38, -84.05) * mm, "end": v(-134.66, -84.16) * mm});
            skLineSegment(sketch, "E1331", {"start": v(-134.66, -84.16) * mm, "end": v(-134.51, -84.19) * mm});
            skLineSegment(sketch, "E1332", {"start": v(-134.51, -84.19) * mm, "end": v(-133, -84.5) * mm});
            skLineSegment(sketch, "E1333", {"start": v(-133, -84.5) * mm, "end": v(-132.85, -84.54) * mm});
            skLineSegment(sketch, "E1334", {"start": v(-148.17, -14.1) * mm, "end": v(-147.47, -14.43) * mm});
            skLineSegment(sketch, "E1335", {"start": v(-147.47, -14.43) * mm, "end": v(-143.89, -15.79) * mm});
            skLineSegment(sketch, "E1336", {"start": v(-143.89, -15.79) * mm, "end": v(-140.25, -17.02) * mm});
            skLineSegment(sketch, "E1337", {"start": v(-140.25, -17.02) * mm, "end": v(-139.53, -17.28) * mm});
            skLineSegment(sketch, "E1338", {"start": v(-139.53, -17.28) * mm, "end": v(-138.3, -17.74) * mm});
            skLineSegment(sketch, "E1339", {"start": v(-138.3, -17.74) * mm, "end": v(-132.08, -19.9) * mm});
            skLineSegment(sketch, "E1340", {"start": v(-132.08, -19.9) * mm, "end": v(-125.9, -22.12) * mm});
            skLineSegment(sketch, "E1341", {"start": v(-125.9, -22.12) * mm, "end": v(-124.67, -22.61) * mm});
            skLineSegment(sketch, "E1342", {"start": v(-124.67, -22.61) * mm, "end": v(-124.53, -22.67) * mm});
            skLineSegment(sketch, "E1343", {"start": v(-124.53, -22.67) * mm, "end": v(-123.05, -23.09) * mm});
            skLineSegment(sketch, "E1344", {"start": v(-123.05, -23.09) * mm, "end": v(-122.9, -23.11) * mm});
            skLineSegment(sketch, "E1345", {"start": v(-122.9, -23.11) * mm, "end": v(-122.64, -23.15) * mm});
            skLineSegment(sketch, "E1346", {"start": v(-122.64, -23.15) * mm, "end": v(-121.84, -23.12) * mm});
            skLineSegment(sketch, "E1347", {"start": v(-121.84, -23.12) * mm, "end": v(-120.94, -22.82) * mm});
            skLineSegment(sketch, "E1348", {"start": v(-120.94, -22.82) * mm, "end": v(-120.17, -22.24) * mm});
            skLineSegment(sketch, "E1349", {"start": v(-120.17, -22.24) * mm, "end": v(-119.67, -21.6) * mm});
            skLineSegment(sketch, "E1350", {"start": v(-119.67, -21.6) * mm, "end": v(-119.54, -21.37) * mm});
            skLineSegment(sketch, "E1351", {"start": v(-119.54, -21.37) * mm, "end": v(-119.5, -21.29) * mm});
            skLineSegment(sketch, "E1352", {"start": v(-119.5, -21.29) * mm, "end": v(-119.4, -21.01) * mm});
            skLineSegment(sketch, "E1353", {"start": v(-119.4, -21.01) * mm, "end": v(-119.27, -20.64) * mm});
            skLineSegment(sketch, "E1354", {"start": v(-119.27, -20.64) * mm, "end": v(-119.01, -20.41) * mm});
            skLineSegment(sketch, "E1355", {"start": v(-119.01, -20.41) * mm, "end": v(-118.63, -20.45) * mm});
            skLineSegment(sketch, "E1356", {"start": v(-118.63, -20.45) * mm, "end": v(-118.52, -20.5) * mm});
            skLineSegment(sketch, "E1357", {"start": v(-118.52, -20.5) * mm, "end": v(-118.41, -20.55) * mm});
            skLineSegment(sketch, "E1358", {"start": v(-118.41, -20.55) * mm, "end": v(-118.15, -20.82) * mm});
            skLineSegment(sketch, "E1359", {"start": v(-118.15, -20.82) * mm, "end": v(-118.13, -21.18) * mm});
            skLineSegment(sketch, "E1360", {"start": v(-118.13, -21.18) * mm, "end": v(-118.27, -21.56) * mm});
            skLineSegment(sketch, "E1361", {"start": v(-118.27, -21.56) * mm, "end": v(-118.4, -21.83) * mm});
            skLineSegment(sketch, "E1362", {"start": v(-118.4, -21.83) * mm, "end": v(-118.42, -21.92) * mm});
            skLineSegment(sketch, "E1363", {"start": v(-118.42, -21.92) * mm, "end": v(-118.56, -22.36) * mm});
            skLineSegment(sketch, "E1364", {"start": v(-118.56, -22.36) * mm, "end": v(-119.97, -26.76) * mm});
            skLineSegment(sketch, "E1365", {"start": v(-119.97, -26.76) * mm, "end": v(-120.11, -27.2) * mm});
            skLineSegment(sketch, "E1366", {"start": v(-120.11, -27.2) * mm, "end": v(-120.3, -27.73) * mm});
            skLineSegment(sketch, "E1367", {"start": v(-120.3, -27.73) * mm, "end": v(-122.07, -33.03) * mm});
            skLineSegment(sketch, "E1368", {"start": v(-122.07, -33.03) * mm, "end": v(-122.2, -33.58) * mm});
            skLineSegment(sketch, "E1369", {"start": v(-122.2, -33.58) * mm, "end": v(-122.22, -33.66) * mm});
            skLineSegment(sketch, "E1370", {"start": v(-122.22, -33.66) * mm, "end": v(-122.42, -34.04) * mm});
            skLineSegment(sketch, "E1371", {"start": v(-122.42, -34.04) * mm, "end": v(-122.77, -34.22) * mm});
            skLineSegment(sketch, "E1372", {"start": v(-122.77, -34.22) * mm, "end": v(-122.87, -34.2) * mm});
            skLineSegment(sketch, "E1373", {"start": v(-122.87, -34.2) * mm, "end": v(-122.98, -34.2) * mm});
            skLineSegment(sketch, "E1374", {"start": v(-122.98, -34.2) * mm, "end": v(-123.27, -33.93) * mm});
            skLineSegment(sketch, "E1375", {"start": v(-123.27, -33.93) * mm, "end": v(-123.3, -33.52) * mm});
            skLineSegment(sketch, "E1376", {"start": v(-123.3, -33.52) * mm, "end": v(-123.28, -33.43) * mm});
            skLineSegment(sketch, "E1377", {"start": v(-123.28, -33.43) * mm, "end": v(-123.26, -33.31) * mm});
            skLineSegment(sketch, "E1378", {"start": v(-123.26, -33.31) * mm, "end": v(-123.18, -32.13) * mm});
            skLineSegment(sketch, "E1379", {"start": v(-123.18, -32.13) * mm, "end": v(-123.2, -32) * mm});
            skLineSegment(sketch, "E1380", {"start": v(-123.2, -32) * mm, "end": v(-123.24, -31.79) * mm});
            skLineSegment(sketch, "E1381", {"start": v(-123.24, -31.79) * mm, "end": v(-123.63, -30.85) * mm});
            skLineSegment(sketch, "E1382", {"start": v(-123.63, -30.85) * mm, "end": v(-124.37, -30.2) * mm});
            skLineSegment(sketch, "E1383", {"start": v(-124.37, -30.2) * mm, "end": v(-124.58, -30.12) * mm});
            skLineSegment(sketch, "E1384", {"start": v(-124.58, -30.12) * mm, "end": v(-125.76, -29.67) * mm});
            skLineSegment(sketch, "E1385", {"start": v(-125.76, -29.67) * mm, "end": v(-131.58, -27.39) * mm});
            skLineSegment(sketch, "E1386", {"start": v(-131.58, -27.39) * mm, "end": v(-137.44, -25.2) * mm});
            skLineSegment(sketch, "E1387", {"start": v(-137.44, -25.2) * mm, "end": v(-138.63, -24.8) * mm});
            skLineSegment(sketch, "E1388", {"start": v(-138.63, -24.8) * mm, "end": v(-138.66, -24.8) * mm});
            skLineSegment(sketch, "E1389", {"start": v(-138.66, -24.8) * mm, "end": v(-139, -24.8) * mm});
            skLineSegment(sketch, "E1390", {"start": v(-139, -24.8) * mm, "end": v(-139.03, -24.8) * mm});
            skLineSegment(sketch, "E1391", {"start": v(-139.03, -24.8) * mm, "end": v(-140.35, -24.27) * mm});
            skLineSegment(sketch, "E1392", {"start": v(-140.35, -24.27) * mm, "end": v(-153.7, -19.44) * mm});
            skLineSegment(sketch, "E1393", {"start": v(-153.7, -19.44) * mm, "end": v(-155.04, -19.02) * mm});
            skLineSegment(sketch, "E1394", {"start": v(-155.04, -19.02) * mm, "end": v(-155.24, -18.96) * mm});
            skLineSegment(sketch, "E1395", {"start": v(-155.24, -18.96) * mm, "end": v(-155.83, -18.79) * mm});
            skLineSegment(sketch, "E1396", {"start": v(-155.83, -18.79) * mm, "end": v(-156.45, -18.66) * mm});
            skLineSegment(sketch, "E1397", {"start": v(-156.45, -18.66) * mm, "end": v(-156.93, -18.64) * mm});
            skLineSegment(sketch, "E1398", {"start": v(-156.93, -18.64) * mm, "end": v(-157.32, -18.75) * mm});
            skLineSegment(sketch, "E1399", {"start": v(-157.32, -18.75) * mm, "end": v(-157.64, -19) * mm});
            skLineSegment(sketch, "E1400", {"start": v(-157.64, -19) * mm, "end": v(-157.93, -19.4) * mm});
            skLineSegment(sketch, "E1401", {"start": v(-157.93, -19.4) * mm, "end": v(-158.23, -19.96) * mm});
            skLineSegment(sketch, "E1402", {"start": v(-158.23, -19.96) * mm, "end": v(-158.49, -20.53) * mm});
            skLineSegment(sketch, "E1403", {"start": v(-158.49, -20.53) * mm, "end": v(-158.57, -20.71) * mm});
            skLineSegment(sketch, "E1404", {"start": v(-158.57, -20.71) * mm, "end": v(-158.6, -20.8) * mm});
            skLineSegment(sketch, "E1405", {"start": v(-158.6, -20.8) * mm, "end": v(-158.84, -21.14) * mm});
            skLineSegment(sketch, "E1406", {"start": v(-158.84, -21.14) * mm, "end": v(-159.22, -21.32) * mm});
            skLineSegment(sketch, "E1407", {"start": v(-159.22, -21.32) * mm, "end": v(-159.33, -21.32) * mm});
            skLineSegment(sketch, "E1408", {"start": v(-159.33, -21.32) * mm, "end": v(-159.44, -21.26) * mm});
            skLineSegment(sketch, "E1409", {"start": v(-159.44, -21.26) * mm, "end": v(-159.63, -20.84) * mm});
            skLineSegment(sketch, "E1410", {"start": v(-159.63, -20.84) * mm, "end": v(-159.58, -20.37) * mm});
            skLineSegment(sketch, "E1411", {"start": v(-159.58, -20.37) * mm, "end": v(-159.56, -20.28) * mm});
            skLineSegment(sketch, "E1412", {"start": v(-159.56, -20.28) * mm, "end": v(-159.39, -19.32) * mm});
            skLineSegment(sketch, "E1413", {"start": v(-159.39, -19.32) * mm, "end": v(-157.62, -9.73) * mm});
            skLineSegment(sketch, "E1414", {"start": v(-157.62, -9.73) * mm, "end": v(-157.44, -8.77) * mm});
            skLineSegment(sketch, "E1415", {"start": v(-157.44, -8.77) * mm, "end": v(-157.42, -8.68) * mm});
            skLineSegment(sketch, "E1416", {"start": v(-157.42, -8.68) * mm, "end": v(-157.39, -8.38) * mm});
            skLineSegment(sketch, "E1417", {"start": v(-157.39, -8.38) * mm, "end": v(-157.31, -7.96) * mm});
            skLineSegment(sketch, "E1418", {"start": v(-157.31, -7.96) * mm, "end": v(-157.12, -7.64) * mm});
            skLineSegment(sketch, "E1419", {"start": v(-157.12, -7.64) * mm, "end": v(-156.8, -7.54) * mm});
            skLineSegment(sketch, "E1420", {"start": v(-156.8, -7.54) * mm, "end": v(-156.71, -7.55) * mm});
            skLineSegment(sketch, "E1421", {"start": v(-156.71, -7.55) * mm, "end": v(-156.6, -7.56) * mm});
            skLineSegment(sketch, "E1422", {"start": v(-156.6, -7.56) * mm, "end": v(-156.31, -7.73) * mm});
            skLineSegment(sketch, "E1423", {"start": v(-156.31, -7.73) * mm, "end": v(-156.22, -8.07) * mm});
            skLineSegment(sketch, "E1424", {"start": v(-156.22, -8.07) * mm, "end": v(-156.28, -8.48) * mm});
            skLineSegment(sketch, "E1425", {"start": v(-156.28, -8.48) * mm, "end": v(-156.34, -8.79) * mm});
            skLineSegment(sketch, "E1426", {"start": v(-156.34, -8.79) * mm, "end": v(-156.34, -8.9) * mm});
            skLineSegment(sketch, "E1427", {"start": v(-156.34, -8.9) * mm, "end": v(-156.35, -9.19) * mm});
            skLineSegment(sketch, "E1428", {"start": v(-156.35, -9.19) * mm, "end": v(-156.27, -10.07) * mm});
            skLineSegment(sketch, "E1429", {"start": v(-156.27, -10.07) * mm, "end": v(-155.9, -11) * mm});
            skLineSegment(sketch, "E1430", {"start": v(-155.9, -11) * mm, "end": v(-155.17, -11.72) * mm});
            skLineSegment(sketch, "E1431", {"start": v(-155.17, -11.72) * mm, "end": v(-154.32, -12.17) * mm});
            skLineSegment(sketch, "E1432", {"start": v(-154.32, -12.17) * mm, "end": v(-154.02, -12.28) * mm});
            skLineSegment(sketch, "E1433", {"start": v(-154.02, -12.28) * mm, "end": v(-153.54, -12.46) * mm});
            skLineSegment(sketch, "E1434", {"start": v(-153.54, -12.46) * mm, "end": v(-148.66, -13.95) * mm});
            skLineSegment(sketch, "E1435", {"start": v(-148.66, -13.95) * mm, "end": v(-148.17, -14.1) * mm});
            skLineSegment(sketch, "E1436", {"start": v(-151.8, -139.59) * mm, "end": v(-151.08, -139.47) * mm});
            skLineSegment(sketch, "E1437", {"start": v(-151.08, -139.47) * mm, "end": v(-144.36, -138.37) * mm});
            skLineSegment(sketch, "E1438", {"start": v(-144.36, -138.37) * mm, "end": v(-143.7, -138.25) * mm});
            skLineSegment(sketch, "E1439", {"start": v(-143.7, -138.25) * mm, "end": v(-143.57, -138.23) * mm});
            skLineSegment(sketch, "E1440", {"start": v(-143.57, -138.23) * mm, "end": v(-143.02, -138.33) * mm});
            skLineSegment(sketch, "E1441", {"start": v(-143.02, -138.33) * mm, "end": v(-142.63, -138.73) * mm});
            skLineSegment(sketch, "E1442", {"start": v(-142.63, -138.73) * mm, "end": v(-142.56, -138.85) * mm});
            skLineSegment(sketch, "E1443", {"start": v(-142.56, -138.85) * mm, "end": v(-142.51, -138.94) * mm});
            skLineSegment(sketch, "E1444", {"start": v(-142.51, -138.94) * mm, "end": v(-142.43, -139.25) * mm});
            skLineSegment(sketch, "E1445", {"start": v(-142.43, -139.25) * mm, "end": v(-142.53, -139.55) * mm});
            skLineSegment(sketch, "E1446", {"start": v(-142.53, -139.55) * mm, "end": v(-142.76, -139.77) * mm});
            skLineSegment(sketch, "E1447", {"start": v(-142.76, -139.77) * mm, "end": v(-142.98, -139.92) * mm});
            skLineSegment(sketch, "E1448", {"start": v(-142.98, -139.92) * mm, "end": v(-143.05, -139.97) * mm});
            skLineSegment(sketch, "E1449", {"start": v(-143.05, -139.97) * mm, "end": v(-143.23, -140.1) * mm});
            skLineSegment(sketch, "E1450", {"start": v(-143.23, -140.1) * mm, "end": v(-144.15, -140.72) * mm});
            skLineSegment(sketch, "E1451", {"start": v(-144.15, -140.72) * mm, "end": v(-145.1, -141.3) * mm});
            skLineSegment(sketch, "E1452", {"start": v(-145.1, -141.3) * mm, "end": v(-145.3, -141.39) * mm});
            skLineSegment(sketch, "E1453", {"start": v(-145.3, -141.39) * mm, "end": v(-145.5, -141.47) * mm});
            skLineSegment(sketch, "E1454", {"start": v(-145.5, -141.47) * mm, "end": v(-146.12, -142.12) * mm});
            skLineSegment(sketch, "E1455", {"start": v(-146.12, -142.12) * mm, "end": v(-146.18, -143.02) * mm});
            skLineSegment(sketch, "E1456", {"start": v(-146.18, -143.02) * mm, "end": v(-146.1, -143.24) * mm});
            skLineSegment(sketch, "E1457", {"start": v(-146.1, -143.24) * mm, "end": v(-146.02, -143.44) * mm});
            skLineSegment(sketch, "E1458", {"start": v(-146.02, -143.44) * mm, "end": v(-145.3, -145.54) * mm});
            skLineSegment(sketch, "E1459", {"start": v(-145.3, -145.54) * mm, "end": v(-145.23, -145.75) * mm});
            skLineSegment(sketch, "E1460", {"start": v(-145.23, -145.75) * mm, "end": v(-145.17, -145.96) * mm});
            skLineSegment(sketch, "E1461", {"start": v(-145.17, -145.96) * mm, "end": v(-144.94, -146.6) * mm});
            skLineSegment(sketch, "E1462", {"start": v(-144.94, -146.6) * mm, "end": v(-144.64, -147) * mm});
            skLineSegment(sketch, "E1463", {"start": v(-144.64, -147) * mm, "end": v(-144.14, -147.09) * mm});
            skLineSegment(sketch, "E1464", {"start": v(-144.14, -147.09) * mm, "end": v(-143.48, -147) * mm});
            skLineSegment(sketch, "E1465", {"start": v(-143.48, -147) * mm, "end": v(-143.26, -146.96) * mm});
            skLineSegment(sketch, "E1466", {"start": v(-143.26, -146.96) * mm, "end": v(-142.5, -146.82) * mm});
            skLineSegment(sketch, "E1467", {"start": v(-142.5, -146.82) * mm, "end": v(-134.94, -145.44) * mm});
            skLineSegment(sketch, "E1468", {"start": v(-134.94, -145.44) * mm, "end": v(-134.18, -145.3) * mm});
            skLineSegment(sketch, "E1469", {"start": v(-134.18, -145.3) * mm, "end": v(-133.5, -145.17) * mm});
            skLineSegment(sketch, "E1470", {"start": v(-133.5, -145.17) * mm, "end": v(-126.78, -143.92) * mm});
            skLineSegment(sketch, "E1471", {"start": v(-126.78, -143.92) * mm, "end": v(-126.1, -143.79) * mm});
            skLineSegment(sketch, "E1472", {"start": v(-126.1, -143.79) * mm, "end": v(-125.99, -143.77) * mm});
            skLineSegment(sketch, "E1473", {"start": v(-125.99, -143.77) * mm, "end": v(-124.83, -143.48) * mm});
            skLineSegment(sketch, "E1474", {"start": v(-124.83, -143.48) * mm, "end": v(-124.71, -143.47) * mm});
            skLineSegment(sketch, "E1475", {"start": v(-124.71, -143.47) * mm, "end": v(-124.51, -143.44) * mm});
            skLineSegment(sketch, "E1476", {"start": v(-124.51, -143.44) * mm, "end": v(-123.92, -143.22) * mm});
            skLineSegment(sketch, "E1477", {"start": v(-123.92, -143.22) * mm, "end": v(-123.4, -142.78) * mm});
            skLineSegment(sketch, "E1478", {"start": v(-123.4, -142.78) * mm, "end": v(-123.1, -142.15) * mm});
            skLineSegment(sketch, "E1479", {"start": v(-123.1, -142.15) * mm, "end": v(-123.01, -141.53) * mm});
            skLineSegment(sketch, "E1480", {"start": v(-123.01, -141.53) * mm, "end": v(-123.01, -141.33) * mm});
            skLineSegment(sketch, "E1481", {"start": v(-123.01, -141.33) * mm, "end": v(-123.01, -141.18) * mm});
            skLineSegment(sketch, "E1482", {"start": v(-123.01, -141.18) * mm, "end": v(-123.04, -140.72) * mm});
            skLineSegment(sketch, "E1483", {"start": v(-123.04, -140.72) * mm, "end": v(-123.01, -140.12) * mm});
            skLineSegment(sketch, "E1484", {"start": v(-123.01, -140.12) * mm, "end": v(-122.73, -139.67) * mm});
            skLineSegment(sketch, "E1485", {"start": v(-122.73, -139.67) * mm, "end": v(-122.2, -139.51) * mm});
            skLineSegment(sketch, "E1486", {"start": v(-122.2, -139.51) * mm, "end": v(-122.02, -139.52) * mm});
            skLineSegment(sketch, "E1487", {"start": v(-122.02, -139.52) * mm, "end": v(-121.87, -139.53) * mm});
            skLineSegment(sketch, "E1488", {"start": v(-121.87, -139.53) * mm, "end": v(-121.43, -139.74) * mm});
            skLineSegment(sketch, "E1489", {"start": v(-121.43, -139.74) * mm, "end": v(-121.23, -140.2) * mm});
            skLineSegment(sketch, "E1490", {"start": v(-121.23, -140.2) * mm, "end": v(-121.23, -140.77) * mm});
            skLineSegment(sketch, "E1491", {"start": v(-121.23, -140.77) * mm, "end": v(-121.26, -141.19) * mm});
            skLineSegment(sketch, "E1492", {"start": v(-121.26, -141.19) * mm, "end": v(-121.24, -141.32) * mm});
            skLineSegment(sketch, "E1493", {"start": v(-121.24, -141.32) * mm, "end": v(-121.15, -141.98) * mm});
            skLineSegment(sketch, "E1494", {"start": v(-121.15, -141.98) * mm, "end": v(-120.65, -145.27) * mm});
            skLineSegment(sketch, "E1495", {"start": v(-120.65, -145.27) * mm, "end": v(-119.84, -148.5) * mm});
            skLineSegment(sketch, "E1496", {"start": v(-119.84, -148.5) * mm, "end": v(-119.61, -149.13) * mm});
            skLineSegment(sketch, "E1497", {"start": v(-119.61, -149.13) * mm, "end": v(-119.6, -149.16) * mm});
            skLineSegment(sketch, "E1498", {"start": v(-119.6, -149.16) * mm, "end": v(-119.5, -149.5) * mm});
            skLineSegment(sketch, "E1499", {"start": v(-119.5, -149.5) * mm, "end": v(-119.49, -149.52) * mm});
            skLineSegment(sketch, "E1500", {"start": v(-119.49, -149.52) * mm, "end": v(-119.46, -149.65) * mm});
            skLineSegment(sketch, "E1501", {"start": v(-119.46, -149.65) * mm, "end": v(-119.34, -150.02) * mm});
            skLineSegment(sketch, "E1502", {"start": v(-119.34, -150.02) * mm, "end": v(-119.2, -150.51) * mm});
            skLineSegment(sketch, "E1503", {"start": v(-119.2, -150.51) * mm, "end": v(-119.27, -150.96) * mm});
            skLineSegment(sketch, "E1504", {"start": v(-119.27, -150.96) * mm, "end": v(-119.58, -151.26) * mm});
            skLineSegment(sketch, "E1505", {"start": v(-119.58, -151.26) * mm, "end": v(-119.7, -151.3) * mm});
            skLineSegment(sketch, "E1506", {"start": v(-119.7, -151.3) * mm, "end": v(-119.82, -151.36) * mm});
            skLineSegment(sketch, "E1507", {"start": v(-119.82, -151.36) * mm, "end": v(-120.24, -151.37) * mm});
            skLineSegment(sketch, "E1508", {"start": v(-120.24, -151.37) * mm, "end": v(-120.67, -151.14) * mm});
            skLineSegment(sketch, "E1509", {"start": v(-120.67, -151.14) * mm, "end": v(-121, -150.73) * mm});
            skLineSegment(sketch, "E1510", {"start": v(-121, -150.73) * mm, "end": v(-121.18, -150.4) * mm});
            skLineSegment(sketch, "E1511", {"start": v(-121.18, -150.4) * mm, "end": v(-121.23, -150.27) * mm});
            skLineSegment(sketch, "E1512", {"start": v(-121.23, -150.27) * mm, "end": v(-121.37, -149.93) * mm});
            skLineSegment(sketch, "E1513", {"start": v(-121.37, -149.93) * mm, "end": v(-122.03, -149) * mm});
            skLineSegment(sketch, "E1514", {"start": v(-122.03, -149) * mm, "end": v(-123.07, -148.35) * mm});
            skLineSegment(sketch, "E1515", {"start": v(-123.07, -148.35) * mm, "end": v(-124.31, -148.2) * mm});
            skLineSegment(sketch, "E1516", {"start": v(-124.31, -148.2) * mm, "end": v(-125.4, -148.3) * mm});
            skLineSegment(sketch, "E1517", {"start": v(-125.4, -148.3) * mm, "end": v(-125.74, -148.38) * mm});
            skLineSegment(sketch, "E1518", {"start": v(-125.74, -148.38) * mm, "end": v(-127.08, -148.66) * mm});
            skLineSegment(sketch, "E1519", {"start": v(-127.08, -148.66) * mm, "end": v(-140.51, -151.31) * mm});
            skLineSegment(sketch, "E1520", {"start": v(-140.51, -151.31) * mm, "end": v(-141.85, -151.58) * mm});
            skLineSegment(sketch, "E1521", {"start": v(-141.85, -151.58) * mm, "end": v(-142.06, -151.62) * mm});
            skLineSegment(sketch, "E1522", {"start": v(-142.06, -151.62) * mm, "end": v(-142.65, -151.78) * mm});
            skLineSegment(sketch, "E1523", {"start": v(-142.65, -151.78) * mm, "end": v(-143.03, -152.06) * mm});
            skLineSegment(sketch, "E1524", {"start": v(-143.03, -152.06) * mm, "end": v(-143.1, -152.55) * mm});
            skLineSegment(sketch, "E1525", {"start": v(-143.1, -152.55) * mm, "end": v(-142.96, -153.18) * mm});
            skLineSegment(sketch, "E1526", {"start": v(-142.96, -153.18) * mm, "end": v(-142.91, -153.38) * mm});
            skLineSegment(sketch, "E1527", {"start": v(-142.91, -153.38) * mm, "end": v(-142.89, -153.47) * mm});
            skLineSegment(sketch, "E1528", {"start": v(-142.89, -153.47) * mm, "end": v(-142.66, -154.3) * mm});
            skLineSegment(sketch, "E1529", {"start": v(-142.66, -154.3) * mm, "end": v(-142.65, -154.38) * mm});
            skLineSegment(sketch, "E1530", {"start": v(-142.65, -154.38) * mm, "end": v(-142.6, -154.79) * mm});
            skLineSegment(sketch, "E1531", {"start": v(-142.6, -154.79) * mm, "end": v(-142.24, -156) * mm});
            skLineSegment(sketch, "E1532", {"start": v(-142.24, -156) * mm, "end": v(-141.43, -157.24) * mm});
            skLineSegment(sketch, "E1533", {"start": v(-141.43, -157.24) * mm, "end": v(-140.22, -158.08) * mm});
            skLineSegment(sketch, "E1534", {"start": v(-140.22, -158.08) * mm, "end": v(-139.01, -158.48) * mm});
            skLineSegment(sketch, "E1535", {"start": v(-139.01, -158.48) * mm, "end": v(-138.6, -158.53) * mm});
            skLineSegment(sketch, "E1536", {"start": v(-138.6, -158.53) * mm, "end": v(-138.58, -158.54) * mm});
            skLineSegment(sketch, "E1537", {"start": v(-138.58, -158.54) * mm, "end": v(-138.41, -158.57) * mm});
            skLineSegment(sketch, "E1538", {"start": v(-138.41, -158.57) * mm, "end": v(-138.4, -158.57) * mm});
            skLineSegment(sketch, "E1539", {"start": v(-138.4, -158.57) * mm, "end": v(-138.3, -158.6) * mm});
            skLineSegment(sketch, "E1540", {"start": v(-138.3, -158.6) * mm, "end": v(-138, -158.68) * mm});
            skLineSegment(sketch, "E1541", {"start": v(-138, -158.68) * mm, "end": v(-137.65, -158.86) * mm});
            skLineSegment(sketch, "E1542", {"start": v(-137.65, -158.86) * mm, "end": v(-137.44, -159.15) * mm});
            skLineSegment(sketch, "E1543", {"start": v(-137.44, -159.15) * mm, "end": v(-137.4, -159.5) * mm});
            skLineSegment(sketch, "E1544", {"start": v(-137.4, -159.5) * mm, "end": v(-137.43, -159.61) * mm});
            skLineSegment(sketch, "E1545", {"start": v(-137.43, -159.61) * mm, "end": v(-137.45, -159.7) * mm});
            skLineSegment(sketch, "E1546", {"start": v(-137.45, -159.7) * mm, "end": v(-137.59, -159.97) * mm});
            skLineSegment(sketch, "E1547", {"start": v(-137.59, -159.97) * mm, "end": v(-137.86, -160.15) * mm});
            skLineSegment(sketch, "E1548", {"start": v(-137.86, -160.15) * mm, "end": v(-138.2, -160.22) * mm});
            skLineSegment(sketch, "E1549", {"start": v(-138.2, -160.22) * mm, "end": v(-138.47, -160.23) * mm});
            skLineSegment(sketch, "E1550", {"start": v(-138.47, -160.23) * mm, "end": v(-138.56, -160.22) * mm});
            skLineSegment(sketch, "E1551", {"start": v(-138.56, -160.22) * mm, "end": v(-138.74, -160.21) * mm});
            skLineSegment(sketch, "E1552", {"start": v(-138.74, -160.21) * mm, "end": v(-140.44, -160.11) * mm});
            skLineSegment(sketch, "E1553", {"start": v(-140.44, -160.11) * mm, "end": v(-140.61, -160.1) * mm});
            skLineSegment(sketch, "E1554", {"start": v(-140.61, -160.1) * mm, "end": v(-140.92, -160.1) * mm});
            skLineSegment(sketch, "E1555", {"start": v(-140.92, -160.1) * mm, "end": v(-142.46, -160) * mm});
            skLineSegment(sketch, "E1556", {"start": v(-142.46, -160) * mm, "end": v(-144, -160) * mm});
            skLineSegment(sketch, "E1557", {"start": v(-144, -160) * mm, "end": v(-144.3, -160.03) * mm});
            skLineSegment(sketch, "E1558", {"start": v(-144.3, -160.03) * mm, "end": v(-144.44, -160.04) * mm});
            skLineSegment(sketch, "E1559", {"start": v(-144.44, -160.04) * mm, "end": v(-144.84, -159.95) * mm});
            skLineSegment(sketch, "E1560", {"start": v(-144.84, -159.95) * mm, "end": v(-145.19, -159.68) * mm});
            skLineSegment(sketch, "E1561", {"start": v(-145.19, -159.68) * mm, "end": v(-145.3, -159.3) * mm});
            skLineSegment(sketch, "E1562", {"start": v(-145.3, -159.3) * mm, "end": v(-145.16, -159) * mm});
            skLineSegment(sketch, "E1563", {"start": v(-145.16, -159) * mm, "end": v(-145.09, -158.93) * mm});
            skLineSegment(sketch, "E1564", {"start": v(-145.09, -158.93) * mm, "end": v(-144.88, -158.74) * mm});
            skLineSegment(sketch, "E1565", {"start": v(-144.88, -158.74) * mm, "end": v(-144.42, -158) * mm});
            skLineSegment(sketch, "E1566", {"start": v(-144.42, -158) * mm, "end": v(-144.28, -157.04) * mm});
            skLineSegment(sketch, "E1567", {"start": v(-144.28, -157.04) * mm, "end": v(-144.47, -156.1) * mm});
            skLineSegment(sketch, "E1568", {"start": v(-144.47, -156.1) * mm, "end": v(-144.7, -155.39) * mm});
            skLineSegment(sketch, "E1569", {"start": v(-144.7, -155.39) * mm, "end": v(-144.77, -155.15) * mm});
            skLineSegment(sketch, "E1570", {"start": v(-144.77, -155.15) * mm, "end": v(-145.08, -154.14) * mm});
            skLineSegment(sketch, "E1571", {"start": v(-145.08, -154.14) * mm, "end": v(-148.31, -144.03) * mm});
            skLineSegment(sketch, "E1572", {"start": v(-148.31, -144.03) * mm, "end": v(-148.64, -143.03) * mm});
            skLineSegment(sketch, "E1573", {"start": v(-148.64, -143.03) * mm, "end": v(-148.7, -142.85) * mm});
            skLineSegment(sketch, "E1574", {"start": v(-148.7, -142.85) * mm, "end": v(-148.9, -142.3) * mm});
            skLineSegment(sketch, "E1575", {"start": v(-148.9, -142.3) * mm, "end": v(-149.27, -141.68) * mm});
            skLineSegment(sketch, "E1576", {"start": v(-149.27, -141.68) * mm, "end": v(-149.83, -141.24) * mm});
            skLineSegment(sketch, "E1577", {"start": v(-149.83, -141.24) * mm, "end": v(-150.47, -141.09) * mm});
            skLineSegment(sketch, "E1578", {"start": v(-150.47, -141.09) * mm, "end": v(-150.68, -141.1) * mm});
            skLineSegment(sketch, "E1579", {"start": v(-150.68, -141.1) * mm, "end": v(-150.8, -141.1) * mm});
            skLineSegment(sketch, "E1580", {"start": v(-150.8, -141.1) * mm, "end": v(-151.17, -140.98) * mm});
            skLineSegment(sketch, "E1581", {"start": v(-151.17, -140.98) * mm, "end": v(-151.45, -140.65) * mm});
            skLineSegment(sketch, "E1582", {"start": v(-151.45, -140.65) * mm, "end": v(-151.63, -140.16) * mm});
            skLineSegment(sketch, "E1583", {"start": v(-151.63, -140.16) * mm, "end": v(-151.75, -139.73) * mm});
            skLineSegment(sketch, "E1584", {"start": v(-151.75, -139.73) * mm, "end": v(-151.8, -139.59) * mm});
            skLineSegment(sketch, "E1585", {"start": v(-56.74, -179.54) * mm, "end": v(-56.4, -179.56) * mm});
            skLineSegment(sketch, "E1586", {"start": v(-56.4, -179.56) * mm, "end": v(-54.8, -179.47) * mm});
            skLineSegment(sketch, "E1587", {"start": v(-54.8, -179.47) * mm, "end": v(-53.37, -179.13) * mm});
            skLineSegment(sketch, "E1588", {"start": v(-53.37, -179.13) * mm, "end": v(-53.1, -179.04) * mm});
            skLineSegment(sketch, "E1589", {"start": v(-53.1, -179.04) * mm, "end": v(-52.87, -178.97) * mm});
            skLineSegment(sketch, "E1590", {"start": v(-52.87, -178.97) * mm, "end": v(-52.23, -178.66) * mm});
            skLineSegment(sketch, "E1591", {"start": v(-52.23, -178.66) * mm, "end": v(-51.54, -178.1) * mm});
            skLineSegment(sketch, "E1592", {"start": v(-51.54, -178.1) * mm, "end": v(-51.06, -177.35) * mm});
            skLineSegment(sketch, "E1593", {"start": v(-51.06, -177.35) * mm, "end": v(-50.84, -176.65) * mm});
            skLineSegment(sketch, "E1594", {"start": v(-50.84, -176.65) * mm, "end": v(-50.8, -176.42) * mm});
            skLineSegment(sketch, "E1595", {"start": v(-50.8, -176.42) * mm, "end": v(-50.75, -175.91) * mm});
            skLineSegment(sketch, "E1596", {"start": v(-50.75, -175.91) * mm, "end": v(-50.92, -174.36) * mm});
            skLineSegment(sketch, "E1597", {"start": v(-50.92, -174.36) * mm, "end": v(-51.65, -172.28) * mm});
            skLineSegment(sketch, "E1598", {"start": v(-51.65, -172.28) * mm, "end": v(-52.9, -170.48) * mm});
            skLineSegment(sketch, "E1599", {"start": v(-52.9, -170.48) * mm, "end": v(-54.14, -169.45) * mm});
            skLineSegment(sketch, "E1600", {"start": v(-54.14, -169.45) * mm, "end": v(-54.6, -169.23) * mm});
            skLineSegment(sketch, "E1601", {"start": v(-54.6, -169.23) * mm, "end": v(-55.1, -169) * mm});
            skLineSegment(sketch, "E1602", {"start": v(-55.1, -169) * mm, "end": v(-57.6, -168.49) * mm});
            skLineSegment(sketch, "E1603", {"start": v(-57.6, -168.49) * mm, "end": v(-60.12, -168.28) * mm});
            skLineSegment(sketch, "E1604", {"start": v(-60.12, -168.28) * mm, "end": v(-60.63, -168.21) * mm});
            skLineSegment(sketch, "E1605", {"start": v(-60.63, -168.21) * mm, "end": v(-60.73, -168.2) * mm});
            skLineSegment(sketch, "E1606", {"start": v(-60.73, -168.2) * mm, "end": v(-61.08, -168.38) * mm});
            skLineSegment(sketch, "E1607", {"start": v(-61.08, -168.38) * mm, "end": v(-61.2, -168.78) * mm});
            skLineSegment(sketch, "E1608", {"start": v(-61.2, -168.78) * mm, "end": v(-61.2, -168.88) * mm});
            skLineSegment(sketch, "E1609", {"start": v(-61.2, -168.88) * mm, "end": v(-61.18, -169.01) * mm});
            skLineSegment(sketch, "E1610", {"start": v(-61.18, -169.01) * mm, "end": v(-61.02, -170.37) * mm});
            skLineSegment(sketch, "E1611", {"start": v(-61.02, -170.37) * mm, "end": v(-61, -170.5) * mm});
            skLineSegment(sketch, "E1612", {"start": v(-61, -170.5) * mm, "end": v(-60.91, -171.08) * mm});
            skLineSegment(sketch, "E1613", {"start": v(-60.91, -171.08) * mm, "end": v(-60.05, -176.82) * mm});
            skLineSegment(sketch, "E1614", {"start": v(-60.05, -176.82) * mm, "end": v(-59.97, -177.4) * mm});
            skLineSegment(sketch, "E1615", {"start": v(-59.97, -177.4) * mm, "end": v(-59.94, -177.66) * mm});
            skLineSegment(sketch, "E1616", {"start": v(-59.94, -177.66) * mm, "end": v(-59.81, -178.45) * mm});
            skLineSegment(sketch, "E1617", {"start": v(-59.81, -178.45) * mm, "end": v(-59.53, -179.06) * mm});
            skLineSegment(sketch, "E1618", {"start": v(-59.53, -179.06) * mm, "end": v(-58.97, -179.36) * mm});
            skLineSegment(sketch, "E1619", {"start": v(-58.97, -179.36) * mm, "end": v(-58.21, -179.5) * mm});
            skLineSegment(sketch, "E1620", {"start": v(-58.21, -179.5) * mm, "end": v(-57.96, -179.52) * mm});
            skLineSegment(sketch, "E1621", {"start": v(-57.96, -179.52) * mm, "end": v(-57.84, -179.54) * mm});
            skLineSegment(sketch, "E1622", {"start": v(-57.84, -179.54) * mm, "end": v(-57.27, -179.55) * mm});
            skLineSegment(sketch, "E1623", {"start": v(-57.27, -179.55) * mm, "end": v(-56.87, -179.54) * mm});
            skLineSegment(sketch, "E1624", {"start": v(-56.87, -179.54) * mm, "end": v(-56.74, -179.54) * mm});
            skLineSegment(sketch, "E1625", {"start": v(-48.13, -181.51) * mm, "end": v(-47.66, -182.08) * mm});
            skLineSegment(sketch, "E1626", {"start": v(-47.66, -182.08) * mm, "end": v(-43.08, -187.52) * mm});
            skLineSegment(sketch, "E1627", {"start": v(-43.08, -187.52) * mm, "end": v(-42.63, -188.05) * mm});
            skLineSegment(sketch, "E1628", {"start": v(-42.63, -188.05) * mm, "end": v(-42.43, -188.3) * mm});
            skLineSegment(sketch, "E1629", {"start": v(-42.43, -188.3) * mm, "end": v(-41.41, -189.45) * mm});
            skLineSegment(sketch, "E1630", {"start": v(-41.41, -189.45) * mm, "end": v(-40.43, -190.64) * mm});
            skLineSegment(sketch, "E1631", {"start": v(-40.43, -190.64) * mm, "end": v(-40.25, -190.9) * mm});
            skLineSegment(sketch, "E1632", {"start": v(-40.25, -190.9) * mm, "end": v(-40, -191.24) * mm});
            skLineSegment(sketch, "E1633", {"start": v(-40, -191.24) * mm, "end": v(-39.2, -192.24) * mm});
            skLineSegment(sketch, "E1634", {"start": v(-39.2, -192.24) * mm, "end": v(-38.03, -193.43) * mm});
            skLineSegment(sketch, "E1635", {"start": v(-38.03, -193.43) * mm, "end": v(-36.67, -194.38) * mm});
            skLineSegment(sketch, "E1636", {"start": v(-36.67, -194.38) * mm, "end": v(-35.48, -194.9) * mm});
            skLineSegment(sketch, "E1637", {"start": v(-35.48, -194.9) * mm, "end": v(-35.06, -195.01) * mm});
            skLineSegment(sketch, "E1638", {"start": v(-35.06, -195.01) * mm, "end": v(-35.04, -195.02) * mm});
            skLineSegment(sketch, "E1639", {"start": v(-35.04, -195.02) * mm, "end": v(-34.9, -195.1) * mm});
            skLineSegment(sketch, "E1640", {"start": v(-34.9, -195.1) * mm, "end": v(-34.88, -195.11) * mm});
            skLineSegment(sketch, "E1641", {"start": v(-34.88, -195.11) * mm, "end": v(-34.77, -195.18) * mm});
            skLineSegment(sketch, "E1642", {"start": v(-34.77, -195.18) * mm, "end": v(-34.43, -195.37) * mm});
            skLineSegment(sketch, "E1643", {"start": v(-34.43, -195.37) * mm, "end": v(-33.98, -195.65) * mm});
            skLineSegment(sketch, "E1644", {"start": v(-33.98, -195.65) * mm, "end": v(-33.7, -196) * mm});
            skLineSegment(sketch, "E1645", {"start": v(-33.7, -196) * mm, "end": v(-33.68, -196.42) * mm});
            skLineSegment(sketch, "E1646", {"start": v(-33.68, -196.42) * mm, "end": v(-33.72, -196.54) * mm});
            skLineSegment(sketch, "E1647", {"start": v(-33.72, -196.54) * mm, "end": v(-33.76, -196.63) * mm});
            skLineSegment(sketch, "E1648", {"start": v(-33.76, -196.63) * mm, "end": v(-34.01, -196.86) * mm});
            skLineSegment(sketch, "E1649", {"start": v(-34.01, -196.86) * mm, "end": v(-34.43, -196.92) * mm});
            skLineSegment(sketch, "E1650", {"start": v(-34.43, -196.92) * mm, "end": v(-34.9, -196.84) * mm});
            skLineSegment(sketch, "E1651", {"start": v(-34.9, -196.84) * mm, "end": v(-35.25, -196.77) * mm});
            skLineSegment(sketch, "E1652", {"start": v(-35.25, -196.77) * mm, "end": v(-35.37, -196.75) * mm});
            skLineSegment(sketch, "E1653", {"start": v(-35.37, -196.75) * mm, "end": v(-36.01, -196.68) * mm});
            skLineSegment(sketch, "E1654", {"start": v(-36.01, -196.68) * mm, "end": v(-39.24, -196.28) * mm});
            skLineSegment(sketch, "E1655", {"start": v(-39.24, -196.28) * mm, "end": v(-42.48, -196.1) * mm});
            skLineSegment(sketch, "E1656", {"start": v(-42.48, -196.1) * mm, "end": v(-43.13, -196.15) * mm});
            skLineSegment(sketch, "E1657", {"start": v(-43.13, -196.15) * mm, "end": v(-43.33, -196.16) * mm});
            skLineSegment(sketch, "E1658", {"start": v(-43.33, -196.16) * mm, "end": v(-43.94, -196.12) * mm});
            skLineSegment(sketch, "E1659", {"start": v(-43.94, -196.12) * mm, "end": v(-44.62, -195.9) * mm});
            skLineSegment(sketch, "E1660", {"start": v(-44.62, -195.9) * mm, "end": v(-45.2, -195.5) * mm});
            skLineSegment(sketch, "E1661", {"start": v(-45.2, -195.5) * mm, "end": v(-45.6, -195.07) * mm});
            skLineSegment(sketch, "E1662", {"start": v(-45.6, -195.07) * mm, "end": v(-45.7, -194.9) * mm});
            skLineSegment(sketch, "E1663", {"start": v(-45.7, -194.9) * mm, "end": v(-46.14, -194.27) * mm});
            skLineSegment(sketch, "E1664", {"start": v(-46.14, -194.27) * mm, "end": v(-50.51, -187.91) * mm});
            skLineSegment(sketch, "E1665", {"start": v(-50.51, -187.91) * mm, "end": v(-50.95, -187.28) * mm});
            skLineSegment(sketch, "E1666", {"start": v(-50.95, -187.28) * mm, "end": v(-51.2, -186.93) * mm});
            skLineSegment(sketch, "E1667", {"start": v(-51.2, -186.93) * mm, "end": v(-53.75, -183.5) * mm});
            skLineSegment(sketch, "E1668", {"start": v(-53.75, -183.5) * mm, "end": v(-54, -183.15) * mm});
            skLineSegment(sketch, "E1669", {"start": v(-54, -183.15) * mm, "end": v(-54.2, -182.9) * mm});
            skLineSegment(sketch, "E1670", {"start": v(-54.2, -182.9) * mm, "end": v(-54.95, -182.26) * mm});
            skLineSegment(sketch, "E1671", {"start": v(-54.95, -182.26) * mm, "end": v(-56.04, -181.8) * mm});
            skLineSegment(sketch, "E1672", {"start": v(-56.04, -181.8) * mm, "end": v(-57.23, -181.62) * mm});
            skLineSegment(sketch, "E1673", {"start": v(-57.23, -181.62) * mm, "end": v(-58.16, -181.6) * mm});
            skLineSegment(sketch, "E1674", {"start": v(-58.16, -181.6) * mm, "end": v(-58.47, -181.6) * mm});
            skLineSegment(sketch, "E1675", {"start": v(-58.47, -181.6) * mm, "end": v(-58.57, -181.6) * mm});
            skLineSegment(sketch, "E1676", {"start": v(-58.57, -181.6) * mm, "end": v(-58.87, -181.7) * mm});
            skLineSegment(sketch, "E1677", {"start": v(-58.87, -181.7) * mm, "end": v(-59.08, -181.93) * mm});
            skLineSegment(sketch, "E1678", {"start": v(-59.08, -181.93) * mm, "end": v(-59.15, -182.26) * mm});
            skLineSegment(sketch, "E1679", {"start": v(-59.15, -182.26) * mm, "end": v(-59.14, -182.54) * mm});
            skLineSegment(sketch, "E1680", {"start": v(-59.14, -182.54) * mm, "end": v(-59.13, -182.63) * mm});
            skLineSegment(sketch, "E1681", {"start": v(-59.13, -182.63) * mm, "end": v(-59.09, -182.93) * mm});
            skLineSegment(sketch, "E1682", {"start": v(-59.09, -182.93) * mm, "end": v(-58.64, -185.98) * mm});
            skLineSegment(sketch, "E1683", {"start": v(-58.64, -185.98) * mm, "end": v(-58.59, -186.29) * mm});
            skLineSegment(sketch, "E1684", {"start": v(-58.59, -186.29) * mm, "end": v(-58.53, -186.64) * mm});
            skLineSegment(sketch, "E1685", {"start": v(-58.53, -186.64) * mm, "end": v(-57.94, -190.18) * mm});
            skLineSegment(sketch, "E1686", {"start": v(-57.94, -190.18) * mm, "end": v(-57.9, -190.54) * mm});
            skLineSegment(sketch, "E1687", {"start": v(-57.9, -190.54) * mm, "end": v(-57.87, -190.77) * mm});
            skLineSegment(sketch, "E1688", {"start": v(-57.87, -190.77) * mm, "end": v(-57.72, -191.44) * mm});
            skLineSegment(sketch, "E1689", {"start": v(-57.72, -191.44) * mm, "end": v(-57.36, -192.14) * mm});
            skLineSegment(sketch, "E1690", {"start": v(-57.36, -192.14) * mm, "end": v(-56.77, -192.64) * mm});
            skLineSegment(sketch, "E1691", {"start": v(-56.77, -192.64) * mm, "end": v(-56.1, -192.88) * mm});
            skLineSegment(sketch, "E1692", {"start": v(-56.1, -192.88) * mm, "end": v(-55.86, -192.91) * mm});
            skLineSegment(sketch, "E1693", {"start": v(-55.86, -192.91) * mm, "end": v(-55.64, -192.94) * mm});
            skLineSegment(sketch, "E1694", {"start": v(-55.64, -192.94) * mm, "end": v(-54.57, -193.24) * mm});
            skLineSegment(sketch, "E1695", {"start": v(-54.57, -193.24) * mm, "end": v(-53.51, -193.61) * mm});
            skLineSegment(sketch, "E1696", {"start": v(-53.51, -193.61) * mm, "end": v(-53.3, -193.68) * mm});
            skLineSegment(sketch, "E1697", {"start": v(-53.3, -193.68) * mm, "end": v(-53.22, -193.7) * mm});
            skLineSegment(sketch, "E1698", {"start": v(-53.22, -193.7) * mm, "end": v(-52.44, -194.06) * mm});
            skLineSegment(sketch, "E1699", {"start": v(-52.44, -194.06) * mm, "end": v(-52.38, -194.11) * mm});
            skLineSegment(sketch, "E1700", {"start": v(-52.38, -194.11) * mm, "end": v(-52.28, -194.2) * mm});
            skLineSegment(sketch, "E1701", {"start": v(-52.28, -194.2) * mm, "end": v(-51.95, -194.68) * mm});
            skLineSegment(sketch, "E1702", {"start": v(-51.95, -194.68) * mm, "end": v(-51.92, -195.27) * mm});
            skLineSegment(sketch, "E1703", {"start": v(-51.92, -195.27) * mm, "end": v(-51.97, -195.39) * mm});
            skLineSegment(sketch, "E1704", {"start": v(-51.97, -195.39) * mm, "end": v(-52, -195.48) * mm});
            skLineSegment(sketch, "E1705", {"start": v(-52, -195.48) * mm, "end": v(-52.34, -195.68) * mm});
            skLineSegment(sketch, "E1706", {"start": v(-52.34, -195.68) * mm, "end": v(-52.78, -195.7) * mm});
            skLineSegment(sketch, "E1707", {"start": v(-52.78, -195.7) * mm, "end": v(-52.86, -195.7) * mm});
            skLineSegment(sketch, "E1708", {"start": v(-52.86, -195.7) * mm, "end": v(-53.2, -195.73) * mm});
            skLineSegment(sketch, "E1709", {"start": v(-53.2, -195.73) * mm, "end": v(-54.91, -195.58) * mm});
            skLineSegment(sketch, "E1710", {"start": v(-54.91, -195.58) * mm, "end": v(-56.6, -195.3) * mm});
            skLineSegment(sketch, "E1711", {"start": v(-56.6, -195.3) * mm, "end": v(-56.94, -195.25) * mm});
            skLineSegment(sketch, "E1712", {"start": v(-56.94, -195.25) * mm, "end": v(-57.7, -195.14) * mm});
            skLineSegment(sketch, "E1713", {"start": v(-57.7, -195.14) * mm, "end": v(-65.4, -194.82) * mm});
            skLineSegment(sketch, "E1714", {"start": v(-65.4, -194.82) * mm, "end": v(-66.17, -194.85) * mm});
            skLineSegment(sketch, "E1715", {"start": v(-66.17, -194.85) * mm, "end": v(-66.34, -194.85) * mm});
            skLineSegment(sketch, "E1716", {"start": v(-66.34, -194.85) * mm, "end": v(-68.05, -194.77) * mm});
            skLineSegment(sketch, "E1717", {"start": v(-68.05, -194.77) * mm, "end": v(-68.22, -194.75) * mm});
            skLineSegment(sketch, "E1718", {"start": v(-68.22, -194.75) * mm, "end": v(-68.34, -194.74) * mm});
            skLineSegment(sketch, "E1719", {"start": v(-68.34, -194.74) * mm, "end": v(-68.72, -194.43) * mm});
            skLineSegment(sketch, "E1720", {"start": v(-68.72, -194.43) * mm, "end": v(-68.88, -193.94) * mm});
            skLineSegment(sketch, "E1721", {"start": v(-68.88, -193.94) * mm, "end": v(-68.88, -193.83) * mm});
            skLineSegment(sketch, "E1722", {"start": v(-68.88, -193.83) * mm, "end": v(-68.89, -193.74) * mm});
            skLineSegment(sketch, "E1723", {"start": v(-68.89, -193.74) * mm, "end": v(-68.7, -193.37) * mm});
            skLineSegment(sketch, "E1724", {"start": v(-68.7, -193.37) * mm, "end": v(-68.34, -193.16) * mm});
            skLineSegment(sketch, "E1725", {"start": v(-68.34, -193.16) * mm, "end": v(-68.25, -193.14) * mm});
            skLineSegment(sketch, "E1726", {"start": v(-68.25, -193.14) * mm, "end": v(-68.1, -193.11) * mm});
            skLineSegment(sketch, "E1727", {"start": v(-68.1, -193.11) * mm, "end": v(-66.59, -192.84) * mm});
            skLineSegment(sketch, "E1728", {"start": v(-66.59, -192.84) * mm, "end": v(-66.43, -192.83) * mm});
            skLineSegment(sketch, "E1729", {"start": v(-66.43, -192.83) * mm, "end": v(-66.18, -192.8) * mm});
            skLineSegment(sketch, "E1730", {"start": v(-66.18, -192.8) * mm, "end": v(-65.42, -192.68) * mm});
            skLineSegment(sketch, "E1731", {"start": v(-65.42, -192.68) * mm, "end": v(-64.9, -192.41) * mm});
            skLineSegment(sketch, "E1732", {"start": v(-64.9, -192.41) * mm, "end": v(-64.75, -191.84) * mm});
            skLineSegment(sketch, "E1733", {"start": v(-64.75, -191.84) * mm, "end": v(-64.81, -191.05) * mm});
            skLineSegment(sketch, "E1734", {"start": v(-64.81, -191.05) * mm, "end": v(-64.85, -190.79) * mm});
            skLineSegment(sketch, "E1735", {"start": v(-64.85, -190.79) * mm, "end": v(-64.9, -190.31) * mm});
            skLineSegment(sketch, "E1736", {"start": v(-64.9, -190.31) * mm, "end": v(-65.64, -185.58) * mm});
            skLineSegment(sketch, "E1737", {"start": v(-65.64, -185.58) * mm, "end": v(-65.7, -185.1) * mm});
            skLineSegment(sketch, "E1738", {"start": v(-65.7, -185.1) * mm, "end": v(-65.9, -183.87) * mm});
            skLineSegment(sketch, "E1739", {"start": v(-65.9, -183.87) * mm, "end": v(-67.84, -171.52) * mm});
            skLineSegment(sketch, "E1740", {"start": v(-67.84, -171.52) * mm, "end": v(-68.05, -170.29) * mm});
            skLineSegment(sketch, "E1741", {"start": v(-68.05, -170.29) * mm, "end": v(-68.08, -170.09) * mm});
            skLineSegment(sketch, "E1742", {"start": v(-68.08, -170.09) * mm, "end": v(-68.2, -169.5) * mm});
            skLineSegment(sketch, "E1743", {"start": v(-68.2, -169.5) * mm, "end": v(-68.33, -168.9) * mm});
            skLineSegment(sketch, "E1744", {"start": v(-68.33, -168.9) * mm, "end": v(-68.5, -168.46) * mm});
            skLineSegment(sketch, "E1745", {"start": v(-68.5, -168.46) * mm, "end": v(-68.74, -168.15) * mm});
            skLineSegment(sketch, "E1746", {"start": v(-68.74, -168.15) * mm, "end": v(-69.07, -167.95) * mm});
            skLineSegment(sketch, "E1747", {"start": v(-69.07, -167.95) * mm, "end": v(-69.52, -167.8) * mm});
            skLineSegment(sketch, "E1748", {"start": v(-69.52, -167.8) * mm, "end": v(-70.12, -167.7) * mm});
            skLineSegment(sketch, "E1749", {"start": v(-70.12, -167.7) * mm, "end": v(-70.7, -167.63) * mm});
            skLineSegment(sketch, "E1750", {"start": v(-70.7, -167.63) * mm, "end": v(-70.9, -167.6) * mm});
            skLineSegment(sketch, "E1751", {"start": v(-70.9, -167.6) * mm, "end": v(-71.03, -167.58) * mm});
            skLineSegment(sketch, "E1752", {"start": v(-71.03, -167.58) * mm, "end": v(-72.37, -167.3) * mm});
            skLineSegment(sketch, "E1753", {"start": v(-72.37, -167.3) * mm, "end": v(-72.5, -167.25) * mm});
            skLineSegment(sketch, "E1754", {"start": v(-72.5, -167.25) * mm, "end": v(-72.6, -167.21) * mm});
            skLineSegment(sketch, "E1755", {"start": v(-72.6, -167.21) * mm, "end": v(-72.93, -166.85) * mm});
            skLineSegment(sketch, "E1756", {"start": v(-72.93, -166.85) * mm, "end": v(-73.03, -166.34) * mm});
            skLineSegment(sketch, "E1757", {"start": v(-73.03, -166.34) * mm, "end": v(-73.03, -166.24) * mm});
            skLineSegment(sketch, "E1758", {"start": v(-73.03, -166.24) * mm, "end": v(-73.03, -166.15) * mm});
            skLineSegment(sketch, "E1759", {"start": v(-73.03, -166.15) * mm, "end": v(-72.95, -165.9) * mm});
            skLineSegment(sketch, "E1760", {"start": v(-72.95, -165.9) * mm, "end": v(-72.75, -165.7) * mm});
            skLineSegment(sketch, "E1761", {"start": v(-72.75, -165.7) * mm, "end": v(-72.48, -165.62) * mm});
            skLineSegment(sketch, "E1762", {"start": v(-72.48, -165.62) * mm, "end": v(-72.25, -165.6) * mm});
            skLineSegment(sketch, "E1763", {"start": v(-72.25, -165.6) * mm, "end": v(-72.17, -165.6) * mm});
            skLineSegment(sketch, "E1764", {"start": v(-72.17, -165.6) * mm, "end": v(-71.86, -165.6) * mm});
            skLineSegment(sketch, "E1765", {"start": v(-71.86, -165.6) * mm, "end": v(-70.3, -165.54) * mm});
            skLineSegment(sketch, "E1766", {"start": v(-70.3, -165.54) * mm, "end": v(-68.77, -165.6) * mm});
            skLineSegment(sketch, "E1767", {"start": v(-68.77, -165.6) * mm, "end": v(-68.47, -165.65) * mm});
            skLineSegment(sketch, "E1768", {"start": v(-68.47, -165.65) * mm, "end": v(-67.74, -165.8) * mm});
            skLineSegment(sketch, "E1769", {"start": v(-67.74, -165.8) * mm, "end": v(-64.06, -166) * mm});
            skLineSegment(sketch, "E1770", {"start": v(-64.06, -166) * mm, "end": v(-60.39, -165.97) * mm});
            skLineSegment(sketch, "E1771", {"start": v(-60.39, -165.97) * mm, "end": v(-59.65, -166) * mm});
            skLineSegment(sketch, "E1772", {"start": v(-59.65, -166) * mm, "end": v(-58.95, -166.01) * mm});
            skLineSegment(sketch, "E1773", {"start": v(-58.95, -166.01) * mm, "end": v(-55.45, -166.2) * mm});
            skLineSegment(sketch, "E1774", {"start": v(-55.45, -166.2) * mm, "end": v(-51.97, -166.67) * mm});
            skLineSegment(sketch, "E1775", {"start": v(-51.97, -166.67) * mm, "end": v(-51.28, -166.85) * mm});
            skLineSegment(sketch, "E1776", {"start": v(-51.28, -166.85) * mm, "end": v(-50.62, -167.01) * mm});
            skLineSegment(sketch, "E1777", {"start": v(-50.62, -167.01) * mm, "end": v(-47.6, -168.39) * mm});
            skLineSegment(sketch, "E1778", {"start": v(-47.6, -168.39) * mm, "end": v(-45, -170.46) * mm});
            skLineSegment(sketch, "E1779", {"start": v(-45, -170.46) * mm, "end": v(-44.56, -170.98) * mm});
            skLineSegment(sketch, "E1780", {"start": v(-44.56, -170.98) * mm, "end": v(-44.43, -171.14) * mm});
            skLineSegment(sketch, "E1781", {"start": v(-44.43, -171.14) * mm, "end": v(-43.27, -172.84) * mm});
            skLineSegment(sketch, "E1782", {"start": v(-43.27, -172.84) * mm, "end": v(-43.19, -173.02) * mm});
            skLineSegment(sketch, "E1783", {"start": v(-43.19, -173.02) * mm, "end": v(-42.95, -173.51) * mm});
            skLineSegment(sketch, "E1784", {"start": v(-42.95, -173.51) * mm, "end": v(-42.62, -175.17) * mm});
            skLineSegment(sketch, "E1785", {"start": v(-42.62, -175.17) * mm, "end": v(-42.9, -177.2) * mm});
            skLineSegment(sketch, "E1786", {"start": v(-42.9, -177.2) * mm, "end": v(-43.96, -178.99) * mm});
            skLineSegment(sketch, "E1787", {"start": v(-43.96, -178.99) * mm, "end": v(-45.25, -180.1) * mm});
            skLineSegment(sketch, "E1788", {"start": v(-45.25, -180.1) * mm, "end": v(-45.74, -180.35) * mm});
            skLineSegment(sketch, "E1789", {"start": v(-45.74, -180.35) * mm, "end": v(-45.92, -180.44) * mm});
            skLineSegment(sketch, "E1790", {"start": v(-45.92, -180.44) * mm, "end": v(-46.9, -180.78) * mm});
            skLineSegment(sketch, "E1791", {"start": v(-46.9, -180.78) * mm, "end": v(-47.93, -181.32) * mm});
            skLineSegment(sketch, "E1792", {"start": v(-47.93, -181.32) * mm, "end": v(-48.13, -181.51) * mm});
            skLineSegment(sketch, "E1793", {"start": v(-26.56, -169.23) * mm, "end": v(-26.36, -170.05) * mm});
            skLineSegment(sketch, "E1794", {"start": v(-26.36, -170.05) * mm, "end": v(-24.36, -178.3) * mm});
            skLineSegment(sketch, "E1795", {"start": v(-24.36, -178.3) * mm, "end": v(-24.16, -179.14) * mm});
            skLineSegment(sketch, "E1796", {"start": v(-24.16, -179.14) * mm, "end": v(-24.12, -179.3) * mm});
            skLineSegment(sketch, "E1797", {"start": v(-24.12, -179.3) * mm, "end": v(-23.76, -179.83) * mm});
            skLineSegment(sketch, "E1798", {"start": v(-23.76, -179.83) * mm, "end": v(-23.16, -180) * mm});
            skLineSegment(sketch, "E1799", {"start": v(-23.16, -180) * mm, "end": v(-23, -180) * mm});
            skLineSegment(sketch, "E1800", {"start": v(-23, -180) * mm, "end": v(-22.4, -180) * mm});
            skLineSegment(sketch, "E1801", {"start": v(-22.4, -180) * mm, "end": v(-16.44, -179.48) * mm});
            skLineSegment(sketch, "E1802", {"start": v(-16.44, -179.48) * mm, "end": v(-15.84, -179.38) * mm});
            skLineSegment(sketch, "E1803", {"start": v(-15.84, -179.38) * mm, "end": v(-15.59, -179.34) * mm});
            skLineSegment(sketch, "E1804", {"start": v(-15.59, -179.34) * mm, "end": v(-14.82, -179.1) * mm});
            skLineSegment(sketch, "E1805", {"start": v(-14.82, -179.1) * mm, "end": v(-14.2, -178.65) * mm});
            skLineSegment(sketch, "E1806", {"start": v(-14.2, -178.65) * mm, "end": v(-13.88, -177.93) * mm});
            skLineSegment(sketch, "E1807", {"start": v(-13.88, -177.93) * mm, "end": v(-13.76, -177.12) * mm});
            skLineSegment(sketch, "E1808", {"start": v(-13.76, -177.12) * mm, "end": v(-13.75, -176.85) * mm});
            skLineSegment(sketch, "E1809", {"start": v(-13.75, -176.85) * mm, "end": v(-13.74, -176.73) * mm});
            skLineSegment(sketch, "E1810", {"start": v(-13.74, -176.73) * mm, "end": v(-13.7, -175.53) * mm});
            skLineSegment(sketch, "E1811", {"start": v(-13.7, -175.53) * mm, "end": v(-13.7, -175.41) * mm});
            skLineSegment(sketch, "E1812", {"start": v(-13.7, -175.41) * mm, "end": v(-13.71, -175.24) * mm});
            skLineSegment(sketch, "E1813", {"start": v(-13.71, -175.24) * mm, "end": v(-13.5, -174.65) * mm});
            skLineSegment(sketch, "E1814", {"start": v(-13.5, -174.65) * mm, "end": v(-12.93, -174.34) * mm});
            skLineSegment(sketch, "E1815", {"start": v(-12.93, -174.34) * mm, "end": v(-12.76, -174.32) * mm});
            skLineSegment(sketch, "E1816", {"start": v(-12.76, -174.32) * mm, "end": v(-12.65, -174.31) * mm});
            skLineSegment(sketch, "E1817", {"start": v(-12.65, -174.31) * mm, "end": v(-12.3, -174.35) * mm});
            skLineSegment(sketch, "E1818", {"start": v(-12.3, -174.35) * mm, "end": v(-12, -174.53) * mm});
            skLineSegment(sketch, "E1819", {"start": v(-12, -174.53) * mm, "end": v(-11.8, -174.84) * mm});
            skLineSegment(sketch, "E1820", {"start": v(-11.8, -174.84) * mm, "end": v(-11.69, -175.15) * mm});
            skLineSegment(sketch, "E1821", {"start": v(-11.69, -175.15) * mm, "end": v(-11.66, -175.25) * mm});
            skLineSegment(sketch, "E1822", {"start": v(-11.66, -175.25) * mm, "end": v(-11.54, -175.71) * mm});
            skLineSegment(sketch, "E1823", {"start": v(-11.54, -175.71) * mm, "end": v(-10.34, -180.35) * mm});
            skLineSegment(sketch, "E1824", {"start": v(-10.34, -180.35) * mm, "end": v(-10.22, -180.82) * mm});
            skLineSegment(sketch, "E1825", {"start": v(-10.22, -180.82) * mm, "end": v(-10.14, -181.17) * mm});
            skLineSegment(sketch, "E1826", {"start": v(-10.14, -181.17) * mm, "end": v(-9.3, -184.67) * mm});
            skLineSegment(sketch, "E1827", {"start": v(-9.3, -184.67) * mm, "end": v(-9.22, -185.02) * mm});
            skLineSegment(sketch, "E1828", {"start": v(-9.22, -185.02) * mm, "end": v(-9.2, -185.1) * mm});
            skLineSegment(sketch, "E1829", {"start": v(-9.2, -185.1) * mm, "end": v(-9.13, -185.3) * mm});
            skLineSegment(sketch, "E1830", {"start": v(-9.13, -185.3) * mm, "end": v(-9.05, -185.6) * mm});
            skLineSegment(sketch, "E1831", {"start": v(-9.05, -185.6) * mm, "end": v(-9.08, -185.88) * mm});
            skLineSegment(sketch, "E1832", {"start": v(-9.08, -185.88) * mm, "end": v(-9.27, -186.06) * mm});
            skLineSegment(sketch, "E1833", {"start": v(-9.27, -186.06) * mm, "end": v(-9.34, -186.09) * mm});
            skLineSegment(sketch, "E1834", {"start": v(-9.34, -186.09) * mm, "end": v(-9.46, -186.14) * mm});
            skLineSegment(sketch, "E1835", {"start": v(-9.46, -186.14) * mm, "end": v(-10.14, -186.25) * mm});
            skLineSegment(sketch, "E1836", {"start": v(-10.14, -186.25) * mm, "end": v(-10.77, -186.02) * mm});
            skLineSegment(sketch, "E1837", {"start": v(-10.77, -186.02) * mm, "end": v(-10.87, -185.9) * mm});
            skLineSegment(sketch, "E1838", {"start": v(-10.87, -185.9) * mm, "end": v(-10.97, -185.78) * mm});
            skLineSegment(sketch, "E1839", {"start": v(-10.97, -185.78) * mm, "end": v(-11.74, -184.45) * mm});
            skLineSegment(sketch, "E1840", {"start": v(-11.74, -184.45) * mm, "end": v(-11.79, -184.3) * mm});
            skLineSegment(sketch, "E1841", {"start": v(-11.79, -184.3) * mm, "end": v(-11.91, -183.94) * mm});
            skLineSegment(sketch, "E1842", {"start": v(-11.91, -183.94) * mm, "end": v(-12.48, -182.93) * mm});
            skLineSegment(sketch, "E1843", {"start": v(-12.48, -182.93) * mm, "end": v(-13.45, -182.04) * mm});
            skLineSegment(sketch, "E1844", {"start": v(-13.45, -182.04) * mm, "end": v(-14.7, -181.6) * mm});
            skLineSegment(sketch, "E1845", {"start": v(-14.7, -181.6) * mm, "end": v(-15.86, -181.55) * mm});
            skLineSegment(sketch, "E1846", {"start": v(-15.86, -181.55) * mm, "end": v(-16.24, -181.6) * mm});
            skLineSegment(sketch, "E1847", {"start": v(-16.24, -181.6) * mm, "end": v(-16.73, -181.65) * mm});
            skLineSegment(sketch, "E1848", {"start": v(-16.73, -181.65) * mm, "end": v(-21.7, -181.98) * mm});
            skLineSegment(sketch, "E1849", {"start": v(-21.7, -181.98) * mm, "end": v(-22.19, -182) * mm});
            skLineSegment(sketch, "E1850", {"start": v(-22.19, -182) * mm, "end": v(-22.33, -182.01) * mm});
            skLineSegment(sketch, "E1851", {"start": v(-22.33, -182.01) * mm, "end": v(-22.76, -182.1) * mm});
            skLineSegment(sketch, "E1852", {"start": v(-22.76, -182.1) * mm, "end": v(-23.13, -182.32) * mm});
            skLineSegment(sketch, "E1853", {"start": v(-23.13, -182.32) * mm, "end": v(-23.3, -182.7) * mm});
            skLineSegment(sketch, "E1854", {"start": v(-23.3, -182.7) * mm, "end": v(-23.27, -183.14) * mm});
            skLineSegment(sketch, "E1855", {"start": v(-23.27, -183.14) * mm, "end": v(-23.24, -183.28) * mm});
            skLineSegment(sketch, "E1856", {"start": v(-23.24, -183.28) * mm, "end": v(-23.05, -184.03) * mm});
            skLineSegment(sketch, "E1857", {"start": v(-23.05, -184.03) * mm, "end": v(-21.15, -191.5) * mm});
            skLineSegment(sketch, "E1858", {"start": v(-21.15, -191.5) * mm, "end": v(-20.97, -192.24) * mm});
            skLineSegment(sketch, "E1859", {"start": v(-20.97, -192.24) * mm, "end": v(-20.93, -192.4) * mm});
            skLineSegment(sketch, "E1860", {"start": v(-20.93, -192.4) * mm, "end": v(-20.7, -192.85) * mm});
            skLineSegment(sketch, "E1861", {"start": v(-20.7, -192.85) * mm, "end": v(-20.3, -193.27) * mm});
            skLineSegment(sketch, "E1862", {"start": v(-20.3, -193.27) * mm, "end": v(-19.78, -193.51) * mm});
            skLineSegment(sketch, "E1863", {"start": v(-19.78, -193.51) * mm, "end": v(-19.31, -193.6) * mm});
            skLineSegment(sketch, "E1864", {"start": v(-19.31, -193.6) * mm, "end": v(-19.15, -193.6) * mm});
            skLineSegment(sketch, "E1865", {"start": v(-19.15, -193.6) * mm, "end": v(-18.31, -193.6) * mm});
            skLineSegment(sketch, "E1866", {"start": v(-18.31, -193.6) * mm, "end": v(-14.12, -193.55) * mm});
            skLineSegment(sketch, "E1867", {"start": v(-14.12, -193.55) * mm, "end": v(-9.95, -193.15) * mm});
            skLineSegment(sketch, "E1868", {"start": v(-9.95, -193.15) * mm, "end": v(-9.12, -193) * mm});
            skLineSegment(sketch, "E1869", {"start": v(-9.12, -193) * mm, "end": v(-8.63, -192.9) * mm});
            skLineSegment(sketch, "E1870", {"start": v(-8.63, -192.9) * mm, "end": v(-7.22, -192.37) * mm});
            skLineSegment(sketch, "E1871", {"start": v(-7.22, -192.37) * mm, "end": v(-5.74, -191.33) * mm});
            skLineSegment(sketch, "E1872", {"start": v(-5.74, -191.33) * mm, "end": v(-4.66, -189.9) * mm});
            skLineSegment(sketch, "E1873", {"start": v(-4.66, -189.9) * mm, "end": v(-4.07, -188.54) * mm});
            skLineSegment(sketch, "E1874", {"start": v(-4.07, -188.54) * mm, "end": v(-3.94, -188.07) * mm});
            skLineSegment(sketch, "E1875", {"start": v(-3.94, -188.07) * mm, "end": v(-3.91, -187.98) * mm});
            skLineSegment(sketch, "E1876", {"start": v(-3.91, -187.98) * mm, "end": v(-3.7, -187.16) * mm});
            skLineSegment(sketch, "E1877", {"start": v(-3.7, -187.16) * mm, "end": v(-3.65, -187.08) * mm});
            skLineSegment(sketch, "E1878", {"start": v(-3.65, -187.08) * mm, "end": v(-3.6, -186.98) * mm});
            skLineSegment(sketch, "E1879", {"start": v(-3.6, -186.98) * mm, "end": v(-3.33, -186.7) * mm});
            skLineSegment(sketch, "E1880", {"start": v(-3.33, -186.7) * mm, "end": v(-2.93, -186.55) * mm});
            skLineSegment(sketch, "E1881", {"start": v(-2.93, -186.55) * mm, "end": v(-2.47, -186.53) * mm});
            skLineSegment(sketch, "E1882", {"start": v(-2.47, -186.53) * mm, "end": v(-2.13, -186.56) * mm});
            skLineSegment(sketch, "E1883", {"start": v(-2.13, -186.56) * mm, "end": v(-2.02, -186.57) * mm});
            skLineSegment(sketch, "E1884", {"start": v(-2.02, -186.57) * mm, "end": v(-1.94, -186.57) * mm});
            skLineSegment(sketch, "E1885", {"start": v(-1.94, -186.57) * mm, "end": v(-1.7, -186.67) * mm});
            skLineSegment(sketch, "E1886", {"start": v(-1.7, -186.67) * mm, "end": v(-1.53, -186.89) * mm});
            skLineSegment(sketch, "E1887", {"start": v(-1.53, -186.89) * mm, "end": v(-1.46, -187.18) * mm});
            skLineSegment(sketch, "E1888", {"start": v(-1.46, -187.18) * mm, "end": v(-1.44, -187.41) * mm});
            skLineSegment(sketch, "E1889", {"start": v(-1.44, -187.41) * mm, "end": v(-1.44, -187.5) * mm});
            skLineSegment(sketch, "E1890", {"start": v(-1.44, -187.5) * mm, "end": v(-1.4, -188.02) * mm});
            skLineSegment(sketch, "E1891", {"start": v(-1.4, -188.02) * mm, "end": v(-1.09, -193.32) * mm});
            skLineSegment(sketch, "E1892", {"start": v(-1.09, -193.32) * mm, "end": v(-1.05, -193.85) * mm});
            skLineSegment(sketch, "E1893", {"start": v(-1.05, -193.85) * mm, "end": v(-1.04, -194) * mm});
            skLineSegment(sketch, "E1894", {"start": v(-1.04, -194) * mm, "end": v(-1.07, -194.46) * mm});
            skLineSegment(sketch, "E1895", {"start": v(-1.07, -194.46) * mm, "end": v(-1.28, -194.88) * mm});
            skLineSegment(sketch, "E1896", {"start": v(-1.28, -194.88) * mm, "end": v(-1.68, -195.13) * mm});
            skLineSegment(sketch, "E1897", {"start": v(-1.68, -195.13) * mm, "end": v(-2.15, -195.22) * mm});
            skLineSegment(sketch, "E1898", {"start": v(-2.15, -195.22) * mm, "end": v(-2.3, -195.22) * mm});
            skLineSegment(sketch, "E1899", {"start": v(-2.3, -195.22) * mm, "end": v(-3.06, -195.24) * mm});
            skLineSegment(sketch, "E1900", {"start": v(-3.06, -195.24) * mm, "end": v(-10.6, -195.6) * mm});
            skLineSegment(sketch, "E1901", {"start": v(-10.6, -195.6) * mm, "end": v(-11.35, -195.6) * mm});
            skLineSegment(sketch, "E1902", {"start": v(-11.35, -195.6) * mm, "end": v(-12.9, -195.62) * mm});
            skLineSegment(sketch, "E1903", {"start": v(-12.9, -195.62) * mm, "end": v(-20.7, -195.91) * mm});
            skLineSegment(sketch, "E1904", {"start": v(-20.7, -195.91) * mm, "end": v(-28.46, -196.59) * mm});
            skLineSegment(sketch, "E1905", {"start": v(-28.46, -196.59) * mm, "end": v(-30, -196.8) * mm});
            skLineSegment(sketch, "E1906", {"start": v(-30, -196.8) * mm, "end": v(-30.18, -196.82) * mm});
            skLineSegment(sketch, "E1907", {"start": v(-30.18, -196.82) * mm, "end": v(-31.9, -196.91) * mm});
            skLineSegment(sketch, "E1908", {"start": v(-31.9, -196.91) * mm, "end": v(-32.06, -196.92) * mm});
            skLineSegment(sketch, "E1909", {"start": v(-32.06, -196.92) * mm, "end": v(-32.17, -196.93) * mm});
            skLineSegment(sketch, "E1910", {"start": v(-32.17, -196.93) * mm, "end": v(-32.49, -196.9) * mm});
            skLineSegment(sketch, "E1911", {"start": v(-32.49, -196.9) * mm, "end": v(-32.84, -196.78) * mm});
            skLineSegment(sketch, "E1912", {"start": v(-32.84, -196.78) * mm, "end": v(-33.08, -196.52) * mm});
            skLineSegment(sketch, "E1913", {"start": v(-33.08, -196.52) * mm, "end": v(-33.18, -196.18) * mm});
            skLineSegment(sketch, "E1914", {"start": v(-33.18, -196.18) * mm, "end": v(-33.19, -196.07) * mm});
            skLineSegment(sketch, "E1915", {"start": v(-33.19, -196.07) * mm, "end": v(-33.2, -195.9) * mm});
            skLineSegment(sketch, "E1916", {"start": v(-33.2, -195.9) * mm, "end": v(-32.98, -195.4) * mm});
            skLineSegment(sketch, "E1917", {"start": v(-32.98, -195.4) * mm, "end": v(-32.47, -195.17) * mm});
            skLineSegment(sketch, "E1918", {"start": v(-32.47, -195.17) * mm, "end": v(-32.34, -195.15) * mm});
            skLineSegment(sketch, "E1919", {"start": v(-32.34, -195.15) * mm, "end": v(-32.15, -195.12) * mm});
            skLineSegment(sketch, "E1920", {"start": v(-32.15, -195.12) * mm, "end": v(-30.3, -194.74) * mm});
            skLineSegment(sketch, "E1921", {"start": v(-30.3, -194.74) * mm, "end": v(-30.12, -194.7) * mm});
            skLineSegment(sketch, "E1922", {"start": v(-30.12, -194.7) * mm, "end": v(-29.95, -194.66) * mm});
            skLineSegment(sketch, "E1923", {"start": v(-29.95, -194.66) * mm, "end": v(-29.42, -194.51) * mm});
            skLineSegment(sketch, "E1924", {"start": v(-29.42, -194.51) * mm, "end": v(-28.89, -194.33) * mm});
            skLineSegment(sketch, "E1925", {"start": v(-28.89, -194.33) * mm, "end": v(-28.5, -194.13) * mm});
            skLineSegment(sketch, "E1926", {"start": v(-28.5, -194.13) * mm, "end": v(-28.26, -193.88) * mm});
            skLineSegment(sketch, "E1927", {"start": v(-28.26, -193.88) * mm, "end": v(-28.15, -193.55) * mm});
            skLineSegment(sketch, "E1928", {"start": v(-28.15, -193.55) * mm, "end": v(-28.14, -193.13) * mm});
            skLineSegment(sketch, "E1929", {"start": v(-28.14, -193.13) * mm, "end": v(-28.22, -192.59) * mm});
            skLineSegment(sketch, "E1930", {"start": v(-28.22, -192.59) * mm, "end": v(-28.33, -192.07) * mm});
            skLineSegment(sketch, "E1931", {"start": v(-28.33, -192.07) * mm, "end": v(-28.38, -191.9) * mm});
            skLineSegment(sketch, "E1932", {"start": v(-28.38, -191.9) * mm, "end": v(-28.72, -190.55) * mm});
            skLineSegment(sketch, "E1933", {"start": v(-28.72, -190.55) * mm, "end": v(-32.1, -177.1) * mm});
            skLineSegment(sketch, "E1934", {"start": v(-32.1, -177.1) * mm, "end": v(-32.43, -175.75) * mm});
            skLineSegment(sketch, "E1935", {"start": v(-32.43, -175.75) * mm, "end": v(-32.52, -175.39) * mm});
            skLineSegment(sketch, "E1936", {"start": v(-32.52, -175.39) * mm, "end": v(-33.47, -171.74) * mm});
            skLineSegment(sketch, "E1937", {"start": v(-33.47, -171.74) * mm, "end": v(-33.56, -171.38) * mm});
            skLineSegment(sketch, "E1938", {"start": v(-33.56, -171.38) * mm, "end": v(-33.63, -171.12) * mm});
            skLineSegment(sketch, "E1939", {"start": v(-33.63, -171.12) * mm, "end": v(-33.87, -170.37) * mm});
            skLineSegment(sketch, "E1940", {"start": v(-33.87, -170.37) * mm, "end": v(-34.24, -169.8) * mm});
            skLineSegment(sketch, "E1941", {"start": v(-34.24, -169.8) * mm, "end": v(-34.86, -169.52) * mm});
            skLineSegment(sketch, "E1942", {"start": v(-34.86, -169.52) * mm, "end": v(-35.65, -169.4) * mm});
            skLineSegment(sketch, "E1943", {"start": v(-35.65, -169.4) * mm, "end": v(-35.9, -169.37) * mm});
            skLineSegment(sketch, "E1944", {"start": v(-35.9, -169.37) * mm, "end": v(-36.13, -169.35) * mm});
            skLineSegment(sketch, "E1945", {"start": v(-36.13, -169.35) * mm, "end": v(-38.36, -169.26) * mm});
            skLineSegment(sketch, "E1946", {"start": v(-38.36, -169.26) * mm, "end": v(-38.58, -169.26) * mm});
            skLineSegment(sketch, "E1947", {"start": v(-38.58, -169.26) * mm, "end": v(-38.72, -169.25) * mm});
            skLineSegment(sketch, "E1948", {"start": v(-38.72, -169.25) * mm, "end": v(-39.25, -169.04) * mm});
            skLineSegment(sketch, "E1949", {"start": v(-39.25, -169.04) * mm, "end": v(-39.56, -168.57) * mm});
            skLineSegment(sketch, "E1950", {"start": v(-39.56, -168.57) * mm, "end": v(-39.6, -168.44) * mm});
            skLineSegment(sketch, "E1951", {"start": v(-39.6, -168.44) * mm, "end": v(-39.63, -168.33) * mm});
            skLineSegment(sketch, "E1952", {"start": v(-39.63, -168.33) * mm, "end": v(-39.67, -167.99) * mm});
            skLineSegment(sketch, "E1953", {"start": v(-39.67, -167.99) * mm, "end": v(-39.58, -167.65) * mm});
            skLineSegment(sketch, "E1954", {"start": v(-39.58, -167.65) * mm, "end": v(-39.32, -167.42) * mm});
            skLineSegment(sketch, "E1955", {"start": v(-39.32, -167.42) * mm, "end": v(-38.98, -167.34) * mm});
            skLineSegment(sketch, "E1956", {"start": v(-38.98, -167.34) * mm, "end": v(-38.86, -167.34) * mm});
            skLineSegment(sketch, "E1957", {"start": v(-38.86, -167.34) * mm, "end": v(-38.76, -167.34) * mm});
            skLineSegment(sketch, "E1958", {"start": v(-38.76, -167.34) * mm, "end": v(-37.73, -167.32) * mm});
            skLineSegment(sketch, "E1959", {"start": v(-37.73, -167.32) * mm, "end": v(-37.63, -167.34) * mm});
            skLineSegment(sketch, "E1960", {"start": v(-37.63, -167.34) * mm, "end": v(-36.54, -167.47) * mm});
            skLineSegment(sketch, "E1961", {"start": v(-36.54, -167.47) * mm, "end": v(-31.16, -167.31) * mm});
            skLineSegment(sketch, "E1962", {"start": v(-31.16, -167.31) * mm, "end": v(-25.8, -166.74) * mm});
            skLineSegment(sketch, "E1963", {"start": v(-25.8, -166.74) * mm, "end": v(-24.72, -166.67) * mm});
            skLineSegment(sketch, "E1964", {"start": v(-24.72, -166.67) * mm, "end": v(-23.53, -166.59) * mm});
            skLineSegment(sketch, "E1965", {"start": v(-23.53, -166.59) * mm, "end": v(-17.55, -166.15) * mm});
            skLineSegment(sketch, "E1966", {"start": v(-17.55, -166.15) * mm, "end": v(-11.55, -165.94) * mm});
            skLineSegment(sketch, "E1967", {"start": v(-11.55, -165.94) * mm, "end": v(-10.35, -165.98) * mm});
            skLineSegment(sketch, "E1968", {"start": v(-10.35, -165.98) * mm, "end": v(-10.2, -165.98) * mm});
            skLineSegment(sketch, "E1969", {"start": v(-10.2, -165.98) * mm, "end": v(-9.7, -166) * mm});
            skLineSegment(sketch, "E1970", {"start": v(-9.7, -166) * mm, "end": v(-9.21, -166.04) * mm});
            skLineSegment(sketch, "E1971", {"start": v(-9.21, -166.04) * mm, "end": v(-8.84, -166.13) * mm});
            skLineSegment(sketch, "E1972", {"start": v(-8.84, -166.13) * mm, "end": v(-8.57, -166.28) * mm});
            skLineSegment(sketch, "E1973", {"start": v(-8.57, -166.28) * mm, "end": v(-8.37, -166.52) * mm});
            skLineSegment(sketch, "E1974", {"start": v(-8.37, -166.52) * mm, "end": v(-8.2, -166.87) * mm});
            skLineSegment(sketch, "E1975", {"start": v(-8.2, -166.87) * mm, "end": v(-8.05, -167.35) * mm});
            skLineSegment(sketch, "E1976", {"start": v(-8.05, -167.35) * mm, "end": v(-7.92, -167.83) * mm});
            skLineSegment(sketch, "E1977", {"start": v(-7.92, -167.83) * mm, "end": v(-7.88, -167.99) * mm});
            skLineSegment(sketch, "E1978", {"start": v(-7.88, -167.99) * mm, "end": v(-7.8, -168.3) * mm});
            skLineSegment(sketch, "E1979", {"start": v(-7.8, -168.3) * mm, "end": v(-7.04, -171.47) * mm});
            skLineSegment(sketch, "E1980", {"start": v(-7.04, -171.47) * mm, "end": v(-6.97, -171.79) * mm});
            skLineSegment(sketch, "E1981", {"start": v(-6.97, -171.79) * mm, "end": v(-6.95, -171.89) * mm});
            skLineSegment(sketch, "E1982", {"start": v(-6.95, -171.89) * mm, "end": v(-6.87, -172.19) * mm});
            skLineSegment(sketch, "E1983", {"start": v(-6.87, -172.19) * mm, "end": v(-6.8, -172.6) * mm});
            skLineSegment(sketch, "E1984", {"start": v(-6.8, -172.6) * mm, "end": v(-6.86, -172.98) * mm});
            skLineSegment(sketch, "E1985", {"start": v(-6.86, -172.98) * mm, "end": v(-7.08, -173.22) * mm});
            skLineSegment(sketch, "E1986", {"start": v(-7.08, -173.22) * mm, "end": v(-7.18, -173.26) * mm});
            skLineSegment(sketch, "E1987", {"start": v(-7.18, -173.26) * mm, "end": v(-7.34, -173.34) * mm});
            skLineSegment(sketch, "E1988", {"start": v(-7.34, -173.34) * mm, "end": v(-8.14, -173.4) * mm});
            skLineSegment(sketch, "E1989", {"start": v(-8.14, -173.4) * mm, "end": v(-8.89, -172.97) * mm});
            skLineSegment(sketch, "E1990", {"start": v(-8.89, -172.97) * mm, "end": v(-9.01, -172.8) * mm});
            skLineSegment(sketch, "E1991", {"start": v(-9.01, -172.8) * mm, "end": v(-9.16, -172.62) * mm});
            skLineSegment(sketch, "E1992", {"start": v(-9.16, -172.62) * mm, "end": v(-10.72, -170.79) * mm});
            skLineSegment(sketch, "E1993", {"start": v(-10.72, -170.79) * mm, "end": v(-10.88, -170.6) * mm});
            skLineSegment(sketch, "E1994", {"start": v(-10.88, -170.6) * mm, "end": v(-10.98, -170.5) * mm});
            skLineSegment(sketch, "E1995", {"start": v(-10.98, -170.5) * mm, "end": v(-12.02, -169.35) * mm});
            skLineSegment(sketch, "E1996", {"start": v(-12.02, -169.35) * mm, "end": v(-12.12, -169.24) * mm});
            skLineSegment(sketch, "E1997", {"start": v(-12.12, -169.24) * mm, "end": v(-12.26, -169.1) * mm});
            skLineSegment(sketch, "E1998", {"start": v(-12.26, -169.1) * mm, "end": v(-13.05, -168.64) * mm});
            skLineSegment(sketch, "E1999", {"start": v(-13.05, -168.64) * mm, "end": v(-13.96, -168.44) * mm});
            skLineSegment(sketch, "E2000", {"start": v(-13.96, -168.44) * mm, "end": v(-14.16, -168.44) * mm});
            skLineSegment(sketch, "E2001", {"start": v(-14.16, -168.44) * mm, "end": v(-15.16, -168.42) * mm});
            skLineSegment(sketch, "E2002", {"start": v(-15.16, -168.42) * mm, "end": v(-25.09, -168.84) * mm});
            skLineSegment(sketch, "E2003", {"start": v(-25.09, -168.84) * mm, "end": v(-26.08, -168.94) * mm});
            skLineSegment(sketch, "E2004", {"start": v(-26.08, -168.94) * mm, "end": v(-26.1, -168.94) * mm});
            skLineSegment(sketch, "E2005", {"start": v(-26.1, -168.94) * mm, "end": v(-26.26, -169.03) * mm});
            skLineSegment(sketch, "E2006", {"start": v(-26.26, -169.03) * mm, "end": v(-26.5, -169.2) * mm});
            skLineSegment(sketch, "E2007", {"start": v(-26.5, -169.2) * mm, "end": v(-26.56, -169.23) * mm});
            skLineSegment(sketch, "E2008", {"start": v(178.98, 73.13) * mm, "end": v(178.97, 73.51) * mm});
            skLineSegment(sketch, "E2009", {"start": v(178.97, 73.51) * mm, "end": v(178.83, 74.66) * mm});
            skLineSegment(sketch, "E2010", {"start": v(178.83, 74.66) * mm, "end": v(178.44, 76.1) * mm});
            skLineSegment(sketch, "E2011", {"start": v(178.44, 76.1) * mm, "end": v(177.83, 77.41) * mm});
            skLineSegment(sketch, "E2012", {"start": v(177.83, 77.41) * mm, "end": v(177.26, 78.31) * mm});
            skLineSegment(sketch, "E2013", {"start": v(177.26, 78.31) * mm, "end": v(177.04, 78.59) * mm});
            skLineSegment(sketch, "E2014", {"start": v(177.04, 78.59) * mm, "end": v(176.93, 78.74) * mm});
            skLineSegment(sketch, "E2015", {"start": v(176.93, 78.74) * mm, "end": v(176.54, 79.15) * mm});
            skLineSegment(sketch, "E2016", {"start": v(176.54, 79.15) * mm, "end": v(176.12, 79.36) * mm});
            skLineSegment(sketch, "E2017", {"start": v(176.12, 79.36) * mm, "end": v(175.7, 79.22) * mm});
            skLineSegment(sketch, "E2018", {"start": v(175.7, 79.22) * mm, "end": v(175.27, 78.85) * mm});
            skLineSegment(sketch, "E2019", {"start": v(175.27, 78.85) * mm, "end": v(175.14, 78.72) * mm});
            skLineSegment(sketch, "E2020", {"start": v(175.14, 78.72) * mm, "end": v(174.65, 78.2) * mm});
            skLineSegment(sketch, "E2021", {"start": v(174.65, 78.2) * mm, "end": v(169.74, 72.94) * mm});
            skLineSegment(sketch, "E2022", {"start": v(169.74, 72.94) * mm, "end": v(169.25, 72.42) * mm});
            skLineSegment(sketch, "E2023", {"start": v(169.25, 72.42) * mm, "end": v(169.05, 72.21) * mm});
            skLineSegment(sketch, "E2024", {"start": v(169.05, 72.21) * mm, "end": v(168.47, 71.57) * mm});
            skLineSegment(sketch, "E2025", {"start": v(168.47, 71.57) * mm, "end": v(167.92, 70.89) * mm});
            skLineSegment(sketch, "E2026", {"start": v(167.92, 70.89) * mm, "end": v(167.6, 70.32) * mm});
            skLineSegment(sketch, "E2027", {"start": v(167.6, 70.32) * mm, "end": v(167.5, 69.8) * mm});
            skLineSegment(sketch, "E2028", {"start": v(167.5, 69.8) * mm, "end": v(167.63, 69.3) * mm});
            skLineSegment(sketch, "E2029", {"start": v(167.63, 69.3) * mm, "end": v(168, 68.75) * mm});
            skLineSegment(sketch, "E2030", {"start": v(168, 68.75) * mm, "end": v(168.6, 68.1) * mm});
            skLineSegment(sketch, "E2031", {"start": v(168.6, 68.1) * mm, "end": v(169.24, 67.5) * mm});
            skLineSegment(sketch, "E2032", {"start": v(169.24, 67.5) * mm, "end": v(169.45, 67.3) * mm});
            skLineSegment(sketch, "E2033", {"start": v(169.45, 67.3) * mm, "end": v(169.54, 67.23) * mm});
            skLineSegment(sketch, "E2034", {"start": v(169.54, 67.23) * mm, "end": v(170.5, 66.5) * mm});
            skLineSegment(sketch, "E2035", {"start": v(170.5, 66.5) * mm, "end": v(170.6, 66.44) * mm});
            skLineSegment(sketch, "E2036", {"start": v(170.6, 66.44) * mm, "end": v(170.82, 66.29) * mm});
            skLineSegment(sketch, "E2037", {"start": v(170.82, 66.29) * mm, "end": v(171.56, 65.94) * mm});
            skLineSegment(sketch, "E2038", {"start": v(171.56, 65.94) * mm, "end": v(172.55, 65.74) * mm});
            skLineSegment(sketch, "E2039", {"start": v(172.55, 65.74) * mm, "end": v(173.52, 65.84) * mm});
            skLineSegment(sketch, "E2040", {"start": v(173.52, 65.84) * mm, "end": v(174.25, 66.14) * mm});
            skLineSegment(sketch, "E2041", {"start": v(174.25, 66.14) * mm, "end": v(174.46, 66.29) * mm});
            skLineSegment(sketch, "E2042", {"start": v(174.46, 66.29) * mm, "end": v(174.93, 66.6) * mm});
            skLineSegment(sketch, "E2043", {"start": v(174.93, 66.6) * mm, "end": v(176.23, 67.73) * mm});
            skLineSegment(sketch, "E2044", {"start": v(176.23, 67.73) * mm, "end": v(177.6, 69.38) * mm});
            skLineSegment(sketch, "E2045", {"start": v(177.6, 69.38) * mm, "end": v(178.52, 71.2) * mm});
            skLineSegment(sketch, "E2046", {"start": v(178.52, 71.2) * mm, "end": v(178.93, 72.64) * mm});
            skLineSegment(sketch, "E2047", {"start": v(178.93, 72.64) * mm, "end": v(178.98, 73.13) * mm});
            skLineSegment(sketch, "E2048", {"start": v(171.73, 60.86) * mm, "end": v(171.36, 59.6) * mm});
            skLineSegment(sketch, "E2049", {"start": v(171.36, 59.6) * mm, "end": v(167.5, 47.12) * mm});
            skLineSegment(sketch, "E2050", {"start": v(167.5, 47.12) * mm, "end": v(167.14, 45.87) * mm});
            skLineSegment(sketch, "E2051", {"start": v(167.14, 45.87) * mm, "end": v(166.99, 45.33) * mm});
            skLineSegment(sketch, "E2052", {"start": v(166.99, 45.33) * mm, "end": v(166.9, 43.6) * mm});
            skLineSegment(sketch, "E2053", {"start": v(166.9, 43.6) * mm, "end": v(167.44, 41.6) * mm});
            skLineSegment(sketch, "E2054", {"start": v(167.44, 41.6) * mm, "end": v(168.6, 39.88) * mm});
            skLineSegment(sketch, "E2055", {"start": v(168.6, 39.88) * mm, "end": v(169.76, 38.72) * mm});
            skLineSegment(sketch, "E2056", {"start": v(169.76, 38.72) * mm, "end": v(170.19, 38.37) * mm});
            skLineSegment(sketch, "E2057", {"start": v(170.19, 38.37) * mm, "end": v(170.3, 38.3) * mm});
            skLineSegment(sketch, "E2058", {"start": v(170.3, 38.3) * mm, "end": v(170.69, 38.11) * mm});
            skLineSegment(sketch, "E2059", {"start": v(170.69, 38.11) * mm, "end": v(171.15, 38.12) * mm});
            skLineSegment(sketch, "E2060", {"start": v(171.15, 38.12) * mm, "end": v(171.59, 38.32) * mm});
            skLineSegment(sketch, "E2061", {"start": v(171.59, 38.32) * mm, "end": v(171.9, 38.56) * mm});
            skLineSegment(sketch, "E2062", {"start": v(171.9, 38.56) * mm, "end": v(172, 38.65) * mm});
            skLineSegment(sketch, "E2063", {"start": v(172, 38.65) * mm, "end": v(172.23, 38.86) * mm});
            skLineSegment(sketch, "E2064", {"start": v(172.23, 38.86) * mm, "end": v(174.5, 40.95) * mm});
            skLineSegment(sketch, "E2065", {"start": v(174.5, 40.95) * mm, "end": v(174.72, 41.16) * mm});
            skLineSegment(sketch, "E2066", {"start": v(174.72, 41.16) * mm, "end": v(175.71, 42.14) * mm});
            skLineSegment(sketch, "E2067", {"start": v(175.71, 42.14) * mm, "end": v(185.6, 51.88) * mm});
            skLineSegment(sketch, "E2068", {"start": v(185.6, 51.88) * mm, "end": v(186.59, 52.87) * mm});
            skLineSegment(sketch, "E2069", {"start": v(186.59, 52.87) * mm, "end": v(186.9, 53.17) * mm});
            skLineSegment(sketch, "E2070", {"start": v(186.9, 53.17) * mm, "end": v(188.34, 54.75) * mm});
            skLineSegment(sketch, "E2071", {"start": v(188.34, 54.75) * mm, "end": v(189.77, 56.34) * mm});
            skLineSegment(sketch, "E2072", {"start": v(189.77, 56.34) * mm, "end": v(190.08, 56.64) * mm});
            skLineSegment(sketch, "E2073", {"start": v(190.08, 56.64) * mm, "end": v(190.26, 56.83) * mm});
            skLineSegment(sketch, "E2074", {"start": v(190.26, 56.83) * mm, "end": v(190.71, 57.8) * mm});
            skLineSegment(sketch, "E2075", {"start": v(190.71, 57.8) * mm, "end": v(190.56, 58.82) * mm});
            skLineSegment(sketch, "E2076", {"start": v(190.56, 58.82) * mm, "end": v(190.45, 59.05) * mm});
            skLineSegment(sketch, "E2077", {"start": v(190.45, 59.05) * mm, "end": v(190.37, 59.2) * mm});
            skLineSegment(sketch, "E2078", {"start": v(190.37, 59.2) * mm, "end": v(189.69, 60.77) * mm});
            skLineSegment(sketch, "E2079", {"start": v(189.69, 60.77) * mm, "end": v(189.62, 60.93) * mm});
            skLineSegment(sketch, "E2080", {"start": v(189.62, 60.93) * mm, "end": v(189.53, 61.14) * mm});
            skLineSegment(sketch, "E2081", {"start": v(189.53, 61.14) * mm, "end": v(189.29, 61.8) * mm});
            skLineSegment(sketch, "E2082", {"start": v(189.29, 61.8) * mm, "end": v(189.28, 62.34) * mm});
            skLineSegment(sketch, "E2083", {"start": v(189.28, 62.34) * mm, "end": v(189.7, 62.8) * mm});
            skLineSegment(sketch, "E2084", {"start": v(189.7, 62.8) * mm, "end": v(190.39, 63.25) * mm});
            skLineSegment(sketch, "E2085", {"start": v(190.39, 63.25) * mm, "end": v(190.62, 63.4) * mm});
            skLineSegment(sketch, "E2086", {"start": v(190.62, 63.4) * mm, "end": v(190.65, 63.38) * mm});
            skLineSegment(sketch, "E2087", {"start": v(190.65, 63.38) * mm, "end": v(190.9, 63.15) * mm});
            skLineSegment(sketch, "E2088", {"start": v(190.9, 63.15) * mm, "end": v(190.92, 63.12) * mm});
            skLineSegment(sketch, "E2089", {"start": v(190.92, 63.12) * mm, "end": v(191.34, 62.11) * mm});
            skLineSegment(sketch, "E2090", {"start": v(191.34, 62.11) * mm, "end": v(192.88, 59.2) * mm});
            skLineSegment(sketch, "E2091", {"start": v(192.88, 59.2) * mm, "end": v(195.2, 55.5) * mm});
            skLineSegment(sketch, "E2092", {"start": v(195.2, 55.5) * mm, "end": v(197.64, 51.88) * mm});
            skLineSegment(sketch, "E2093", {"start": v(197.64, 51.88) * mm, "end": v(199.43, 49.14) * mm});
            skLineSegment(sketch, "E2094", {"start": v(199.43, 49.14) * mm, "end": v(199.99, 48.2) * mm});
            skLineSegment(sketch, "E2095", {"start": v(199.99, 48.2) * mm, "end": v(200.37, 47.56) * mm});
            skLineSegment(sketch, "E2096", {"start": v(200.37, 47.56) * mm, "end": v(204.04, 40.97) * mm});
            skLineSegment(sketch, "E2097", {"start": v(204.04, 40.97) * mm, "end": v(204.42, 40.32) * mm});
            skLineSegment(sketch, "E2098", {"start": v(204.42, 40.32) * mm, "end": v(204.54, 40.1) * mm});
            skLineSegment(sketch, "E2099", {"start": v(204.54, 40.1) * mm, "end": v(204.77, 39.15) * mm});
            skLineSegment(sketch, "E2100", {"start": v(204.77, 39.15) * mm, "end": v(204.42, 38.26) * mm});
            skLineSegment(sketch, "E2101", {"start": v(204.42, 38.26) * mm, "end": v(204.24, 38.09) * mm});
            skLineSegment(sketch, "E2102", {"start": v(204.24, 38.09) * mm, "end": v(203.86, 37.72) * mm});
            skLineSegment(sketch, "E2103", {"start": v(203.86, 37.72) * mm, "end": v(200.03, 34.04) * mm});
            skLineSegment(sketch, "E2104", {"start": v(200.03, 34.04) * mm, "end": v(199.64, 33.68) * mm});
            skLineSegment(sketch, "E2105", {"start": v(199.64, 33.68) * mm, "end": v(199.58, 33.61) * mm});
            skLineSegment(sketch, "E2106", {"start": v(199.58, 33.61) * mm, "end": v(199.2, 33.4) * mm});
            skLineSegment(sketch, "E2107", {"start": v(199.2, 33.4) * mm, "end": v(198.81, 33.49) * mm});
            skLineSegment(sketch, "E2108", {"start": v(198.81, 33.49) * mm, "end": v(198.75, 33.57) * mm});
            skLineSegment(sketch, "E2109", {"start": v(198.75, 33.57) * mm, "end": v(198.7, 33.65) * mm});
            skLineSegment(sketch, "E2110", {"start": v(198.7, 33.65) * mm, "end": v(198.49, 33.89) * mm});
            skLineSegment(sketch, "E2111", {"start": v(198.49, 33.89) * mm, "end": v(198.24, 34.22) * mm});
            skLineSegment(sketch, "E2112", {"start": v(198.24, 34.22) * mm, "end": v(198.12, 34.62) * mm});
            skLineSegment(sketch, "E2113", {"start": v(198.12, 34.62) * mm, "end": v(198.17, 35) * mm});
            skLineSegment(sketch, "E2114", {"start": v(198.17, 35) * mm, "end": v(198.22, 35.12) * mm});
            skLineSegment(sketch, "E2115", {"start": v(198.22, 35.12) * mm, "end": v(198.42, 35.57) * mm});
            skLineSegment(sketch, "E2116", {"start": v(198.42, 35.57) * mm, "end": v(199.5, 37.76) * mm});
            skLineSegment(sketch, "E2117", {"start": v(199.5, 37.76) * mm, "end": v(200.37, 40.04) * mm});
            skLineSegment(sketch, "E2118", {"start": v(200.37, 40.04) * mm, "end": v(200.47, 40.53) * mm});
            skLineSegment(sketch, "E2119", {"start": v(200.47, 40.53) * mm, "end": v(200.5, 40.63) * mm});
            skLineSegment(sketch, "E2120", {"start": v(200.5, 40.63) * mm, "end": v(200.6, 41.07) * mm});
            skLineSegment(sketch, "E2121", {"start": v(200.6, 41.07) * mm, "end": v(200.56, 41.54) * mm});
            skLineSegment(sketch, "E2122", {"start": v(200.56, 41.54) * mm, "end": v(200.5, 41.65) * mm});
            skLineSegment(sketch, "E2123", {"start": v(200.5, 41.65) * mm, "end": v(200.06, 42.51) * mm});
            skLineSegment(sketch, "E2124", {"start": v(200.06, 42.51) * mm, "end": v(197.83, 46.8) * mm});
            skLineSegment(sketch, "E2125", {"start": v(197.83, 46.8) * mm, "end": v(195.35, 51.04) * mm});
            skLineSegment(sketch, "E2126", {"start": v(195.35, 51.04) * mm, "end": v(194.79, 51.87) * mm});
            skLineSegment(sketch, "E2127", {"start": v(194.79, 51.87) * mm, "end": v(194.03, 51.22) * mm});
            skLineSegment(sketch, "E2128", {"start": v(194.03, 51.22) * mm, "end": v(190.46, 47.87) * mm});
            skLineSegment(sketch, "E2129", {"start": v(190.46, 47.87) * mm, "end": v(187.02, 44.5) * mm});
            skLineSegment(sketch, "E2130", {"start": v(187.02, 44.5) * mm, "end": v(186.33, 43.84) * mm});
            skLineSegment(sketch, "E2131", {"start": v(186.33, 43.84) * mm, "end": v(186.22, 43.74) * mm});
            skLineSegment(sketch, "E2132", {"start": v(186.22, 43.74) * mm, "end": v(185.85, 43.17) * mm});
            skLineSegment(sketch, "E2133", {"start": v(185.85, 43.17) * mm, "end": v(185.88, 42.53) * mm});
            skLineSegment(sketch, "E2134", {"start": v(185.88, 42.53) * mm, "end": v(185.97, 42.39) * mm});
            skLineSegment(sketch, "E2135", {"start": v(185.97, 42.39) * mm, "end": v(186.28, 41.88) * mm});
            skLineSegment(sketch, "E2136", {"start": v(186.28, 41.88) * mm, "end": v(187.78, 39.3) * mm});
            skLineSegment(sketch, "E2137", {"start": v(187.78, 39.3) * mm, "end": v(189.5, 36.85) * mm});
            skLineSegment(sketch, "E2138", {"start": v(189.5, 36.85) * mm, "end": v(189.92, 36.41) * mm});
            skLineSegment(sketch, "E2139", {"start": v(189.92, 36.41) * mm, "end": v(190.07, 36.26) * mm});
            skLineSegment(sketch, "E2140", {"start": v(190.07, 36.26) * mm, "end": v(190.79, 35.91) * mm});
            skLineSegment(sketch, "E2141", {"start": v(190.79, 35.91) * mm, "end": v(191.53, 36.08) * mm});
            skLineSegment(sketch, "E2142", {"start": v(191.53, 36.08) * mm, "end": v(191.7, 36.2) * mm});
            skLineSegment(sketch, "E2143", {"start": v(191.7, 36.2) * mm, "end": v(191.86, 36.3) * mm});
            skLineSegment(sketch, "E2144", {"start": v(191.86, 36.3) * mm, "end": v(193.53, 37.45) * mm});
            skLineSegment(sketch, "E2145", {"start": v(193.53, 37.45) * mm, "end": v(193.7, 37.55) * mm});
            skLineSegment(sketch, "E2146", {"start": v(193.7, 37.55) * mm, "end": v(193.82, 37.61) * mm});
            skLineSegment(sketch, "E2147", {"start": v(193.82, 37.61) * mm, "end": v(194.18, 37.77) * mm});
            skLineSegment(sketch, "E2148", {"start": v(194.18, 37.77) * mm, "end": v(194.65, 37.86) * mm});
            skLineSegment(sketch, "E2149", {"start": v(194.65, 37.86) * mm, "end": v(195.11, 37.75) * mm});
            skLineSegment(sketch, "E2150", {"start": v(195.11, 37.75) * mm, "end": v(195.45, 37.49) * mm});
            skLineSegment(sketch, "E2151", {"start": v(195.45, 37.49) * mm, "end": v(195.53, 37.38) * mm});
            skLineSegment(sketch, "E2152", {"start": v(195.53, 37.38) * mm, "end": v(195.61, 37.27) * mm});
            skLineSegment(sketch, "E2153", {"start": v(195.61, 37.27) * mm, "end": v(195.75, 36.89) * mm});
            skLineSegment(sketch, "E2154", {"start": v(195.75, 36.89) * mm, "end": v(195.66, 36.48) * mm});
            skLineSegment(sketch, "E2155", {"start": v(195.66, 36.48) * mm, "end": v(195.39, 36.13) * mm});
            skLineSegment(sketch, "E2156", {"start": v(195.39, 36.13) * mm, "end": v(195.13, 35.9) * mm});
            skLineSegment(sketch, "E2157", {"start": v(195.13, 35.9) * mm, "end": v(195.05, 35.82) * mm});
            skLineSegment(sketch, "E2158", {"start": v(195.05, 35.82) * mm, "end": v(194.36, 35.23) * mm});
            skLineSegment(sketch, "E2159", {"start": v(194.36, 35.23) * mm, "end": v(191.12, 32.04) * mm});
            skLineSegment(sketch, "E2160", {"start": v(191.12, 32.04) * mm, "end": v(187.97, 28.77) * mm});
            skLineSegment(sketch, "E2161", {"start": v(187.97, 28.77) * mm, "end": v(187.32, 28.13) * mm});
            skLineSegment(sketch, "E2162", {"start": v(187.32, 28.13) * mm, "end": v(187.26, 28.07) * mm});
            skLineSegment(sketch, "E2163", {"start": v(187.26, 28.07) * mm, "end": v(187.08, 27.87) * mm});
            skLineSegment(sketch, "E2164", {"start": v(187.08, 27.87) * mm, "end": v(186.81, 27.62) * mm});
            skLineSegment(sketch, "E2165", {"start": v(186.81, 27.62) * mm, "end": v(186.5, 27.51) * mm});
            skLineSegment(sketch, "E2166", {"start": v(186.5, 27.51) * mm, "end": v(186.22, 27.6) * mm});
            skLineSegment(sketch, "E2167", {"start": v(186.22, 27.6) * mm, "end": v(186.15, 27.66) * mm});
            skLineSegment(sketch, "E2168", {"start": v(186.15, 27.66) * mm, "end": v(186.05, 27.73) * mm});
            skLineSegment(sketch, "E2169", {"start": v(186.05, 27.73) * mm, "end": v(185.82, 27.98) * mm});
            skLineSegment(sketch, "E2170", {"start": v(185.82, 27.98) * mm, "end": v(185.62, 28.36) * mm});
            skLineSegment(sketch, "E2171", {"start": v(185.62, 28.36) * mm, "end": v(185.6, 28.8) * mm});
            skLineSegment(sketch, "E2172", {"start": v(185.6, 28.8) * mm, "end": v(185.73, 29.17) * mm});
            skLineSegment(sketch, "E2173", {"start": v(185.73, 29.17) * mm, "end": v(185.8, 29.27) * mm});
            skLineSegment(sketch, "E2174", {"start": v(185.8, 29.27) * mm, "end": v(185.95, 29.49) * mm});
            skLineSegment(sketch, "E2175", {"start": v(185.95, 29.49) * mm, "end": v(187.41, 31.6) * mm});
            skLineSegment(sketch, "E2176", {"start": v(187.41, 31.6) * mm, "end": v(187.58, 31.8) * mm});
            skLineSegment(sketch, "E2177", {"start": v(187.58, 31.8) * mm, "end": v(187.8, 32.06) * mm});
            skLineSegment(sketch, "E2178", {"start": v(187.8, 32.06) * mm, "end": v(188.27, 33.4) * mm});
            skLineSegment(sketch, "E2179", {"start": v(188.27, 33.4) * mm, "end": v(188.02, 34.78) * mm});
            skLineSegment(sketch, "E2180", {"start": v(188.02, 34.78) * mm, "end": v(187.86, 35.05) * mm});
            skLineSegment(sketch, "E2181", {"start": v(187.86, 35.05) * mm, "end": v(187.56, 35.57) * mm});
            skLineSegment(sketch, "E2182", {"start": v(187.56, 35.57) * mm, "end": v(184.24, 40.71) * mm});
            skLineSegment(sketch, "E2183", {"start": v(184.24, 40.71) * mm, "end": v(183.84, 41.23) * mm});
            skLineSegment(sketch, "E2184", {"start": v(183.84, 41.23) * mm, "end": v(183.58, 41) * mm});
            skLineSegment(sketch, "E2185", {"start": v(183.58, 41) * mm, "end": v(181.2, 38.72) * mm});
            skLineSegment(sketch, "E2186", {"start": v(181.2, 38.72) * mm, "end": v(180.98, 38.5) * mm});
            skLineSegment(sketch, "E2187", {"start": v(180.98, 38.5) * mm, "end": v(180.56, 38.09) * mm});
            skLineSegment(sketch, "E2188", {"start": v(180.56, 38.09) * mm, "end": v(176.37, 34.03) * mm});
            skLineSegment(sketch, "E2189", {"start": v(176.37, 34.03) * mm, "end": v(175.96, 33.62) * mm});
            skLineSegment(sketch, "E2190", {"start": v(175.96, 33.62) * mm, "end": v(175.75, 33.41) * mm});
            skLineSegment(sketch, "E2191", {"start": v(175.75, 33.41) * mm, "end": v(175.16, 32.76) * mm});
            skLineSegment(sketch, "E2192", {"start": v(175.16, 32.76) * mm, "end": v(174.81, 32.08) * mm});
            skLineSegment(sketch, "E2193", {"start": v(174.81, 32.08) * mm, "end": v(174.89, 31.3) * mm});
            skLineSegment(sketch, "E2194", {"start": v(174.89, 31.3) * mm, "end": v(175.22, 30.48) * mm});
            skLineSegment(sketch, "E2195", {"start": v(175.22, 30.48) * mm, "end": v(175.35, 30.21) * mm});
            skLineSegment(sketch, "E2196", {"start": v(175.35, 30.21) * mm, "end": v(175.64, 29.59) * mm});
            skLineSegment(sketch, "E2197", {"start": v(175.64, 29.59) * mm, "end": v(177.34, 26.62) * mm});
            skLineSegment(sketch, "E2198", {"start": v(177.34, 26.62) * mm, "end": v(179.3, 23.8) * mm});
            skLineSegment(sketch, "E2199", {"start": v(179.3, 23.8) * mm, "end": v(179.72, 23.26) * mm});
            skLineSegment(sketch, "E2200", {"start": v(179.72, 23.26) * mm, "end": v(179.97, 22.95) * mm});
            skLineSegment(sketch, "E2201", {"start": v(179.97, 22.95) * mm, "end": v(180.9, 22.12) * mm});
            skLineSegment(sketch, "E2202", {"start": v(180.9, 22.12) * mm, "end": v(182.2, 21.48) * mm});
            skLineSegment(sketch, "E2203", {"start": v(182.2, 21.48) * mm, "end": v(183.65, 21.3) * mm});
            skLineSegment(sketch, "E2204", {"start": v(183.65, 21.3) * mm, "end": v(184.84, 21.4) * mm});
            skLineSegment(sketch, "E2205", {"start": v(184.84, 21.4) * mm, "end": v(185.22, 21.5) * mm});
            skLineSegment(sketch, "E2206", {"start": v(185.22, 21.5) * mm, "end": v(185.4, 21.54) * mm});
            skLineSegment(sketch, "E2207", {"start": v(185.4, 21.54) * mm, "end": v(187.2, 22.11) * mm});
            skLineSegment(sketch, "E2208", {"start": v(187.2, 22.11) * mm, "end": v(187.38, 22.17) * mm});
            skLineSegment(sketch, "E2209", {"start": v(187.38, 22.17) * mm, "end": v(187.56, 22.24) * mm});
            skLineSegment(sketch, "E2210", {"start": v(187.56, 22.24) * mm, "end": v(188.27, 22.16) * mm});
            skLineSegment(sketch, "E2211", {"start": v(188.27, 22.16) * mm, "end": v(188.78, 21.64) * mm});
            skLineSegment(sketch, "E2212", {"start": v(188.78, 21.64) * mm, "end": v(188.88, 21.49) * mm});
            skLineSegment(sketch, "E2213", {"start": v(188.88, 21.49) * mm, "end": v(188.94, 21.39) * mm});
            skLineSegment(sketch, "E2214", {"start": v(188.94, 21.39) * mm, "end": v(189.04, 21.03) * mm});
            skLineSegment(sketch, "E2215", {"start": v(189.04, 21.03) * mm, "end": v(188.94, 20.7) * mm});
            skLineSegment(sketch, "E2216", {"start": v(188.94, 20.7) * mm, "end": v(188.68, 20.43) * mm});
            skLineSegment(sketch, "E2217", {"start": v(188.68, 20.43) * mm, "end": v(188.44, 20.25) * mm});
            skLineSegment(sketch, "E2218", {"start": v(188.44, 20.25) * mm, "end": v(188.35, 20.19) * mm});
            skLineSegment(sketch, "E2219", {"start": v(188.35, 20.19) * mm, "end": v(187.84, 19.84) * mm});
            skLineSegment(sketch, "E2220", {"start": v(187.84, 19.84) * mm, "end": v(182.78, 16.31) * mm});
            skLineSegment(sketch, "E2221", {"start": v(182.78, 16.31) * mm, "end": v(182.28, 15.95) * mm});
            skLineSegment(sketch, "E2222", {"start": v(182.28, 15.95) * mm, "end": v(182.16, 15.87) * mm});
            skLineSegment(sketch, "E2223", {"start": v(182.16, 15.87) * mm, "end": v(181.78, 15.69) * mm});
            skLineSegment(sketch, "E2224", {"start": v(181.78, 15.69) * mm, "end": v(181.36, 15.67) * mm});
            skLineSegment(sketch, "E2225", {"start": v(181.36, 15.67) * mm, "end": v(180.98, 15.88) * mm});
            skLineSegment(sketch, "E2226", {"start": v(180.98, 15.88) * mm, "end": v(180.68, 16.18) * mm});
            skLineSegment(sketch, "E2227", {"start": v(180.68, 16.18) * mm, "end": v(180.6, 16.29) * mm});
            skLineSegment(sketch, "E2228", {"start": v(180.6, 16.29) * mm, "end": v(180.17, 16.8) * mm});
            skLineSegment(sketch, "E2229", {"start": v(180.17, 16.8) * mm, "end": v(178.45, 19.64) * mm});
            skLineSegment(sketch, "E2230", {"start": v(178.45, 19.64) * mm, "end": v(176.94, 22.59) * mm});
            skLineSegment(sketch, "E2231", {"start": v(176.94, 22.59) * mm, "end": v(176.62, 23.17) * mm});
            skLineSegment(sketch, "E2232", {"start": v(176.62, 23.17) * mm, "end": v(176.02, 24.26) * mm});
            skLineSegment(sketch, "E2233", {"start": v(176.02, 24.26) * mm, "end": v(169.5, 34.94) * mm});
            skLineSegment(sketch, "E2234", {"start": v(169.5, 34.94) * mm, "end": v(168.8, 35.98) * mm});
            skLineSegment(sketch, "E2235", {"start": v(168.8, 35.98) * mm, "end": v(168.3, 36.7) * mm});
            skLineSegment(sketch, "E2236", {"start": v(168.3, 36.7) * mm, "end": v(166.01, 40.44) * mm});
            skLineSegment(sketch, "E2237", {"start": v(166.01, 40.44) * mm, "end": v(163.55, 44.02) * mm});
            skLineSegment(sketch, "E2238", {"start": v(163.55, 44.02) * mm, "end": v(162.98, 44.67) * mm});
            skLineSegment(sketch, "E2239", {"start": v(162.98, 44.67) * mm, "end": v(162.65, 45.04) * mm});
            skLineSegment(sketch, "E2240", {"start": v(162.65, 45.04) * mm, "end": v(161.85, 46.33) * mm});
            skLineSegment(sketch, "E2241", {"start": v(161.85, 46.33) * mm, "end": v(161.43, 47.93) * mm});
            skLineSegment(sketch, "E2242", {"start": v(161.43, 47.93) * mm, "end": v(161.59, 49.57) * mm});
            skLineSegment(sketch, "E2243", {"start": v(161.59, 49.57) * mm, "end": v(162.01, 50.88) * mm});
            skLineSegment(sketch, "E2244", {"start": v(162.01, 50.88) * mm, "end": v(162.2, 51.3) * mm});
            skLineSegment(sketch, "E2245", {"start": v(162.2, 51.3) * mm, "end": v(162.52, 52.04) * mm});
            skLineSegment(sketch, "E2246", {"start": v(162.52, 52.04) * mm, "end": v(165.52, 59.51) * mm});
            skLineSegment(sketch, "E2247", {"start": v(165.52, 59.51) * mm, "end": v(165.82, 60.26) * mm});
            skLineSegment(sketch, "E2248", {"start": v(165.82, 60.26) * mm, "end": v(165.92, 60.54) * mm});
            skLineSegment(sketch, "E2249", {"start": v(165.92, 60.54) * mm, "end": v(166.9, 63.28) * mm});
            skLineSegment(sketch, "E2250", {"start": v(166.9, 63.28) * mm, "end": v(167, 63.55) * mm});
            skLineSegment(sketch, "E2251", {"start": v(167, 63.55) * mm, "end": v(167.12, 63.82) * mm});
            skLineSegment(sketch, "E2252", {"start": v(167.12, 63.82) * mm, "end": v(167.27, 64.74) * mm});
            skLineSegment(sketch, "E2253", {"start": v(167.27, 64.74) * mm, "end": v(167.05, 65.79) * mm});
            skLineSegment(sketch, "E2254", {"start": v(167.05, 65.79) * mm, "end": v(166.51, 66.73) * mm});
            skLineSegment(sketch, "E2255", {"start": v(166.51, 66.73) * mm, "end": v(166, 67.4) * mm});
            skLineSegment(sketch, "E2256", {"start": v(166, 67.4) * mm, "end": v(165.82, 67.61) * mm});
            skLineSegment(sketch, "E2257", {"start": v(165.82, 67.61) * mm, "end": v(165.74, 67.7) * mm});
            skLineSegment(sketch, "E2258", {"start": v(165.74, 67.7) * mm, "end": v(165.42, 67.9) * mm});
            skLineSegment(sketch, "E2259", {"start": v(165.42, 67.9) * mm, "end": v(165.08, 67.81) * mm});
            skLineSegment(sketch, "E2260", {"start": v(165.08, 67.81) * mm, "end": v(164.78, 67.54) * mm});
            skLineSegment(sketch, "E2261", {"start": v(164.78, 67.54) * mm, "end": v(164.58, 67.31) * mm});
            skLineSegment(sketch, "E2262", {"start": v(164.58, 67.31) * mm, "end": v(164.5, 67.24) * mm});
            skLineSegment(sketch, "E2263", {"start": v(164.5, 67.24) * mm, "end": v(164.03, 66.72) * mm});
            skLineSegment(sketch, "E2264", {"start": v(164.03, 66.72) * mm, "end": v(159.27, 61.54) * mm});
            skLineSegment(sketch, "E2265", {"start": v(159.27, 61.54) * mm, "end": v(158.8, 61.03) * mm});
            skLineSegment(sketch, "E2266", {"start": v(158.8, 61.03) * mm, "end": v(158.73, 60.95) * mm});
            skLineSegment(sketch, "E2267", {"start": v(158.73, 60.95) * mm, "end": v(158.06, 60.17) * mm});
            skLineSegment(sketch, "E2268", {"start": v(158.06, 60.17) * mm, "end": v(157.98, 60.1) * mm});
            skLineSegment(sketch, "E2269", {"start": v(157.98, 60.1) * mm, "end": v(157.82, 59.96) * mm});
            skLineSegment(sketch, "E2270", {"start": v(157.82, 59.96) * mm, "end": v(157.4, 59.46) * mm});
            skLineSegment(sketch, "E2271", {"start": v(157.4, 59.46) * mm, "end": v(157.1, 58.77) * mm});
            skLineSegment(sketch, "E2272", {"start": v(157.1, 58.77) * mm, "end": v(157.1, 58.02) * mm});
            skLineSegment(sketch, "E2273", {"start": v(157.1, 58.02) * mm, "end": v(157.28, 57.38) * mm});
            skLineSegment(sketch, "E2274", {"start": v(157.28, 57.38) * mm, "end": v(157.37, 57.18) * mm});
            skLineSegment(sketch, "E2275", {"start": v(157.37, 57.18) * mm, "end": v(157.47, 56.98) * mm});
            skLineSegment(sketch, "E2276", {"start": v(157.47, 56.98) * mm, "end": v(158.17, 54.87) * mm});
            skLineSegment(sketch, "E2277", {"start": v(158.17, 54.87) * mm, "end": v(158.25, 54.66) * mm});
            skLineSegment(sketch, "E2278", {"start": v(158.25, 54.66) * mm, "end": v(158.29, 54.53) * mm});
            skLineSegment(sketch, "E2279", {"start": v(158.29, 54.53) * mm, "end": v(158.32, 54.1) * mm});
            skLineSegment(sketch, "E2280", {"start": v(158.32, 54.1) * mm, "end": v(158.17, 53.63) * mm});
            skLineSegment(sketch, "E2281", {"start": v(158.17, 53.63) * mm, "end": v(157.87, 53.25) * mm});
            skLineSegment(sketch, "E2282", {"start": v(157.87, 53.25) * mm, "end": v(157.56, 53) * mm});
            skLineSegment(sketch, "E2283", {"start": v(157.56, 53) * mm, "end": v(157.45, 52.95) * mm});
            skLineSegment(sketch, "E2284", {"start": v(157.45, 52.95) * mm, "end": v(157.34, 52.89) * mm});
            skLineSegment(sketch, "E2285", {"start": v(157.34, 52.89) * mm, "end": v(156.96, 52.82) * mm});
            skLineSegment(sketch, "E2286", {"start": v(156.96, 52.82) * mm, "end": v(156.55, 52.96) * mm});
            skLineSegment(sketch, "E2287", {"start": v(156.55, 52.96) * mm, "end": v(156.24, 53.28) * mm});
            skLineSegment(sketch, "E2288", {"start": v(156.24, 53.28) * mm, "end": v(156.05, 53.57) * mm});
            skLineSegment(sketch, "E2289", {"start": v(156.05, 53.57) * mm, "end": v(156, 53.68) * mm});
            skLineSegment(sketch, "E2290", {"start": v(156, 53.68) * mm, "end": v(155.6, 54.6) * mm});
            skLineSegment(sketch, "E2291", {"start": v(155.6, 54.6) * mm, "end": v(153, 58.81) * mm});
            skLineSegment(sketch, "E2292", {"start": v(153, 58.81) * mm, "end": v(149.95, 62.73) * mm});
            skLineSegment(sketch, "E2293", {"start": v(149.95, 62.73) * mm, "end": v(149.32, 63.5) * mm});
            skLineSegment(sketch, "E2294", {"start": v(149.32, 63.5) * mm, "end": v(149.27, 63.55) * mm});
            skLineSegment(sketch, "E2295", {"start": v(149.27, 63.55) * mm, "end": v(148.88, 64.1) * mm});
            skLineSegment(sketch, "E2296", {"start": v(148.88, 64.1) * mm, "end": v(148.85, 64.17) * mm});
            skLineSegment(sketch, "E2297", {"start": v(148.85, 64.17) * mm, "end": v(148.8, 64.26) * mm});
            skLineSegment(sketch, "E2298", {"start": v(148.8, 64.26) * mm, "end": v(148.8, 64.66) * mm});
            skLineSegment(sketch, "E2299", {"start": v(148.8, 64.66) * mm, "end": v(149, 65.03) * mm});
            skLineSegment(sketch, "E2300", {"start": v(149, 65.03) * mm, "end": v(149.06, 65.1) * mm});
            skLineSegment(sketch, "E2301", {"start": v(149.06, 65.1) * mm, "end": v(149.14, 65.18) * mm});
            skLineSegment(sketch, "E2302", {"start": v(149.14, 65.18) * mm, "end": v(149.57, 65.44) * mm});
            skLineSegment(sketch, "E2303", {"start": v(149.57, 65.44) * mm, "end": v(150.05, 65.4) * mm});
            skLineSegment(sketch, "E2304", {"start": v(150.05, 65.4) * mm, "end": v(150.15, 65.34) * mm});
            skLineSegment(sketch, "E2305", {"start": v(150.15, 65.34) * mm, "end": v(150.24, 65.3) * mm});
            skLineSegment(sketch, "E2306", {"start": v(150.24, 65.3) * mm, "end": v(151.03, 64.65) * mm});
            skLineSegment(sketch, "E2307", {"start": v(151.03, 64.65) * mm, "end": v(151.12, 64.58) * mm});
            skLineSegment(sketch, "E2308", {"start": v(151.12, 64.58) * mm, "end": v(151.33, 64.4) * mm});
            skLineSegment(sketch, "E2309", {"start": v(151.33, 64.4) * mm, "end": v(152.02, 63.92) * mm});
            skLineSegment(sketch, "E2310", {"start": v(152.02, 63.92) * mm, "end": v(152.68, 63.73) * mm});
            skLineSegment(sketch, "E2311", {"start": v(152.68, 63.73) * mm, "end": v(153.31, 64.03) * mm});
            skLineSegment(sketch, "E2312", {"start": v(153.31, 64.03) * mm, "end": v(153.94, 64.63) * mm});
            skLineSegment(sketch, "E2313", {"start": v(153.94, 64.63) * mm, "end": v(154.14, 64.84) * mm});
            skLineSegment(sketch, "E2314", {"start": v(154.14, 64.84) * mm, "end": v(155.52, 66.35) * mm});
            skLineSegment(sketch, "E2315", {"start": v(155.52, 66.35) * mm, "end": v(169.29, 81.4) * mm});
            skLineSegment(sketch, "E2316", {"start": v(169.29, 81.4) * mm, "end": v(170.67, 82.9) * mm});
            skLineSegment(sketch, "E2317", {"start": v(170.67, 82.9) * mm, "end": v(170.88, 83.13) * mm});
            skLineSegment(sketch, "E2318", {"start": v(170.88, 83.13) * mm, "end": v(171.5, 83.85) * mm});
            skLineSegment(sketch, "E2319", {"start": v(171.5, 83.85) * mm, "end": v(171.8, 84.54) * mm});
            skLineSegment(sketch, "E2320", {"start": v(171.8, 84.54) * mm, "end": v(171.67, 85.3) * mm});
            skLineSegment(sketch, "E2321", {"start": v(171.67, 85.3) * mm, "end": v(171.26, 86.16) * mm});
            skLineSegment(sketch, "E2322", {"start": v(171.26, 86.16) * mm, "end": v(171.11, 86.45) * mm});
            skLineSegment(sketch, "E2323", {"start": v(171.11, 86.45) * mm, "end": v(171.07, 86.54) * mm});
            skLineSegment(sketch, "E2324", {"start": v(171.07, 86.54) * mm, "end": v(170.61, 87.46) * mm});
            skLineSegment(sketch, "E2325", {"start": v(170.61, 87.46) * mm, "end": v(170.58, 87.55) * mm});
            skLineSegment(sketch, "E2326", {"start": v(170.58, 87.55) * mm, "end": v(170.54, 87.66) * mm});
            skLineSegment(sketch, "E2327", {"start": v(170.54, 87.66) * mm, "end": v(170.52, 88) * mm});
            skLineSegment(sketch, "E2328", {"start": v(170.52, 88) * mm, "end": v(170.67, 88.35) * mm});
            skLineSegment(sketch, "E2329", {"start": v(170.67, 88.35) * mm, "end": v(170.94, 88.65) * mm});
            skLineSegment(sketch, "E2330", {"start": v(170.94, 88.65) * mm, "end": v(171.18, 88.83) * mm});
            skLineSegment(sketch, "E2331", {"start": v(171.18, 88.83) * mm, "end": v(171.26, 88.9) * mm});
            skLineSegment(sketch, "E2332", {"start": v(171.26, 88.9) * mm, "end": v(171.37, 88.97) * mm});
            skLineSegment(sketch, "E2333", {"start": v(171.37, 88.97) * mm, "end": v(171.85, 88.96) * mm});
            skLineSegment(sketch, "E2334", {"start": v(171.85, 88.96) * mm, "end": v(172.24, 88.64) * mm});
            skLineSegment(sketch, "E2335", {"start": v(172.24, 88.64) * mm, "end": v(172.3, 88.55) * mm});
            skLineSegment(sketch, "E2336", {"start": v(172.3, 88.55) * mm, "end": v(172.44, 88.38) * mm});
            skLineSegment(sketch, "E2337", {"start": v(172.44, 88.38) * mm, "end": v(173.81, 86.62) * mm});
            skLineSegment(sketch, "E2338", {"start": v(173.81, 86.62) * mm, "end": v(173.93, 86.44) * mm});
            skLineSegment(sketch, "E2339", {"start": v(173.93, 86.44) * mm, "end": v(174.36, 85.77) * mm});
            skLineSegment(sketch, "E2340", {"start": v(174.36, 85.77) * mm, "end": v(176.77, 82.66) * mm});
            skLineSegment(sketch, "E2341", {"start": v(176.77, 82.66) * mm, "end": v(179.36, 79.7) * mm});
            skLineSegment(sketch, "E2342", {"start": v(179.36, 79.7) * mm, "end": v(179.88, 79.1) * mm});
            skLineSegment(sketch, "E2343", {"start": v(179.88, 79.1) * mm, "end": v(180.47, 78.42) * mm});
            skLineSegment(sketch, "E2344", {"start": v(180.47, 78.42) * mm, "end": v(181.99, 76.11) * mm});
            skLineSegment(sketch, "E2345", {"start": v(181.99, 76.11) * mm, "end": v(183.22, 72.92) * mm});
            skLineSegment(sketch, "E2346", {"start": v(183.22, 72.92) * mm, "end": v(183.55, 69.53) * mm});
            skLineSegment(sketch, "E2347", {"start": v(183.55, 69.53) * mm, "end": v(183.18, 66.8) * mm});
            skLineSegment(sketch, "E2348", {"start": v(183.18, 66.8) * mm, "end": v(182.91, 65.92) * mm});
            skLineSegment(sketch, "E2349", {"start": v(182.91, 65.92) * mm, "end": v(182.72, 65.27) * mm});
            skLineSegment(sketch, "E2350", {"start": v(182.72, 65.27) * mm, "end": v(181.7, 63.44) * mm});
            skLineSegment(sketch, "E2351", {"start": v(181.7, 63.44) * mm, "end": v(179.76, 61.44) * mm});
            skLineSegment(sketch, "E2352", {"start": v(179.76, 61.44) * mm, "end": v(177.3, 60.23) * mm});
            skLineSegment(sketch, "E2353", {"start": v(177.3, 60.23) * mm, "end": v(175.2, 59.98) * mm});
            skLineSegment(sketch, "E2354", {"start": v(175.2, 59.98) * mm, "end": v(174.54, 60.1) * mm});
            skLineSegment(sketch, "E2355", {"start": v(174.54, 60.1) * mm, "end": v(174.3, 60.13) * mm});
            skLineSegment(sketch, "E2356", {"start": v(174.3, 60.13) * mm, "end": v(173.15, 60.44) * mm});
            skLineSegment(sketch, "E2357", {"start": v(173.15, 60.44) * mm, "end": v(171.97, 60.8) * mm});
            skLineSegment(sketch, "E2358", {"start": v(171.97, 60.8) * mm, "end": v(171.73, 60.86) * mm});
            skLineSegment(sketch, "E2359", {"start": v(-70.3, 180.21) * mm, "end": v(-69.73, 180.21) * mm});
            skLineSegment(sketch, "E2360", {"start": v(-69.73, 180.21) * mm, "end": v(-67.18, 180.86) * mm});
            skLineSegment(sketch, "E2361", {"start": v(-67.18, 180.86) * mm, "end": v(-64.91, 182.2) * mm});
            skLineSegment(sketch, "E2362", {"start": v(-64.91, 182.2) * mm, "end": v(-64.5, 182.54) * mm});
            skLineSegment(sketch, "E2363", {"start": v(-64.5, 182.54) * mm, "end": v(-63.59, 183.28) * mm});
            skLineSegment(sketch, "E2364", {"start": v(-63.59, 183.28) * mm, "end": v(-59.77, 187.53) * mm});
            skLineSegment(sketch, "E2365", {"start": v(-59.77, 187.53) * mm, "end": v(-56.82, 192.43) * mm});
            skLineSegment(sketch, "E2366", {"start": v(-56.82, 192.43) * mm, "end": v(-56.35, 193.5) * mm});
            skLineSegment(sketch, "E2367", {"start": v(-56.35, 193.5) * mm, "end": v(-56.27, 193.69) * mm});
            skLineSegment(sketch, "E2368", {"start": v(-56.27, 193.69) * mm, "end": v(-55.75, 195.67) * mm});
            skLineSegment(sketch, "E2369", {"start": v(-55.75, 195.67) * mm, "end": v(-55.73, 195.88) * mm});
            skLineSegment(sketch, "E2370", {"start": v(-55.73, 195.88) * mm, "end": v(-55.7, 196.29) * mm});
            skLineSegment(sketch, "E2371", {"start": v(-55.7, 196.29) * mm, "end": v(-55.75, 197.53) * mm});
            skLineSegment(sketch, "E2372", {"start": v(-55.75, 197.53) * mm, "end": v(-56.2, 198.76) * mm});
            skLineSegment(sketch, "E2373", {"start": v(-56.2, 198.76) * mm, "end": v(-57.15, 199.64) * mm});
            skLineSegment(sketch, "E2374", {"start": v(-57.15, 199.64) * mm, "end": v(-58.29, 200.19) * mm});
            skLineSegment(sketch, "E2375", {"start": v(-58.29, 200.19) * mm, "end": v(-58.68, 200.31) * mm});
            skLineSegment(sketch, "E2376", {"start": v(-58.68, 200.31) * mm, "end": v(-58.93, 200.4) * mm});
            skLineSegment(sketch, "E2377", {"start": v(-58.93, 200.4) * mm, "end": v(-59.69, 200.6) * mm});
            skLineSegment(sketch, "E2378", {"start": v(-59.69, 200.6) * mm, "end": v(-60.32, 200.58) * mm});
            skLineSegment(sketch, "E2379", {"start": v(-60.32, 200.58) * mm, "end": v(-60.84, 200.17) * mm});
            skLineSegment(sketch, "E2380", {"start": v(-60.84, 200.17) * mm, "end": v(-61.33, 199.5) * mm});
            skLineSegment(sketch, "E2381", {"start": v(-61.33, 199.5) * mm, "end": v(-61.49, 199.27) * mm});
            skLineSegment(sketch, "E2382", {"start": v(-61.49, 199.27) * mm, "end": v(-62.38, 197.95) * mm});
            skLineSegment(sketch, "E2383", {"start": v(-62.38, 197.95) * mm, "end": v(-71.27, 184.72) * mm});
            skLineSegment(sketch, "E2384", {"start": v(-71.27, 184.72) * mm, "end": v(-72.15, 183.4) * mm});
            skLineSegment(sketch, "E2385", {"start": v(-72.15, 183.4) * mm, "end": v(-72.25, 183.25) * mm});
            skLineSegment(sketch, "E2386", {"start": v(-72.25, 183.25) * mm, "end": v(-72.56, 182.85) * mm});
            skLineSegment(sketch, "E2387", {"start": v(-72.56, 182.85) * mm, "end": v(-72.97, 182.3) * mm});
            skLineSegment(sketch, "E2388", {"start": v(-72.97, 182.3) * mm, "end": v(-73.2, 181.7) * mm});
            skLineSegment(sketch, "E2389", {"start": v(-73.2, 181.7) * mm, "end": v(-73.17, 181.18) * mm});
            skLineSegment(sketch, "E2390", {"start": v(-73.17, 181.18) * mm, "end": v(-73.1, 181.04) * mm});
            skLineSegment(sketch, "E2391", {"start": v(-73.1, 181.04) * mm, "end": v(-73.02, 180.89) * mm});
            skLineSegment(sketch, "E2392", {"start": v(-73.02, 180.89) * mm, "end": v(-72.61, 180.51) * mm});
            skLineSegment(sketch, "E2393", {"start": v(-72.61, 180.51) * mm, "end": v(-71.96, 180.3) * mm});
            skLineSegment(sketch, "E2394", {"start": v(-71.96, 180.3) * mm, "end": v(-71.22, 180.26) * mm});
            skLineSegment(sketch, "E2395", {"start": v(-71.22, 180.26) * mm, "end": v(-70.67, 180.23) * mm});
            skLineSegment(sketch, "E2396", {"start": v(-70.67, 180.23) * mm, "end": v(-70.5, 180.21) * mm});
            skLineSegment(sketch, "E2397", {"start": v(-70.5, 180.21) * mm, "end": v(-70.48, 180.21) * mm});
            skLineSegment(sketch, "E2398", {"start": v(-70.48, 180.21) * mm, "end": v(-70.3, 180.21) * mm});
            skLineSegment(sketch, "E2399", {"start": v(-70.3, 180.21) * mm, "end": v(-70.3, 180.21) * mm});
            skLineSegment(sketch, "E2400", {"start": v(-68.83, 203.74) * mm, "end": v(-68.6, 203.79) * mm});
            skLineSegment(sketch, "E2401", {"start": v(-68.6, 203.79) * mm, "end": v(-67.67, 203.8) * mm});
            skLineSegment(sketch, "E2402", {"start": v(-67.67, 203.8) * mm, "end": v(-66.89, 203.66) * mm});
            skLineSegment(sketch, "E2403", {"start": v(-66.89, 203.66) * mm, "end": v(-66.74, 203.63) * mm});
            skLineSegment(sketch, "E2404", {"start": v(-66.74, 203.63) * mm, "end": v(-66.02, 203.47) * mm});
            skLineSegment(sketch, "E2405", {"start": v(-66.02, 203.47) * mm, "end": v(-58.84, 201.9) * mm});
            skLineSegment(sketch, "E2406", {"start": v(-58.84, 201.9) * mm, "end": v(-58.12, 201.74) * mm});
            skLineSegment(sketch, "E2407", {"start": v(-58.12, 201.74) * mm, "end": v(-57.77, 201.66) * mm});
            skLineSegment(sketch, "E2408", {"start": v(-57.77, 201.66) * mm, "end": v(-56.03, 201.2) * mm});
            skLineSegment(sketch, "E2409", {"start": v(-56.03, 201.2) * mm, "end": v(-54.34, 200.58) * mm});
            skLineSegment(sketch, "E2410", {"start": v(-54.34, 200.58) * mm, "end": v(-54.01, 200.43) * mm});
            skLineSegment(sketch, "E2411", {"start": v(-54.01, 200.43) * mm, "end": v(-53.46, 200.18) * mm});
            skLineSegment(sketch, "E2412", {"start": v(-53.46, 200.18) * mm, "end": v(-51.94, 199.05) * mm});
            skLineSegment(sketch, "E2413", {"start": v(-51.94, 199.05) * mm, "end": v(-50.63, 197.24) * mm});
            skLineSegment(sketch, "E2414", {"start": v(-50.63, 197.24) * mm, "end": v(-50.07, 195.07) * mm});
            skLineSegment(sketch, "E2415", {"start": v(-50.07, 195.07) * mm, "end": v(-50.12, 193.24) * mm});
            skLineSegment(sketch, "E2416", {"start": v(-50.12, 193.24) * mm, "end": v(-50.25, 192.65) * mm});
            skLineSegment(sketch, "E2417", {"start": v(-50.25, 192.65) * mm, "end": v(-50.29, 192.47) * mm});
            skLineSegment(sketch, "E2418", {"start": v(-50.29, 192.47) * mm, "end": v(-50.87, 190.67) * mm});
            skLineSegment(sketch, "E2419", {"start": v(-50.87, 190.67) * mm, "end": v(-50.94, 190.5) * mm});
            skLineSegment(sketch, "E2420", {"start": v(-50.94, 190.5) * mm, "end": v(-51.26, 189.73) * mm});
            skLineSegment(sketch, "E2421", {"start": v(-51.26, 189.73) * mm, "end": v(-52.5, 187.52) * mm});
            skLineSegment(sketch, "E2422", {"start": v(-52.5, 187.52) * mm, "end": v(-54.52, 184.91) * mm});
            skLineSegment(sketch, "E2423", {"start": v(-54.52, 184.91) * mm, "end": v(-56.91, 182.71) * mm});
            skLineSegment(sketch, "E2424", {"start": v(-56.91, 182.71) * mm, "end": v(-59.63, 180.96) * mm});
            skLineSegment(sketch, "E2425", {"start": v(-59.63, 180.96) * mm, "end": v(-62.6, 179.67) * mm});
            skLineSegment(sketch, "E2426", {"start": v(-62.6, 179.67) * mm, "end": v(-65.77, 178.9) * mm});
            skLineSegment(sketch, "E2427", {"start": v(-65.77, 178.9) * mm, "end": v(-69.06, 178.68) * mm});
            skLineSegment(sketch, "E2428", {"start": v(-69.06, 178.68) * mm, "end": v(-71.58, 178.87) * mm});
            skLineSegment(sketch, "E2429", {"start": v(-71.58, 178.87) * mm, "end": v(-72.4, 179.03) * mm});
            skLineSegment(sketch, "E2430", {"start": v(-72.4, 179.03) * mm, "end": v(-72.98, 179.14) * mm});
            skLineSegment(sketch, "E2431", {"start": v(-72.98, 179.14) * mm, "end": v(-78.68, 180.35) * mm});
            skLineSegment(sketch, "E2432", {"start": v(-78.68, 180.35) * mm, "end": v(-79.25, 180.47) * mm});
            skLineSegment(sketch, "E2433", {"start": v(-79.25, 180.47) * mm, "end": v(-79.45, 180.52) * mm});
            skLineSegment(sketch, "E2434", {"start": v(-79.45, 180.52) * mm, "end": v(-80.45, 180.76) * mm});
            skLineSegment(sketch, "E2435", {"start": v(-80.45, 180.76) * mm, "end": v(-81.47, 180.85) * mm});
            skLineSegment(sketch, "E2436", {"start": v(-81.47, 180.85) * mm, "end": v(-81.67, 180.8) * mm});
            skLineSegment(sketch, "E2437", {"start": v(-81.67, 180.8) * mm, "end": v(-81.8, 180.79) * mm});
            skLineSegment(sketch, "E2438", {"start": v(-81.8, 180.79) * mm, "end": v(-82.2, 180.83) * mm});
            skLineSegment(sketch, "E2439", {"start": v(-82.2, 180.83) * mm, "end": v(-82.62, 181.03) * mm});
            skLineSegment(sketch, "E2440", {"start": v(-82.62, 181.03) * mm, "end": v(-82.95, 181.3) * mm});
            skLineSegment(sketch, "E2441", {"start": v(-82.95, 181.3) * mm, "end": v(-83.19, 181.48) * mm});
            skLineSegment(sketch, "E2442", {"start": v(-83.19, 181.48) * mm, "end": v(-83.27, 181.52) * mm});
            skLineSegment(sketch, "E2443", {"start": v(-83.27, 181.52) * mm, "end": v(-83.28, 181.6) * mm});
            skLineSegment(sketch, "E2444", {"start": v(-83.28, 181.6) * mm, "end": v(-83.24, 181.88) * mm});
            skLineSegment(sketch, "E2445", {"start": v(-83.24, 181.88) * mm, "end": v(-83.09, 181.96) * mm});
            skLineSegment(sketch, "E2446", {"start": v(-83.09, 181.96) * mm, "end": v(-83.05, 181.95) * mm});
            skLineSegment(sketch, "E2447", {"start": v(-83.05, 181.95) * mm, "end": v(-82.64, 181.86) * mm});
            skLineSegment(sketch, "E2448", {"start": v(-82.64, 181.86) * mm, "end": v(-81.38, 181.87) * mm});
            skLineSegment(sketch, "E2449", {"start": v(-81.38, 181.87) * mm, "end": v(-80, 182.34) * mm});
            skLineSegment(sketch, "E2450", {"start": v(-80, 182.34) * mm, "end": v(-78.83, 183.27) * mm});
            skLineSegment(sketch, "E2451", {"start": v(-78.83, 183.27) * mm, "end": v(-78.04, 184.25) * mm});
            skLineSegment(sketch, "E2452", {"start": v(-78.04, 184.25) * mm, "end": v(-77.82, 184.6) * mm});
            skLineSegment(sketch, "E2453", {"start": v(-77.82, 184.6) * mm, "end": v(-77, 185.85) * mm});
            skLineSegment(sketch, "E2454", {"start": v(-77, 185.85) * mm, "end": v(-68.67, 198.23) * mm});
            skLineSegment(sketch, "E2455", {"start": v(-68.67, 198.23) * mm, "end": v(-67.84, 199.46) * mm});
            skLineSegment(sketch, "E2456", {"start": v(-67.84, 199.46) * mm, "end": v(-67.83, 199.48) * mm});
            skLineSegment(sketch, "E2457", {"start": v(-67.83, 199.48) * mm, "end": v(-67.73, 199.62) * mm});
            skLineSegment(sketch, "E2458", {"start": v(-67.73, 199.62) * mm, "end": v(-67.72, 199.64) * mm});
            skLineSegment(sketch, "E2459", {"start": v(-67.72, 199.64) * mm, "end": v(-67.6, 199.84) * mm});
            skLineSegment(sketch, "E2460", {"start": v(-67.6, 199.84) * mm, "end": v(-67.2, 200.46) * mm});
            skLineSegment(sketch, "E2461", {"start": v(-67.2, 200.46) * mm, "end": v(-66.84, 201.1) * mm});
            skLineSegment(sketch, "E2462", {"start": v(-66.84, 201.1) * mm, "end": v(-66.65, 201.61) * mm});
            skLineSegment(sketch, "E2463", {"start": v(-66.65, 201.61) * mm, "end": v(-66.66, 202.03) * mm});
            skLineSegment(sketch, "E2464", {"start": v(-66.66, 202.03) * mm, "end": v(-66.87, 202.41) * mm});
            skLineSegment(sketch, "E2465", {"start": v(-66.87, 202.41) * mm, "end": v(-67.3, 202.79) * mm});
            skLineSegment(sketch, "E2466", {"start": v(-67.3, 202.79) * mm, "end": v(-67.94, 203.22) * mm});
            skLineSegment(sketch, "E2467", {"start": v(-67.94, 203.22) * mm, "end": v(-68.6, 203.6) * mm});
            skLineSegment(sketch, "E2468", {"start": v(-68.6, 203.6) * mm, "end": v(-68.83, 203.74) * mm});
            skLineSegment(sketch, "E2469", {"start": v(-36.35, 167.8) * mm, "end": v(-36.24, 168.04) * mm});
            skLineSegment(sketch, "E2470", {"start": v(-36.24, 168.04) * mm, "end": v(-35.81, 168.73) * mm});
            skLineSegment(sketch, "E2471", {"start": v(-35.81, 168.73) * mm, "end": v(-34.94, 170) * mm});
            skLineSegment(sketch, "E2472", {"start": v(-34.94, 170) * mm, "end": v(-33.83, 171.51) * mm});
            skLineSegment(sketch, "E2473", {"start": v(-33.83, 171.51) * mm, "end": v(-32.59, 173.1) * mm});
            skLineSegment(sketch, "E2474", {"start": v(-32.59, 173.1) * mm, "end": v(-31.33, 174.62) * mm});
            skLineSegment(sketch, "E2475", {"start": v(-31.33, 174.62) * mm, "end": v(-30.17, 175.96) * mm});
            skLineSegment(sketch, "E2476", {"start": v(-30.17, 175.96) * mm, "end": v(-29.2, 176.97) * mm});
            skLineSegment(sketch, "E2477", {"start": v(-29.2, 176.97) * mm, "end": v(-28.73, 177.4) * mm});
            skLineSegment(sketch, "E2478", {"start": v(-28.73, 177.4) * mm, "end": v(-28.55, 177.52) * mm});
            skLineSegment(sketch, "E2479", {"start": v(-28.55, 177.52) * mm, "end": v(-28.48, 177.44) * mm});
            skLineSegment(sketch, "E2480", {"start": v(-28.48, 177.44) * mm, "end": v(-28.36, 177.15) * mm});
            skLineSegment(sketch, "E2481", {"start": v(-28.36, 177.15) * mm, "end": v(-28.42, 176.83) * mm});
            skLineSegment(sketch, "E2482", {"start": v(-28.42, 176.83) * mm, "end": v(-28.6, 176.54) * mm});
            skLineSegment(sketch, "E2483", {"start": v(-28.6, 176.54) * mm, "end": v(-28.74, 176.33) * mm});
            skLineSegment(sketch, "E2484", {"start": v(-28.74, 176.33) * mm, "end": v(-28.77, 176.25) * mm});
            skLineSegment(sketch, "E2485", {"start": v(-28.77, 176.25) * mm, "end": v(-28.9, 175.94) * mm});
            skLineSegment(sketch, "E2486", {"start": v(-28.9, 175.94) * mm, "end": v(-29.52, 174.35) * mm});
            skLineSegment(sketch, "E2487", {"start": v(-29.52, 174.35) * mm, "end": v(-29.94, 172.7) * mm});
            skLineSegment(sketch, "E2488", {"start": v(-29.94, 172.7) * mm, "end": v(-29.98, 172.35) * mm});
            skLineSegment(sketch, "E2489", {"start": v(-29.98, 172.35) * mm, "end": v(-30.05, 171.64) * mm});
            skLineSegment(sketch, "E2490", {"start": v(-30.05, 171.64) * mm, "end": v(-29.68, 169.46) * mm});
            skLineSegment(sketch, "E2491", {"start": v(-29.68, 169.46) * mm, "end": v(-28.29, 167.39) * mm});
            skLineSegment(sketch, "E2492", {"start": v(-28.29, 167.39) * mm, "end": v(-26.03, 166.32) * mm});
            skLineSegment(sketch, "E2493", {"start": v(-26.03, 166.32) * mm, "end": v(-23.82, 166.3) * mm});
            skLineSegment(sketch, "E2494", {"start": v(-23.82, 166.3) * mm, "end": v(-23.13, 166.48) * mm});
            skLineSegment(sketch, "E2495", {"start": v(-23.13, 166.48) * mm, "end": v(-22.88, 166.54) * mm});
            skLineSegment(sketch, "E2496", {"start": v(-22.88, 166.54) * mm, "end": v(-21.68, 167) * mm});
            skLineSegment(sketch, "E2497", {"start": v(-21.68, 167) * mm, "end": v(-20.57, 167.64) * mm});
            skLineSegment(sketch, "E2498", {"start": v(-20.57, 167.64) * mm, "end": v(-20.37, 167.8) * mm});
            skLineSegment(sketch, "E2499", {"start": v(-20.37, 167.8) * mm, "end": v(-19.98, 168.12) * mm});
            skLineSegment(sketch, "E2500", {"start": v(-19.98, 168.12) * mm, "end": v(-18.93, 169.24) * mm});
            skLineSegment(sketch, "E2501", {"start": v(-18.93, 169.24) * mm, "end": v(-18.15, 170.82) * mm});
            skLineSegment(sketch, "E2502", {"start": v(-18.15, 170.82) * mm, "end": v(-18.15, 172.58) * mm});
            skLineSegment(sketch, "E2503", {"start": v(-18.15, 172.58) * mm, "end": v(-18.77, 174.13) * mm});
            skLineSegment(sketch, "E2504", {"start": v(-18.77, 174.13) * mm, "end": v(-19.08, 174.58) * mm});
            skLineSegment(sketch, "E2505", {"start": v(-19.08, 174.58) * mm, "end": v(-19.3, 174.9) * mm});
            skLineSegment(sketch, "E2506", {"start": v(-19.3, 174.9) * mm, "end": v(-21.52, 178.16) * mm});
            skLineSegment(sketch, "E2507", {"start": v(-21.52, 178.16) * mm, "end": v(-21.72, 178.5) * mm});
            skLineSegment(sketch, "E2508", {"start": v(-21.72, 178.5) * mm, "end": v(-22.05, 179.04) * mm});
            skLineSegment(sketch, "E2509", {"start": v(-22.05, 179.04) * mm, "end": v(-22.78, 180.84) * mm});
            skLineSegment(sketch, "E2510", {"start": v(-22.78, 180.84) * mm, "end": v(-23.06, 183.1) * mm});
            skLineSegment(sketch, "E2511", {"start": v(-23.06, 183.1) * mm, "end": v(-22.55, 185.3) * mm});
            skLineSegment(sketch, "E2512", {"start": v(-22.55, 185.3) * mm, "end": v(-21.62, 186.97) * mm});
            skLineSegment(sketch, "E2513", {"start": v(-21.62, 186.97) * mm, "end": v(-21.23, 187.45) * mm});
            skLineSegment(sketch, "E2514", {"start": v(-21.23, 187.45) * mm, "end": v(-20.64, 188.2) * mm});
            skLineSegment(sketch, "E2515", {"start": v(-20.64, 188.2) * mm, "end": v(-18.58, 190.16) * mm});
            skLineSegment(sketch, "E2516", {"start": v(-18.58, 190.16) * mm, "end": v(-15.56, 192.07) * mm});
            skLineSegment(sketch, "E2517", {"start": v(-15.56, 192.07) * mm, "end": v(-12.15, 193.09) * mm});
            skLineSegment(sketch, "E2518", {"start": v(-12.15, 193.09) * mm, "end": v(-9.25, 193.23) * mm});
            skLineSegment(sketch, "E2519", {"start": v(-9.25, 193.23) * mm, "end": v(-8.31, 193.11) * mm});
            skLineSegment(sketch, "E2520", {"start": v(-8.31, 193.11) * mm, "end": v(-7.9, 193.07) * mm});
            skLineSegment(sketch, "E2521", {"start": v(-7.9, 193.07) * mm, "end": v(-5.98, 192.4) * mm});
            skLineSegment(sketch, "E2522", {"start": v(-5.98, 192.4) * mm, "end": v(-4.33, 191.2) * mm});
            skLineSegment(sketch, "E2523", {"start": v(-4.33, 191.2) * mm, "end": v(-4.04, 190.88) * mm});
            skLineSegment(sketch, "E2524", {"start": v(-4.04, 190.88) * mm, "end": v(-3.89, 190.7) * mm});
            skLineSegment(sketch, "E2525", {"start": v(-3.89, 190.7) * mm, "end": v(-3.43, 190.2) * mm});
            skLineSegment(sketch, "E2526", {"start": v(-3.43, 190.2) * mm, "end": v(-2.94, 189.72) * mm});
            skLineSegment(sketch, "E2527", {"start": v(-2.94, 189.72) * mm, "end": v(-2.53, 189.41) * mm});
            skLineSegment(sketch, "E2528", {"start": v(-2.53, 189.41) * mm, "end": v(-2.14, 189.28) * mm});
            skLineSegment(sketch, "E2529", {"start": v(-2.14, 189.28) * mm, "end": v(-1.73, 189.32) * mm});
            skLineSegment(sketch, "E2530", {"start": v(-1.73, 189.32) * mm, "end": v(-1.26, 189.52) * mm});
            skLineSegment(sketch, "E2531", {"start": v(-1.26, 189.52) * mm, "end": v(-0.67, 189.88) * mm});
            skLineSegment(sketch, "E2532", {"start": v(-0.67, 189.88) * mm, "end": v(-0.1, 190.26) * mm});
            skLineSegment(sketch, "E2533", {"start": v(-0.1, 190.26) * mm, "end": v(0.09, 190.4) * mm});
            skLineSegment(sketch, "E2534", {"start": v(0.09, 190.4) * mm, "end": v(0.1, 190.4) * mm});
            skLineSegment(sketch, "E2535", {"start": v(0.1, 190.4) * mm, "end": v(0.42, 190.44) * mm});
            skLineSegment(sketch, "E2536", {"start": v(0.42, 190.44) * mm, "end": v(0.45, 190.44) * mm});
            skLineSegment(sketch, "E2537", {"start": v(0.45, 190.44) * mm, "end": v(0.53, 190.34) * mm});
            skLineSegment(sketch, "E2538", {"start": v(0.53, 190.34) * mm, "end": v(0.51, 189.86) * mm});
            skLineSegment(sketch, "E2539", {"start": v(0.51, 189.86) * mm, "end": v(0.21, 189.48) * mm});
            skLineSegment(sketch, "E2540", {"start": v(0.21, 189.48) * mm, "end": v(0.16, 189.4) * mm});
            skLineSegment(sketch, "E2541", {"start": v(0.16, 189.4) * mm, "end": v(-0.26, 188.84) * mm});
            skLineSegment(sketch, "E2542", {"start": v(-0.26, 188.84) * mm, "end": v(-4.48, 183.22) * mm});
            skLineSegment(sketch, "E2543", {"start": v(-4.48, 183.22) * mm, "end": v(-4.91, 182.66) * mm});
            skLineSegment(sketch, "E2544", {"start": v(-4.91, 182.66) * mm, "end": v(-4.97, 182.58) * mm});
            skLineSegment(sketch, "E2545", {"start": v(-4.97, 182.58) * mm, "end": v(-5.14, 182.31) * mm});
            skLineSegment(sketch, "E2546", {"start": v(-5.14, 182.31) * mm, "end": v(-5.39, 181.95) * mm});
            skLineSegment(sketch, "E2547", {"start": v(-5.39, 181.95) * mm, "end": v(-5.7, 181.72) * mm});
            skLineSegment(sketch, "E2548", {"start": v(-5.7, 181.72) * mm, "end": v(-6, 181.72) * mm});
            skLineSegment(sketch, "E2549", {"start": v(-6, 181.72) * mm, "end": v(-6.09, 181.76) * mm});
            skLineSegment(sketch, "E2550", {"start": v(-6.09, 181.76) * mm, "end": v(-6.18, 181.82) * mm});
            skLineSegment(sketch, "E2551", {"start": v(-6.18, 181.82) * mm, "end": v(-6.39, 182.08) * mm});
            skLineSegment(sketch, "E2552", {"start": v(-6.39, 182.08) * mm, "end": v(-6.33, 182.44) * mm});
            skLineSegment(sketch, "E2553", {"start": v(-6.33, 182.44) * mm, "end": v(-6.11, 182.81) * mm});
            skLineSegment(sketch, "E2554", {"start": v(-6.11, 182.81) * mm, "end": v(-5.94, 183.06) * mm});
            skLineSegment(sketch, "E2555", {"start": v(-5.94, 183.06) * mm, "end": v(-5.9, 183.15) * mm});
            skLineSegment(sketch, "E2556", {"start": v(-5.9, 183.15) * mm, "end": v(-5.77, 183.45) * mm});
            skLineSegment(sketch, "E2557", {"start": v(-5.77, 183.45) * mm, "end": v(-5.25, 185) * mm});
            skLineSegment(sketch, "E2558", {"start": v(-5.25, 185) * mm, "end": v(-5.03, 186.6) * mm});
            skLineSegment(sketch, "E2559", {"start": v(-5.03, 186.6) * mm, "end": v(-5.03, 186.92) * mm});
            skLineSegment(sketch, "E2560", {"start": v(-5.03, 186.92) * mm, "end": v(-5.05, 187.4) * mm});
            skLineSegment(sketch, "E2561", {"start": v(-5.05, 187.4) * mm, "end": v(-5.39, 188.78) * mm});
            skLineSegment(sketch, "E2562", {"start": v(-5.39, 188.78) * mm, "end": v(-6.3, 190.2) * mm});
            skLineSegment(sketch, "E2563", {"start": v(-6.3, 190.2) * mm, "end": v(-7.7, 191.12) * mm});
            skLineSegment(sketch, "E2564", {"start": v(-7.7, 191.12) * mm, "end": v(-9.1, 191.48) * mm});
            skLineSegment(sketch, "E2565", {"start": v(-9.1, 191.48) * mm, "end": v(-9.56, 191.5) * mm});
            skLineSegment(sketch, "E2566", {"start": v(-9.56, 191.5) * mm, "end": v(-9.9, 191.5) * mm});
            skLineSegment(sketch, "E2567", {"start": v(-9.9, 191.5) * mm, "end": v(-11.5, 191.26) * mm});
            skLineSegment(sketch, "E2568", {"start": v(-11.5, 191.26) * mm, "end": v(-12.98, 190.64) * mm});
            skLineSegment(sketch, "E2569", {"start": v(-12.98, 190.64) * mm, "end": v(-13.27, 190.47) * mm});
            skLineSegment(sketch, "E2570", {"start": v(-13.27, 190.47) * mm, "end": v(-13.7, 190.2) * mm});
            skLineSegment(sketch, "E2571", {"start": v(-13.7, 190.2) * mm, "end": v(-14.86, 189.16) * mm});
            skLineSegment(sketch, "E2572", {"start": v(-14.86, 189.16) * mm, "end": v(-15.65, 187.64) * mm});
            skLineSegment(sketch, "E2573", {"start": v(-15.65, 187.64) * mm, "end": v(-15.62, 185.94) * mm});
            skLineSegment(sketch, "E2574", {"start": v(-15.62, 185.94) * mm, "end": v(-15.06, 184.49) * mm});
            skLineSegment(sketch, "E2575", {"start": v(-15.06, 184.49) * mm, "end": v(-14.78, 184.06) * mm});
            skLineSegment(sketch, "E2576", {"start": v(-14.78, 184.06) * mm, "end": v(-14.57, 183.72) * mm});
            skLineSegment(sketch, "E2577", {"start": v(-14.57, 183.72) * mm, "end": v(-12.32, 180.5) * mm});
            skLineSegment(sketch, "E2578", {"start": v(-12.32, 180.5) * mm, "end": v(-12.1, 180.16) * mm});
            skLineSegment(sketch, "E2579", {"start": v(-12.1, 180.16) * mm, "end": v(-11.7, 179.54) * mm});
            skLineSegment(sketch, "E2580", {"start": v(-11.7, 179.54) * mm, "end": v(-10.8, 177.5) * mm});
            skLineSegment(sketch, "E2581", {"start": v(-10.8, 177.5) * mm, "end": v(-10.44, 175.02) * mm});
            skLineSegment(sketch, "E2582", {"start": v(-10.44, 175.02) * mm, "end": v(-11.07, 172.62) * mm});
            skLineSegment(sketch, "E2583", {"start": v(-11.07, 172.62) * mm, "end": v(-12.23, 170.75) * mm});
            skLineSegment(sketch, "E2584", {"start": v(-12.23, 170.75) * mm, "end": v(-12.71, 170.21) * mm});
            skLineSegment(sketch, "E2585", {"start": v(-12.71, 170.21) * mm, "end": v(-13.4, 169.43) * mm});
            skLineSegment(sketch, "E2586", {"start": v(-13.4, 169.43) * mm, "end": v(-15.81, 167.37) * mm});
            skLineSegment(sketch, "E2587", {"start": v(-15.81, 167.37) * mm, "end": v(-19.28, 165.5) * mm});
            skLineSegment(sketch, "E2588", {"start": v(-19.28, 165.5) * mm, "end": v(-23.14, 164.65) * mm});
            skLineSegment(sketch, "E2589", {"start": v(-23.14, 164.65) * mm, "end": v(-26.38, 164.73) * mm});
            skLineSegment(sketch, "E2590", {"start": v(-26.38, 164.73) * mm, "end": v(-27.42, 164.92) * mm});
            skLineSegment(sketch, "E2591", {"start": v(-27.42, 164.92) * mm, "end": v(-27.79, 165) * mm});
            skLineSegment(sketch, "E2592", {"start": v(-27.79, 165) * mm, "end": v(-29.3, 165.63) * mm});
            skLineSegment(sketch, "E2593", {"start": v(-29.3, 165.63) * mm, "end": v(-30.58, 166.6) * mm});
            skLineSegment(sketch, "E2594", {"start": v(-30.58, 166.6) * mm, "end": v(-30.82, 166.84) * mm});
            skLineSegment(sketch, "E2595", {"start": v(-30.82, 166.84) * mm, "end": v(-31, 167.01) * mm});
            skLineSegment(sketch, "E2596", {"start": v(-31, 167.01) * mm, "end": v(-31.53, 167.52) * mm});
            skLineSegment(sketch, "E2597", {"start": v(-31.53, 167.52) * mm, "end": v(-32.1, 168.02) * mm});
            skLineSegment(sketch, "E2598", {"start": v(-32.1, 168.02) * mm, "end": v(-32.57, 168.35) * mm});
            skLineSegment(sketch, "E2599", {"start": v(-32.57, 168.35) * mm, "end": v(-33.02, 168.51) * mm});
            skLineSegment(sketch, "E2600", {"start": v(-33.02, 168.51) * mm, "end": v(-33.49, 168.53) * mm});
            skLineSegment(sketch, "E2601", {"start": v(-33.49, 168.53) * mm, "end": v(-34.04, 168.4) * mm});
            skLineSegment(sketch, "E2602", {"start": v(-34.04, 168.4) * mm, "end": v(-34.72, 168.15) * mm});
            skLineSegment(sketch, "E2603", {"start": v(-34.72, 168.15) * mm, "end": v(-35.38, 167.87) * mm});
            skLineSegment(sketch, "E2604", {"start": v(-35.38, 167.87) * mm, "end": v(-35.6, 167.77) * mm});
            skLineSegment(sketch, "E2605", {"start": v(-35.6, 167.77) * mm, "end": v(-35.66, 167.74) * mm});
            skLineSegment(sketch, "E2606", {"start": v(-35.66, 167.74) * mm, "end": v(-35.98, 167.67) * mm});
            skLineSegment(sketch, "E2607", {"start": v(-35.98, 167.67) * mm, "end": v(-36.28, 167.75) * mm});
            skLineSegment(sketch, "E2608", {"start": v(-36.28, 167.75) * mm, "end": v(-36.35, 167.8) * mm});
            skLineSegment(sketch, "E2609", {"start": v(-40.65, 178.52) * mm, "end": v(-40.54, 178.72) * mm});
            skLineSegment(sketch, "E2610", {"start": v(-40.54, 178.72) * mm, "end": v(-39.47, 180.82) * mm});
            skLineSegment(sketch, "E2611", {"start": v(-39.47, 180.82) * mm, "end": v(-39.37, 181.03) * mm});
            skLineSegment(sketch, "E2612", {"start": v(-39.37, 181.03) * mm, "end": v(-39.29, 181.2) * mm});
            skLineSegment(sketch, "E2613", {"start": v(-39.29, 181.2) * mm, "end": v(-39, 182.1) * mm});
            skLineSegment(sketch, "E2614", {"start": v(-39, 182.1) * mm, "end": v(-38.89, 183.03) * mm});
            skLineSegment(sketch, "E2615", {"start": v(-38.89, 183.03) * mm, "end": v(-38.9, 183.22) * mm});
            skLineSegment(sketch, "E2616", {"start": v(-38.9, 183.22) * mm, "end": v(-38.9, 183.4) * mm});
            skLineSegment(sketch, "E2617", {"start": v(-38.9, 183.4) * mm, "end": v(-39.07, 183.91) * mm});
            skLineSegment(sketch, "E2618", {"start": v(-39.07, 183.91) * mm, "end": v(-39.44, 184.42) * mm});
            skLineSegment(sketch, "E2619", {"start": v(-39.44, 184.42) * mm, "end": v(-39.97, 184.8) * mm});
            skLineSegment(sketch, "E2620", {"start": v(-39.97, 184.8) * mm, "end": v(-40.42, 185.02) * mm});
            skLineSegment(sketch, "E2621", {"start": v(-40.42, 185.02) * mm, "end": v(-40.57, 185.1) * mm});
            skLineSegment(sketch, "E2622", {"start": v(-40.57, 185.1) * mm, "end": v(-40.7, 185.14) * mm});
            skLineSegment(sketch, "E2623", {"start": v(-40.7, 185.14) * mm, "end": v(-41.1, 185.18) * mm});
            skLineSegment(sketch, "E2624", {"start": v(-41.1, 185.18) * mm, "end": v(-41.47, 185) * mm});
            skLineSegment(sketch, "E2625", {"start": v(-41.47, 185) * mm, "end": v(-41.75, 184.65) * mm});
            skLineSegment(sketch, "E2626", {"start": v(-41.75, 184.65) * mm, "end": v(-41.94, 184.37) * mm});
            skLineSegment(sketch, "E2627", {"start": v(-41.94, 184.37) * mm, "end": v(-42.01, 184.28) * mm});
            skLineSegment(sketch, "E2628", {"start": v(-42.01, 184.28) * mm, "end": v(-42.48, 183.71) * mm});
            skLineSegment(sketch, "E2629", {"start": v(-42.48, 183.71) * mm, "end": v(-47.1, 177.97) * mm});
            skLineSegment(sketch, "E2630", {"start": v(-47.1, 177.97) * mm, "end": v(-47.56, 177.39) * mm});
            skLineSegment(sketch, "E2631", {"start": v(-47.56, 177.39) * mm, "end": v(-47.75, 177.14) * mm});
            skLineSegment(sketch, "E2632", {"start": v(-47.75, 177.14) * mm, "end": v(-48.26, 176.33) * mm});
            skLineSegment(sketch, "E2633", {"start": v(-48.26, 176.33) * mm, "end": v(-48.35, 175.62) * mm});
            skLineSegment(sketch, "E2634", {"start": v(-48.35, 175.62) * mm, "end": v(-47.81, 175.07) * mm});
            skLineSegment(sketch, "E2635", {"start": v(-47.81, 175.07) * mm, "end": v(-46.92, 174.65) * mm});
            skLineSegment(sketch, "E2636", {"start": v(-46.92, 174.65) * mm, "end": v(-46.61, 174.54) * mm});
            skLineSegment(sketch, "E2637", {"start": v(-46.61, 174.54) * mm, "end": v(-45.9, 174.27) * mm});
            skLineSegment(sketch, "E2638", {"start": v(-45.9, 174.27) * mm, "end": v(-43.66, 173.83) * mm});
            skLineSegment(sketch, "E2639", {"start": v(-43.66, 173.83) * mm, "end": v(-40.84, 173.92) * mm});
            skLineSegment(sketch, "E2640", {"start": v(-40.84, 173.92) * mm, "end": v(-38.11, 174.7) * mm});
            skLineSegment(sketch, "E2641", {"start": v(-38.11, 174.7) * mm, "end": v(-36.1, 175.71) * mm});
            skLineSegment(sketch, "E2642", {"start": v(-36.1, 175.71) * mm, "end": v(-35.47, 176.12) * mm});
            skLineSegment(sketch, "E2643", {"start": v(-35.47, 176.12) * mm, "end": v(-35.3, 176.23) * mm});
            skLineSegment(sketch, "E2644", {"start": v(-35.3, 176.23) * mm, "end": v(-34.82, 176.6) * mm});
            skLineSegment(sketch, "E2645", {"start": v(-34.82, 176.6) * mm, "end": v(-34.14, 177.11) * mm});
            skLineSegment(sketch, "E2646", {"start": v(-34.14, 177.11) * mm, "end": v(-33.34, 177.59) * mm});
            skLineSegment(sketch, "E2647", {"start": v(-33.34, 177.59) * mm, "end": v(-32.58, 177.89) * mm});
            skLineSegment(sketch, "E2648", {"start": v(-32.58, 177.89) * mm, "end": v(-32.32, 177.95) * mm});
            skLineSegment(sketch, "E2649", {"start": v(-32.32, 177.95) * mm, "end": v(-32.46, 177.78) * mm});
            skLineSegment(sketch, "E2650", {"start": v(-32.46, 177.78) * mm, "end": v(-33, 177.12) * mm});
            skLineSegment(sketch, "E2651", {"start": v(-33, 177.12) * mm, "end": v(-33.41, 176.62) * mm});
            skLineSegment(sketch, "E2652", {"start": v(-33.41, 176.62) * mm, "end": v(-33.5, 176.53) * mm});
            skLineSegment(sketch, "E2653", {"start": v(-33.5, 176.53) * mm, "end": v(-33.76, 176.26) * mm});
            skLineSegment(sketch, "E2654", {"start": v(-33.76, 176.26) * mm, "end": v(-35.11, 174.93) * mm});
            skLineSegment(sketch, "E2655", {"start": v(-35.11, 174.93) * mm, "end": v(-36.41, 173.57) * mm});
            skLineSegment(sketch, "E2656", {"start": v(-36.41, 173.57) * mm, "end": v(-36.65, 173.28) * mm});
            skLineSegment(sketch, "E2657", {"start": v(-36.65, 173.28) * mm, "end": v(-36.93, 172.93) * mm});
            skLineSegment(sketch, "E2658", {"start": v(-36.93, 172.93) * mm, "end": v(-37.9, 171.96) * mm});
            skLineSegment(sketch, "E2659", {"start": v(-37.9, 171.96) * mm, "end": v(-39.27, 171.16) * mm});
            skLineSegment(sketch, "E2660", {"start": v(-39.27, 171.16) * mm, "end": v(-40.85, 170.96) * mm});
            skLineSegment(sketch, "E2661", {"start": v(-40.85, 170.96) * mm, "end": v(-42.3, 171.28) * mm});
            skLineSegment(sketch, "E2662", {"start": v(-42.3, 171.28) * mm, "end": v(-42.75, 171.47) * mm});
            skLineSegment(sketch, "E2663", {"start": v(-42.75, 171.47) * mm, "end": v(-43.19, 171.65) * mm});
            skLineSegment(sketch, "E2664", {"start": v(-43.19, 171.65) * mm, "end": v(-45.45, 172.51) * mm});
            skLineSegment(sketch, "E2665", {"start": v(-45.45, 172.51) * mm, "end": v(-47.8, 173.25) * mm});
            skLineSegment(sketch, "E2666", {"start": v(-47.8, 173.25) * mm, "end": v(-48.27, 173.36) * mm});
            skLineSegment(sketch, "E2667", {"start": v(-48.27, 173.36) * mm, "end": v(-48.75, 173.48) * mm});
            skLineSegment(sketch, "E2668", {"start": v(-48.75, 173.48) * mm, "end": v(-53.48, 175) * mm});
            skLineSegment(sketch, "E2669", {"start": v(-53.48, 175) * mm, "end": v(-53.95, 175.14) * mm});
            skLineSegment(sketch, "E2670", {"start": v(-53.95, 175.14) * mm, "end": v(-54.3, 175.24) * mm});
            skLineSegment(sketch, "E2671", {"start": v(-54.3, 175.24) * mm, "end": v(-57.7, 176.2) * mm});
            skLineSegment(sketch, "E2672", {"start": v(-57.7, 176.2) * mm, "end": v(-58.05, 176.27) * mm});
            skLineSegment(sketch, "E2673", {"start": v(-58.05, 176.27) * mm, "end": v(-58.13, 176.3) * mm});
            skLineSegment(sketch, "E2674", {"start": v(-58.13, 176.3) * mm, "end": v(-58.37, 176.36) * mm});
            skLineSegment(sketch, "E2675", {"start": v(-58.37, 176.36) * mm, "end": v(-58.6, 176.48) * mm});
            skLineSegment(sketch, "E2676", {"start": v(-58.6, 176.48) * mm, "end": v(-58.73, 176.68) * mm});
            skLineSegment(sketch, "E2677", {"start": v(-58.73, 176.68) * mm, "end": v(-58.71, 176.93) * mm});
            skLineSegment(sketch, "E2678", {"start": v(-58.71, 176.93) * mm, "end": v(-58.69, 177.01) * mm});
            skLineSegment(sketch, "E2679", {"start": v(-58.69, 177.01) * mm, "end": v(-58.65, 177.11) * mm});
            skLineSegment(sketch, "E2680", {"start": v(-58.65, 177.11) * mm, "end": v(-58.34, 177.35) * mm});
            skLineSegment(sketch, "E2681", {"start": v(-58.34, 177.35) * mm, "end": v(-57.92, 177.3) * mm});
            skLineSegment(sketch, "E2682", {"start": v(-57.92, 177.3) * mm, "end": v(-57.84, 177.27) * mm});
            skLineSegment(sketch, "E2683", {"start": v(-57.84, 177.27) * mm, "end": v(-57.52, 177.16) * mm});
            skLineSegment(sketch, "E2684", {"start": v(-57.52, 177.16) * mm, "end": v(-56.49, 177.03) * mm});
            skLineSegment(sketch, "E2685", {"start": v(-56.49, 177.03) * mm, "end": v(-55.31, 177.28) * mm});
            skLineSegment(sketch, "E2686", {"start": v(-55.31, 177.28) * mm, "end": v(-54.28, 177.93) * mm});
            skLineSegment(sketch, "E2687", {"start": v(-54.28, 177.93) * mm, "end": v(-53.57, 178.63) * mm});
            skLineSegment(sketch, "E2688", {"start": v(-53.57, 178.63) * mm, "end": v(-53.36, 178.89) * mm});
            skLineSegment(sketch, "E2689", {"start": v(-53.36, 178.89) * mm, "end": v(-52.27, 180.23) * mm});
            skLineSegment(sketch, "E2690", {"start": v(-52.27, 180.23) * mm, "end": v(-41.34, 193.67) * mm});
            skLineSegment(sketch, "E2691", {"start": v(-41.34, 193.67) * mm, "end": v(-40.25, 195.02) * mm});
            skLineSegment(sketch, "E2692", {"start": v(-40.25, 195.02) * mm, "end": v(-40.2, 195.08) * mm});
            skLineSegment(sketch, "E2693", {"start": v(-40.2, 195.08) * mm, "end": v(-39.72, 195.79) * mm});
            skLineSegment(sketch, "E2694", {"start": v(-39.72, 195.79) * mm, "end": v(-39.68, 195.86) * mm});
            skLineSegment(sketch, "E2695", {"start": v(-39.68, 195.86) * mm, "end": v(-39.56, 196.06) * mm});
            skLineSegment(sketch, "E2696", {"start": v(-39.56, 196.06) * mm, "end": v(-39.2, 196.66) * mm});
            skLineSegment(sketch, "E2697", {"start": v(-39.2, 196.66) * mm, "end": v(-38.88, 197.29) * mm});
            skLineSegment(sketch, "E2698", {"start": v(-38.88, 197.29) * mm, "end": v(-38.7, 197.77) * mm});
            skLineSegment(sketch, "E2699", {"start": v(-38.7, 197.77) * mm, "end": v(-38.7, 198.18) * mm});
            skLineSegment(sketch, "E2700", {"start": v(-38.7, 198.18) * mm, "end": v(-38.86, 198.54) * mm});
            skLineSegment(sketch, "E2701", {"start": v(-38.86, 198.54) * mm, "end": v(-39.2, 198.9) * mm});
            skLineSegment(sketch, "E2702", {"start": v(-39.2, 198.9) * mm, "end": v(-39.73, 199.33) * mm});
            skLineSegment(sketch, "E2703", {"start": v(-39.73, 199.33) * mm, "end": v(-40.28, 199.72) * mm});
            skLineSegment(sketch, "E2704", {"start": v(-40.28, 199.72) * mm, "end": v(-40.46, 199.84) * mm});
            skLineSegment(sketch, "E2705", {"start": v(-40.46, 199.84) * mm, "end": v(-40.35, 199.99) * mm});
            skLineSegment(sketch, "E2706", {"start": v(-40.35, 199.99) * mm, "end": v(-39.75, 200.24) * mm});
            skLineSegment(sketch, "E2707", {"start": v(-39.75, 200.24) * mm, "end": v(-39.1, 200.1) * mm});
            skLineSegment(sketch, "E2708", {"start": v(-39.1, 200.1) * mm, "end": v(-38.98, 200.07) * mm});
            skLineSegment(sketch, "E2709", {"start": v(-38.98, 200.07) * mm, "end": v(-37.52, 199.61) * mm});
            skLineSegment(sketch, "E2710", {"start": v(-37.52, 199.61) * mm, "end": v(-23, 194.99) * mm});
            skLineSegment(sketch, "E2711", {"start": v(-23, 194.99) * mm, "end": v(-21.55, 194.52) * mm});
            skLineSegment(sketch, "E2712", {"start": v(-21.55, 194.52) * mm, "end": v(-21.52, 194.52) * mm});
            skLineSegment(sketch, "E2713", {"start": v(-21.52, 194.52) * mm, "end": v(-21.37, 194.4) * mm});
            skLineSegment(sketch, "E2714", {"start": v(-21.37, 194.4) * mm, "end": v(-21.16, 194.16) * mm});
            skLineSegment(sketch, "E2715", {"start": v(-21.16, 194.16) * mm, "end": v(-21.1, 194.1) * mm});
            skLineSegment(sketch, "E2716", {"start": v(-21.1, 194.1) * mm, "end": v(-21.55, 193.54) * mm});
            skLineSegment(sketch, "E2717", {"start": v(-21.55, 193.54) * mm, "end": v(-26.11, 187.92) * mm});
            skLineSegment(sketch, "E2718", {"start": v(-26.11, 187.92) * mm, "end": v(-26.57, 187.36) * mm});
            skLineSegment(sketch, "E2719", {"start": v(-26.57, 187.36) * mm, "end": v(-26.67, 187.43) * mm});
            skLineSegment(sketch, "E2720", {"start": v(-26.67, 187.43) * mm, "end": v(-26.92, 187.69) * mm});
            skLineSegment(sketch, "E2721", {"start": v(-26.92, 187.69) * mm, "end": v(-26.98, 187.99) * mm});
            skLineSegment(sketch, "E2722", {"start": v(-26.98, 187.99) * mm, "end": v(-26.89, 188.25) * mm});
            skLineSegment(sketch, "E2723", {"start": v(-26.89, 188.25) * mm, "end": v(-26.78, 188.44) * mm});
            skLineSegment(sketch, "E2724", {"start": v(-26.78, 188.44) * mm, "end": v(-26.75, 188.5) * mm});
            skLineSegment(sketch, "E2725", {"start": v(-26.75, 188.5) * mm, "end": v(-26.69, 188.66) * mm});
            skLineSegment(sketch, "E2726", {"start": v(-26.69, 188.66) * mm, "end": v(-25.98, 190.23) * mm});
            skLineSegment(sketch, "E2727", {"start": v(-25.98, 190.23) * mm, "end": v(-25.92, 190.38) * mm});
            skLineSegment(sketch, "E2728", {"start": v(-25.92, 190.38) * mm, "end": v(-25.82, 190.7) * mm});
            skLineSegment(sketch, "E2729", {"start": v(-25.82, 190.7) * mm, "end": v(-25.7, 191.68) * mm});
            skLineSegment(sketch, "E2730", {"start": v(-25.7, 191.68) * mm, "end": v(-25.9, 192.8) * mm});
            skLineSegment(sketch, "E2731", {"start": v(-25.9, 192.8) * mm, "end": v(-26.53, 193.75) * mm});
            skLineSegment(sketch, "E2732", {"start": v(-26.53, 193.75) * mm, "end": v(-27.3, 194.37) * mm});
            skLineSegment(sketch, "E2733", {"start": v(-27.3, 194.37) * mm, "end": v(-27.59, 194.53) * mm});
            skLineSegment(sketch, "E2734", {"start": v(-27.59, 194.53) * mm, "end": v(-27.62, 194.55) * mm});
            skLineSegment(sketch, "E2735", {"start": v(-27.62, 194.55) * mm, "end": v(-27.92, 194.7) * mm});
            skLineSegment(sketch, "E2736", {"start": v(-27.92, 194.7) * mm, "end": v(-27.95, 194.7) * mm});
            skLineSegment(sketch, "E2737", {"start": v(-27.95, 194.7) * mm, "end": v(-28.54, 194.99) * mm});
            skLineSegment(sketch, "E2738", {"start": v(-28.54, 194.99) * mm, "end": v(-30.35, 195.76) * mm});
            skLineSegment(sketch, "E2739", {"start": v(-30.35, 195.76) * mm, "end": v(-31.87, 195.94) * mm});
            skLineSegment(sketch, "E2740", {"start": v(-31.87, 195.94) * mm, "end": v(-33.16, 195.12) * mm});
            skLineSegment(sketch, "E2741", {"start": v(-33.16, 195.12) * mm, "end": v(-34.44, 193.66) * mm});
            skLineSegment(sketch, "E2742", {"start": v(-34.44, 193.66) * mm, "end": v(-34.84, 193.15) * mm});
            skLineSegment(sketch, "E2743", {"start": v(-34.84, 193.15) * mm, "end": v(-35.26, 192.64) * mm});
            skLineSegment(sketch, "E2744", {"start": v(-35.26, 192.64) * mm, "end": v(-39.57, 187.29) * mm});
            skLineSegment(sketch, "E2745", {"start": v(-39.57, 187.29) * mm, "end": v(-40.04, 186.71) * mm});
            skLineSegment(sketch, "E2746", {"start": v(-40.04, 186.71) * mm, "end": v(-39.34, 186.5) * mm});
            skLineSegment(sketch, "E2747", {"start": v(-39.34, 186.5) * mm, "end": v(-37.07, 186.5) * mm});
            skLineSegment(sketch, "E2748", {"start": v(-37.07, 186.5) * mm, "end": v(-34.68, 187.42) * mm});
            skLineSegment(sketch, "E2749", {"start": v(-34.68, 187.42) * mm, "end": v(-32.58, 188.96) * mm});
            skLineSegment(sketch, "E2750", {"start": v(-32.58, 188.96) * mm, "end": v(-31.05, 190.17) * mm});
            skLineSegment(sketch, "E2751", {"start": v(-31.05, 190.17) * mm, "end": v(-30.51, 190.53) * mm});
            skLineSegment(sketch, "E2752", {"start": v(-30.51, 190.53) * mm, "end": v(-31.27, 189.44) * mm});
            skLineSegment(sketch, "E2753", {"start": v(-31.27, 189.44) * mm, "end": v(-35.25, 184.22) * mm});
            skLineSegment(sketch, "E2754", {"start": v(-35.25, 184.22) * mm, "end": v(-39.39, 179.15) * mm});
            skLineSegment(sketch, "E2755", {"start": v(-39.39, 179.15) * mm, "end": v(-40.22, 178.15) * mm});
            skLineSegment(sketch, "E2756", {"start": v(-40.22, 178.15) * mm, "end": v(-40.26, 178.18) * mm});
            skLineSegment(sketch, "E2757", {"start": v(-40.26, 178.18) * mm, "end": v(-40.61, 178.48) * mm});
            skLineSegment(sketch, "E2758", {"start": v(-40.61, 178.48) * mm, "end": v(-40.65, 178.52) * mm});
            skLineSegment(sketch, "E2759", {"start": v(6.46, 185.01) * mm, "end": v(6.46, 185.21) * mm});
            skLineSegment(sketch, "E2760", {"start": v(6.46, 185.21) * mm, "end": v(6.35, 185.82) * mm});
            skLineSegment(sketch, "E2761", {"start": v(6.35, 185.82) * mm, "end": v(6.06, 186.4) * mm});
            skLineSegment(sketch, "E2762", {"start": v(6.06, 186.4) * mm, "end": v(5.62, 186.82) * mm});
            skLineSegment(sketch, "E2763", {"start": v(5.62, 186.82) * mm, "end": v(5.23, 187.09) * mm});
            skLineSegment(sketch, "E2764", {"start": v(5.23, 187.09) * mm, "end": v(5.09, 187.16) * mm});
            skLineSegment(sketch, "E2765", {"start": v(5.09, 187.16) * mm, "end": v(5.03, 187.2) * mm});
            skLineSegment(sketch, "E2766", {"start": v(5.03, 187.2) * mm, "end": v(4.86, 187.28) * mm});
            skLineSegment(sketch, "E2767", {"start": v(4.86, 187.28) * mm, "end": v(4.65, 187.41) * mm});
            skLineSegment(sketch, "E2768", {"start": v(4.65, 187.41) * mm, "end": v(4.52, 187.6) * mm});
            skLineSegment(sketch, "E2769", {"start": v(4.52, 187.6) * mm, "end": v(4.53, 187.82) * mm});
            skLineSegment(sketch, "E2770", {"start": v(4.53, 187.82) * mm, "end": v(4.55, 187.88) * mm});
            skLineSegment(sketch, "E2771", {"start": v(4.55, 187.88) * mm, "end": v(4.6, 188) * mm});
            skLineSegment(sketch, "E2772", {"start": v(4.6, 188) * mm, "end": v(5.01, 188.25) * mm});
            skLineSegment(sketch, "E2773", {"start": v(5.01, 188.25) * mm, "end": v(5.5, 188.15) * mm});
            skLineSegment(sketch, "E2774", {"start": v(5.5, 188.15) * mm, "end": v(5.6, 188.1) * mm});
            skLineSegment(sketch, "E2775", {"start": v(5.6, 188.1) * mm, "end": v(6.25, 187.79) * mm});
            skLineSegment(sketch, "E2776", {"start": v(6.25, 187.79) * mm, "end": v(12.7, 184.63) * mm});
            skLineSegment(sketch, "E2777", {"start": v(12.7, 184.63) * mm, "end": v(13.35, 184.3) * mm});
            skLineSegment(sketch, "E2778", {"start": v(13.35, 184.3) * mm, "end": v(13.68, 184.14) * mm});
            skLineSegment(sketch, "E2779", {"start": v(13.68, 184.14) * mm, "end": v(17.06, 182.47) * mm});
            skLineSegment(sketch, "E2780", {"start": v(17.06, 182.47) * mm, "end": v(17.4, 182.3) * mm});
            skLineSegment(sketch, "E2781", {"start": v(17.4, 182.3) * mm, "end": v(17.46, 182.27) * mm});
            skLineSegment(sketch, "E2782", {"start": v(17.46, 182.27) * mm, "end": v(17.66, 182.17) * mm});
            skLineSegment(sketch, "E2783", {"start": v(17.66, 182.17) * mm, "end": v(17.88, 182) * mm});
            skLineSegment(sketch, "E2784", {"start": v(17.88, 182) * mm, "end": v(17.98, 181.75) * mm});
            skLineSegment(sketch, "E2785", {"start": v(17.98, 181.75) * mm, "end": v(17.9, 181.48) * mm});
            skLineSegment(sketch, "E2786", {"start": v(17.9, 181.48) * mm, "end": v(17.86, 181.4) * mm});
            skLineSegment(sketch, "E2787", {"start": v(17.86, 181.4) * mm, "end": v(17.78, 181.28) * mm});
            skLineSegment(sketch, "E2788", {"start": v(17.78, 181.28) * mm, "end": v(17.37, 180.98) * mm});
            skLineSegment(sketch, "E2789", {"start": v(17.37, 180.98) * mm, "end": v(16.84, 181.05) * mm});
            skLineSegment(sketch, "E2790", {"start": v(16.84, 181.05) * mm, "end": v(16.7, 181.1) * mm});
            skLineSegment(sketch, "E2791", {"start": v(16.7, 181.1) * mm, "end": v(16.32, 181.3) * mm});
            skLineSegment(sketch, "E2792", {"start": v(16.32, 181.3) * mm, "end": v(15.14, 181.74) * mm});
            skLineSegment(sketch, "E2793", {"start": v(15.14, 181.74) * mm, "end": v(13.98, 181.85) * mm});
            skLineSegment(sketch, "E2794", {"start": v(13.98, 181.85) * mm, "end": v(12.94, 181.37) * mm});
            skLineSegment(sketch, "E2795", {"start": v(12.94, 181.37) * mm, "end": v(12.03, 180.53) * mm});
            skLineSegment(sketch, "E2796", {"start": v(12.03, 180.53) * mm, "end": v(11.75, 180.23) * mm});
            skLineSegment(sketch, "E2797", {"start": v(11.75, 180.23) * mm, "end": v(10.63, 179) * mm});
            skLineSegment(sketch, "E2798", {"start": v(10.63, 179) * mm, "end": v(-0.45, 166.65) * mm});
            skLineSegment(sketch, "E2799", {"start": v(-0.45, 166.65) * mm, "end": v(-1.56, 165.42) * mm});
            skLineSegment(sketch, "E2800", {"start": v(-1.56, 165.42) * mm, "end": v(-2, 164.92) * mm});
            skLineSegment(sketch, "E2801", {"start": v(-2, 164.92) * mm, "end": v(-6.44, 159.93) * mm});
            skLineSegment(sketch, "E2802", {"start": v(-6.44, 159.93) * mm, "end": v(-6.87, 159.41) * mm});
            skLineSegment(sketch, "E2803", {"start": v(-6.87, 159.41) * mm, "end": v(-7.1, 159.14) * mm});
            skLineSegment(sketch, "E2804", {"start": v(-7.1, 159.14) * mm, "end": v(-7.72, 158.26) * mm});
            skLineSegment(sketch, "E2805", {"start": v(-7.72, 158.26) * mm, "end": v(-7.94, 157.4) * mm});
            skLineSegment(sketch, "E2806", {"start": v(-7.94, 157.4) * mm, "end": v(-7.52, 156.6) * mm});
            skLineSegment(sketch, "E2807", {"start": v(-7.52, 156.6) * mm, "end": v(-6.72, 155.87) * mm});
            skLineSegment(sketch, "E2808", {"start": v(-6.72, 155.87) * mm, "end": v(-6.43, 155.64) * mm});
            skLineSegment(sketch, "E2809", {"start": v(-6.43, 155.64) * mm, "end": v(-6.37, 155.6) * mm});
            skLineSegment(sketch, "E2810", {"start": v(-6.37, 155.6) * mm, "end": v(-6.18, 155.46) * mm});
            skLineSegment(sketch, "E2811", {"start": v(-6.18, 155.46) * mm, "end": v(-5.97, 155.25) * mm});
            skLineSegment(sketch, "E2812", {"start": v(-5.97, 155.25) * mm, "end": v(-5.9, 155.01) * mm});
            skLineSegment(sketch, "E2813", {"start": v(-5.9, 155.01) * mm, "end": v(-6, 154.77) * mm});
            skLineSegment(sketch, "E2814", {"start": v(-6, 154.77) * mm, "end": v(-6.05, 154.71) * mm});
            skLineSegment(sketch, "E2815", {"start": v(-6.05, 154.71) * mm, "end": v(-6.14, 154.62) * mm});
            skLineSegment(sketch, "E2816", {"start": v(-6.14, 154.62) * mm, "end": v(-6.62, 154.42) * mm});
            skLineSegment(sketch, "E2817", {"start": v(-6.62, 154.42) * mm, "end": v(-7.2, 154.57) * mm});
            skLineSegment(sketch, "E2818", {"start": v(-7.2, 154.57) * mm, "end": v(-7.32, 154.65) * mm});
            skLineSegment(sketch, "E2819", {"start": v(-7.32, 154.65) * mm, "end": v(-8.03, 155.08) * mm});
            skLineSegment(sketch, "E2820", {"start": v(-8.03, 155.08) * mm, "end": v(-11.75, 157.01) * mm});
            skLineSegment(sketch, "E2821", {"start": v(-11.75, 157.01) * mm, "end": v(-15.52, 158.85) * mm});
            skLineSegment(sketch, "E2822", {"start": v(-15.52, 158.85) * mm, "end": v(-16.26, 159.24) * mm});
            skLineSegment(sketch, "E2823", {"start": v(-16.26, 159.24) * mm, "end": v(-16.43, 159.33) * mm});
            skLineSegment(sketch, "E2824", {"start": v(-16.43, 159.33) * mm, "end": v(-17, 159.54) * mm});
            skLineSegment(sketch, "E2825", {"start": v(-17, 159.54) * mm, "end": v(-17.76, 159.78) * mm});
            skLineSegment(sketch, "E2826", {"start": v(-17.76, 159.78) * mm, "end": v(-18.48, 160.1) * mm});
            skLineSegment(sketch, "E2827", {"start": v(-18.48, 160.1) * mm, "end": v(-18.98, 160.5) * mm});
            skLineSegment(sketch, "E2828", {"start": v(-18.98, 160.5) * mm, "end": v(-19.1, 160.65) * mm});
            skLineSegment(sketch, "E2829", {"start": v(-19.1, 160.65) * mm, "end": v(-19.14, 160.7) * mm});
            skLineSegment(sketch, "E2830", {"start": v(-19.14, 160.7) * mm, "end": v(-19.32, 160.96) * mm});
            skLineSegment(sketch, "E2831", {"start": v(-19.32, 160.96) * mm, "end": v(-19.32, 161.27) * mm});
            skLineSegment(sketch, "E2832", {"start": v(-19.32, 161.27) * mm, "end": v(-19.28, 161.34) * mm});
            skLineSegment(sketch, "E2833", {"start": v(-19.28, 161.34) * mm, "end": v(-19.23, 161.4) * mm});
            skLineSegment(sketch, "E2834", {"start": v(-19.23, 161.4) * mm, "end": v(-18.98, 161.6) * mm});
            skLineSegment(sketch, "E2835", {"start": v(-18.98, 161.6) * mm, "end": v(-18.66, 161.61) * mm});
            skLineSegment(sketch, "E2836", {"start": v(-18.66, 161.61) * mm, "end": v(-18.59, 161.58) * mm});
            skLineSegment(sketch, "E2837", {"start": v(-18.59, 161.58) * mm, "end": v(-18.52, 161.56) * mm});
            skLineSegment(sketch, "E2838", {"start": v(-18.52, 161.56) * mm, "end": v(-17.89, 161.3) * mm});
            skLineSegment(sketch, "E2839", {"start": v(-17.89, 161.3) * mm, "end": v(-17.82, 161.27) * mm});
            skLineSegment(sketch, "E2840", {"start": v(-17.82, 161.27) * mm, "end": v(-17.54, 161.16) * mm});
            skLineSegment(sketch, "E2841", {"start": v(-17.54, 161.16) * mm, "end": v(-16.62, 160.95) * mm});
            skLineSegment(sketch, "E2842", {"start": v(-16.62, 160.95) * mm, "end": v(-15.51, 161.02) * mm});
            skLineSegment(sketch, "E2843", {"start": v(-15.51, 161.02) * mm, "end": v(-14.48, 161.46) * mm});
            skLineSegment(sketch, "E2844", {"start": v(-14.48, 161.46) * mm, "end": v(-13.74, 162.02) * mm});
            skLineSegment(sketch, "E2845", {"start": v(-13.74, 162.02) * mm, "end": v(-13.53, 162.24) * mm});
            skLineSegment(sketch, "E2846", {"start": v(-13.53, 162.24) * mm, "end": v(-13.32, 162.47) * mm});
            skLineSegment(sketch, "E2847", {"start": v(-13.32, 162.47) * mm, "end": v(-11.2, 164.7) * mm});
            skLineSegment(sketch, "E2848", {"start": v(-11.2, 164.7) * mm, "end": v(-11, 164.94) * mm});
            skLineSegment(sketch, "E2849", {"start": v(-11, 164.94) * mm, "end": v(-9.67, 166.42) * mm});
            skLineSegment(sketch, "E2850", {"start": v(-9.67, 166.42) * mm, "end": v(3.58, 181.22) * mm});
            skLineSegment(sketch, "E2851", {"start": v(3.58, 181.22) * mm, "end": v(4.9, 182.7) * mm});
            skLineSegment(sketch, "E2852", {"start": v(4.9, 182.7) * mm, "end": v(5.07, 182.9) * mm});
            skLineSegment(sketch, "E2853", {"start": v(5.07, 182.9) * mm, "end": v(5.9, 183.83) * mm});
            skLineSegment(sketch, "E2854", {"start": v(5.9, 183.83) * mm, "end": v(6.43, 184.8) * mm});
            skLineSegment(sketch, "E2855", {"start": v(6.43, 184.8) * mm, "end": v(6.46, 185.01) * mm});
            skLineSegment(sketch, "E2856", {"start": v(-148.26, 108.11) * mm, "end": v(-148.28, 108.43) * mm});
            skLineSegment(sketch, "E2857", {"start": v(-148.28, 108.43) * mm, "end": v(-148.5, 109.37) * mm});
            skLineSegment(sketch, "E2858", {"start": v(-148.5, 109.37) * mm, "end": v(-148.99, 110.4) * mm});
            skLineSegment(sketch, "E2859", {"start": v(-148.99, 110.4) * mm, "end": v(-149.74, 111.2) * mm});
            skLineSegment(sketch, "E2860", {"start": v(-149.74, 111.2) * mm, "end": v(-150.47, 111.68) * mm});
            skLineSegment(sketch, "E2861", {"start": v(-150.47, 111.68) * mm, "end": v(-150.73, 111.8) * mm});
            skLineSegment(sketch, "E2862", {"start": v(-150.73, 111.8) * mm, "end": v(-151.03, 111.93) * mm});
            skLineSegment(sketch, "E2863", {"start": v(-151.03, 111.93) * mm, "end": v(-152.56, 112.47) * mm});
            skLineSegment(sketch, "E2864", {"start": v(-152.56, 112.47) * mm, "end": v(-154.14, 112.84) * mm});
            skLineSegment(sketch, "E2865", {"start": v(-154.14, 112.84) * mm, "end": v(-154.47, 112.9) * mm});
            skLineSegment(sketch, "E2866", {"start": v(-154.47, 112.9) * mm, "end": v(-155.1, 113) * mm});
            skLineSegment(sketch, "E2867", {"start": v(-155.1, 113) * mm, "end": v(-157.08, 112.9) * mm});
            skLineSegment(sketch, "E2868", {"start": v(-157.08, 112.9) * mm, "end": v(-159.14, 112.08) * mm});
            skLineSegment(sketch, "E2869", {"start": v(-159.14, 112.08) * mm, "end": v(-160.82, 110.63) * mm});
            skLineSegment(sketch, "E2870", {"start": v(-160.82, 110.63) * mm, "end": v(-161.9, 109.25) * mm});
            skLineSegment(sketch, "E2871", {"start": v(-161.9, 109.25) * mm, "end": v(-162.23, 108.76) * mm});
            skLineSegment(sketch, "E2872", {"start": v(-162.23, 108.76) * mm, "end": v(-162.35, 108.57) * mm});
            skLineSegment(sketch, "E2873", {"start": v(-162.35, 108.57) * mm, "end": v(-162.44, 107.81) * mm});
            skLineSegment(sketch, "E2874", {"start": v(-162.44, 107.81) * mm, "end": v(-161.87, 107.26) * mm});
            skLineSegment(sketch, "E2875", {"start": v(-161.87, 107.26) * mm, "end": v(-161.66, 107.18) * mm});
            skLineSegment(sketch, "E2876", {"start": v(-161.66, 107.18) * mm, "end": v(-160.82, 106.86) * mm});
            skLineSegment(sketch, "E2877", {"start": v(-160.82, 106.86) * mm, "end": v(-152.37, 103.52) * mm});
            skLineSegment(sketch, "E2878", {"start": v(-152.37, 103.52) * mm, "end": v(-151.53, 103.19) * mm});
            skLineSegment(sketch, "E2879", {"start": v(-151.53, 103.19) * mm, "end": v(-151.4, 103.14) * mm});
            skLineSegment(sketch, "E2880", {"start": v(-151.4, 103.14) * mm, "end": v(-150.83, 103.05) * mm});
            skLineSegment(sketch, "E2881", {"start": v(-150.83, 103.05) * mm, "end": v(-150.34, 103.29) * mm});
            skLineSegment(sketch, "E2882", {"start": v(-150.34, 103.29) * mm, "end": v(-150.25, 103.4) * mm});
            skLineSegment(sketch, "E2883", {"start": v(-150.25, 103.4) * mm, "end": v(-149.99, 103.77) * mm});
            skLineSegment(sketch, "E2884", {"start": v(-149.99, 103.77) * mm, "end": v(-148.92, 105.69) * mm});
            skLineSegment(sketch, "E2885", {"start": v(-148.92, 105.69) * mm, "end": v(-148.3, 107.7) * mm});
            skLineSegment(sketch, "E2886", {"start": v(-148.3, 107.7) * mm, "end": v(-148.26, 108.11) * mm});
            skLineSegment(sketch, "E2887", {"start": v(-126.8, 105.83) * mm, "end": v(-126.89, 105.72) * mm});
            skLineSegment(sketch, "E2888", {"start": v(-126.89, 105.72) * mm, "end": v(-127.27, 105.47) * mm});
            skLineSegment(sketch, "E2889", {"start": v(-127.27, 105.47) * mm, "end": v(-127.8, 105.33) * mm});
            skLineSegment(sketch, "E2890", {"start": v(-127.8, 105.33) * mm, "end": v(-128.35, 105.32) * mm});
            skLineSegment(sketch, "E2891", {"start": v(-128.35, 105.32) * mm, "end": v(-128.77, 105.34) * mm});
            skLineSegment(sketch, "E2892", {"start": v(-128.77, 105.34) * mm, "end": v(-128.9, 105.34) * mm});
            skLineSegment(sketch, "E2893", {"start": v(-128.9, 105.34) * mm, "end": v(-130.1, 105.34) * mm});
            skLineSegment(sketch, "E2894", {"start": v(-130.1, 105.34) * mm, "end": v(-142.1, 105.3) * mm});
            skLineSegment(sketch, "E2895", {"start": v(-142.1, 105.3) * mm, "end": v(-143.3, 105.32) * mm});
            skLineSegment(sketch, "E2896", {"start": v(-143.3, 105.32) * mm, "end": v(-143.71, 105.33) * mm});
            skLineSegment(sketch, "E2897", {"start": v(-143.71, 105.33) * mm, "end": v(-144.93, 105.13) * mm});
            skLineSegment(sketch, "E2898", {"start": v(-144.93, 105.13) * mm, "end": v(-146.23, 104.52) * mm});
            skLineSegment(sketch, "E2899", {"start": v(-146.23, 104.52) * mm, "end": v(-147.25, 103.46) * mm});
            skLineSegment(sketch, "E2900", {"start": v(-147.25, 103.46) * mm, "end": v(-147.88, 102.36) * mm});
            skLineSegment(sketch, "E2901", {"start": v(-147.88, 102.36) * mm, "end": v(-148.03, 101.98) * mm});
            skLineSegment(sketch, "E2902", {"start": v(-148.03, 101.98) * mm, "end": v(-147.56, 101.8) * mm});
            skLineSegment(sketch, "E2903", {"start": v(-147.56, 101.8) * mm, "end": v(-142.95, 99.96) * mm});
            skLineSegment(sketch, "E2904", {"start": v(-142.95, 99.96) * mm, "end": v(-142.5, 99.78) * mm});
            skLineSegment(sketch, "E2905", {"start": v(-142.5, 99.78) * mm, "end": v(-142.11, 99.63) * mm});
            skLineSegment(sketch, "E2906", {"start": v(-142.11, 99.63) * mm, "end": v(-140.18, 98.93) * mm});
            skLineSegment(sketch, "E2907", {"start": v(-140.18, 98.93) * mm, "end": v(-138.28, 98.16) * mm});
            skLineSegment(sketch, "E2908", {"start": v(-138.28, 98.16) * mm, "end": v(-137.9, 97.99) * mm});
            skLineSegment(sketch, "E2909", {"start": v(-137.9, 97.99) * mm, "end": v(-137.7, 97.89) * mm});
            skLineSegment(sketch, "E2910", {"start": v(-137.7, 97.89) * mm, "end": v(-137.06, 97.7) * mm});
            skLineSegment(sketch, "E2911", {"start": v(-137.06, 97.7) * mm, "end": v(-136.31, 97.73) * mm});
            skLineSegment(sketch, "E2912", {"start": v(-136.31, 97.73) * mm, "end": v(-135.63, 98.03) * mm});
            skLineSegment(sketch, "E2913", {"start": v(-135.63, 98.03) * mm, "end": v(-135.14, 98.43) * mm});
            skLineSegment(sketch, "E2914", {"start": v(-135.14, 98.43) * mm, "end": v(-135, 98.59) * mm});
            skLineSegment(sketch, "E2915", {"start": v(-135, 98.59) * mm, "end": v(-134.86, 98.72) * mm});
            skLineSegment(sketch, "E2916", {"start": v(-134.86, 98.72) * mm, "end": v(-133.44, 99.96) * mm});
            skLineSegment(sketch, "E2917", {"start": v(-133.44, 99.96) * mm, "end": v(-133.3, 100.08) * mm});
            skLineSegment(sketch, "E2918", {"start": v(-133.3, 100.08) * mm, "end": v(-133.22, 100.15) * mm});
            skLineSegment(sketch, "E2919", {"start": v(-133.22, 100.15) * mm, "end": v(-132.8, 100.44) * mm});
            skLineSegment(sketch, "E2920", {"start": v(-132.8, 100.44) * mm, "end": v(-132.3, 100.57) * mm});
            skLineSegment(sketch, "E2921", {"start": v(-132.3, 100.57) * mm, "end": v(-132.2, 100.56) * mm});
            skLineSegment(sketch, "E2922", {"start": v(-132.2, 100.56) * mm, "end": v(-132.08, 100.55) * mm});
            skLineSegment(sketch, "E2923", {"start": v(-132.08, 100.55) * mm, "end": v(-131.5, 100.46) * mm});
            skLineSegment(sketch, "E2924", {"start": v(-131.5, 100.46) * mm, "end": v(-130.99, 100.16) * mm});
            skLineSegment(sketch, "E2925", {"start": v(-130.99, 100.16) * mm, "end": v(-130.91, 100.05) * mm});
            skLineSegment(sketch, "E2926", {"start": v(-130.91, 100.05) * mm, "end": v(-130.84, 99.94) * mm});
            skLineSegment(sketch, "E2927", {"start": v(-130.84, 99.94) * mm, "end": v(-130.84, 99.44) * mm});
            skLineSegment(sketch, "E2928", {"start": v(-130.84, 99.44) * mm, "end": v(-131.1, 99) * mm});
            skLineSegment(sketch, "E2929", {"start": v(-131.1, 99) * mm, "end": v(-131.16, 98.93) * mm});
            skLineSegment(sketch, "E2930", {"start": v(-131.16, 98.93) * mm, "end": v(-131.82, 98.1) * mm});
            skLineSegment(sketch, "E2931", {"start": v(-131.82, 98.1) * mm, "end": v(-134.89, 93.76) * mm});
            skLineSegment(sketch, "E2932", {"start": v(-134.89, 93.76) * mm, "end": v(-137.63, 89.23) * mm});
            skLineSegment(sketch, "E2933", {"start": v(-137.63, 89.23) * mm, "end": v(-138.13, 88.29) * mm});
            skLineSegment(sketch, "E2934", {"start": v(-138.13, 88.29) * mm, "end": v(-138.18, 88.18) * mm});
            skLineSegment(sketch, "E2935", {"start": v(-138.18, 88.18) * mm, "end": v(-138.53, 87.84) * mm});
            skLineSegment(sketch, "E2936", {"start": v(-138.53, 87.84) * mm, "end": v(-139, 87.8) * mm});
            skLineSegment(sketch, "E2937", {"start": v(-139, 87.8) * mm, "end": v(-139.12, 87.84) * mm});
            skLineSegment(sketch, "E2938", {"start": v(-139.12, 87.84) * mm, "end": v(-139.25, 87.88) * mm});
            skLineSegment(sketch, "E2939", {"start": v(-139.25, 87.88) * mm, "end": v(-139.7, 88.22) * mm});
            skLineSegment(sketch, "E2940", {"start": v(-139.7, 88.22) * mm, "end": v(-139.9, 88.76) * mm});
            skLineSegment(sketch, "E2941", {"start": v(-139.9, 88.76) * mm, "end": v(-139.9, 88.9) * mm});
            skLineSegment(sketch, "E2942", {"start": v(-139.9, 88.9) * mm, "end": v(-139.9, 89.09) * mm});
            skLineSegment(sketch, "E2943", {"start": v(-139.9, 89.09) * mm, "end": v(-139.7, 89.92) * mm});
            skLineSegment(sketch, "E2944", {"start": v(-139.7, 89.92) * mm, "end": v(-139.38, 90.7) * mm});
            skLineSegment(sketch, "E2945", {"start": v(-139.38, 90.7) * mm, "end": v(-139.3, 90.86) * mm});
            skLineSegment(sketch, "E2946", {"start": v(-139.3, 90.86) * mm, "end": v(-139.24, 91.02) * mm});
            skLineSegment(sketch, "E2947", {"start": v(-139.24, 91.02) * mm, "end": v(-139.24, 91.67) * mm});
            skLineSegment(sketch, "E2948", {"start": v(-139.24, 91.67) * mm, "end": v(-139.66, 92.14) * mm});
            skLineSegment(sketch, "E2949", {"start": v(-139.66, 92.14) * mm, "end": v(-139.8, 92.21) * mm});
            skLineSegment(sketch, "E2950", {"start": v(-139.8, 92.21) * mm, "end": v(-139.92, 92.27) * mm});
            skLineSegment(sketch, "E2951", {"start": v(-139.92, 92.27) * mm, "end": v(-141.18, 92.83) * mm});
            skLineSegment(sketch, "E2952", {"start": v(-141.18, 92.83) * mm, "end": v(-141.3, 92.88) * mm});
            skLineSegment(sketch, "E2953", {"start": v(-141.3, 92.88) * mm, "end": v(-143.06, 93.55) * mm});
            skLineSegment(sketch, "E2954", {"start": v(-143.06, 93.55) * mm, "end": v(-160.64, 100.31) * mm});
            skLineSegment(sketch, "E2955", {"start": v(-160.64, 100.31) * mm, "end": v(-162.4, 100.99) * mm});
            skLineSegment(sketch, "E2956", {"start": v(-162.4, 100.99) * mm, "end": v(-162.47, 101.01) * mm});
            skLineSegment(sketch, "E2957", {"start": v(-162.47, 101.01) * mm, "end": v(-163.1, 101.25) * mm});
            skLineSegment(sketch, "E2958", {"start": v(-163.1, 101.25) * mm, "end": v(-163.17, 101.27) * mm});
            skLineSegment(sketch, "E2959", {"start": v(-163.17, 101.27) * mm, "end": v(-163.42, 101.35) * mm});
            skLineSegment(sketch, "E2960", {"start": v(-163.42, 101.35) * mm, "end": v(-164.14, 101.6) * mm});
            skLineSegment(sketch, "E2961", {"start": v(-164.14, 101.6) * mm, "end": v(-164.84, 101.83) * mm});
            skLineSegment(sketch, "E2962", {"start": v(-164.84, 101.83) * mm, "end": v(-165.35, 101.94) * mm});
            skLineSegment(sketch, "E2963", {"start": v(-165.35, 101.94) * mm, "end": v(-165.73, 101.92) * mm});
            skLineSegment(sketch, "E2964", {"start": v(-165.73, 101.92) * mm, "end": v(-166.06, 101.74) * mm});
            skLineSegment(sketch, "E2965", {"start": v(-166.06, 101.74) * mm, "end": v(-166.41, 101.4) * mm});
            skLineSegment(sketch, "E2966", {"start": v(-166.41, 101.4) * mm, "end": v(-166.85, 100.89) * mm});
            skLineSegment(sketch, "E2967", {"start": v(-166.85, 100.89) * mm, "end": v(-167.3, 100.36) * mm});
            skLineSegment(sketch, "E2968", {"start": v(-167.3, 100.36) * mm, "end": v(-167.46, 100.19) * mm});
            skLineSegment(sketch, "E2969", {"start": v(-167.46, 100.19) * mm, "end": v(-167.5, 100.13) * mm});
            skLineSegment(sketch, "E2970", {"start": v(-167.5, 100.13) * mm, "end": v(-167.96, 99.62) * mm});
            skLineSegment(sketch, "E2971", {"start": v(-167.96, 99.62) * mm, "end": v(-168, 99.57) * mm});
            skLineSegment(sketch, "E2972", {"start": v(-168, 99.57) * mm, "end": v(-168.08, 99.49) * mm});
            skLineSegment(sketch, "E2973", {"start": v(-168.08, 99.49) * mm, "end": v(-168.4, 99.31) * mm});
            skLineSegment(sketch, "E2974", {"start": v(-168.4, 99.31) * mm, "end": v(-168.76, 99.3) * mm});
            skLineSegment(sketch, "E2975", {"start": v(-168.76, 99.3) * mm, "end": v(-169.13, 99.45) * mm});
            skLineSegment(sketch, "E2976", {"start": v(-169.13, 99.45) * mm, "end": v(-169.4, 99.6) * mm});
            skLineSegment(sketch, "E2977", {"start": v(-169.4, 99.6) * mm, "end": v(-169.48, 99.64) * mm});
            skLineSegment(sketch, "E2978", {"start": v(-169.48, 99.64) * mm, "end": v(-169.63, 99.7) * mm});
            skLineSegment(sketch, "E2979", {"start": v(-169.63, 99.7) * mm, "end": v(-169.93, 100.17) * mm});
            skLineSegment(sketch, "E2980", {"start": v(-169.93, 100.17) * mm, "end": v(-169.78, 100.72) * mm});
            skLineSegment(sketch, "E2981", {"start": v(-169.78, 100.72) * mm, "end": v(-169.71, 100.84) * mm});
            skLineSegment(sketch, "E2982", {"start": v(-169.71, 100.84) * mm, "end": v(-169.6, 101.03) * mm});
            skLineSegment(sketch, "E2983", {"start": v(-169.6, 101.03) * mm, "end": v(-168.47, 102.95) * mm});
            skLineSegment(sketch, "E2984", {"start": v(-168.47, 102.95) * mm, "end": v(-168.35, 103.13) * mm});
            skLineSegment(sketch, "E2985", {"start": v(-168.35, 103.13) * mm, "end": v(-167.92, 103.76) * mm});
            skLineSegment(sketch, "E2986", {"start": v(-167.92, 103.76) * mm, "end": v(-164.19, 110.3) * mm});
            skLineSegment(sketch, "E2987", {"start": v(-164.19, 110.3) * mm, "end": v(-163.85, 110.97) * mm});
            skLineSegment(sketch, "E2988", {"start": v(-163.85, 110.97) * mm, "end": v(-163.51, 111.66) * mm});
            skLineSegment(sketch, "E2989", {"start": v(-163.51, 111.66) * mm, "end": v(-161.4, 114.74) * mm});
            skLineSegment(sketch, "E2990", {"start": v(-161.4, 114.74) * mm, "end": v(-158.6, 117.24) * mm});
            skLineSegment(sketch, "E2991", {"start": v(-158.6, 117.24) * mm, "end": v(-157.94, 117.64) * mm});
            skLineSegment(sketch, "E2992", {"start": v(-157.94, 117.64) * mm, "end": v(-157.36, 117.88) * mm});
            skLineSegment(sketch, "E2993", {"start": v(-157.36, 117.88) * mm, "end": v(-154.43, 118.8) * mm});
            skLineSegment(sketch, "E2994", {"start": v(-154.43, 118.8) * mm, "end": v(-151.38, 119.04) * mm});
            skLineSegment(sketch, "E2995", {"start": v(-151.38, 119.04) * mm, "end": v(-150.75, 118.95) * mm});
            skLineSegment(sketch, "E2996", {"start": v(-150.75, 118.95) * mm, "end": v(-150.22, 118.88) * mm});
            skLineSegment(sketch, "E2997", {"start": v(-150.22, 118.88) * mm, "end": v(-148.65, 118.47) * mm});
            skLineSegment(sketch, "E2998", {"start": v(-148.65, 118.47) * mm, "end": v(-146.83, 117.6) * mm});
            skLineSegment(sketch, "E2999", {"start": v(-146.83, 117.6) * mm, "end": v(-145.35, 116.23) * mm});
            skLineSegment(sketch, "E3000", {"start": v(-145.35, 116.23) * mm, "end": v(-144.47, 114.81) * mm});
            skLineSegment(sketch, "E3001", {"start": v(-144.47, 114.81) * mm, "end": v(-144.27, 114.3) * mm});
            skLineSegment(sketch, "E3002", {"start": v(-144.27, 114.3) * mm, "end": v(-144.2, 114.13) * mm});
            skLineSegment(sketch, "E3003", {"start": v(-144.2, 114.13) * mm, "end": v(-143.94, 112.46) * mm});
            skLineSegment(sketch, "E3004", {"start": v(-143.94, 112.46) * mm, "end": v(-143.95, 112.29) * mm});
            skLineSegment(sketch, "E3005", {"start": v(-143.95, 112.29) * mm, "end": v(-143.97, 112.03) * mm});
            skLineSegment(sketch, "E3006", {"start": v(-143.97, 112.03) * mm, "end": v(-143.92, 111.25) * mm});
            skLineSegment(sketch, "E3007", {"start": v(-143.92, 111.25) * mm, "end": v(-143.63, 110.77) * mm});
            skLineSegment(sketch, "E3008", {"start": v(-143.63, 110.77) * mm, "end": v(-143.06, 110.66) * mm});
            skLineSegment(sketch, "E3009", {"start": v(-143.06, 110.66) * mm, "end": v(-142.4, 110.7) * mm});
            skLineSegment(sketch, "E3010", {"start": v(-142.4, 110.7) * mm, "end": v(-142.17, 110.7) * mm});
            skLineSegment(sketch, "E3011", {"start": v(-142.17, 110.7) * mm, "end": v(-141.59, 110.74) * mm});
            skLineSegment(sketch, "E3012", {"start": v(-141.59, 110.74) * mm, "end": v(-135.78, 111.15) * mm});
            skLineSegment(sketch, "E3013", {"start": v(-135.78, 111.15) * mm, "end": v(-135.2, 111.22) * mm});
            skLineSegment(sketch, "E3014", {"start": v(-135.2, 111.22) * mm, "end": v(-134.7, 111.29) * mm});
            skLineSegment(sketch, "E3015", {"start": v(-134.7, 111.29) * mm, "end": v(-129.75, 111.6) * mm});
            skLineSegment(sketch, "E3016", {"start": v(-129.75, 111.6) * mm, "end": v(-129.26, 111.6) * mm});
            skLineSegment(sketch, "E3017", {"start": v(-129.26, 111.6) * mm, "end": v(-128.63, 111.62) * mm});
            skLineSegment(sketch, "E3018", {"start": v(-128.63, 111.62) * mm, "end": v(-126.76, 112.06) * mm});
            skLineSegment(sketch, "E3019", {"start": v(-126.76, 112.06) * mm, "end": v(-124.68, 113.23) * mm});
            skLineSegment(sketch, "E3020", {"start": v(-124.68, 113.23) * mm, "end": v(-123.1, 115.01) * mm});
            skLineSegment(sketch, "E3021", {"start": v(-123.1, 115.01) * mm, "end": v(-122.3, 116.72) * mm});
            skLineSegment(sketch, "E3022", {"start": v(-122.3, 116.72) * mm, "end": v(-122.14, 117.32) * mm});
            skLineSegment(sketch, "E3023", {"start": v(-122.14, 117.32) * mm, "end": v(-122.1, 117.49) * mm});
            skLineSegment(sketch, "E3024", {"start": v(-122.1, 117.49) * mm, "end": v(-122.1, 118.02) * mm});
            skLineSegment(sketch, "E3025", {"start": v(-122.1, 118.02) * mm, "end": v(-122.35, 118.52) * mm});
            skLineSegment(sketch, "E3026", {"start": v(-122.35, 118.52) * mm, "end": v(-122.8, 118.86) * mm});
            skLineSegment(sketch, "E3027", {"start": v(-122.8, 118.86) * mm, "end": v(-123.2, 119.08) * mm});
            skLineSegment(sketch, "E3028", {"start": v(-123.2, 119.08) * mm, "end": v(-123.35, 119.14) * mm});
            skLineSegment(sketch, "E3029", {"start": v(-123.35, 119.14) * mm, "end": v(-124.12, 119.48) * mm});
            skLineSegment(sketch, "E3030", {"start": v(-124.12, 119.48) * mm, "end": v(-131.8, 122.84) * mm});
            skLineSegment(sketch, "E3031", {"start": v(-131.8, 122.84) * mm, "end": v(-132.57, 123.17) * mm});
            skLineSegment(sketch, "E3032", {"start": v(-132.57, 123.17) * mm, "end": v(-133.67, 123.64) * mm});
            skLineSegment(sketch, "E3033", {"start": v(-133.67, 123.64) * mm, "end": v(-144.7, 128.34) * mm});
            skLineSegment(sketch, "E3034", {"start": v(-144.7, 128.34) * mm, "end": v(-145.8, 128.8) * mm});
            skLineSegment(sketch, "E3035", {"start": v(-145.8, 128.8) * mm, "end": v(-146.11, 128.94) * mm});
            skLineSegment(sketch, "E3036", {"start": v(-146.11, 128.94) * mm, "end": v(-147.03, 129.28) * mm});
            skLineSegment(sketch, "E3037", {"start": v(-147.03, 129.28) * mm, "end": v(-147.83, 129.35) * mm});
            skLineSegment(sketch, "E3038", {"start": v(-147.83, 129.35) * mm, "end": v(-148.56, 128.95) * mm});
            skLineSegment(sketch, "E3039", {"start": v(-148.56, 128.95) * mm, "end": v(-149.3, 128.25) * mm});
            skLineSegment(sketch, "E3040", {"start": v(-149.3, 128.25) * mm, "end": v(-149.54, 128) * mm});
            skLineSegment(sketch, "E3041", {"start": v(-149.54, 128) * mm, "end": v(-149.65, 127.9) * mm});
            skLineSegment(sketch, "E3042", {"start": v(-149.65, 127.9) * mm, "end": v(-150.73, 126.8) * mm});
            skLineSegment(sketch, "E3043", {"start": v(-150.73, 126.8) * mm, "end": v(-150.84, 126.7) * mm});
            skLineSegment(sketch, "E3044", {"start": v(-150.84, 126.7) * mm, "end": v(-150.96, 126.57) * mm});
            skLineSegment(sketch, "E3045", {"start": v(-150.96, 126.57) * mm, "end": v(-151.57, 126.34) * mm});
            skLineSegment(sketch, "E3046", {"start": v(-151.57, 126.34) * mm, "end": v(-152.22, 126.48) * mm});
            skLineSegment(sketch, "E3047", {"start": v(-152.22, 126.48) * mm, "end": v(-152.35, 126.54) * mm});
            skLineSegment(sketch, "E3048", {"start": v(-152.35, 126.54) * mm, "end": v(-152.43, 126.58) * mm});
            skLineSegment(sketch, "E3049", {"start": v(-152.43, 126.58) * mm, "end": v(-152.68, 126.74) * mm});
            skLineSegment(sketch, "E3050", {"start": v(-152.68, 126.74) * mm, "end": v(-152.88, 126.97) * mm});
            skLineSegment(sketch, "E3051", {"start": v(-152.88, 126.97) * mm, "end": v(-152.9, 127.27) * mm});
            skLineSegment(sketch, "E3052", {"start": v(-152.9, 127.27) * mm, "end": v(-152.75, 127.55) * mm});
            skLineSegment(sketch, "E3053", {"start": v(-152.75, 127.55) * mm, "end": v(-152.69, 127.63) * mm});
            skLineSegment(sketch, "E3054", {"start": v(-152.69, 127.63) * mm, "end": v(-152.67, 127.65) * mm});
            skLineSegment(sketch, "E3055", {"start": v(-152.67, 127.65) * mm, "end": v(-152.57, 127.78) * mm});
            skLineSegment(sketch, "E3056", {"start": v(-152.57, 127.78) * mm, "end": v(-152.55, 127.79) * mm});
            skLineSegment(sketch, "E3057", {"start": v(-152.55, 127.79) * mm, "end": v(-151.76, 128.55) * mm});
            skLineSegment(sketch, "E3058", {"start": v(-151.76, 128.55) * mm, "end": v(-149.6, 131.1) * mm});
            skLineSegment(sketch, "E3059", {"start": v(-149.6, 131.1) * mm, "end": v(-147.01, 134.67) * mm});
            skLineSegment(sketch, "E3060", {"start": v(-147.01, 134.67) * mm, "end": v(-144.54, 138.34) * mm});
            skLineSegment(sketch, "E3061", {"start": v(-144.54, 138.34) * mm, "end": v(-142.63, 141.04) * mm});
            skLineSegment(sketch, "E3062", {"start": v(-142.63, 141.04) * mm, "end": v(-141.94, 141.9) * mm});
            skLineSegment(sketch, "E3063", {"start": v(-141.94, 141.9) * mm, "end": v(-141.51, 142.44) * mm});
            skLineSegment(sketch, "E3064", {"start": v(-141.51, 142.44) * mm, "end": v(-137.16, 147.73) * mm});
            skLineSegment(sketch, "E3065", {"start": v(-137.16, 147.73) * mm, "end": v(-136.73, 148.27) * mm});
            skLineSegment(sketch, "E3066", {"start": v(-136.73, 148.27) * mm, "end": v(-136.6, 148.44) * mm});
            skLineSegment(sketch, "E3067", {"start": v(-136.6, 148.44) * mm, "end": v(-136.14, 148.86) * mm});
            skLineSegment(sketch, "E3068", {"start": v(-136.14, 148.86) * mm, "end": v(-135.52, 149.14) * mm});
            skLineSegment(sketch, "E3069", {"start": v(-135.52, 149.14) * mm, "end": v(-134.84, 149.13) * mm});
            skLineSegment(sketch, "E3070", {"start": v(-134.84, 149.13) * mm, "end": v(-134.25, 148.94) * mm});
            skLineSegment(sketch, "E3071", {"start": v(-134.25, 148.94) * mm, "end": v(-134.06, 148.85) * mm});
            skLineSegment(sketch, "E3072", {"start": v(-134.06, 148.85) * mm, "end": v(-133.68, 148.67) * mm});
            skLineSegment(sketch, "E3073", {"start": v(-133.68, 148.67) * mm, "end": v(-129.76, 146.95) * mm});
            skLineSegment(sketch, "E3074", {"start": v(-129.76, 146.95) * mm, "end": v(-129.37, 146.77) * mm});
            skLineSegment(sketch, "E3075", {"start": v(-129.37, 146.77) * mm, "end": v(-129.28, 146.73) * mm});
            skLineSegment(sketch, "E3076", {"start": v(-129.28, 146.73) * mm, "end": v(-129, 146.62) * mm});
            skLineSegment(sketch, "E3077", {"start": v(-129, 146.62) * mm, "end": v(-128.64, 146.46) * mm});
            skLineSegment(sketch, "E3078", {"start": v(-128.64, 146.46) * mm, "end": v(-128.41, 146.17) * mm});
            skLineSegment(sketch, "E3079", {"start": v(-128.41, 146.17) * mm, "end": v(-128.4, 145.8) * mm});
            skLineSegment(sketch, "E3080", {"start": v(-128.4, 145.8) * mm, "end": v(-128.44, 145.69) * mm});
            skLineSegment(sketch, "E3081", {"start": v(-128.44, 145.69) * mm, "end": v(-128.5, 145.55) * mm});
            skLineSegment(sketch, "E3082", {"start": v(-128.5, 145.55) * mm, "end": v(-128.92, 145.07) * mm});
            skLineSegment(sketch, "E3083", {"start": v(-128.92, 145.07) * mm, "end": v(-129.57, 144.88) * mm});
            skLineSegment(sketch, "E3084", {"start": v(-129.57, 144.88) * mm, "end": v(-129.72, 144.89) * mm});
            skLineSegment(sketch, "E3085", {"start": v(-129.72, 144.89) * mm, "end": v(-130.1, 144.9) * mm});
            skLineSegment(sketch, "E3086", {"start": v(-130.1, 144.9) * mm, "end": v(-133.87, 145) * mm});
            skLineSegment(sketch, "E3087", {"start": v(-133.87, 145) * mm, "end": v(-134.25, 145.01) * mm});
            skLineSegment(sketch, "E3088", {"start": v(-134.25, 145.01) * mm, "end": v(-134.56, 145.03) * mm});
            skLineSegment(sketch, "E3089", {"start": v(-134.56, 145.03) * mm, "end": v(-135.92, 144.74) * mm});
            skLineSegment(sketch, "E3090", {"start": v(-135.92, 144.74) * mm, "end": v(-137.08, 143.94) * mm});
            skLineSegment(sketch, "E3091", {"start": v(-137.08, 143.94) * mm, "end": v(-137.3, 143.71) * mm});
            skLineSegment(sketch, "E3092", {"start": v(-137.3, 143.71) * mm, "end": v(-137.84, 143.15) * mm});
            skLineSegment(sketch, "E3093", {"start": v(-137.84, 143.15) * mm, "end": v(-140.3, 140.2) * mm});
            skLineSegment(sketch, "E3094", {"start": v(-140.3, 140.2) * mm, "end": v(-142.58, 137.1) * mm});
            skLineSegment(sketch, "E3095", {"start": v(-142.58, 137.1) * mm, "end": v(-143.02, 136.46) * mm});
            skLineSegment(sketch, "E3096", {"start": v(-143.02, 136.46) * mm, "end": v(-143.14, 136.28) * mm});
            skLineSegment(sketch, "E3097", {"start": v(-143.14, 136.28) * mm, "end": v(-143.5, 135.7) * mm});
            skLineSegment(sketch, "E3098", {"start": v(-143.5, 135.7) * mm, "end": v(-143.6, 135.24) * mm});
            skLineSegment(sketch, "E3099", {"start": v(-143.6, 135.24) * mm, "end": v(-143.3, 134.88) * mm});
            skLineSegment(sketch, "E3100", {"start": v(-143.3, 134.88) * mm, "end": v(-142.73, 134.59) * mm});
            skLineSegment(sketch, "E3101", {"start": v(-142.73, 134.59) * mm, "end": v(-142.54, 134.5) * mm});
            skLineSegment(sketch, "E3102", {"start": v(-142.54, 134.5) * mm, "end": v(-141.78, 134.16) * mm});
            skLineSegment(sketch, "E3103", {"start": v(-141.78, 134.16) * mm, "end": v(-134.1, 130.77) * mm});
            skLineSegment(sketch, "E3104", {"start": v(-134.1, 130.77) * mm, "end": v(-133.33, 130.42) * mm});
            skLineSegment(sketch, "E3105", {"start": v(-133.33, 130.42) * mm, "end": v(-133.12, 130.32) * mm});
            skLineSegment(sketch, "E3106", {"start": v(-133.12, 130.32) * mm, "end": v(-132.25, 130.24) * mm});
            skLineSegment(sketch, "E3107", {"start": v(-132.25, 130.24) * mm, "end": v(-131.52, 130.7) * mm});
            skLineSegment(sketch, "E3108", {"start": v(-131.52, 130.7) * mm, "end": v(-131.39, 130.88) * mm});
            skLineSegment(sketch, "E3109", {"start": v(-131.39, 130.88) * mm, "end": v(-131.07, 131.28) * mm});
            skLineSegment(sketch, "E3110", {"start": v(-131.07, 131.28) * mm, "end": v(-129.6, 133.37) * mm});
            skLineSegment(sketch, "E3111", {"start": v(-129.6, 133.37) * mm, "end": v(-128.34, 135.6) * mm});
            skLineSegment(sketch, "E3112", {"start": v(-128.34, 135.6) * mm, "end": v(-128.13, 136.07) * mm});
            skLineSegment(sketch, "E3113", {"start": v(-128.13, 136.07) * mm, "end": v(-128.05, 136.24) * mm});
            skLineSegment(sketch, "E3114", {"start": v(-128.05, 136.24) * mm, "end": v(-127.9, 136.78) * mm});
            skLineSegment(sketch, "E3115", {"start": v(-127.9, 136.78) * mm, "end": v(-127.9, 137.38) * mm});
            skLineSegment(sketch, "E3116", {"start": v(-127.9, 137.38) * mm, "end": v(-128.12, 137.9) * mm});
            skLineSegment(sketch, "E3117", {"start": v(-128.12, 137.9) * mm, "end": v(-128.45, 138.3) * mm});
            skLineSegment(sketch, "E3118", {"start": v(-128.45, 138.3) * mm, "end": v(-128.57, 138.4) * mm});
            skLineSegment(sketch, "E3119", {"start": v(-128.57, 138.4) * mm, "end": v(-128.73, 138.53) * mm});
            skLineSegment(sketch, "E3120", {"start": v(-128.73, 138.53) * mm, "end": v(-130.34, 139.77) * mm});
            skLineSegment(sketch, "E3121", {"start": v(-130.34, 139.77) * mm, "end": v(-130.5, 139.88) * mm});
            skLineSegment(sketch, "E3122", {"start": v(-130.5, 139.88) * mm, "end": v(-130.6, 139.95) * mm});
            skLineSegment(sketch, "E3123", {"start": v(-130.6, 139.95) * mm, "end": v(-130.98, 140.26) * mm});
            skLineSegment(sketch, "E3124", {"start": v(-130.98, 140.26) * mm, "end": v(-131.1, 140.71) * mm});
            skLineSegment(sketch, "E3125", {"start": v(-131.1, 140.71) * mm, "end": v(-131.06, 140.83) * mm});
            skLineSegment(sketch, "E3126", {"start": v(-131.06, 140.83) * mm, "end": v(-131.01, 140.96) * mm});
            skLineSegment(sketch, "E3127", {"start": v(-131.01, 140.96) * mm, "end": v(-130.62, 141.41) * mm});
            skLineSegment(sketch, "E3128", {"start": v(-130.62, 141.41) * mm, "end": v(-130.07, 141.58) * mm});
            skLineSegment(sketch, "E3129", {"start": v(-130.07, 141.58) * mm, "end": v(-129.94, 141.56) * mm});
            skLineSegment(sketch, "E3130", {"start": v(-129.94, 141.56) * mm, "end": v(-129.81, 141.55) * mm});
            skLineSegment(sketch, "E3131", {"start": v(-129.81, 141.55) * mm, "end": v(-128.51, 141.16) * mm});
            skLineSegment(sketch, "E3132", {"start": v(-128.51, 141.16) * mm, "end": v(-128.4, 141.1) * mm});
            skLineSegment(sketch, "E3133", {"start": v(-128.4, 141.1) * mm, "end": v(-127.61, 140.76) * mm});
            skLineSegment(sketch, "E3134", {"start": v(-127.61, 140.76) * mm, "end": v(-119.83, 137.27) * mm});
            skLineSegment(sketch, "E3135", {"start": v(-119.83, 137.27) * mm, "end": v(-119.06, 136.91) * mm});
            skLineSegment(sketch, "E3136", {"start": v(-119.06, 136.91) * mm, "end": v(-118.98, 136.88) * mm});
            skLineSegment(sketch, "E3137", {"start": v(-118.98, 136.88) * mm, "end": v(-118.7, 136.8) * mm});
            skLineSegment(sketch, "E3138", {"start": v(-118.7, 136.8) * mm, "end": v(-118.34, 136.64) * mm});
            skLineSegment(sketch, "E3139", {"start": v(-118.34, 136.64) * mm, "end": v(-118.13, 136.36) * mm});
            skLineSegment(sketch, "E3140", {"start": v(-118.13, 136.36) * mm, "end": v(-118.19, 135.96) * mm});
            skLineSegment(sketch, "E3141", {"start": v(-118.19, 135.96) * mm, "end": v(-118.24, 135.84) * mm});
            skLineSegment(sketch, "E3142", {"start": v(-118.24, 135.84) * mm, "end": v(-118.33, 135.68) * mm});
            skLineSegment(sketch, "E3143", {"start": v(-118.33, 135.68) * mm, "end": v(-118.85, 135.21) * mm});
            skLineSegment(sketch, "E3144", {"start": v(-118.85, 135.21) * mm, "end": v(-119.58, 135.19) * mm});
            skLineSegment(sketch, "E3145", {"start": v(-119.58, 135.19) * mm, "end": v(-119.76, 135.24) * mm});
            skLineSegment(sketch, "E3146", {"start": v(-119.76, 135.24) * mm, "end": v(-119.99, 135.32) * mm});
            skLineSegment(sketch, "E3147", {"start": v(-119.99, 135.32) * mm, "end": v(-121.15, 135.6) * mm});
            skLineSegment(sketch, "E3148", {"start": v(-121.15, 135.6) * mm, "end": v(-122.31, 135.9) * mm});
            skLineSegment(sketch, "E3149", {"start": v(-122.31, 135.9) * mm, "end": v(-122.54, 135.97) * mm});
            skLineSegment(sketch, "E3150", {"start": v(-122.54, 135.97) * mm, "end": v(-122.74, 136.05) * mm});
            skLineSegment(sketch, "E3151", {"start": v(-122.74, 136.05) * mm, "end": v(-123.4, 136.15) * mm});
            skLineSegment(sketch, "E3152", {"start": v(-123.4, 136.15) * mm, "end": v(-124.17, 136.06) * mm});
            skLineSegment(sketch, "E3153", {"start": v(-124.17, 136.06) * mm, "end": v(-124.87, 135.72) * mm});
            skLineSegment(sketch, "E3154", {"start": v(-124.87, 135.72) * mm, "end": v(-125.36, 135.33) * mm});
            skLineSegment(sketch, "E3155", {"start": v(-125.36, 135.33) * mm, "end": v(-125.5, 135.17) * mm});
            skLineSegment(sketch, "E3156", {"start": v(-125.5, 135.17) * mm, "end": v(-125.89, 134.77) * mm});
            skLineSegment(sketch, "E3157", {"start": v(-125.89, 134.77) * mm, "end": v(-127.55, 132.6) * mm});
            skLineSegment(sketch, "E3158", {"start": v(-127.55, 132.6) * mm, "end": v(-129.1, 130.33) * mm});
            skLineSegment(sketch, "E3159", {"start": v(-129.1, 130.33) * mm, "end": v(-129.4, 129.89) * mm});
            skLineSegment(sketch, "E3160", {"start": v(-129.4, 129.89) * mm, "end": v(-129.48, 129.78) * mm});
            skLineSegment(sketch, "E3161", {"start": v(-129.48, 129.78) * mm, "end": v(-129.62, 129.4) * mm});
            skLineSegment(sketch, "E3162", {"start": v(-129.62, 129.4) * mm, "end": v(-129.55, 129.01) * mm});
            skLineSegment(sketch, "E3163", {"start": v(-129.55, 129.01) * mm, "end": v(-129.27, 128.7) * mm});
            skLineSegment(sketch, "E3164", {"start": v(-129.27, 128.7) * mm, "end": v(-128.95, 128.51) * mm});
            skLineSegment(sketch, "E3165", {"start": v(-128.95, 128.51) * mm, "end": v(-128.84, 128.46) * mm});
            skLineSegment(sketch, "E3166", {"start": v(-128.84, 128.46) * mm, "end": v(-128.5, 128.3) * mm});
            skLineSegment(sketch, "E3167", {"start": v(-128.5, 128.3) * mm, "end": v(-125.06, 126.76) * mm});
            skLineSegment(sketch, "E3168", {"start": v(-125.06, 126.76) * mm, "end": v(-124.71, 126.6) * mm});
            skLineSegment(sketch, "E3169", {"start": v(-124.71, 126.6) * mm, "end": v(-124.3, 126.42) * mm});
            skLineSegment(sketch, "E3170", {"start": v(-124.3, 126.42) * mm, "end": v(-120.08, 124.5) * mm});
            skLineSegment(sketch, "E3171", {"start": v(-120.08, 124.5) * mm, "end": v(-119.67, 124.3) * mm});
            skLineSegment(sketch, "E3172", {"start": v(-119.67, 124.3) * mm, "end": v(-119.44, 124.18) * mm});
            skLineSegment(sketch, "E3173", {"start": v(-119.44, 124.18) * mm, "end": v(-118.36, 123.98) * mm});
            skLineSegment(sketch, "E3174", {"start": v(-118.36, 123.98) * mm, "end": v(-117.4, 124.35) * mm});
            skLineSegment(sketch, "E3175", {"start": v(-117.4, 124.35) * mm, "end": v(-117.22, 124.53) * mm});
            skLineSegment(sketch, "E3176", {"start": v(-117.22, 124.53) * mm, "end": v(-116.57, 125.15) * mm});
            skLineSegment(sketch, "E3177", {"start": v(-116.57, 125.15) * mm, "end": v(-113.72, 128.56) * mm});
            skLineSegment(sketch, "E3178", {"start": v(-113.72, 128.56) * mm, "end": v(-111.44, 132.37) * mm});
            skLineSegment(sketch, "E3179", {"start": v(-111.44, 132.37) * mm, "end": v(-111.08, 133.2) * mm});
            skLineSegment(sketch, "E3180", {"start": v(-111.08, 133.2) * mm, "end": v(-110.99, 133.41) * mm});
            skLineSegment(sketch, "E3181", {"start": v(-110.99, 133.41) * mm, "end": v(-110.85, 134.1) * mm});
            skLineSegment(sketch, "E3182", {"start": v(-110.85, 134.1) * mm, "end": v(-110.92, 135.01) * mm});
            skLineSegment(sketch, "E3183", {"start": v(-110.92, 135.01) * mm, "end": v(-111.2, 135.9) * mm});
            skLineSegment(sketch, "E3184", {"start": v(-111.2, 135.9) * mm, "end": v(-111.52, 136.53) * mm});
            skLineSegment(sketch, "E3185", {"start": v(-111.52, 136.53) * mm, "end": v(-111.65, 136.73) * mm});
            skLineSegment(sketch, "E3186", {"start": v(-111.65, 136.73) * mm, "end": v(-111.77, 136.94) * mm});
            skLineSegment(sketch, "E3187", {"start": v(-111.77, 136.94) * mm, "end": v(-113.16, 138.9) * mm});
            skLineSegment(sketch, "E3188", {"start": v(-113.16, 138.9) * mm, "end": v(-113.31, 139.07) * mm});
            skLineSegment(sketch, "E3189", {"start": v(-113.31, 139.07) * mm, "end": v(-113.45, 139.23) * mm});
            skLineSegment(sketch, "E3190", {"start": v(-113.45, 139.23) * mm, "end": v(-113.76, 139.96) * mm});
            skLineSegment(sketch, "E3191", {"start": v(-113.76, 139.96) * mm, "end": v(-113.5, 140.69) * mm});
            skLineSegment(sketch, "E3192", {"start": v(-113.5, 140.69) * mm, "end": v(-113.36, 140.84) * mm});
            skLineSegment(sketch, "E3193", {"start": v(-113.36, 140.84) * mm, "end": v(-113.29, 140.93) * mm});
            skLineSegment(sketch, "E3194", {"start": v(-113.29, 140.93) * mm, "end": v(-112.98, 141.13) * mm});
            skLineSegment(sketch, "E3195", {"start": v(-112.98, 141.13) * mm, "end": v(-112.62, 141.16) * mm});
            skLineSegment(sketch, "E3196", {"start": v(-112.62, 141.16) * mm, "end": v(-112.27, 141.02) * mm});
            skLineSegment(sketch, "E3197", {"start": v(-112.27, 141.02) * mm, "end": v(-112, 140.86) * mm});
            skLineSegment(sketch, "E3198", {"start": v(-112, 140.86) * mm, "end": v(-111.92, 140.8) * mm});
            skLineSegment(sketch, "E3199", {"start": v(-111.92, 140.8) * mm, "end": v(-111.4, 140.48) * mm});
            skLineSegment(sketch, "E3200", {"start": v(-111.4, 140.48) * mm, "end": v(-106.19, 137.17) * mm});
            skLineSegment(sketch, "E3201", {"start": v(-106.19, 137.17) * mm, "end": v(-105.66, 136.85) * mm});
            skLineSegment(sketch, "E3202", {"start": v(-105.66, 136.85) * mm, "end": v(-105.55, 136.78) * mm});
            skLineSegment(sketch, "E3203", {"start": v(-105.55, 136.78) * mm, "end": v(-105.25, 136.52) * mm});
            skLineSegment(sketch, "E3204", {"start": v(-105.25, 136.52) * mm, "end": v(-105.1, 136.18) * mm});
            skLineSegment(sketch, "E3205", {"start": v(-105.1, 136.18) * mm, "end": v(-105.18, 135.82) * mm});
            skLineSegment(sketch, "E3206", {"start": v(-105.18, 135.82) * mm, "end": v(-105.36, 135.5) * mm});
            skLineSegment(sketch, "E3207", {"start": v(-105.36, 135.5) * mm, "end": v(-105.43, 135.39) * mm});
            skLineSegment(sketch, "E3208", {"start": v(-105.43, 135.39) * mm, "end": v(-105.89, 134.74) * mm});
            skLineSegment(sketch, "E3209", {"start": v(-105.89, 134.74) * mm, "end": v(-110.8, 128.59) * mm});
            skLineSegment(sketch, "E3210", {"start": v(-110.8, 128.59) * mm, "end": v(-111.3, 127.97) * mm});
            skLineSegment(sketch, "E3211", {"start": v(-111.3, 127.97) * mm, "end": v(-112.05, 127.06) * mm});
            skLineSegment(sketch, "E3212", {"start": v(-112.05, 127.06) * mm, "end": v(-115.69, 122.41) * mm});
            skLineSegment(sketch, "E3213", {"start": v(-115.69, 122.41) * mm, "end": v(-119.08, 117.58) * mm});
            skLineSegment(sketch, "E3214", {"start": v(-119.08, 117.58) * mm, "end": v(-119.7, 116.57) * mm});
            skLineSegment(sketch, "E3215", {"start": v(-119.7, 116.57) * mm, "end": v(-120.14, 115.87) * mm});
            skLineSegment(sketch, "E3216", {"start": v(-120.14, 115.87) * mm, "end": v(-122.58, 112.57) * mm});
            skLineSegment(sketch, "E3217", {"start": v(-122.58, 112.57) * mm, "end": v(-125.06, 109.29) * mm});
            skLineSegment(sketch, "E3218", {"start": v(-125.06, 109.29) * mm, "end": v(-125.5, 108.6) * mm});
            skLineSegment(sketch, "E3219", {"start": v(-125.5, 108.6) * mm, "end": v(-125.65, 108.38) * mm});
            skLineSegment(sketch, "E3220", {"start": v(-125.65, 108.38) * mm, "end": v(-126.3, 107.29) * mm});
            skLineSegment(sketch, "E3221", {"start": v(-126.3, 107.29) * mm, "end": v(-126.76, 106.1) * mm});
            skLineSegment(sketch, "E3222", {"start": v(-126.76, 106.1) * mm, "end": v(-126.8, 105.83) * mm});
            skLineSegment(sketch, "E3223", {"start": v(112.44, -6.76) * mm, "end": v(112.58, -6.65) * mm});
            skLineSegment(sketch, "E3224", {"start": v(112.58, -6.65) * mm, "end": v(113.1, -6.42) * mm});
            skLineSegment(sketch, "E3225", {"start": v(113.1, -6.42) * mm, "end": v(113.62, -6.42) * mm});
            skLineSegment(sketch, "E3226", {"start": v(113.62, -6.42) * mm, "end": v(114.08, -6.58) * mm});
            skLineSegment(sketch, "E3227", {"start": v(114.08, -6.58) * mm, "end": v(114.39, -6.7) * mm});
            skLineSegment(sketch, "E3228", {"start": v(114.39, -6.7) * mm, "end": v(114.5, -6.73) * mm});
            skLineSegment(sketch, "E3229", {"start": v(114.5, -6.73) * mm, "end": v(114.75, -6.8) * mm});
            skLineSegment(sketch, "E3230", {"start": v(114.75, -6.8) * mm, "end": v(115.52, -6.9) * mm});
            skLineSegment(sketch, "E3231", {"start": v(115.52, -6.9) * mm, "end": v(116.3, -6.78) * mm});
            skLineSegment(sketch, "E3232", {"start": v(116.3, -6.78) * mm, "end": v(116.97, -6.35) * mm});
            skLineSegment(sketch, "E3233", {"start": v(116.97, -6.35) * mm, "end": v(117.46, -5.75) * mm});
            skLineSegment(sketch, "E3234", {"start": v(117.46, -5.75) * mm, "end": v(117.6, -5.53) * mm});
            skLineSegment(sketch, "E3235", {"start": v(117.6, -5.53) * mm, "end": v(117.67, -5.41) * mm});
            skLineSegment(sketch, "E3236", {"start": v(117.67, -5.41) * mm, "end": v(118.32, -4.2) * mm});
            skLineSegment(sketch, "E3237", {"start": v(118.32, -4.2) * mm, "end": v(118.38, -4.08) * mm});
            skLineSegment(sketch, "E3238", {"start": v(118.38, -4.08) * mm, "end": v(119.19, -2.42) * mm});
            skLineSegment(sketch, "E3239", {"start": v(119.19, -2.42) * mm, "end": v(127.3, 14.21) * mm});
            skLineSegment(sketch, "E3240", {"start": v(127.3, 14.21) * mm, "end": v(128.12, 15.88) * mm});
            skLineSegment(sketch, "E3241", {"start": v(128.12, 15.88) * mm, "end": v(128.23, 16.12) * mm});
            skLineSegment(sketch, "E3242", {"start": v(128.23, 16.12) * mm, "end": v(128.56, 16.85) * mm});
            skLineSegment(sketch, "E3243", {"start": v(128.56, 16.85) * mm, "end": v(128.61, 17.43) * mm});
            skLineSegment(sketch, "E3244", {"start": v(128.61, 17.43) * mm, "end": v(128.23, 17.84) * mm});
            skLineSegment(sketch, "E3245", {"start": v(128.23, 17.84) * mm, "end": v(127.55, 18.2) * mm});
            skLineSegment(sketch, "E3246", {"start": v(127.55, 18.2) * mm, "end": v(127.32, 18.3) * mm});
            skLineSegment(sketch, "E3247", {"start": v(127.32, 18.3) * mm, "end": v(126.9, 18.5) * mm});
            skLineSegment(sketch, "E3248", {"start": v(126.9, 18.5) * mm, "end": v(125.55, 18.93) * mm});
            skLineSegment(sketch, "E3249", {"start": v(125.55, 18.93) * mm, "end": v(123.96, 18.98) * mm});
            skLineSegment(sketch, "E3250", {"start": v(123.96, 18.98) * mm, "end": v(122.44, 18.46) * mm});
            skLineSegment(sketch, "E3251", {"start": v(122.44, 18.46) * mm, "end": v(121.28, 17.66) * mm});
            skLineSegment(sketch, "E3252", {"start": v(121.28, 17.66) * mm, "end": v(120.94, 17.34) * mm});
            skLineSegment(sketch, "E3253", {"start": v(120.94, 17.34) * mm, "end": v(120.78, 17.2) * mm});
            skLineSegment(sketch, "E3254", {"start": v(120.78, 17.2) * mm, "end": v(120.35, 16.74) * mm});
            skLineSegment(sketch, "E3255", {"start": v(120.35, 16.74) * mm, "end": v(119.76, 16.12) * mm});
            skLineSegment(sketch, "E3256", {"start": v(119.76, 16.12) * mm, "end": v(119.08, 15.58) * mm});
            skLineSegment(sketch, "E3257", {"start": v(119.08, 15.58) * mm, "end": v(118.45, 15.26) * mm});
            skLineSegment(sketch, "E3258", {"start": v(118.45, 15.26) * mm, "end": v(118.23, 15.2) * mm});
            skLineSegment(sketch, "E3259", {"start": v(118.23, 15.2) * mm, "end": v(118.4, 15.56) * mm});
            skLineSegment(sketch, "E3260", {"start": v(118.4, 15.56) * mm, "end": v(120.13, 19.11) * mm});
            skLineSegment(sketch, "E3261", {"start": v(120.13, 19.11) * mm, "end": v(120.31, 19.46) * mm});
            skLineSegment(sketch, "E3262", {"start": v(120.31, 19.46) * mm, "end": v(120.47, 19.77) * mm});
            skLineSegment(sketch, "E3263", {"start": v(120.47, 19.77) * mm, "end": v(120.9, 20.7) * mm});
            skLineSegment(sketch, "E3264", {"start": v(120.9, 20.7) * mm, "end": v(121.32, 21.62) * mm});
            skLineSegment(sketch, "E3265", {"start": v(121.32, 21.62) * mm, "end": v(121.65, 22.23) * mm});
            skLineSegment(sketch, "E3266", {"start": v(121.65, 22.23) * mm, "end": v(122, 22.54) * mm});
            skLineSegment(sketch, "E3267", {"start": v(122, 22.54) * mm, "end": v(122.45, 22.59) * mm});
            skLineSegment(sketch, "E3268", {"start": v(122.45, 22.59) * mm, "end": v(123.1, 22.38) * mm});
            skLineSegment(sketch, "E3269", {"start": v(123.1, 22.38) * mm, "end": v(124.04, 21.95) * mm});
            skLineSegment(sketch, "E3270", {"start": v(124.04, 21.95) * mm, "end": v(125.05, 21.46) * mm});
            skLineSegment(sketch, "E3271", {"start": v(125.05, 21.46) * mm, "end": v(125.38, 21.3) * mm});
            skLineSegment(sketch, "E3272", {"start": v(125.38, 21.3) * mm, "end": v(126.7, 20.67) * mm});
            skLineSegment(sketch, "E3273", {"start": v(126.7, 20.67) * mm, "end": v(139.95, 14.23) * mm});
            skLineSegment(sketch, "E3274", {"start": v(139.95, 14.23) * mm, "end": v(141.28, 13.59) * mm});
            skLineSegment(sketch, "E3275", {"start": v(141.28, 13.59) * mm, "end": v(141.39, 13.53) * mm});
            skLineSegment(sketch, "E3276", {"start": v(141.39, 13.53) * mm, "end": v(142.46, 13) * mm});
            skLineSegment(sketch, "E3277", {"start": v(142.46, 13) * mm, "end": v(142.56, 12.94) * mm});
            skLineSegment(sketch, "E3278", {"start": v(142.56, 12.94) * mm, "end": v(142.65, 12.9) * mm});
            skLineSegment(sketch, "E3279", {"start": v(142.65, 12.9) * mm, "end": v(142.96, 12.6) * mm});
            skLineSegment(sketch, "E3280", {"start": v(142.96, 12.6) * mm, "end": v(143.02, 12.22) * mm});
            skLineSegment(sketch, "E3281", {"start": v(143.02, 12.22) * mm, "end": v(142.97, 12.12) * mm});
            skLineSegment(sketch, "E3282", {"start": v(142.97, 12.12) * mm, "end": v(142.7, 11.54) * mm});
            skLineSegment(sketch, "E3283", {"start": v(142.7, 11.54) * mm, "end": v(139.88, 5.77) * mm});
            skLineSegment(sketch, "E3284", {"start": v(139.88, 5.77) * mm, "end": v(139.56, 5.2) * mm});
            skLineSegment(sketch, "E3285", {"start": v(139.56, 5.2) * mm, "end": v(139.44, 5.27) * mm});
            skLineSegment(sketch, "E3286", {"start": v(139.44, 5.27) * mm, "end": v(139.12, 5.55) * mm});
            skLineSegment(sketch, "E3287", {"start": v(139.12, 5.55) * mm, "end": v(138.96, 5.9) * mm});
            skLineSegment(sketch, "E3288", {"start": v(138.96, 5.9) * mm, "end": v(139, 6.25) * mm});
            skLineSegment(sketch, "E3289", {"start": v(139, 6.25) * mm, "end": v(139.06, 6.5) * mm});
            skLineSegment(sketch, "E3290", {"start": v(139.06, 6.5) * mm, "end": v(139.08, 6.57) * mm});
            skLineSegment(sketch, "E3291", {"start": v(139.08, 6.57) * mm, "end": v(139.14, 6.8) * mm});
            skLineSegment(sketch, "E3292", {"start": v(139.14, 6.8) * mm, "end": v(139.4, 9.19) * mm});
            skLineSegment(sketch, "E3293", {"start": v(139.4, 9.19) * mm, "end": v(139.4, 9.43) * mm});
            skLineSegment(sketch, "E3294", {"start": v(139.4, 9.43) * mm, "end": v(139.38, 9.86) * mm});
            skLineSegment(sketch, "E3295", {"start": v(139.38, 9.86) * mm, "end": v(139.04, 11.17) * mm});
            skLineSegment(sketch, "E3296", {"start": v(139.04, 11.17) * mm, "end": v(138.17, 12.65) * mm});
            skLineSegment(sketch, "E3297", {"start": v(138.17, 12.65) * mm, "end": v(136.86, 13.76) * mm});
            skLineSegment(sketch, "E3298", {"start": v(136.86, 13.76) * mm, "end": v(135.64, 14.32) * mm});
            skLineSegment(sketch, "E3299", {"start": v(135.64, 14.32) * mm, "end": v(135.22, 14.4) * mm});
            skLineSegment(sketch, "E3300", {"start": v(135.22, 14.4) * mm, "end": v(135.09, 14.44) * mm});
            skLineSegment(sketch, "E3301", {"start": v(135.09, 14.44) * mm, "end": v(134.61, 14.35) * mm});
            skLineSegment(sketch, "E3302", {"start": v(134.61, 14.35) * mm, "end": v(134.3, 14) * mm});
            skLineSegment(sketch, "E3303", {"start": v(134.3, 14) * mm, "end": v(134.25, 13.9) * mm});
            skLineSegment(sketch, "E3304", {"start": v(134.25, 13.9) * mm, "end": v(134.15, 13.7) * mm});
            skLineSegment(sketch, "E3305", {"start": v(134.15, 13.7) * mm, "end": v(133.18, 11.7) * mm});
            skLineSegment(sketch, "E3306", {"start": v(133.18, 11.7) * mm, "end": v(133.08, 11.5) * mm});
            skLineSegment(sketch, "E3307", {"start": v(133.08, 11.5) * mm, "end": v(132.35, 10) * mm});
            skLineSegment(sketch, "E3308", {"start": v(132.35, 10) * mm, "end": v(125.06, -4.93) * mm});
            skLineSegment(sketch, "E3309", {"start": v(125.06, -4.93) * mm, "end": v(124.33, -6.42) * mm});
            skLineSegment(sketch, "E3310", {"start": v(124.33, -6.42) * mm, "end": v(124.26, -6.58) * mm});
            skLineSegment(sketch, "E3311", {"start": v(124.26, -6.58) * mm, "end": v(123.54, -8.13) * mm});
            skLineSegment(sketch, "E3312", {"start": v(123.54, -8.13) * mm, "end": v(123.48, -8.3) * mm});
            skLineSegment(sketch, "E3313", {"start": v(123.48, -8.3) * mm, "end": v(123.39, -8.53) * mm});
            skLineSegment(sketch, "E3314", {"start": v(123.39, -8.53) * mm, "end": v(123.21, -9.29) * mm});
            skLineSegment(sketch, "E3315", {"start": v(123.21, -9.29) * mm, "end": v(123.26, -10.1) * mm});
            skLineSegment(sketch, "E3316", {"start": v(123.26, -10.1) * mm, "end": v(123.65, -10.81) * mm});
            skLineSegment(sketch, "E3317", {"start": v(123.65, -10.81) * mm, "end": v(124.2, -11.36) * mm});
            skLineSegment(sketch, "E3318", {"start": v(124.2, -11.36) * mm, "end": v(124.4, -11.51) * mm});
            skLineSegment(sketch, "E3319", {"start": v(124.4, -11.51) * mm, "end": v(124.47, -11.56) * mm});
            skLineSegment(sketch, "E3320", {"start": v(124.47, -11.56) * mm, "end": v(125.18, -12.04) * mm});
            skLineSegment(sketch, "E3321", {"start": v(125.18, -12.04) * mm, "end": v(125.24, -12.09) * mm});
            skLineSegment(sketch, "E3322", {"start": v(125.24, -12.09) * mm, "end": v(125.3, -12.13) * mm});
            skLineSegment(sketch, "E3323", {"start": v(125.3, -12.13) * mm, "end": v(125.37, -12.35) * mm});
            skLineSegment(sketch, "E3324", {"start": v(125.37, -12.35) * mm, "end": v(125.28, -12.58) * mm});
            skLineSegment(sketch, "E3325", {"start": v(125.28, -12.58) * mm, "end": v(125.25, -12.62) * mm});
            skLineSegment(sketch, "E3326", {"start": v(125.25, -12.62) * mm, "end": v(125.24, -12.65) * mm});
            skLineSegment(sketch, "E3327", {"start": v(125.24, -12.65) * mm, "end": v(124.93, -12.75) * mm});
            skLineSegment(sketch, "E3328", {"start": v(124.93, -12.75) * mm, "end": v(124.9, -12.75) * mm});
            skLineSegment(sketch, "E3329", {"start": v(124.9, -12.75) * mm, "end": v(124.87, -12.75) * mm});
            skLineSegment(sketch, "E3330", {"start": v(124.87, -12.75) * mm, "end": v(124.54, -12.67) * mm});
            skLineSegment(sketch, "E3331", {"start": v(124.54, -12.67) * mm, "end": v(124.5, -12.66) * mm});
            skLineSegment(sketch, "E3332", {"start": v(124.5, -12.66) * mm, "end": v(123.52, -12.17) * mm});
            skLineSegment(sketch, "E3333", {"start": v(123.52, -12.17) * mm, "end": v(113.48, -7.26) * mm});
            skLineSegment(sketch, "E3334", {"start": v(113.48, -7.26) * mm, "end": v(112.44, -6.76) * mm});
            skLineSegment(sketch, "E3335", {"start": v(101.09, -2.5) * mm, "end": v(100.58, -2.31) * mm});
            skLineSegment(sketch, "E3336", {"start": v(100.58, -2.31) * mm, "end": v(95.56, -0.4) * mm});
            skLineSegment(sketch, "E3337", {"start": v(95.56, -0.4) * mm, "end": v(95.06, -0.22) * mm});
            skLineSegment(sketch, "E3338", {"start": v(95.06, -0.22) * mm, "end": v(94.95, -0.17) * mm});
            skLineSegment(sketch, "E3339", {"start": v(94.95, -0.17) * mm, "end": v(93.86, 0.3) * mm});
            skLineSegment(sketch, "E3340", {"start": v(93.86, 0.3) * mm, "end": v(93.75, 0.35) * mm});
            skLineSegment(sketch, "E3341", {"start": v(93.75, 0.35) * mm, "end": v(93.7, 0.37) * mm});
            skLineSegment(sketch, "E3342", {"start": v(93.7, 0.37) * mm, "end": v(93.54, 0.54) * mm});
            skLineSegment(sketch, "E3343", {"start": v(93.54, 0.54) * mm, "end": v(93.53, 0.8) * mm});
            skLineSegment(sketch, "E3344", {"start": v(93.53, 0.8) * mm, "end": v(93.56, 0.85) * mm});
            skLineSegment(sketch, "E3345", {"start": v(93.56, 0.85) * mm, "end": v(93.59, 0.9) * mm});
            skLineSegment(sketch, "E3346", {"start": v(93.59, 0.9) * mm, "end": v(93.74, 1.08) * mm});
            skLineSegment(sketch, "E3347", {"start": v(93.74, 1.08) * mm, "end": v(93.96, 1.15) * mm});
            skLineSegment(sketch, "E3348", {"start": v(93.96, 1.15) * mm, "end": v(94.02, 1.14) * mm});
            skLineSegment(sketch, "E3349", {"start": v(94.02, 1.14) * mm, "end": v(94.04, 1.14) * mm});
            skLineSegment(sketch, "E3350", {"start": v(94.04, 1.14) * mm, "end": v(94.2, 1.12) * mm});
            skLineSegment(sketch, "E3351", {"start": v(94.2, 1.12) * mm, "end": v(94.23, 1.12) * mm});
            skLineSegment(sketch, "E3352", {"start": v(94.23, 1.12) * mm, "end": v(94.46, 1.09) * mm});
            skLineSegment(sketch, "E3353", {"start": v(94.46, 1.09) * mm, "end": v(95.18, 1) * mm});
            skLineSegment(sketch, "E3354", {"start": v(95.18, 1) * mm, "end": v(95.92, 0.97) * mm});
            skLineSegment(sketch, "E3355", {"start": v(95.92, 0.97) * mm, "end": v(96.5, 1.01) * mm});
            skLineSegment(sketch, "E3356", {"start": v(96.5, 1.01) * mm, "end": v(96.95, 1.18) * mm});
            skLineSegment(sketch, "E3357", {"start": v(96.95, 1.18) * mm, "end": v(97.3, 1.48) * mm});
            skLineSegment(sketch, "E3358", {"start": v(97.3, 1.48) * mm, "end": v(97.62, 1.95) * mm});
            skLineSegment(sketch, "E3359", {"start": v(97.62, 1.95) * mm, "end": v(97.93, 2.61) * mm});
            skLineSegment(sketch, "E3360", {"start": v(97.93, 2.61) * mm, "end": v(98.18, 3.27) * mm});
            skLineSegment(sketch, "E3361", {"start": v(98.18, 3.27) * mm, "end": v(98.26, 3.49) * mm});
            skLineSegment(sketch, "E3362", {"start": v(98.26, 3.49) * mm, "end": v(98.89, 5.2) * mm});
            skLineSegment(sketch, "E3363", {"start": v(98.89, 5.2) * mm, "end": v(105.1, 22.38) * mm});
            skLineSegment(sketch, "E3364", {"start": v(105.1, 22.38) * mm, "end": v(105.71, 24.1) * mm});
            skLineSegment(sketch, "E3365", {"start": v(105.71, 24.1) * mm, "end": v(105.79, 24.3) * mm});
            skLineSegment(sketch, "E3366", {"start": v(105.79, 24.3) * mm, "end": v(106, 24.94) * mm});
            skLineSegment(sketch, "E3367", {"start": v(106, 24.94) * mm, "end": v(106.17, 25.62) * mm});
            skLineSegment(sketch, "E3368", {"start": v(106.17, 25.62) * mm, "end": v(106.21, 26.18) * mm});
            skLineSegment(sketch, "E3369", {"start": v(106.21, 26.18) * mm, "end": v(106.12, 26.64) * mm});
            skLineSegment(sketch, "E3370", {"start": v(106.12, 26.64) * mm, "end": v(105.88, 27.05) * mm});
            skLineSegment(sketch, "E3371", {"start": v(105.88, 27.05) * mm, "end": v(105.48, 27.45) * mm});
            skLineSegment(sketch, "E3372", {"start": v(105.48, 27.45) * mm, "end": v(104.9, 27.87) * mm});
            skLineSegment(sketch, "E3373", {"start": v(104.9, 27.87) * mm, "end": v(104.32, 28.25) * mm});
            skLineSegment(sketch, "E3374", {"start": v(104.32, 28.25) * mm, "end": v(104.13, 28.36) * mm});
            skLineSegment(sketch, "E3375", {"start": v(104.13, 28.36) * mm, "end": v(104.07, 28.4) * mm});
            skLineSegment(sketch, "E3376", {"start": v(104.07, 28.4) * mm, "end": v(103.79, 28.59) * mm});
            skLineSegment(sketch, "E3377", {"start": v(103.79, 28.59) * mm, "end": v(103.67, 28.87) * mm});
            skLineSegment(sketch, "E3378", {"start": v(103.67, 28.87) * mm, "end": v(103.69, 28.95) * mm});
            skLineSegment(sketch, "E3379", {"start": v(103.69, 28.95) * mm, "end": v(103.71, 29.05) * mm});
            skLineSegment(sketch, "E3380", {"start": v(103.71, 29.05) * mm, "end": v(104.02, 29.29) * mm});
            skLineSegment(sketch, "E3381", {"start": v(104.02, 29.29) * mm, "end": v(104.43, 29.26) * mm});
            skLineSegment(sketch, "E3382", {"start": v(104.43, 29.26) * mm, "end": v(104.51, 29.24) * mm});
            skLineSegment(sketch, "E3383", {"start": v(104.51, 29.24) * mm, "end": v(104.78, 29.18) * mm});
            skLineSegment(sketch, "E3384", {"start": v(104.78, 29.18) * mm, "end": v(105.58, 28.9) * mm});
            skLineSegment(sketch, "E3385", {"start": v(105.58, 28.9) * mm, "end": v(106.61, 28.46) * mm});
            skLineSegment(sketch, "E3386", {"start": v(106.61, 28.46) * mm, "end": v(107.65, 28.05) * mm});
            skLineSegment(sketch, "E3387", {"start": v(107.65, 28.05) * mm, "end": v(108.47, 27.84) * mm});
            skLineSegment(sketch, "E3388", {"start": v(108.47, 27.84) * mm, "end": v(108.75, 27.8) * mm});
            skLineSegment(sketch, "E3389", {"start": v(108.75, 27.8) * mm, "end": v(109.25, 27.55) * mm});
            skLineSegment(sketch, "E3390", {"start": v(109.25, 27.55) * mm, "end": v(111.88, 26.54) * mm});
            skLineSegment(sketch, "E3391", {"start": v(111.88, 26.54) * mm, "end": v(114.54, 25.6) * mm});
            skLineSegment(sketch, "E3392", {"start": v(114.54, 25.6) * mm, "end": v(115.06, 25.38) * mm});
            skLineSegment(sketch, "E3393", {"start": v(115.06, 25.38) * mm, "end": v(115.16, 25.34) * mm});
            skLineSegment(sketch, "E3394", {"start": v(115.16, 25.34) * mm, "end": v(115.47, 25.26) * mm});
            skLineSegment(sketch, "E3395", {"start": v(115.47, 25.26) * mm, "end": v(115.9, 25.13) * mm});
            skLineSegment(sketch, "E3396", {"start": v(115.9, 25.13) * mm, "end": v(116.29, 24.9) * mm});
            skLineSegment(sketch, "E3397", {"start": v(116.29, 24.9) * mm, "end": v(116.53, 24.62) * mm});
            skLineSegment(sketch, "E3398", {"start": v(116.53, 24.62) * mm, "end": v(116.57, 24.51) * mm});
            skLineSegment(sketch, "E3399", {"start": v(116.57, 24.51) * mm, "end": v(116.48, 24.43) * mm});
            skLineSegment(sketch, "E3400", {"start": v(116.48, 24.43) * mm, "end": v(116.15, 24.26) * mm});
            skLineSegment(sketch, "E3401", {"start": v(116.15, 24.26) * mm, "end": v(115.75, 24.24) * mm});
            skLineSegment(sketch, "E3402", {"start": v(115.75, 24.24) * mm, "end": v(115.36, 24.32) * mm});
            skLineSegment(sketch, "E3403", {"start": v(115.36, 24.32) * mm, "end": v(115.08, 24.4) * mm});
            skLineSegment(sketch, "E3404", {"start": v(115.08, 24.4) * mm, "end": v(114.98, 24.4) * mm});
            skLineSegment(sketch, "E3405", {"start": v(114.98, 24.4) * mm, "end": v(114.74, 24.43) * mm});
            skLineSegment(sketch, "E3406", {"start": v(114.74, 24.43) * mm, "end": v(114, 24.43) * mm});
            skLineSegment(sketch, "E3407", {"start": v(114, 24.43) * mm, "end": v(113.28, 24.23) * mm});
            skLineSegment(sketch, "E3408", {"start": v(113.28, 24.23) * mm, "end": v(112.7, 23.74) * mm});
            skLineSegment(sketch, "E3409", {"start": v(112.7, 23.74) * mm, "end": v(112.3, 23.12) * mm});
            skLineSegment(sketch, "E3410", {"start": v(112.3, 23.12) * mm, "end": v(112.2, 22.9) * mm});
            skLineSegment(sketch, "E3411", {"start": v(112.2, 22.9) * mm, "end": v(112.11, 22.74) * mm});
            skLineSegment(sketch, "E3412", {"start": v(112.11, 22.74) * mm, "end": v(111.46, 21.16) * mm});
            skLineSegment(sketch, "E3413", {"start": v(111.46, 21.16) * mm, "end": v(111.4, 21) * mm});
            skLineSegment(sketch, "E3414", {"start": v(111.4, 21) * mm, "end": v(110.83, 19.42) * mm});
            skLineSegment(sketch, "E3415", {"start": v(110.83, 19.42) * mm, "end": v(105.12, 3.62) * mm});
            skLineSegment(sketch, "E3416", {"start": v(105.12, 3.62) * mm, "end": v(104.55, 2.04) * mm});
            skLineSegment(sketch, "E3417", {"start": v(104.55, 2.04) * mm, "end": v(104.52, 1.96) * mm});
            skLineSegment(sketch, "E3418", {"start": v(104.52, 1.96) * mm, "end": v(104.26, 1.15) * mm});
            skLineSegment(sketch, "E3419", {"start": v(104.26, 1.15) * mm, "end": v(104.23, 1.07) * mm});
            skLineSegment(sketch, "E3420", {"start": v(104.23, 1.07) * mm, "end": v(104.17, 0.86) * mm});
            skLineSegment(sketch, "E3421", {"start": v(104.17, 0.86) * mm, "end": v(103.99, 0.23) * mm});
            skLineSegment(sketch, "E3422", {"start": v(103.99, 0.23) * mm, "end": v(103.85, -0.45) * mm});
            skLineSegment(sketch, "E3423", {"start": v(103.85, -0.45) * mm, "end": v(103.83, -1.02) * mm});
            skLineSegment(sketch, "E3424", {"start": v(103.83, -1.02) * mm, "end": v(103.94, -1.5) * mm});
            skLineSegment(sketch, "E3425", {"start": v(103.94, -1.5) * mm, "end": v(104.2, -1.93) * mm});
            skLineSegment(sketch, "E3426", {"start": v(104.2, -1.93) * mm, "end": v(104.6, -2.33) * mm});
            skLineSegment(sketch, "E3427", {"start": v(104.6, -2.33) * mm, "end": v(105.18, -2.75) * mm});
            skLineSegment(sketch, "E3428", {"start": v(105.18, -2.75) * mm, "end": v(105.75, -3.1) * mm});
            skLineSegment(sketch, "E3429", {"start": v(105.75, -3.1) * mm, "end": v(105.94, -3.2) * mm});
            skLineSegment(sketch, "E3430", {"start": v(105.94, -3.2) * mm, "end": v(105.99, -3.22) * mm});
            skLineSegment(sketch, "E3431", {"start": v(105.99, -3.22) * mm, "end": v(106.35, -3.48) * mm});
            skLineSegment(sketch, "E3432", {"start": v(106.35, -3.48) * mm, "end": v(106.38, -3.5) * mm});
            skLineSegment(sketch, "E3433", {"start": v(106.38, -3.5) * mm, "end": v(106.35, -3.6) * mm});
            skLineSegment(sketch, "E3434", {"start": v(106.35, -3.6) * mm, "end": v(106.18, -3.89) * mm});
            skLineSegment(sketch, "E3435", {"start": v(106.18, -3.89) * mm, "end": v(105.93, -4.02) * mm});
            skLineSegment(sketch, "E3436", {"start": v(105.93, -4.02) * mm, "end": v(105.66, -4) * mm});
            skLineSegment(sketch, "E3437", {"start": v(105.66, -4) * mm, "end": v(105.44, -3.92) * mm});
            skLineSegment(sketch, "E3438", {"start": v(105.44, -3.92) * mm, "end": v(105.37, -3.9) * mm});
            skLineSegment(sketch, "E3439", {"start": v(105.37, -3.9) * mm, "end": v(105, -3.78) * mm});
            skLineSegment(sketch, "E3440", {"start": v(105, -3.78) * mm, "end": v(103.25, -3.11) * mm});
            skLineSegment(sketch, "E3441", {"start": v(103.25, -3.11) * mm, "end": v(101.46, -2.56) * mm});
            skLineSegment(sketch, "E3442", {"start": v(101.46, -2.56) * mm, "end": v(101.09, -2.5) * mm});
            skLineSegment(sketch, "E3443", {"start": v(-21.65, 32.87) * mm, "end": v(-21.67, 33.17) * mm});
            skLineSegment(sketch, "E3444", {"start": v(-21.67, 33.17) * mm, "end": v(-21.96, 34.96) * mm});
            skLineSegment(sketch, "E3445", {"start": v(-21.96, 34.96) * mm, "end": v(-22.6, 36.92) * mm});
            skLineSegment(sketch, "E3446", {"start": v(-22.6, 36.92) * mm, "end": v(-22.79, 37.32) * mm});
            skLineSegment(sketch, "E3447", {"start": v(-22.79, 37.32) * mm, "end": v(-22.94, 37.63) * mm});
            skLineSegment(sketch, "E3448", {"start": v(-22.94, 37.63) * mm, "end": v(-23.53, 38.49) * mm});
            skLineSegment(sketch, "E3449", {"start": v(-23.53, 38.49) * mm, "end": v(-24.49, 39.34) * mm});
            skLineSegment(sketch, "E3450", {"start": v(-24.49, 39.34) * mm, "end": v(-25.65, 39.85) * mm});
            skLineSegment(sketch, "E3451", {"start": v(-25.65, 39.85) * mm, "end": v(-26.69, 40.02) * mm});
            skLineSegment(sketch, "E3452", {"start": v(-26.69, 40.02) * mm, "end": v(-27.03, 40.01) * mm});
            skLineSegment(sketch, "E3453", {"start": v(-27.03, 40.01) * mm, "end": v(-27.25, 40.01) * mm});
            skLineSegment(sketch, "E3454", {"start": v(-27.25, 40.01) * mm, "end": v(-29.47, 39.82) * mm});
            skLineSegment(sketch, "E3455", {"start": v(-29.47, 39.82) * mm, "end": v(-29.7, 39.8) * mm});
            skLineSegment(sketch, "E3456", {"start": v(-29.7, 39.8) * mm, "end": v(-29.81, 39.79) * mm});
            skLineSegment(sketch, "E3457", {"start": v(-29.81, 39.79) * mm, "end": v(-30.17, 39.7) * mm});
            skLineSegment(sketch, "E3458", {"start": v(-30.17, 39.7) * mm, "end": v(-30.48, 39.47) * mm});
            skLineSegment(sketch, "E3459", {"start": v(-30.48, 39.47) * mm, "end": v(-30.62, 39.1) * mm});
            skLineSegment(sketch, "E3460", {"start": v(-30.62, 39.1) * mm, "end": v(-30.63, 38.7) * mm});
            skLineSegment(sketch, "E3461", {"start": v(-30.63, 38.7) * mm, "end": v(-30.6, 38.57) * mm});
            skLineSegment(sketch, "E3462", {"start": v(-30.6, 38.57) * mm, "end": v(-30.45, 37.71) * mm});
            skLineSegment(sketch, "E3463", {"start": v(-30.45, 37.71) * mm, "end": v(-29.06, 29.1) * mm});
            skLineSegment(sketch, "E3464", {"start": v(-29.06, 29.1) * mm, "end": v(-28.9, 28.23) * mm});
            skLineSegment(sketch, "E3465", {"start": v(-28.9, 28.23) * mm, "end": v(-28.86, 28.06) * mm});
            skLineSegment(sketch, "E3466", {"start": v(-28.86, 28.06) * mm, "end": v(-28.79, 27.56) * mm});
            skLineSegment(sketch, "E3467", {"start": v(-28.79, 27.56) * mm, "end": v(-28.72, 27.05) * mm});
            skLineSegment(sketch, "E3468", {"start": v(-28.72, 27.05) * mm, "end": v(-28.64, 26.7) * mm});
            skLineSegment(sketch, "E3469", {"start": v(-28.64, 26.7) * mm, "end": v(-28.52, 26.5) * mm});
            skLineSegment(sketch, "E3470", {"start": v(-28.52, 26.5) * mm, "end": v(-28.3, 26.41) * mm});
            skLineSegment(sketch, "E3471", {"start": v(-28.3, 26.41) * mm, "end": v(-27.94, 26.43) * mm});
            skLineSegment(sketch, "E3472", {"start": v(-27.94, 26.43) * mm, "end": v(-27.4, 26.52) * mm});
            skLineSegment(sketch, "E3473", {"start": v(-27.4, 26.52) * mm, "end": v(-26.81, 26.64) * mm});
            skLineSegment(sketch, "E3474", {"start": v(-26.81, 26.64) * mm, "end": v(-26.62, 26.68) * mm});
            skLineSegment(sketch, "E3475", {"start": v(-26.62, 26.68) * mm, "end": v(-26.03, 26.8) * mm});
            skLineSegment(sketch, "E3476", {"start": v(-26.03, 26.8) * mm, "end": v(-24.31, 27.4) * mm});
            skLineSegment(sketch, "E3477", {"start": v(-24.31, 27.4) * mm, "end": v(-22.77, 28.6) * mm});
            skLineSegment(sketch, "E3478", {"start": v(-22.77, 28.6) * mm, "end": v(-21.9, 30.37) * mm});
            skLineSegment(sketch, "E3479", {"start": v(-21.9, 30.37) * mm, "end": v(-21.65, 32.25) * mm});
            skLineSegment(sketch, "E3480", {"start": v(-21.65, 32.25) * mm, "end": v(-21.65, 32.87) * mm});
            skLineSegment(sketch, "E3481", {"start": v(-36.27, 34.57) * mm, "end": v(-36.26, 34.8) * mm});
            skLineSegment(sketch, "E3482", {"start": v(-36.26, 34.8) * mm, "end": v(-36.54, 35.9) * mm});
            skLineSegment(sketch, "E3483", {"start": v(-36.54, 35.9) * mm, "end": v(-36.93, 37) * mm});
            skLineSegment(sketch, "E3484", {"start": v(-36.93, 37) * mm, "end": v(-36.98, 37.22) * mm});
            skLineSegment(sketch, "E3485", {"start": v(-36.98, 37.22) * mm, "end": v(-37.02, 37.44) * mm});
            skLineSegment(sketch, "E3486", {"start": v(-37.02, 37.44) * mm, "end": v(-37.3, 38.06) * mm});
            skLineSegment(sketch, "E3487", {"start": v(-37.3, 38.06) * mm, "end": v(-37.87, 38.68) * mm});
            skLineSegment(sketch, "E3488", {"start": v(-37.87, 38.68) * mm, "end": v(-38.68, 39.02) * mm});
            skLineSegment(sketch, "E3489", {"start": v(-38.68, 39.02) * mm, "end": v(-39.47, 39.04) * mm});
            skLineSegment(sketch, "E3490", {"start": v(-39.47, 39.04) * mm, "end": v(-39.71, 38.98) * mm});
            skLineSegment(sketch, "E3491", {"start": v(-39.71, 38.98) * mm, "end": v(-39.8, 38.97) * mm});
            skLineSegment(sketch, "E3492", {"start": v(-39.8, 38.97) * mm, "end": v(-40.21, 38.94) * mm});
            skLineSegment(sketch, "E3493", {"start": v(-40.21, 38.94) * mm, "end": v(-40.53, 39.18) * mm});
            skLineSegment(sketch, "E3494", {"start": v(-40.53, 39.18) * mm, "end": v(-40.55, 39.28) * mm});
            skLineSegment(sketch, "E3495", {"start": v(-40.55, 39.28) * mm, "end": v(-40.58, 39.39) * mm});
            skLineSegment(sketch, "E3496", {"start": v(-40.58, 39.39) * mm, "end": v(-40.42, 39.73) * mm});
            skLineSegment(sketch, "E3497", {"start": v(-40.42, 39.73) * mm, "end": v(-40.03, 39.88) * mm});
            skLineSegment(sketch, "E3498", {"start": v(-40.03, 39.88) * mm, "end": v(-39.94, 39.9) * mm});
            skLineSegment(sketch, "E3499", {"start": v(-39.94, 39.9) * mm, "end": v(-38.62, 40.08) * mm});
            skLineSegment(sketch, "E3500", {"start": v(-38.62, 40.08) * mm, "end": v(-32.05, 41.18) * mm});
            skLineSegment(sketch, "E3501", {"start": v(-32.05, 41.18) * mm, "end": v(-25.46, 42.1) * mm});
            skLineSegment(sketch, "E3502", {"start": v(-25.46, 42.1) * mm, "end": v(-24.13, 42.18) * mm});
            skLineSegment(sketch, "E3503", {"start": v(-24.13, 42.18) * mm, "end": v(-23.9, 42.2) * mm});
            skLineSegment(sketch, "E3504", {"start": v(-23.9, 42.2) * mm, "end": v(-21.5, 42.05) * mm});
            skLineSegment(sketch, "E3505", {"start": v(-21.5, 42.05) * mm, "end": v(-21.27, 42.04) * mm});
            skLineSegment(sketch, "E3506", {"start": v(-21.27, 42.04) * mm, "end": v(-20.6, 41.8) * mm});
            skLineSegment(sketch, "E3507", {"start": v(-20.6, 41.8) * mm, "end": v(-18.74, 40.72) * mm});
            skLineSegment(sketch, "E3508", {"start": v(-18.74, 40.72) * mm, "end": v(-16.93, 38.89) * mm});
            skLineSegment(sketch, "E3509", {"start": v(-16.93, 38.89) * mm, "end": v(-15.83, 36.56) * mm});
            skLineSegment(sketch, "E3510", {"start": v(-15.83, 36.56) * mm, "end": v(-15.43, 34.45) * mm});
            skLineSegment(sketch, "E3511", {"start": v(-15.43, 34.45) * mm, "end": v(-15.4, 33.75) * mm});
            skLineSegment(sketch, "E3512", {"start": v(-15.4, 33.75) * mm, "end": v(-15.4, 33.25) * mm});
            skLineSegment(sketch, "E3513", {"start": v(-15.4, 33.25) * mm, "end": v(-15.58, 31.74) * mm});
            skLineSegment(sketch, "E3514", {"start": v(-15.58, 31.74) * mm, "end": v(-16.2, 29.97) * mm});
            skLineSegment(sketch, "E3515", {"start": v(-16.2, 29.97) * mm, "end": v(-17.3, 28.45) * mm});
            skLineSegment(sketch, "E3516", {"start": v(-17.3, 28.45) * mm, "end": v(-18.45, 27.44) * mm});
            skLineSegment(sketch, "E3517", {"start": v(-18.45, 27.44) * mm, "end": v(-18.87, 27.17) * mm});
            skLineSegment(sketch, "E3518", {"start": v(-18.87, 27.17) * mm, "end": v(-18.94, 27.12) * mm});
            skLineSegment(sketch, "E3519", {"start": v(-18.94, 27.12) * mm, "end": v(-19.64, 26.65) * mm});
            skLineSegment(sketch, "E3520", {"start": v(-19.64, 26.65) * mm, "end": v(-19.71, 26.6) * mm});
            skLineSegment(sketch, "E3521", {"start": v(-19.71, 26.6) * mm, "end": v(-19.7, 26.43) * mm});
            skLineSegment(sketch, "E3522", {"start": v(-19.7, 26.43) * mm, "end": v(-19.32, 25.75) * mm});
            skLineSegment(sketch, "E3523", {"start": v(-19.32, 25.75) * mm, "end": v(-18.8, 25.19) * mm});
            skLineSegment(sketch, "E3524", {"start": v(-18.8, 25.19) * mm, "end": v(-18.7, 25.08) * mm});
            skLineSegment(sketch, "E3525", {"start": v(-18.7, 25.08) * mm, "end": v(-18.08, 24.33) * mm});
            skLineSegment(sketch, "E3526", {"start": v(-18.08, 24.33) * mm, "end": v(-11.74, 16.89) * mm});
            skLineSegment(sketch, "E3527", {"start": v(-11.74, 16.89) * mm, "end": v(-11.1, 16.14) * mm});
            skLineSegment(sketch, "E3528", {"start": v(-11.1, 16.14) * mm, "end": v(-10.88, 15.88) * mm});
            skLineSegment(sketch, "E3529", {"start": v(-10.88, 15.88) * mm, "end": v(-10.1, 15.2) * mm});
            skLineSegment(sketch, "E3530", {"start": v(-10.1, 15.2) * mm, "end": v(-8.96, 14.6) * mm});
            skLineSegment(sketch, "E3531", {"start": v(-8.96, 14.6) * mm, "end": v(-7.7, 14.35) * mm});
            skLineSegment(sketch, "E3532", {"start": v(-7.7, 14.35) * mm, "end": v(-6.66, 14.38) * mm});
            skLineSegment(sketch, "E3533", {"start": v(-6.66, 14.38) * mm, "end": v(-6.33, 14.44) * mm});
            skLineSegment(sketch, "E3534", {"start": v(-6.33, 14.44) * mm, "end": v(-6.04, 14.5) * mm});
            skLineSegment(sketch, "E3535", {"start": v(-6.04, 14.5) * mm, "end": v(-5.2, 14.76) * mm});
            skLineSegment(sketch, "E3536", {"start": v(-5.2, 14.76) * mm, "end": v(-4.47, 15.27) * mm});
            skLineSegment(sketch, "E3537", {"start": v(-4.47, 15.27) * mm, "end": v(-4.07, 16.05) * mm});
            skLineSegment(sketch, "E3538", {"start": v(-4.07, 16.05) * mm, "end": v(-3.94, 16.92) * mm});
            skLineSegment(sketch, "E3539", {"start": v(-3.94, 16.92) * mm, "end": v(-3.94, 17.2) * mm});
            skLineSegment(sketch, "E3540", {"start": v(-3.94, 17.2) * mm, "end": v(-3.93, 17.98) * mm});
            skLineSegment(sketch, "E3541", {"start": v(-3.93, 17.98) * mm, "end": v(-4, 25.7) * mm});
            skLineSegment(sketch, "E3542", {"start": v(-4, 25.7) * mm, "end": v(-4.03, 26.47) * mm});
            skLineSegment(sketch, "E3543", {"start": v(-4.03, 26.47) * mm, "end": v(-4.05, 27.6) * mm});
            skLineSegment(sketch, "E3544", {"start": v(-4.05, 27.6) * mm, "end": v(-4.33, 38.9) * mm});
            skLineSegment(sketch, "E3545", {"start": v(-4.33, 38.9) * mm, "end": v(-4.36, 40.04) * mm});
            skLineSegment(sketch, "E3546", {"start": v(-4.36, 40.04) * mm, "end": v(-4.37, 40.26) * mm});
            skLineSegment(sketch, "E3547", {"start": v(-4.37, 40.26) * mm, "end": v(-4.4, 40.93) * mm});
            skLineSegment(sketch, "E3548", {"start": v(-4.4, 40.93) * mm, "end": v(-4.5, 41.64) * mm});
            skLineSegment(sketch, "E3549", {"start": v(-4.5, 41.64) * mm, "end": v(-4.65, 42.2) * mm});
            skLineSegment(sketch, "E3550", {"start": v(-4.65, 42.2) * mm, "end": v(-4.9, 42.62) * mm});
            skLineSegment(sketch, "E3551", {"start": v(-4.9, 42.62) * mm, "end": v(-5.28, 42.93) * mm});
            skLineSegment(sketch, "E3552", {"start": v(-5.28, 42.93) * mm, "end": v(-5.8, 43.17) * mm});
            skLineSegment(sketch, "E3553", {"start": v(-5.8, 43.17) * mm, "end": v(-6.47, 43.37) * mm});
            skLineSegment(sketch, "E3554", {"start": v(-6.47, 43.37) * mm, "end": v(-7.11, 43.5) * mm});
            skLineSegment(sketch, "E3555", {"start": v(-7.11, 43.5) * mm, "end": v(-7.33, 43.54) * mm});
            skLineSegment(sketch, "E3556", {"start": v(-7.33, 43.54) * mm, "end": v(-7.39, 43.55) * mm});
            skLineSegment(sketch, "E3557", {"start": v(-7.39, 43.55) * mm, "end": v(-7.57, 43.57) * mm});
            skLineSegment(sketch, "E3558", {"start": v(-7.57, 43.57) * mm, "end": v(-7.8, 43.62) * mm});
            skLineSegment(sketch, "E3559", {"start": v(-7.8, 43.62) * mm, "end": v(-7.96, 43.75) * mm});
            skLineSegment(sketch, "E3560", {"start": v(-7.96, 43.75) * mm, "end": v(-8, 43.98) * mm});
            skLineSegment(sketch, "E3561", {"start": v(-8, 43.98) * mm, "end": v(-8, 44.04) * mm});
            skLineSegment(sketch, "E3562", {"start": v(-8, 44.04) * mm, "end": v(-7.99, 44.13) * mm});
            skLineSegment(sketch, "E3563", {"start": v(-7.99, 44.13) * mm, "end": v(-7.76, 44.36) * mm});
            skLineSegment(sketch, "E3564", {"start": v(-7.76, 44.36) * mm, "end": v(-7.43, 44.4) * mm});
            skLineSegment(sketch, "E3565", {"start": v(-7.43, 44.4) * mm, "end": v(-7.37, 44.4) * mm});
            skLineSegment(sketch, "E3566", {"start": v(-7.37, 44.4) * mm, "end": v(-7.18, 44.4) * mm});
            skLineSegment(sketch, "E3567", {"start": v(-7.18, 44.4) * mm, "end": v(-5.3, 44.44) * mm});
            skLineSegment(sketch, "E3568", {"start": v(-5.3, 44.44) * mm, "end": v(-5.1, 44.44) * mm});
            skLineSegment(sketch, "E3569", {"start": v(-5.1, 44.44) * mm, "end": v(-3.66, 44.47) * mm});
            skLineSegment(sketch, "E3570", {"start": v(-3.66, 44.47) * mm, "end": v(10.73, 44.8) * mm});
            skLineSegment(sketch, "E3571", {"start": v(10.73, 44.8) * mm, "end": v(12.17, 44.84) * mm});
            skLineSegment(sketch, "E3572", {"start": v(12.17, 44.84) * mm, "end": v(12.41, 44.85) * mm});
            skLineSegment(sketch, "E3573", {"start": v(12.41, 44.85) * mm, "end": v(13.14, 44.84) * mm});
            skLineSegment(sketch, "E3574", {"start": v(13.14, 44.84) * mm, "end": v(13.64, 44.67) * mm});
            skLineSegment(sketch, "E3575", {"start": v(13.64, 44.67) * mm, "end": v(13.82, 44.17) * mm});
            skLineSegment(sketch, "E3576", {"start": v(13.82, 44.17) * mm, "end": v(13.85, 43.42) * mm});
            skLineSegment(sketch, "E3577", {"start": v(13.85, 43.42) * mm, "end": v(13.85, 43.16) * mm});
            skLineSegment(sketch, "E3578", {"start": v(13.85, 43.16) * mm, "end": v(13.86, 42.67) * mm});
            skLineSegment(sketch, "E3579", {"start": v(13.86, 42.67) * mm, "end": v(14.03, 37.7) * mm});
            skLineSegment(sketch, "E3580", {"start": v(14.03, 37.7) * mm, "end": v(14.04, 37.2) * mm});
            skLineSegment(sketch, "E3581", {"start": v(14.04, 37.2) * mm, "end": v(14.05, 37.1) * mm});
            skLineSegment(sketch, "E3582", {"start": v(14.05, 37.1) * mm, "end": v(14.09, 36.51) * mm});
            skLineSegment(sketch, "E3583", {"start": v(14.09, 36.51) * mm, "end": v(13.93, 35.95) * mm});
            skLineSegment(sketch, "E3584", {"start": v(13.93, 35.95) * mm, "end": v(13.83, 35.85) * mm});
            skLineSegment(sketch, "E3585", {"start": v(13.83, 35.85) * mm, "end": v(13.75, 35.83) * mm});
            skLineSegment(sketch, "E3586", {"start": v(13.75, 35.83) * mm, "end": v(13.47, 35.84) * mm});
            skLineSegment(sketch, "E3587", {"start": v(13.47, 35.84) * mm, "end": v(13.26, 35.98) * mm});
            skLineSegment(sketch, "E3588", {"start": v(13.26, 35.98) * mm, "end": v(13.13, 36.23) * mm});
            skLineSegment(sketch, "E3589", {"start": v(13.13, 36.23) * mm, "end": v(13.06, 36.45) * mm});
            skLineSegment(sketch, "E3590", {"start": v(13.06, 36.45) * mm, "end": v(13.04, 36.52) * mm});
            skLineSegment(sketch, "E3591", {"start": v(13.04, 36.52) * mm, "end": v(13, 36.65) * mm});
            skLineSegment(sketch, "E3592", {"start": v(13, 36.65) * mm, "end": v(12.65, 37.97) * mm});
            skLineSegment(sketch, "E3593", {"start": v(12.65, 37.97) * mm, "end": v(12.61, 38.1) * mm});
            skLineSegment(sketch, "E3594", {"start": v(12.61, 38.1) * mm, "end": v(12.44, 38.64) * mm});
            skLineSegment(sketch, "E3595", {"start": v(12.44, 38.64) * mm, "end": v(11.68, 40.18) * mm});
            skLineSegment(sketch, "E3596", {"start": v(11.68, 40.18) * mm, "end": v(10.38, 41.62) * mm});
            skLineSegment(sketch, "E3597", {"start": v(10.38, 41.62) * mm, "end": v(8.66, 42.48) * mm});
            skLineSegment(sketch, "E3598", {"start": v(8.66, 42.48) * mm, "end": v(7, 42.79) * mm});
            skLineSegment(sketch, "E3599", {"start": v(7, 42.79) * mm, "end": v(6.44, 42.8) * mm});
            skLineSegment(sketch, "E3600", {"start": v(6.44, 42.8) * mm, "end": v(6.17, 42.8) * mm});
            skLineSegment(sketch, "E3601", {"start": v(6.17, 42.8) * mm, "end": v(3.42, 42.78) * mm});
            skLineSegment(sketch, "E3602", {"start": v(3.42, 42.78) * mm, "end": v(3.15, 42.8) * mm});
            skLineSegment(sketch, "E3603", {"start": v(3.15, 42.8) * mm, "end": v(3.01, 42.8) * mm});
            skLineSegment(sketch, "E3604", {"start": v(3.01, 42.8) * mm, "end": v(2.6, 42.76) * mm});
            skLineSegment(sketch, "E3605", {"start": v(2.6, 42.76) * mm, "end": v(2.21, 42.58) * mm});
            skLineSegment(sketch, "E3606", {"start": v(2.21, 42.58) * mm, "end": v(2, 42.21) * mm});
            skLineSegment(sketch, "E3607", {"start": v(2, 42.21) * mm, "end": v(1.93, 41.78) * mm});
            skLineSegment(sketch, "E3608", {"start": v(1.93, 41.78) * mm, "end": v(1.94, 41.64) * mm});
            skLineSegment(sketch, "E3609", {"start": v(1.94, 41.64) * mm, "end": v(1.97, 40.76) * mm});
            skLineSegment(sketch, "E3610", {"start": v(1.97, 40.76) * mm, "end": v(2.18, 32.02) * mm});
            skLineSegment(sketch, "E3611", {"start": v(2.18, 32.02) * mm, "end": v(2.2, 31.15) * mm});
            skLineSegment(sketch, "E3612", {"start": v(2.2, 31.15) * mm, "end": v(2.2, 31) * mm});
            skLineSegment(sketch, "E3613", {"start": v(2.2, 31) * mm, "end": v(2.42, 30.5) * mm});
            skLineSegment(sketch, "E3614", {"start": v(2.42, 30.5) * mm, "end": v(2.93, 30.35) * mm});
            skLineSegment(sketch, "E3615", {"start": v(2.93, 30.35) * mm, "end": v(3.08, 30.36) * mm});
            skLineSegment(sketch, "E3616", {"start": v(3.08, 30.36) * mm, "end": v(3.36, 30.38) * mm});
            skLineSegment(sketch, "E3617", {"start": v(3.36, 30.38) * mm, "end": v(4.18, 30.56) * mm});
            skLineSegment(sketch, "E3618", {"start": v(4.18, 30.56) * mm, "end": v(5.1, 31.01) * mm});
            skLineSegment(sketch, "E3619", {"start": v(5.1, 31.01) * mm, "end": v(5.86, 31.71) * mm});
            skLineSegment(sketch, "E3620", {"start": v(5.86, 31.71) * mm, "end": v(6.34, 32.4) * mm});
            skLineSegment(sketch, "E3621", {"start": v(6.34, 32.4) * mm, "end": v(6.46, 32.66) * mm});
            skLineSegment(sketch, "E3622", {"start": v(6.46, 32.66) * mm, "end": v(6.6, 32.96) * mm});
            skLineSegment(sketch, "E3623", {"start": v(6.6, 32.96) * mm, "end": v(7.08, 34.5) * mm});
            skLineSegment(sketch, "E3624", {"start": v(7.08, 34.5) * mm, "end": v(7.4, 36.1) * mm});
            skLineSegment(sketch, "E3625", {"start": v(7.4, 36.1) * mm, "end": v(7.48, 36.41) * mm});
            skLineSegment(sketch, "E3626", {"start": v(7.48, 36.41) * mm, "end": v(7.5, 36.5) * mm});
            skLineSegment(sketch, "E3627", {"start": v(7.5, 36.5) * mm, "end": v(7.5, 36.75) * mm});
            skLineSegment(sketch, "E3628", {"start": v(7.5, 36.75) * mm, "end": v(7.52, 37.1) * mm});
            skLineSegment(sketch, "E3629", {"start": v(7.52, 37.1) * mm, "end": v(7.64, 37.4) * mm});
            skLineSegment(sketch, "E3630", {"start": v(7.64, 37.4) * mm, "end": v(7.87, 37.6) * mm});
            skLineSegment(sketch, "E3631", {"start": v(7.87, 37.6) * mm, "end": v(7.96, 37.62) * mm});
            skLineSegment(sketch, "E3632", {"start": v(7.96, 37.62) * mm, "end": v(8.06, 37.4) * mm});
            skLineSegment(sketch, "E3633", {"start": v(8.06, 37.4) * mm, "end": v(8.15, 36.6) * mm});
            skLineSegment(sketch, "E3634", {"start": v(8.15, 36.6) * mm, "end": v(8.32, 34.74) * mm});
            skLineSegment(sketch, "E3635", {"start": v(8.32, 34.74) * mm, "end": v(8.44, 32.3) * mm});
            skLineSegment(sketch, "E3636", {"start": v(8.44, 32.3) * mm, "end": v(8.53, 29.59) * mm});
            skLineSegment(sketch, "E3637", {"start": v(8.53, 29.59) * mm, "end": v(8.57, 26.86) * mm});
            skLineSegment(sketch, "E3638", {"start": v(8.57, 26.86) * mm, "end": v(8.55, 24.42) * mm});
            skLineSegment(sketch, "E3639", {"start": v(8.55, 24.42) * mm, "end": v(8.47, 22.55) * mm});
            skLineSegment(sketch, "E3640", {"start": v(8.47, 22.55) * mm, "end": v(8.4, 21.76) * mm});
            skLineSegment(sketch, "E3641", {"start": v(8.4, 21.76) * mm, "end": v(8.32, 21.52) * mm});
            skLineSegment(sketch, "E3642", {"start": v(8.32, 21.52) * mm, "end": v(8.22, 21.56) * mm});
            skLineSegment(sketch, "E3643", {"start": v(8.22, 21.56) * mm, "end": v(7.95, 21.77) * mm});
            skLineSegment(sketch, "E3644", {"start": v(7.95, 21.77) * mm, "end": v(7.78, 22.12) * mm});
            skLineSegment(sketch, "E3645", {"start": v(7.78, 22.12) * mm, "end": v(7.72, 22.5) * mm});
            skLineSegment(sketch, "E3646", {"start": v(7.72, 22.5) * mm, "end": v(7.7, 22.8) * mm});
            skLineSegment(sketch, "E3647", {"start": v(7.7, 22.8) * mm, "end": v(7.68, 22.88) * mm});
            skLineSegment(sketch, "E3648", {"start": v(7.68, 22.88) * mm, "end": v(7.64, 23.16) * mm});
            skLineSegment(sketch, "E3649", {"start": v(7.64, 23.16) * mm, "end": v(7.31, 24.49) * mm});
            skLineSegment(sketch, "E3650", {"start": v(7.31, 24.49) * mm, "end": v(6.83, 25.77) * mm});
            skLineSegment(sketch, "E3651", {"start": v(6.83, 25.77) * mm, "end": v(6.71, 26.01) * mm});
            skLineSegment(sketch, "E3652", {"start": v(6.71, 26.01) * mm, "end": v(6.55, 26.33) * mm});
            skLineSegment(sketch, "E3653", {"start": v(6.55, 26.33) * mm, "end": v(5.97, 27.22) * mm});
            skLineSegment(sketch, "E3654", {"start": v(5.97, 27.22) * mm, "end": v(5.08, 27.95) * mm});
            skLineSegment(sketch, "E3655", {"start": v(5.08, 27.95) * mm, "end": v(3.9, 28.3) * mm});
            skLineSegment(sketch, "E3656", {"start": v(3.9, 28.3) * mm, "end": v(2.69, 28.35) * mm});
            skLineSegment(sketch, "E3657", {"start": v(2.69, 28.35) * mm, "end": v(2.29, 28.33) * mm});
            skLineSegment(sketch, "E3658", {"start": v(2.29, 28.33) * mm, "end": v(2.28, 27.4) * mm});
            skLineSegment(sketch, "E3659", {"start": v(2.28, 27.4) * mm, "end": v(2.55, 18.19) * mm});
            skLineSegment(sketch, "E3660", {"start": v(2.55, 18.19) * mm, "end": v(2.63, 17.27) * mm});
            skLineSegment(sketch, "E3661", {"start": v(2.63, 17.27) * mm, "end": v(2.64, 17.1) * mm});
            skLineSegment(sketch, "E3662", {"start": v(2.64, 17.1) * mm, "end": v(2.8, 16.58) * mm});
            skLineSegment(sketch, "E3663", {"start": v(2.8, 16.58) * mm, "end": v(3.15, 16.07) * mm});
            skLineSegment(sketch, "E3664", {"start": v(3.15, 16.07) * mm, "end": v(3.7, 15.74) * mm});
            skLineSegment(sketch, "E3665", {"start": v(3.7, 15.74) * mm, "end": v(4.22, 15.62) * mm});
            skLineSegment(sketch, "E3666", {"start": v(4.22, 15.62) * mm, "end": v(4.4, 15.61) * mm});
            skLineSegment(sketch, "E3667", {"start": v(4.4, 15.61) * mm, "end": v(4.74, 15.6) * mm});
            skLineSegment(sketch, "E3668", {"start": v(4.74, 15.6) * mm, "end": v(6.45, 15.58) * mm});
            skLineSegment(sketch, "E3669", {"start": v(6.45, 15.58) * mm, "end": v(8.15, 15.73) * mm});
            skLineSegment(sketch, "E3670", {"start": v(8.15, 15.73) * mm, "end": v(8.5, 15.8) * mm});
            skLineSegment(sketch, "E3671", {"start": v(8.5, 15.8) * mm, "end": v(9.08, 15.91) * mm});
            skLineSegment(sketch, "E3672", {"start": v(9.08, 15.91) * mm, "end": v(10.77, 16.6) * mm});
            skLineSegment(sketch, "E3673", {"start": v(10.77, 16.6) * mm, "end": v(12.54, 17.92) * mm});
            skLineSegment(sketch, "E3674", {"start": v(12.54, 17.92) * mm, "end": v(13.88, 19.7) * mm});
            skLineSegment(sketch, "E3675", {"start": v(13.88, 19.7) * mm, "end": v(14.67, 21.3) * mm});
            skLineSegment(sketch, "E3676", {"start": v(14.67, 21.3) * mm, "end": v(14.86, 21.86) * mm});
            skLineSegment(sketch, "E3677", {"start": v(14.86, 21.86) * mm, "end": v(14.9, 22) * mm});
            skLineSegment(sketch, "E3678", {"start": v(14.9, 22) * mm, "end": v(15, 22.38) * mm});
            skLineSegment(sketch, "E3679", {"start": v(15, 22.38) * mm, "end": v(15.12, 22.91) * mm});
            skLineSegment(sketch, "E3680", {"start": v(15.12, 22.91) * mm, "end": v(15.33, 23.4) * mm});
            skLineSegment(sketch, "E3681", {"start": v(15.33, 23.4) * mm, "end": v(15.6, 23.73) * mm});
            skLineSegment(sketch, "E3682", {"start": v(15.6, 23.73) * mm, "end": v(15.71, 23.8) * mm});
            skLineSegment(sketch, "E3683", {"start": v(15.71, 23.8) * mm, "end": v(15.8, 23.77) * mm});
            skLineSegment(sketch, "E3684", {"start": v(15.8, 23.77) * mm, "end": v(16.05, 23.58) * mm});
            skLineSegment(sketch, "E3685", {"start": v(16.05, 23.58) * mm, "end": v(16.16, 23.31) * mm});
            skLineSegment(sketch, "E3686", {"start": v(16.16, 23.31) * mm, "end": v(16.15, 23.02) * mm});
            skLineSegment(sketch, "E3687", {"start": v(16.15, 23.02) * mm, "end": v(16.1, 22.81) * mm});
            skLineSegment(sketch, "E3688", {"start": v(16.1, 22.81) * mm, "end": v(16.1, 22.74) * mm});
            skLineSegment(sketch, "E3689", {"start": v(16.1, 22.74) * mm, "end": v(16.05, 22.16) * mm});
            skLineSegment(sketch, "E3690", {"start": v(16.05, 22.16) * mm, "end": v(15.46, 16.37) * mm});
            skLineSegment(sketch, "E3691", {"start": v(15.46, 16.37) * mm, "end": v(15.4, 15.78) * mm});
            skLineSegment(sketch, "E3692", {"start": v(15.4, 15.78) * mm, "end": v(15.38, 15.52) * mm});
            skLineSegment(sketch, "E3693", {"start": v(15.38, 15.52) * mm, "end": v(15.29, 14.74) * mm});
            skLineSegment(sketch, "E3694", {"start": v(15.29, 14.74) * mm, "end": v(15.05, 14.2) * mm});
            skLineSegment(sketch, "E3695", {"start": v(15.05, 14.2) * mm, "end": v(14.52, 14) * mm});
            skLineSegment(sketch, "E3696", {"start": v(14.52, 14) * mm, "end": v(13.77, 13.95) * mm});
            skLineSegment(sketch, "E3697", {"start": v(13.77, 13.95) * mm, "end": v(13.51, 13.94) * mm});
            skLineSegment(sketch, "E3698", {"start": v(13.51, 13.94) * mm, "end": v(12.16, 13.91) * mm});
            skLineSegment(sketch, "E3699", {"start": v(12.16, 13.91) * mm, "end": v(-1.38, 13.61) * mm});
            skLineSegment(sketch, "E3700", {"start": v(-1.38, 13.61) * mm, "end": v(-2.73, 13.56) * mm});
            skLineSegment(sketch, "E3701", {"start": v(-2.73, 13.56) * mm, "end": v(-3.25, 13.55) * mm});
            skLineSegment(sketch, "E3702", {"start": v(-3.25, 13.55) * mm, "end": v(-5.83, 13.64) * mm});
            skLineSegment(sketch, "E3703", {"start": v(-5.83, 13.64) * mm, "end": v(-8.4, 13.63) * mm});
            skLineSegment(sketch, "E3704", {"start": v(-8.4, 13.63) * mm, "end": v(-8.91, 13.55) * mm});
            skLineSegment(sketch, "E3705", {"start": v(-8.91, 13.55) * mm, "end": v(-9.42, 13.47) * mm});
            skLineSegment(sketch, "E3706", {"start": v(-9.42, 13.47) * mm, "end": v(-14.5, 12.68) * mm});
            skLineSegment(sketch, "E3707", {"start": v(-14.5, 12.68) * mm, "end": v(-15, 12.58) * mm});
            skLineSegment(sketch, "E3708", {"start": v(-15, 12.58) * mm, "end": v(-15.17, 12.54) * mm});
            skLineSegment(sketch, "E3709", {"start": v(-15.17, 12.54) * mm, "end": v(-15.68, 12.51) * mm});
            skLineSegment(sketch, "E3710", {"start": v(-15.68, 12.51) * mm, "end": v(-16.23, 12.64) * mm});
            skLineSegment(sketch, "E3711", {"start": v(-16.23, 12.64) * mm, "end": v(-16.7, 12.95) * mm});
            skLineSegment(sketch, "E3712", {"start": v(-16.7, 12.95) * mm, "end": v(-17.07, 13.32) * mm});
            skLineSegment(sketch, "E3713", {"start": v(-17.07, 13.32) * mm, "end": v(-17.17, 13.45) * mm});
            skLineSegment(sketch, "E3714", {"start": v(-17.17, 13.45) * mm, "end": v(-17.89, 14.35) * mm});
            skLineSegment(sketch, "E3715", {"start": v(-17.89, 14.35) * mm, "end": v(-25.2, 23.2) * mm});
            skLineSegment(sketch, "E3716", {"start": v(-25.2, 23.2) * mm, "end": v(-25.94, 24.07) * mm});
            skLineSegment(sketch, "E3717", {"start": v(-25.94, 24.07) * mm, "end": v(-26, 24.14) * mm});
            skLineSegment(sketch, "E3718", {"start": v(-26, 24.14) * mm, "end": v(-26.62, 24.72) * mm});
            skLineSegment(sketch, "E3719", {"start": v(-26.62, 24.72) * mm, "end": v(-26.69, 24.75) * mm});
            skLineSegment(sketch, "E3720", {"start": v(-26.69, 24.75) * mm, "end": v(-26.83, 24.82) * mm});
            skLineSegment(sketch, "E3721", {"start": v(-26.83, 24.82) * mm, "end": v(-27.3, 24.88) * mm});
            skLineSegment(sketch, "E3722", {"start": v(-27.3, 24.88) * mm, "end": v(-27.8, 24.7) * mm});
            skLineSegment(sketch, "E3723", {"start": v(-27.8, 24.7) * mm, "end": v(-28.12, 24.25) * mm});
            skLineSegment(sketch, "E3724", {"start": v(-28.12, 24.25) * mm, "end": v(-28.2, 23.78) * mm});
            skLineSegment(sketch, "E3725", {"start": v(-28.2, 23.78) * mm, "end": v(-28.17, 23.63) * mm});
            skLineSegment(sketch, "E3726", {"start": v(-28.17, 23.63) * mm, "end": v(-28.05, 22.88) * mm});
            skLineSegment(sketch, "E3727", {"start": v(-28.05, 22.88) * mm, "end": v(-26.8, 15.46) * mm});
            skLineSegment(sketch, "E3728", {"start": v(-26.8, 15.46) * mm, "end": v(-26.66, 14.72) * mm});
            skLineSegment(sketch, "E3729", {"start": v(-26.66, 14.72) * mm, "end": v(-26.62, 14.53) * mm});
            skLineSegment(sketch, "E3730", {"start": v(-26.62, 14.53) * mm, "end": v(-26.5, 13.96) * mm});
            skLineSegment(sketch, "E3731", {"start": v(-26.5, 13.96) * mm, "end": v(-26.31, 13.38) * mm});
            skLineSegment(sketch, "E3732", {"start": v(-26.31, 13.38) * mm, "end": v(-26.09, 12.94) * mm});
            skLineSegment(sketch, "E3733", {"start": v(-26.09, 12.94) * mm, "end": v(-25.8, 12.63) * mm});
            skLineSegment(sketch, "E3734", {"start": v(-25.8, 12.63) * mm, "end": v(-25.4, 12.42) * mm});
            skLineSegment(sketch, "E3735", {"start": v(-25.4, 12.42) * mm, "end": v(-24.9, 12.3) * mm});
            skLineSegment(sketch, "E3736", {"start": v(-24.9, 12.3) * mm, "end": v(-24.26, 12.23) * mm});
            skLineSegment(sketch, "E3737", {"start": v(-24.26, 12.23) * mm, "end": v(-23.66, 12.2) * mm});
            skLineSegment(sketch, "E3738", {"start": v(-23.66, 12.2) * mm, "end": v(-23.46, 12.2) * mm});
            skLineSegment(sketch, "E3739", {"start": v(-23.46, 12.2) * mm, "end": v(-23.37, 12.2) * mm});
            skLineSegment(sketch, "E3740", {"start": v(-23.37, 12.2) * mm, "end": v(-22.97, 12.18) * mm});
            skLineSegment(sketch, "E3741", {"start": v(-22.97, 12.18) * mm, "end": v(-22.65, 11.94) * mm});
            skLineSegment(sketch, "E3742", {"start": v(-22.65, 11.94) * mm, "end": v(-22.62, 11.83) * mm});
            skLineSegment(sketch, "E3743", {"start": v(-22.62, 11.83) * mm, "end": v(-22.63, 11.75) * mm});
            skLineSegment(sketch, "E3744", {"start": v(-22.63, 11.75) * mm, "end": v(-22.73, 11.5) * mm});
            skLineSegment(sketch, "E3745", {"start": v(-22.73, 11.5) * mm, "end": v(-22.96, 11.33) * mm});
            skLineSegment(sketch, "E3746", {"start": v(-22.96, 11.33) * mm, "end": v(-23.24, 11.24) * mm});
            skLineSegment(sketch, "E3747", {"start": v(-23.24, 11.24) * mm, "end": v(-23.46, 11.21) * mm});
            skLineSegment(sketch, "E3748", {"start": v(-23.46, 11.21) * mm, "end": v(-23.53, 11.2) * mm});
            skLineSegment(sketch, "E3749", {"start": v(-23.53, 11.2) * mm, "end": v(-24.55, 11.07) * mm});
            skLineSegment(sketch, "E3750", {"start": v(-24.55, 11.07) * mm, "end": v(-29.64, 10.22) * mm});
            skLineSegment(sketch, "E3751", {"start": v(-29.64, 10.22) * mm, "end": v(-34.78, 9.46) * mm});
            skLineSegment(sketch, "E3752", {"start": v(-34.78, 9.46) * mm, "end": v(-35.82, 9.37) * mm});
            skLineSegment(sketch, "E3753", {"start": v(-35.82, 9.37) * mm, "end": v(-35.82, 9.51) * mm});
            skLineSegment(sketch, "E3754", {"start": v(-35.82, 9.51) * mm, "end": v(-35.7, 9.94) * mm});
            skLineSegment(sketch, "E3755", {"start": v(-35.7, 9.94) * mm, "end": v(-35.44, 10.2) * mm});
            skLineSegment(sketch, "E3756", {"start": v(-35.44, 10.2) * mm, "end": v(-35.11, 10.3) * mm});
            skLineSegment(sketch, "E3757", {"start": v(-35.11, 10.3) * mm, "end": v(-34.86, 10.34) * mm});
            skLineSegment(sketch, "E3758", {"start": v(-34.86, 10.34) * mm, "end": v(-34.79, 10.37) * mm});
            skLineSegment(sketch, "E3759", {"start": v(-34.79, 10.37) * mm, "end": v(-34.5, 10.47) * mm});
            skLineSegment(sketch, "E3760", {"start": v(-34.5, 10.47) * mm, "end": v(-33.71, 10.89) * mm});
            skLineSegment(sketch, "E3761", {"start": v(-33.71, 10.89) * mm, "end": v(-33.07, 11.54) * mm});
            skLineSegment(sketch, "E3762", {"start": v(-33.07, 11.54) * mm, "end": v(-32.8, 12.43) * mm});
            skLineSegment(sketch, "E3763", {"start": v(-32.8, 12.43) * mm, "end": v(-32.82, 13.38) * mm});
            skLineSegment(sketch, "E3764", {"start": v(-32.82, 13.38) * mm, "end": v(-32.86, 13.69) * mm});
            skLineSegment(sketch, "E3765", {"start": v(-32.86, 13.69) * mm, "end": v(-32.95, 14.33) * mm});
            skLineSegment(sketch, "E3766", {"start": v(-32.95, 14.33) * mm, "end": v(-33.96, 20.76) * mm});
            skLineSegment(sketch, "E3767", {"start": v(-33.96, 20.76) * mm, "end": v(-34.06, 21.4) * mm});
            skLineSegment(sketch, "E3768", {"start": v(-34.06, 21.4) * mm, "end": v(-34.24, 22.5) * mm});
            skLineSegment(sketch, "E3769", {"start": v(-34.24, 22.5) * mm, "end": v(-36.08, 33.47) * mm});
            skLineSegment(sketch, "E3770", {"start": v(-36.08, 33.47) * mm, "end": v(-36.27, 34.57) * mm});
            skLineSegment(sketch, "E3771", {"start": v(-63.6, 30.05) * mm, "end": v(-63.34, 29.32) * mm});
            skLineSegment(sketch, "E3772", {"start": v(-63.34, 29.32) * mm, "end": v(-60.62, 22) * mm});
            skLineSegment(sketch, "E3773", {"start": v(-60.62, 22) * mm, "end": v(-60.35, 21.26) * mm});
            skLineSegment(sketch, "E3774", {"start": v(-60.35, 21.26) * mm, "end": v(-59.9, 20.08) * mm});
            skLineSegment(sketch, "E3775", {"start": v(-59.9, 20.08) * mm, "end": v(-55.47, 8.24) * mm});
            skLineSegment(sketch, "E3776", {"start": v(-55.47, 8.24) * mm, "end": v(-55.02, 7.06) * mm});
            skLineSegment(sketch, "E3777", {"start": v(-55.02, 7.06) * mm, "end": v(-54.9, 6.74) * mm});
            skLineSegment(sketch, "E3778", {"start": v(-54.9, 6.74) * mm, "end": v(-54.4, 5.83) * mm});
            skLineSegment(sketch, "E3779", {"start": v(-54.4, 5.83) * mm, "end": v(-53.67, 5.23) * mm});
            skLineSegment(sketch, "E3780", {"start": v(-53.67, 5.23) * mm, "end": v(-52.71, 5.2) * mm});
            skLineSegment(sketch, "E3781", {"start": v(-52.71, 5.2) * mm, "end": v(-51.74, 5.54) * mm});
            skLineSegment(sketch, "E3782", {"start": v(-51.74, 5.54) * mm, "end": v(-51.43, 5.7) * mm});
            skLineSegment(sketch, "E3783", {"start": v(-51.43, 5.7) * mm, "end": v(-51.13, 5.84) * mm});
            skLineSegment(sketch, "E3784", {"start": v(-51.13, 5.84) * mm, "end": v(-50.32, 6.4) * mm});
            skLineSegment(sketch, "E3785", {"start": v(-50.32, 6.4) * mm, "end": v(-49.45, 7.29) * mm});
            skLineSegment(sketch, "E3786", {"start": v(-49.45, 7.29) * mm, "end": v(-48.82, 8.36) * mm});
            skLineSegment(sketch, "E3787", {"start": v(-48.82, 8.36) * mm, "end": v(-48.48, 9.29) * mm});
            skLineSegment(sketch, "E3788", {"start": v(-48.48, 9.29) * mm, "end": v(-48.42, 9.6) * mm});
            skLineSegment(sketch, "E3789", {"start": v(-48.42, 9.6) * mm, "end": v(-48.25, 10.37) * mm});
            skLineSegment(sketch, "E3790", {"start": v(-48.25, 10.37) * mm, "end": v(-48.3, 14.1) * mm});
            skLineSegment(sketch, "E3791", {"start": v(-48.3, 14.1) * mm, "end": v(-49.18, 17.75) * mm});
            skLineSegment(sketch, "E3792", {"start": v(-49.18, 17.75) * mm, "end": v(-49.42, 18.46) * mm});
            skLineSegment(sketch, "E3793", {"start": v(-49.42, 18.46) * mm, "end": v(-49.47, 18.62) * mm});
            skLineSegment(sketch, "E3794", {"start": v(-49.47, 18.62) * mm, "end": v(-49.9, 19.41) * mm});
            skLineSegment(sketch, "E3795", {"start": v(-49.9, 19.41) * mm, "end": v(-50.27, 20.23) * mm});
            skLineSegment(sketch, "E3796", {"start": v(-50.27, 20.23) * mm, "end": v(-50.3, 20.4) * mm});
            skLineSegment(sketch, "E3797", {"start": v(-50.3, 20.4) * mm, "end": v(-50.46, 21.2) * mm});
            skLineSegment(sketch, "E3798", {"start": v(-50.46, 21.2) * mm, "end": v(-51.93, 24.82) * mm});
            skLineSegment(sketch, "E3799", {"start": v(-51.93, 24.82) * mm, "end": v(-54.17, 28) * mm});
            skLineSegment(sketch, "E3800", {"start": v(-54.17, 28) * mm, "end": v(-54.7, 28.58) * mm});
            skLineSegment(sketch, "E3801", {"start": v(-54.7, 28.58) * mm, "end": v(-55.11, 29.03) * mm});
            skLineSegment(sketch, "E3802", {"start": v(-55.11, 29.03) * mm, "end": v(-56.52, 30.2) * mm});
            skLineSegment(sketch, "E3803", {"start": v(-56.52, 30.2) * mm, "end": v(-58.52, 31.09) * mm});
            skLineSegment(sketch, "E3804", {"start": v(-58.52, 31.09) * mm, "end": v(-60.84, 31.09) * mm});
            skLineSegment(sketch, "E3805", {"start": v(-60.84, 31.09) * mm, "end": v(-62.96, 30.4) * mm});
            skLineSegment(sketch, "E3806", {"start": v(-62.96, 30.4) * mm, "end": v(-63.6, 30.05) * mm});
            skLineSegment(sketch, "E3807", {"start": v(-58.85, 0.87) * mm, "end": v(-59.08, 0.85) * mm});
            skLineSegment(sketch, "E3808", {"start": v(-59.08, 0.85) * mm, "end": v(-59.79, 0.7) * mm});
            skLineSegment(sketch, "E3809", {"start": v(-59.79, 0.7) * mm, "end": v(-60.67, 0.36) * mm});
            skLineSegment(sketch, "E3810", {"start": v(-60.67, 0.36) * mm, "end": v(-61.52, -0.06) * mm});
            skLineSegment(sketch, "E3811", {"start": v(-61.52, -0.06) * mm, "end": v(-62.16, -0.36) * mm});
            skLineSegment(sketch, "E3812", {"start": v(-62.16, -0.36) * mm, "end": v(-62.38, -0.44) * mm});
            skLineSegment(sketch, "E3813", {"start": v(-62.38, -0.44) * mm, "end": v(-62.5, -0.42) * mm});
            skLineSegment(sketch, "E3814", {"start": v(-62.5, -0.42) * mm, "end": v(-62.86, -0.28) * mm});
            skLineSegment(sketch, "E3815", {"start": v(-62.86, -0.28) * mm, "end": v(-63.05, -0.04) * mm});
            skLineSegment(sketch, "E3816", {"start": v(-63.05, -0.04) * mm, "end": v(-62.99, 0.28) * mm});
            skLineSegment(sketch, "E3817", {"start": v(-62.99, 0.28) * mm, "end": v(-62.77, 0.58) * mm});
            skLineSegment(sketch, "E3818", {"start": v(-62.77, 0.58) * mm, "end": v(-62.7, 0.66) * mm});
            skLineSegment(sketch, "E3819", {"start": v(-62.7, 0.66) * mm, "end": v(-62.36, 0.8) * mm});
            skLineSegment(sketch, "E3820", {"start": v(-62.36, 0.8) * mm, "end": v(-61.4, 1.34) * mm});
            skLineSegment(sketch, "E3821", {"start": v(-61.4, 1.34) * mm, "end": v(-60.72, 2.1) * mm});
            skLineSegment(sketch, "E3822", {"start": v(-60.72, 2.1) * mm, "end": v(-60.58, 3.07) * mm});
            skLineSegment(sketch, "E3823", {"start": v(-60.58, 3.07) * mm, "end": v(-60.8, 4.1) * mm});
            skLineSegment(sketch, "E3824", {"start": v(-60.8, 4.1) * mm, "end": v(-60.92, 4.43) * mm});
            skLineSegment(sketch, "E3825", {"start": v(-60.92, 4.43) * mm, "end": v(-61.1, 4.96) * mm});
            skLineSegment(sketch, "E3826", {"start": v(-61.1, 4.96) * mm, "end": v(-63.06, 10.24) * mm});
            skLineSegment(sketch, "E3827", {"start": v(-63.06, 10.24) * mm, "end": v(-63.25, 10.76) * mm});
            skLineSegment(sketch, "E3828", {"start": v(-63.25, 10.76) * mm, "end": v(-63.73, 12.03) * mm});
            skLineSegment(sketch, "E3829", {"start": v(-63.73, 12.03) * mm, "end": v(-68.46, 24.63) * mm});
            skLineSegment(sketch, "E3830", {"start": v(-68.46, 24.63) * mm, "end": v(-68.94, 25.9) * mm});
            skLineSegment(sketch, "E3831", {"start": v(-68.94, 25.9) * mm, "end": v(-69.05, 26.19) * mm});
            skLineSegment(sketch, "E3832", {"start": v(-69.05, 26.19) * mm, "end": v(-69.45, 27.05) * mm});
            skLineSegment(sketch, "E3833", {"start": v(-69.45, 27.05) * mm, "end": v(-69.98, 27.66) * mm});
            skLineSegment(sketch, "E3834", {"start": v(-69.98, 27.66) * mm, "end": v(-70.74, 27.89) * mm});
            skLineSegment(sketch, "E3835", {"start": v(-70.74, 27.89) * mm, "end": v(-71.64, 27.9) * mm});
            skLineSegment(sketch, "E3836", {"start": v(-71.64, 27.9) * mm, "end": v(-71.93, 27.89) * mm});
            skLineSegment(sketch, "E3837", {"start": v(-71.93, 27.89) * mm, "end": v(-72, 27.94) * mm});
            skLineSegment(sketch, "E3838", {"start": v(-72, 27.94) * mm, "end": v(-72.36, 27.93) * mm});
            skLineSegment(sketch, "E3839", {"start": v(-72.36, 27.93) * mm, "end": v(-72.8, 27.76) * mm});
            skLineSegment(sketch, "E3840", {"start": v(-72.8, 27.76) * mm, "end": v(-73.2, 27.68) * mm});
            skLineSegment(sketch, "E3841", {"start": v(-73.2, 27.68) * mm, "end": v(-73.45, 27.91) * mm});
            skLineSegment(sketch, "E3842", {"start": v(-73.45, 27.91) * mm, "end": v(-73.47, 28) * mm});
            skLineSegment(sketch, "E3843", {"start": v(-73.47, 28) * mm, "end": v(-73.5, 28.1) * mm});
            skLineSegment(sketch, "E3844", {"start": v(-73.5, 28.1) * mm, "end": v(-73.44, 28.45) * mm});
            skLineSegment(sketch, "E3845", {"start": v(-73.44, 28.45) * mm, "end": v(-73.1, 28.67) * mm});
            skLineSegment(sketch, "E3846", {"start": v(-73.1, 28.67) * mm, "end": v(-72.65, 28.8) * mm});
            skLineSegment(sketch, "E3847", {"start": v(-72.65, 28.8) * mm, "end": v(-72.33, 28.92) * mm});
            skLineSegment(sketch, "E3848", {"start": v(-72.33, 28.92) * mm, "end": v(-72.24, 28.98) * mm});
            skLineSegment(sketch, "E3849", {"start": v(-72.24, 28.98) * mm, "end": v(-72.21, 29) * mm});
            skLineSegment(sketch, "E3850", {"start": v(-72.21, 29) * mm, "end": v(-71.96, 29.22) * mm});
            skLineSegment(sketch, "E3851", {"start": v(-71.96, 29.22) * mm, "end": v(-71.93, 29.24) * mm});
            skLineSegment(sketch, "E3852", {"start": v(-71.93, 29.24) * mm, "end": v(-71.3, 29.43) * mm});
            skLineSegment(sketch, "E3853", {"start": v(-71.3, 29.43) * mm, "end": v(-68.14, 30.46) * mm});
            skLineSegment(sketch, "E3854", {"start": v(-68.14, 30.46) * mm, "end": v(-65.06, 31.7) * mm});
            skLineSegment(sketch, "E3855", {"start": v(-65.06, 31.7) * mm, "end": v(-64.46, 32) * mm});
            skLineSegment(sketch, "E3856", {"start": v(-64.46, 32) * mm, "end": v(-64.03, 32.2) * mm});
            skLineSegment(sketch, "E3857", {"start": v(-64.03, 32.2) * mm, "end": v(-61.76, 33) * mm});
            skLineSegment(sketch, "E3858", {"start": v(-61.76, 33) * mm, "end": v(-59.42, 33.52) * mm});
            skLineSegment(sketch, "E3859", {"start": v(-59.42, 33.52) * mm, "end": v(-58.95, 33.6) * mm});
            skLineSegment(sketch, "E3860", {"start": v(-58.95, 33.6) * mm, "end": v(-58.23, 33.73) * mm});
            skLineSegment(sketch, "E3861", {"start": v(-58.23, 33.73) * mm, "end": v(-56.03, 33.82) * mm});
            skLineSegment(sketch, "E3862", {"start": v(-56.03, 33.82) * mm, "end": v(-53.29, 33.4) * mm});
            skLineSegment(sketch, "E3863", {"start": v(-53.29, 33.4) * mm, "end": v(-50.73, 32.33) * mm});
            skLineSegment(sketch, "E3864", {"start": v(-50.73, 32.33) * mm, "end": v(-48.9, 31.08) * mm});
            skLineSegment(sketch, "E3865", {"start": v(-48.9, 31.08) * mm, "end": v(-48.35, 30.58) * mm});
            skLineSegment(sketch, "E3866", {"start": v(-48.35, 30.58) * mm, "end": v(-48.27, 30.5) * mm});
            skLineSegment(sketch, "E3867", {"start": v(-48.27, 30.5) * mm, "end": v(-47.38, 29.71) * mm});
            skLineSegment(sketch, "E3868", {"start": v(-47.38, 29.71) * mm, "end": v(-47.29, 29.64) * mm});
            skLineSegment(sketch, "E3869", {"start": v(-47.29, 29.64) * mm, "end": v(-46.69, 28.85) * mm});
            skLineSegment(sketch, "E3870", {"start": v(-46.69, 28.85) * mm, "end": v(-44.23, 24.69) * mm});
            skLineSegment(sketch, "E3871", {"start": v(-44.23, 24.69) * mm, "end": v(-42.64, 20.12) * mm});
            skLineSegment(sketch, "E3872", {"start": v(-42.64, 20.12) * mm, "end": v(-42.47, 19.13) * mm});
            skLineSegment(sketch, "E3873", {"start": v(-42.47, 19.13) * mm, "end": v(-42.27, 17.95) * mm});
            skLineSegment(sketch, "E3874", {"start": v(-42.27, 17.95) * mm, "end": v(-42.36, 14.27) * mm});
            skLineSegment(sketch, "E3875", {"start": v(-42.36, 14.27) * mm, "end": v(-43.74, 10.05) * mm});
            skLineSegment(sketch, "E3876", {"start": v(-43.74, 10.05) * mm, "end": v(-46.53, 6.6) * mm});
            skLineSegment(sketch, "E3877", {"start": v(-46.53, 6.6) * mm, "end": v(-49.57, 4.53) * mm});
            skLineSegment(sketch, "E3878", {"start": v(-49.57, 4.53) * mm, "end": v(-50.67, 4.07) * mm});
            skLineSegment(sketch, "E3879", {"start": v(-50.67, 4.07) * mm, "end": v(-51.35, 3.78) * mm});
            skLineSegment(sketch, "E3880", {"start": v(-51.35, 3.78) * mm, "end": v(-54.78, 2.52) * mm});
            skLineSegment(sketch, "E3881", {"start": v(-54.78, 2.52) * mm, "end": v(-58.19, 1.19) * mm});
            skLineSegment(sketch, "E3882", {"start": v(-58.19, 1.19) * mm, "end": v(-58.85, 0.87) * mm});
            skLineSegment(sketch, "E3883", {"start": v(34.77, 23.23) * mm, "end": v(34.54, 24.1) * mm});
            skLineSegment(sketch, "E3884", {"start": v(34.54, 24.1) * mm, "end": v(33.4, 28.47) * mm});
            skLineSegment(sketch, "E3885", {"start": v(33.4, 28.47) * mm, "end": v(32.13, 32.95) * mm});
            skLineSegment(sketch, "E3886", {"start": v(32.13, 32.95) * mm, "end": v(31.82, 33.89) * mm});
            skLineSegment(sketch, "E3887", {"start": v(31.82, 33.89) * mm, "end": v(31.39, 32.99) * mm});
            skLineSegment(sketch, "E3888", {"start": v(31.39, 32.99) * mm, "end": v(29.36, 28.77) * mm});
            skLineSegment(sketch, "E3889", {"start": v(29.36, 28.77) * mm, "end": v(27.42, 24.75) * mm});
            skLineSegment(sketch, "E3890", {"start": v(27.42, 24.75) * mm, "end": v(27.03, 23.94) * mm});
            skLineSegment(sketch, "E3891", {"start": v(27.03, 23.94) * mm, "end": v(27.7, 23.83) * mm});
            skLineSegment(sketch, "E3892", {"start": v(27.7, 23.83) * mm, "end": v(30.93, 23.45) * mm});
            skLineSegment(sketch, "E3893", {"start": v(30.93, 23.45) * mm, "end": v(34.12, 23.25) * mm});
            skLineSegment(sketch, "E3894", {"start": v(34.12, 23.25) * mm, "end": v(34.77, 23.23) * mm});
            skLineSegment(sketch, "E3895", {"start": v(25.9, 25.42) * mm, "end": v(26.54, 26.61) * mm});
            skLineSegment(sketch, "E3896", {"start": v(26.54, 26.61) * mm, "end": v(29.55, 32.66) * mm});
            skLineSegment(sketch, "E3897", {"start": v(29.55, 32.66) * mm, "end": v(32.48, 38.76) * mm});
            skLineSegment(sketch, "E3898", {"start": v(32.48, 38.76) * mm, "end": v(33.09, 39.96) * mm});
            skLineSegment(sketch, "E3899", {"start": v(33.09, 39.96) * mm, "end": v(33.26, 40.3) * mm});
            skLineSegment(sketch, "E3900", {"start": v(33.26, 40.3) * mm, "end": v(34.1, 42) * mm});
            skLineSegment(sketch, "E3901", {"start": v(34.1, 42) * mm, "end": v(35.01, 43.87) * mm});
            skLineSegment(sketch, "E3902", {"start": v(35.01, 43.87) * mm, "end": v(35.21, 44.27) * mm});
            skLineSegment(sketch, "E3903", {"start": v(35.21, 44.27) * mm, "end": v(35.37, 43.98) * mm});
            skLineSegment(sketch, "E3904", {"start": v(35.37, 43.98) * mm, "end": v(35.93, 42.59) * mm});
            skLineSegment(sketch, "E3905", {"start": v(35.93, 42.59) * mm, "end": v(36.3, 41.3) * mm});
            skLineSegment(sketch, "E3906", {"start": v(36.3, 41.3) * mm, "end": v(36.37, 41.06) * mm});
            skLineSegment(sketch, "E3907", {"start": v(36.37, 41.06) * mm, "end": v(36.7, 39.89) * mm});
            skLineSegment(sketch, "E3908", {"start": v(36.7, 39.89) * mm, "end": v(39.96, 28.22) * mm});
            skLineSegment(sketch, "E3909", {"start": v(39.96, 28.22) * mm, "end": v(40.28, 27.05) * mm});
            skLineSegment(sketch, "E3910", {"start": v(40.28, 27.05) * mm, "end": v(40.55, 26.1) * mm});
            skLineSegment(sketch, "E3911", {"start": v(40.55, 26.1) * mm, "end": v(43.2, 16.57) * mm});
            skLineSegment(sketch, "E3912", {"start": v(43.2, 16.57) * mm, "end": v(43.48, 15.62) * mm});
            skLineSegment(sketch, "E3913", {"start": v(43.48, 15.62) * mm, "end": v(43.54, 15.4) * mm});
            skLineSegment(sketch, "E3914", {"start": v(43.54, 15.4) * mm, "end": v(43.76, 14.75) * mm});
            skLineSegment(sketch, "E3915", {"start": v(43.76, 14.75) * mm, "end": v(44.13, 13.93) * mm});
            skLineSegment(sketch, "E3916", {"start": v(44.13, 13.93) * mm, "end": v(44.7, 13.22) * mm});
            skLineSegment(sketch, "E3917", {"start": v(44.7, 13.22) * mm, "end": v(45.3, 12.8) * mm});
            skLineSegment(sketch, "E3918", {"start": v(45.3, 12.8) * mm, "end": v(45.51, 12.7) * mm});
            skLineSegment(sketch, "E3919", {"start": v(45.51, 12.7) * mm, "end": v(45.59, 12.67) * mm});
            skLineSegment(sketch, "E3920", {"start": v(45.59, 12.67) * mm, "end": v(45.8, 12.57) * mm});
            skLineSegment(sketch, "E3921", {"start": v(45.8, 12.57) * mm, "end": v(46.04, 12.41) * mm});
            skLineSegment(sketch, "E3922", {"start": v(46.04, 12.41) * mm, "end": v(46.17, 12.18) * mm});
            skLineSegment(sketch, "E3923", {"start": v(46.17, 12.18) * mm, "end": v(46.14, 11.92) * mm});
            skLineSegment(sketch, "E3924", {"start": v(46.14, 11.92) * mm, "end": v(46.1, 11.84) * mm});
            skLineSegment(sketch, "E3925", {"start": v(46.1, 11.84) * mm, "end": v(46.06, 11.76) * mm});
            skLineSegment(sketch, "E3926", {"start": v(46.06, 11.76) * mm, "end": v(45.7, 11.6) * mm});
            skLineSegment(sketch, "E3927", {"start": v(45.7, 11.6) * mm, "end": v(45.27, 11.64) * mm});
            skLineSegment(sketch, "E3928", {"start": v(45.27, 11.64) * mm, "end": v(45.19, 11.65) * mm});
            skLineSegment(sketch, "E3929", {"start": v(45.19, 11.65) * mm, "end": v(44.39, 11.72) * mm});
            skLineSegment(sketch, "E3930", {"start": v(44.39, 11.72) * mm, "end": v(36.4, 12.4) * mm});
            skLineSegment(sketch, "E3931", {"start": v(36.4, 12.4) * mm, "end": v(35.6, 12.43) * mm});
            skLineSegment(sketch, "E3932", {"start": v(35.6, 12.43) * mm, "end": v(35.49, 12.5) * mm});
            skLineSegment(sketch, "E3933", {"start": v(35.49, 12.5) * mm, "end": v(35.1, 12.6) * mm});
            skLineSegment(sketch, "E3934", {"start": v(35.1, 12.6) * mm, "end": v(34.55, 12.68) * mm});
            skLineSegment(sketch, "E3935", {"start": v(34.55, 12.68) * mm, "end": v(33.98, 12.8) * mm});
            skLineSegment(sketch, "E3936", {"start": v(33.98, 12.8) * mm, "end": v(33.55, 13.06) * mm});
            skLineSegment(sketch, "E3937", {"start": v(33.55, 13.06) * mm, "end": v(33.44, 13.17) * mm});
            skLineSegment(sketch, "E3938", {"start": v(33.44, 13.17) * mm, "end": v(33.6, 13.29) * mm});
            skLineSegment(sketch, "E3939", {"start": v(33.6, 13.29) * mm, "end": v(34.33, 13.5) * mm});
            skLineSegment(sketch, "E3940", {"start": v(34.33, 13.5) * mm, "end": v(35, 13.5) * mm});
            skLineSegment(sketch, "E3941", {"start": v(35, 13.5) * mm, "end": v(35.13, 13.52) * mm});
            skLineSegment(sketch, "E3942", {"start": v(35.13, 13.52) * mm, "end": v(35.35, 13.55) * mm});
            skLineSegment(sketch, "E3943", {"start": v(35.35, 13.55) * mm, "end": v(36, 13.73) * mm});
            skLineSegment(sketch, "E3944", {"start": v(36, 13.73) * mm, "end": v(36.56, 14.12) * mm});
            skLineSegment(sketch, "E3945", {"start": v(36.56, 14.12) * mm, "end": v(36.82, 14.71) * mm});
            skLineSegment(sketch, "E3946", {"start": v(36.82, 14.71) * mm, "end": v(36.83, 15.35) * mm});
            skLineSegment(sketch, "E3947", {"start": v(36.83, 15.35) * mm, "end": v(36.79, 15.56) * mm});
            skLineSegment(sketch, "E3948", {"start": v(36.79, 15.56) * mm, "end": v(36.7, 16) * mm});
            skLineSegment(sketch, "E3949", {"start": v(36.7, 16) * mm, "end": v(35.6, 20.31) * mm});
            skLineSegment(sketch, "E3950", {"start": v(35.6, 20.31) * mm, "end": v(35.5, 20.74) * mm});
            skLineSegment(sketch, "E3951", {"start": v(35.5, 20.74) * mm, "end": v(35.46, 20.88) * mm});
            skLineSegment(sketch, "E3952", {"start": v(35.46, 20.88) * mm, "end": v(35.07, 21.3) * mm});
            skLineSegment(sketch, "E3953", {"start": v(35.07, 21.3) * mm, "end": v(34.5, 21.43) * mm});
            skLineSegment(sketch, "E3954", {"start": v(34.5, 21.43) * mm, "end": v(34.38, 21.45) * mm});
            skLineSegment(sketch, "E3955", {"start": v(34.38, 21.45) * mm, "end": v(33.78, 21.5) * mm});
            skLineSegment(sketch, "E3956", {"start": v(33.78, 21.5) * mm, "end": v(27.8, 22.09) * mm});
            skLineSegment(sketch, "E3957", {"start": v(27.8, 22.09) * mm, "end": v(27.21, 22.15) * mm});
            skLineSegment(sketch, "E3958", {"start": v(27.21, 22.15) * mm, "end": v(27.04, 22.17) * mm});
            skLineSegment(sketch, "E3959", {"start": v(27.04, 22.17) * mm, "end": v(26.32, 22.06) * mm});
            skLineSegment(sketch, "E3960", {"start": v(26.32, 22.06) * mm, "end": v(25.8, 21.56) * mm});
            skLineSegment(sketch, "E3961", {"start": v(25.8, 21.56) * mm, "end": v(25.73, 21.39) * mm});
            skLineSegment(sketch, "E3962", {"start": v(25.73, 21.39) * mm, "end": v(25.62, 21.12) * mm});
            skLineSegment(sketch, "E3963", {"start": v(25.62, 21.12) * mm, "end": v(24.44, 18.46) * mm});
            skLineSegment(sketch, "E3964", {"start": v(24.44, 18.46) * mm, "end": v(24.33, 18.19) * mm});
            skLineSegment(sketch, "E3965", {"start": v(24.33, 18.19) * mm, "end": v(24.2, 17.83) * mm});
            skLineSegment(sketch, "E3966", {"start": v(24.2, 17.83) * mm, "end": v(24, 16.68) * mm});
            skLineSegment(sketch, "E3967", {"start": v(24, 16.68) * mm, "end": v(24.25, 15.52) * mm});
            skLineSegment(sketch, "E3968", {"start": v(24.25, 15.52) * mm, "end": v(25.02, 14.74) * mm});
            skLineSegment(sketch, "E3969", {"start": v(25.02, 14.74) * mm, "end": v(25.93, 14.39) * mm});
            skLineSegment(sketch, "E3970", {"start": v(25.93, 14.39) * mm, "end": v(26.25, 14.35) * mm});
            skLineSegment(sketch, "E3971", {"start": v(26.25, 14.35) * mm, "end": v(26.32, 14.34) * mm});
            skLineSegment(sketch, "E3972", {"start": v(26.32, 14.34) * mm, "end": v(26.54, 14.3) * mm});
            skLineSegment(sketch, "E3973", {"start": v(26.54, 14.3) * mm, "end": v(26.82, 14.2) * mm});
            skLineSegment(sketch, "E3974", {"start": v(26.82, 14.2) * mm, "end": v(27.04, 13.98) * mm});
            skLineSegment(sketch, "E3975", {"start": v(27.04, 13.98) * mm, "end": v(27.15, 13.68) * mm});
            skLineSegment(sketch, "E3976", {"start": v(27.15, 13.68) * mm, "end": v(27.16, 13.57) * mm});
            skLineSegment(sketch, "E3977", {"start": v(27.16, 13.57) * mm, "end": v(26.87, 13.49) * mm});
            skLineSegment(sketch, "E3978", {"start": v(26.87, 13.49) * mm, "end": v(25.96, 13.42) * mm});
            skLineSegment(sketch, "E3979", {"start": v(25.96, 13.42) * mm, "end": v(24.76, 13.51) * mm});
            skLineSegment(sketch, "E3980", {"start": v(24.76, 13.51) * mm, "end": v(23.57, 13.64) * mm});
            skLineSegment(sketch, "E3981", {"start": v(23.57, 13.64) * mm, "end": v(22.67, 13.63) * mm});
            skLineSegment(sketch, "E3982", {"start": v(22.67, 13.63) * mm, "end": v(22.38, 13.58) * mm});
            skLineSegment(sketch, "E3983", {"start": v(22.38, 13.58) * mm, "end": v(22.11, 13.66) * mm});
            skLineSegment(sketch, "E3984", {"start": v(22.11, 13.66) * mm, "end": v(20.77, 13.86) * mm});
            skLineSegment(sketch, "E3985", {"start": v(20.77, 13.86) * mm, "end": v(19.4, 13.95) * mm});
            skLineSegment(sketch, "E3986", {"start": v(19.4, 13.95) * mm, "end": v(19.14, 13.97) * mm});
            skLineSegment(sketch, "E3987", {"start": v(19.14, 13.97) * mm, "end": v(19.07, 13.98) * mm});
            skLineSegment(sketch, "E3988", {"start": v(19.07, 13.98) * mm, "end": v(18.75, 14.03) * mm});
            skLineSegment(sketch, "E3989", {"start": v(18.75, 14.03) * mm, "end": v(18.52, 14.25) * mm});
            skLineSegment(sketch, "E3990", {"start": v(18.52, 14.25) * mm, "end": v(18.5, 14.34) * mm});
            skLineSegment(sketch, "E3991", {"start": v(18.5, 14.34) * mm, "end": v(18.48, 14.44) * mm});
            skLineSegment(sketch, "E3992", {"start": v(18.48, 14.44) * mm, "end": v(18.55, 14.82) * mm});
            skLineSegment(sketch, "E3993", {"start": v(18.55, 14.82) * mm, "end": v(18.87, 15.04) * mm});
            skLineSegment(sketch, "E3994", {"start": v(18.87, 15.04) * mm, "end": v(18.97, 15.07) * mm});
            skLineSegment(sketch, "E3995", {"start": v(18.97, 15.07) * mm, "end": v(19.33, 15.17) * mm});
            skLineSegment(sketch, "E3996", {"start": v(19.33, 15.17) * mm, "end": v(20.35, 15.7) * mm});
            skLineSegment(sketch, "E3997", {"start": v(20.35, 15.7) * mm, "end": v(21.39, 16.68) * mm});
            skLineSegment(sketch, "E3998", {"start": v(21.39, 16.68) * mm, "end": v(22.19, 17.87) * mm});
            skLineSegment(sketch, "E3999", {"start": v(22.19, 17.87) * mm, "end": v(22.7, 18.84) * mm});
            skLineSegment(sketch, "E4000", {"start": v(22.7, 18.84) * mm, "end": v(22.87, 19.17) * mm});
            skLineSegment(sketch, "E4001", {"start": v(22.87, 19.17) * mm, "end": v(23.12, 19.69) * mm});
            skLineSegment(sketch, "E4002", {"start": v(23.12, 19.69) * mm, "end": v(25.64, 24.9) * mm});
            skLineSegment(sketch, "E4003", {"start": v(25.64, 24.9) * mm, "end": v(25.9, 25.42) * mm});
            skLineSegment(sketch, "E4004", {"start": v(61.01, -106.54) * mm, "end": v(60.9, -106.57) * mm});
            skLineSegment(sketch, "E4005", {"start": v(60.9, -106.57) * mm, "end": v(60.55, -106.74) * mm});
            skLineSegment(sketch, "E4006", {"start": v(60.55, -106.74) * mm, "end": v(60.3, -107.03) * mm});
            skLineSegment(sketch, "E4007", {"start": v(60.3, -107.03) * mm, "end": v(60.16, -107.37) * mm});
            skLineSegment(sketch, "E4008", {"start": v(60.16, -107.37) * mm, "end": v(60.09, -107.61) * mm});
            skLineSegment(sketch, "E4009", {"start": v(60.09, -107.61) * mm, "end": v(60.06, -107.7) * mm});
            skLineSegment(sketch, "E4010", {"start": v(60.06, -107.7) * mm, "end": v(59.25, -109.9) * mm});
            skLineSegment(sketch, "E4011", {"start": v(59.25, -109.9) * mm, "end": v(54.95, -120.82) * mm});
            skLineSegment(sketch, "E4012", {"start": v(54.95, -120.82) * mm, "end": v(50.99, -131.86) * mm});
            skLineSegment(sketch, "E4013", {"start": v(50.99, -131.86) * mm, "end": v(50.35, -134.13) * mm});
            skLineSegment(sketch, "E4014", {"start": v(50.35, -134.13) * mm, "end": v(50.29, -134.36) * mm});
            skLineSegment(sketch, "E4015", {"start": v(50.29, -134.36) * mm, "end": v(49.72, -135.14) * mm});
            skLineSegment(sketch, "E4016", {"start": v(49.72, -135.14) * mm, "end": v(48.82, -135.51) * mm});
            skLineSegment(sketch, "E4017", {"start": v(48.82, -135.51) * mm, "end": v(48.59, -135.54) * mm});
            skLineSegment(sketch, "E4018", {"start": v(48.59, -135.54) * mm, "end": v(48.43, -135.56) * mm});
            skLineSegment(sketch, "E4019", {"start": v(48.43, -135.56) * mm, "end": v(47.96, -135.49) * mm});
            skLineSegment(sketch, "E4020", {"start": v(47.96, -135.49) * mm, "end": v(47.53, -135.2) * mm});
            skLineSegment(sketch, "E4021", {"start": v(47.53, -135.2) * mm, "end": v(47.23, -134.78) * mm});
            skLineSegment(sketch, "E4022", {"start": v(47.23, -134.78) * mm, "end": v(47.03, -134.4) * mm});
            skLineSegment(sketch, "E4023", {"start": v(47.03, -134.4) * mm, "end": v(46.97, -134.28) * mm});
            skLineSegment(sketch, "E4024", {"start": v(46.97, -134.28) * mm, "end": v(46, -132.35) * mm});
            skLineSegment(sketch, "E4025", {"start": v(46, -132.35) * mm, "end": v(40.53, -123.04) * mm});
            skLineSegment(sketch, "E4026", {"start": v(40.53, -123.04) * mm, "end": v(34.87, -113.85) * mm});
            skLineSegment(sketch, "E4027", {"start": v(34.87, -113.85) * mm, "end": v(33.8, -111.98) * mm});
            skLineSegment(sketch, "E4028", {"start": v(33.8, -111.98) * mm, "end": v(33.74, -111.9) * mm});
            skLineSegment(sketch, "E4029", {"start": v(33.74, -111.9) * mm, "end": v(33.48, -111.45) * mm});
            skLineSegment(sketch, "E4030", {"start": v(33.48, -111.45) * mm, "end": v(32.97, -111.1) * mm});
            skLineSegment(sketch, "E4031", {"start": v(32.97, -111.1) * mm, "end": v(32.8, -111.07) * mm});
            skLineSegment(sketch, "E4032", {"start": v(32.8, -111.07) * mm, "end": v(32.8, -112.7) * mm});
            skLineSegment(sketch, "E4033", {"start": v(32.8, -112.7) * mm, "end": v(32.78, -117.01) * mm});
            skLineSegment(sketch, "E4034", {"start": v(32.78, -117.01) * mm, "end": v(32.82, -117.55) * mm});
            skLineSegment(sketch, "E4035", {"start": v(32.82, -117.55) * mm, "end": v(32.9, -118.58) * mm});
            skLineSegment(sketch, "E4036", {"start": v(32.9, -118.58) * mm, "end": v(33.08, -128.86) * mm});
            skLineSegment(sketch, "E4037", {"start": v(33.08, -128.86) * mm, "end": v(33.1, -129.88) * mm});
            skLineSegment(sketch, "E4038", {"start": v(33.1, -129.88) * mm, "end": v(33.1, -130.1) * mm});
            skLineSegment(sketch, "E4039", {"start": v(33.1, -130.1) * mm, "end": v(33.15, -132.34) * mm});
            skLineSegment(sketch, "E4040", {"start": v(33.15, -132.34) * mm, "end": v(33.18, -132.56) * mm});
            skLineSegment(sketch, "E4041", {"start": v(33.18, -132.56) * mm, "end": v(33.22, -132.84) * mm});
            skLineSegment(sketch, "E4042", {"start": v(33.22, -132.84) * mm, "end": v(33.45, -133.66) * mm});
            skLineSegment(sketch, "E4043", {"start": v(33.45, -133.66) * mm, "end": v(33.95, -134.4) * mm});
            skLineSegment(sketch, "E4044", {"start": v(33.95, -134.4) * mm, "end": v(34.73, -134.87) * mm});
            skLineSegment(sketch, "E4045", {"start": v(34.73, -134.87) * mm, "end": v(35.58, -135.08) * mm});
            skLineSegment(sketch, "E4046", {"start": v(35.58, -135.08) * mm, "end": v(35.86, -135.11) * mm});
            skLineSegment(sketch, "E4047", {"start": v(35.86, -135.11) * mm, "end": v(36.08, -135.13) * mm});
            skLineSegment(sketch, "E4048", {"start": v(36.08, -135.13) * mm, "end": v(38.3, -135.33) * mm});
            skLineSegment(sketch, "E4049", {"start": v(38.3, -135.33) * mm, "end": v(38.52, -135.36) * mm});
            skLineSegment(sketch, "E4050", {"start": v(38.52, -135.36) * mm, "end": v(38.63, -135.37) * mm});
            skLineSegment(sketch, "E4051", {"start": v(38.63, -135.37) * mm, "end": v(38.98, -135.46) * mm});
            skLineSegment(sketch, "E4052", {"start": v(38.98, -135.46) * mm, "end": v(39.34, -135.67) * mm});
            skLineSegment(sketch, "E4053", {"start": v(39.34, -135.67) * mm, "end": v(39.57, -136.01) * mm});
            skLineSegment(sketch, "E4054", {"start": v(39.57, -136.01) * mm, "end": v(39.66, -136.4) * mm});
            skLineSegment(sketch, "E4055", {"start": v(39.66, -136.4) * mm, "end": v(39.66, -136.52) * mm});
            skLineSegment(sketch, "E4056", {"start": v(39.66, -136.52) * mm, "end": v(39.67, -136.72) * mm});
            skLineSegment(sketch, "E4057", {"start": v(39.67, -136.72) * mm, "end": v(39.4, -137.39) * mm});
            skLineSegment(sketch, "E4058", {"start": v(39.4, -137.39) * mm, "end": v(38.76, -137.7) * mm});
            skLineSegment(sketch, "E4059", {"start": v(38.76, -137.7) * mm, "end": v(38.58, -137.72) * mm});
            skLineSegment(sketch, "E4060", {"start": v(38.58, -137.72) * mm, "end": v(38.3, -137.76) * mm});
            skLineSegment(sketch, "E4061", {"start": v(38.3, -137.76) * mm, "end": v(35.42, -138.16) * mm});
            skLineSegment(sketch, "E4062", {"start": v(35.42, -138.16) * mm, "end": v(35.13, -138.22) * mm});
            skLineSegment(sketch, "E4063", {"start": v(35.13, -138.22) * mm, "end": v(34.33, -138.38) * mm});
            skLineSegment(sketch, "E4064", {"start": v(34.33, -138.38) * mm, "end": v(26.3, -140.1) * mm});
            skLineSegment(sketch, "E4065", {"start": v(26.3, -140.1) * mm, "end": v(25.5, -140.28) * mm});
            skLineSegment(sketch, "E4066", {"start": v(25.5, -140.28) * mm, "end": v(25.4, -140.3) * mm});
            skLineSegment(sketch, "E4067", {"start": v(25.4, -140.3) * mm, "end": v(25.1, -140.39) * mm});
            skLineSegment(sketch, "E4068", {"start": v(25.1, -140.39) * mm, "end": v(24.7, -140.46) * mm});
            skLineSegment(sketch, "E4069", {"start": v(24.7, -140.46) * mm, "end": v(24.34, -140.37) * mm});
            skLineSegment(sketch, "E4070", {"start": v(24.34, -140.37) * mm, "end": v(24.12, -140.1) * mm});
            skLineSegment(sketch, "E4071", {"start": v(24.12, -140.1) * mm, "end": v(24.09, -140) * mm});
            skLineSegment(sketch, "E4072", {"start": v(24.09, -140) * mm, "end": v(24.05, -139.87) * mm});
            skLineSegment(sketch, "E4073", {"start": v(24.05, -139.87) * mm, "end": v(23.97, -139.46) * mm});
            skLineSegment(sketch, "E4074", {"start": v(23.97, -139.46) * mm, "end": v(24, -138.93) * mm});
            skLineSegment(sketch, "E4075", {"start": v(24, -138.93) * mm, "end": v(24.26, -138.46) * mm});
            skLineSegment(sketch, "E4076", {"start": v(24.26, -138.46) * mm, "end": v(24.64, -138.16) * mm});
            skLineSegment(sketch, "E4077", {"start": v(24.64, -138.16) * mm, "end": v(24.79, -138.1) * mm});
            skLineSegment(sketch, "E4078", {"start": v(24.79, -138.1) * mm, "end": v(25.07, -137.98) * mm});
            skLineSegment(sketch, "E4079", {"start": v(25.07, -137.98) * mm, "end": v(27.88, -136.71) * mm});
            skLineSegment(sketch, "E4080", {"start": v(27.88, -136.71) * mm, "end": v(28.16, -136.59) * mm});
            skLineSegment(sketch, "E4081", {"start": v(28.16, -136.59) * mm, "end": v(28.35, -136.5) * mm});
            skLineSegment(sketch, "E4082", {"start": v(28.35, -136.5) * mm, "end": v(29.05, -135.94) * mm});
            skLineSegment(sketch, "E4083", {"start": v(29.05, -135.94) * mm, "end": v(29.42, -135.1) * mm});
            skLineSegment(sketch, "E4084", {"start": v(29.42, -135.1) * mm, "end": v(29.45, -134.89) * mm});
            skLineSegment(sketch, "E4085", {"start": v(29.45, -134.89) * mm, "end": v(29.47, -134.63) * mm});
            skLineSegment(sketch, "E4086", {"start": v(29.47, -134.63) * mm, "end": v(29.69, -133.37) * mm});
            skLineSegment(sketch, "E4087", {"start": v(29.69, -133.37) * mm, "end": v(29.85, -132.1) * mm});
            skLineSegment(sketch, "E4088", {"start": v(29.85, -132.1) * mm, "end": v(29.85, -131.84) * mm});
            skLineSegment(sketch, "E4089", {"start": v(29.85, -131.84) * mm, "end": v(29.84, -130.04) * mm});
            skLineSegment(sketch, "E4090", {"start": v(29.84, -130.04) * mm, "end": v(29.85, -115.18) * mm});
            skLineSegment(sketch, "E4091", {"start": v(29.85, -115.18) * mm, "end": v(29.85, -110.22) * mm});
            skLineSegment(sketch, "E4092", {"start": v(29.85, -110.22) * mm, "end": v(29.85, -109.86) * mm});
            skLineSegment(sketch, "E4093", {"start": v(29.85, -109.86) * mm, "end": v(29.81, -108.9) * mm});
            skLineSegment(sketch, "E4094", {"start": v(29.81, -108.9) * mm, "end": v(29.8, -108.78) * mm});
            skLineSegment(sketch, "E4095", {"start": v(29.8, -108.78) * mm, "end": v(29.79, -108.47) * mm});
            skLineSegment(sketch, "E4096", {"start": v(29.79, -108.47) * mm, "end": v(29.67, -107.54) * mm});
            skLineSegment(sketch, "E4097", {"start": v(29.67, -107.54) * mm, "end": v(29.33, -106.8) * mm});
            skLineSegment(sketch, "E4098", {"start": v(29.33, -106.8) * mm, "end": v(28.65, -106.4) * mm});
            skLineSegment(sketch, "E4099", {"start": v(28.65, -106.4) * mm, "end": v(27.76, -106.2) * mm});
            skLineSegment(sketch, "E4100", {"start": v(27.76, -106.2) * mm, "end": v(27.46, -106.16) * mm});
            skLineSegment(sketch, "E4101", {"start": v(27.46, -106.16) * mm, "end": v(27.25, -106.13) * mm});
            skLineSegment(sketch, "E4102", {"start": v(27.25, -106.13) * mm, "end": v(25.2, -105.94) * mm});
            skLineSegment(sketch, "E4103", {"start": v(25.2, -105.94) * mm, "end": v(25, -105.94) * mm});
            skLineSegment(sketch, "E4104", {"start": v(25, -105.94) * mm, "end": v(24.86, -105.94) * mm});
            skLineSegment(sketch, "E4105", {"start": v(24.86, -105.94) * mm, "end": v(24.43, -105.82) * mm});
            skLineSegment(sketch, "E4106", {"start": v(24.43, -105.82) * mm, "end": v(24.08, -105.52) * mm});
            skLineSegment(sketch, "E4107", {"start": v(24.08, -105.52) * mm, "end": v(23.9, -105.08) * mm});
            skLineSegment(sketch, "E4108", {"start": v(23.9, -105.08) * mm, "end": v(23.82, -104.7) * mm});
            skLineSegment(sketch, "E4109", {"start": v(23.82, -104.7) * mm, "end": v(23.8, -104.58) * mm});
            skLineSegment(sketch, "E4110", {"start": v(23.8, -104.58) * mm, "end": v(23.8, -104.47) * mm});
            skLineSegment(sketch, "E4111", {"start": v(23.8, -104.47) * mm, "end": v(23.86, -104.1) * mm});
            skLineSegment(sketch, "E4112", {"start": v(23.86, -104.1) * mm, "end": v(24.11, -103.86) * mm});
            skLineSegment(sketch, "E4113", {"start": v(24.11, -103.86) * mm, "end": v(24.49, -103.73) * mm});
            skLineSegment(sketch, "E4114", {"start": v(24.49, -103.73) * mm, "end": v(24.78, -103.67) * mm});
            skLineSegment(sketch, "E4115", {"start": v(24.78, -103.67) * mm, "end": v(24.88, -103.64) * mm});
            skLineSegment(sketch, "E4116", {"start": v(24.88, -103.64) * mm, "end": v(25.25, -103.55) * mm});
            skLineSegment(sketch, "E4117", {"start": v(25.25, -103.55) * mm, "end": v(27.12, -103.35) * mm});
            skLineSegment(sketch, "E4118", {"start": v(27.12, -103.35) * mm, "end": v(29, -103.23) * mm});
            skLineSegment(sketch, "E4119", {"start": v(29, -103.23) * mm, "end": v(29.37, -103.17) * mm});
            skLineSegment(sketch, "E4120", {"start": v(29.37, -103.17) * mm, "end": v(30, -103.07) * mm});
            skLineSegment(sketch, "E4121", {"start": v(30, -103.07) * mm, "end": v(36.3, -102.46) * mm});
            skLineSegment(sketch, "E4122", {"start": v(36.3, -102.46) * mm, "end": v(36.94, -102.39) * mm});
            skLineSegment(sketch, "E4123", {"start": v(36.94, -102.39) * mm, "end": v(37.11, -102.37) * mm});
            skLineSegment(sketch, "E4124", {"start": v(37.11, -102.37) * mm, "end": v(37.67, -102.45) * mm});
            skLineSegment(sketch, "E4125", {"start": v(37.67, -102.45) * mm, "end": v(38.21, -102.76) * mm});
            skLineSegment(sketch, "E4126", {"start": v(38.21, -102.76) * mm, "end": v(38.64, -103.23) * mm});
            skLineSegment(sketch, "E4127", {"start": v(38.64, -103.23) * mm, "end": v(38.9, -103.65) * mm});
            skLineSegment(sketch, "E4128", {"start": v(38.9, -103.65) * mm, "end": v(39, -103.79) * mm});
            skLineSegment(sketch, "E4129", {"start": v(39, -103.79) * mm, "end": v(39.34, -104.36) * mm});
            skLineSegment(sketch, "E4130", {"start": v(39.34, -104.36) * mm, "end": v(42.77, -110.1) * mm});
            skLineSegment(sketch, "E4131", {"start": v(42.77, -110.1) * mm, "end": v(43.11, -110.68) * mm});
            skLineSegment(sketch, "E4132", {"start": v(43.11, -110.68) * mm, "end": v(43.67, -111.6) * mm});
            skLineSegment(sketch, "E4133", {"start": v(43.67, -111.6) * mm, "end": v(49.2, -120.88) * mm});
            skLineSegment(sketch, "E4134", {"start": v(49.2, -120.88) * mm, "end": v(49.75, -121.8) * mm});
            skLineSegment(sketch, "E4135", {"start": v(49.75, -121.8) * mm, "end": v(49.84, -121.95) * mm});
            skLineSegment(sketch, "E4136", {"start": v(49.84, -121.95) * mm, "end": v(50.28, -122.7) * mm});
            skLineSegment(sketch, "E4137", {"start": v(50.28, -122.7) * mm, "end": v(50.92, -123.42) * mm});
            skLineSegment(sketch, "E4138", {"start": v(50.92, -123.42) * mm, "end": v(51.11, -123.55) * mm});
            skLineSegment(sketch, "E4139", {"start": v(51.11, -123.55) * mm, "end": v(51.34, -123) * mm});
            skLineSegment(sketch, "E4140", {"start": v(51.34, -123) * mm, "end": v(53.5, -117.73) * mm});
            skLineSegment(sketch, "E4141", {"start": v(53.5, -117.73) * mm, "end": v(53.7, -117.2) * mm});
            skLineSegment(sketch, "E4142", {"start": v(53.7, -117.2) * mm, "end": v(54.25, -115.79) * mm});
            skLineSegment(sketch, "E4143", {"start": v(54.25, -115.79) * mm, "end": v(59.67, -101.58) * mm});
            skLineSegment(sketch, "E4144", {"start": v(59.67, -101.58) * mm, "end": v(60.2, -100.16) * mm});
            skLineSegment(sketch, "E4145", {"start": v(60.2, -100.16) * mm, "end": v(60.27, -99.99) * mm});
            skLineSegment(sketch, "E4146", {"start": v(60.27, -99.99) * mm, "end": v(60.68, -99.3) * mm});
            skLineSegment(sketch, "E4147", {"start": v(60.68, -99.3) * mm, "end": v(61.37, -98.9) * mm});
            skLineSegment(sketch, "E4148", {"start": v(61.37, -98.9) * mm, "end": v(61.58, -98.87) * mm});
            skLineSegment(sketch, "E4149", {"start": v(61.58, -98.87) * mm, "end": v(62.42, -98.73) * mm});
            skLineSegment(sketch, "E4150", {"start": v(62.42, -98.73) * mm, "end": v(70.82, -97.24) * mm});
            skLineSegment(sketch, "E4151", {"start": v(70.82, -97.24) * mm, "end": v(71.66, -97.09) * mm});
            skLineSegment(sketch, "E4152", {"start": v(71.66, -97.09) * mm, "end": v(71.8, -97.06) * mm});
            skLineSegment(sketch, "E4153", {"start": v(71.8, -97.06) * mm, "end": v(72.37, -97.03) * mm});
            skLineSegment(sketch, "E4154", {"start": v(72.37, -97.03) * mm, "end": v(72.8, -97.33) * mm});
            skLineSegment(sketch, "E4155", {"start": v(72.8, -97.33) * mm, "end": v(72.85, -97.46) * mm});
            skLineSegment(sketch, "E4156", {"start": v(72.85, -97.46) * mm, "end": v(72.92, -97.61) * mm});
            skLineSegment(sketch, "E4157", {"start": v(72.92, -97.61) * mm, "end": v(73, -98.37) * mm});
            skLineSegment(sketch, "E4158", {"start": v(73, -98.37) * mm, "end": v(72.63, -99) * mm});
            skLineSegment(sketch, "E4159", {"start": v(72.63, -99) * mm, "end": v(72.47, -99.1) * mm});
            skLineSegment(sketch, "E4160", {"start": v(72.47, -99.1) * mm, "end": v(72.34, -99.18) * mm});
            skLineSegment(sketch, "E4161", {"start": v(72.34, -99.18) * mm, "end": v(71.62, -99.45) * mm});
            skLineSegment(sketch, "E4162", {"start": v(71.62, -99.45) * mm, "end": v(70.88, -99.67) * mm});
            skLineSegment(sketch, "E4163", {"start": v(70.88, -99.67) * mm, "end": v(70.74, -99.73) * mm});
            skLineSegment(sketch, "E4164", {"start": v(70.74, -99.73) * mm, "end": v(70.37, -99.86) * mm});
            skLineSegment(sketch, "E4165", {"start": v(70.37, -99.86) * mm, "end": v(69.3, -100.36) * mm});
            skLineSegment(sketch, "E4166", {"start": v(69.3, -100.36) * mm, "end": v(68.46, -101.1) * mm});
            skLineSegment(sketch, "E4167", {"start": v(68.46, -101.1) * mm, "end": v(68.1, -102.13) * mm});
            skLineSegment(sketch, "E4168", {"start": v(68.1, -102.13) * mm, "end": v(68.08, -103.28) * mm});
            skLineSegment(sketch, "E4169", {"start": v(68.08, -103.28) * mm, "end": v(68.1, -103.66) * mm});
            skLineSegment(sketch, "E4170", {"start": v(68.1, -103.66) * mm, "end": v(68.22, -104.9) * mm});
            skLineSegment(sketch, "E4171", {"start": v(68.22, -104.9) * mm, "end": v(69.48, -117.34) * mm});
            skLineSegment(sketch, "E4172", {"start": v(69.48, -117.34) * mm, "end": v(69.6, -118.58) * mm});
            skLineSegment(sketch, "E4173", {"start": v(69.6, -118.58) * mm, "end": v(69.66, -119.23) * mm});
            skLineSegment(sketch, "E4174", {"start": v(69.66, -119.23) * mm, "end": v(70.37, -125.7) * mm});
            skLineSegment(sketch, "E4175", {"start": v(70.37, -125.7) * mm, "end": v(70.48, -126.33) * mm});
            skLineSegment(sketch, "E4176", {"start": v(70.48, -126.33) * mm, "end": v(70.5, -126.5) * mm});
            skLineSegment(sketch, "E4177", {"start": v(70.5, -126.5) * mm, "end": v(70.66, -126.98) * mm});
            skLineSegment(sketch, "E4178", {"start": v(70.66, -126.98) * mm, "end": v(70.95, -127.42) * mm});
            skLineSegment(sketch, "E4179", {"start": v(70.95, -127.42) * mm, "end": v(71.4, -127.67) * mm});
            skLineSegment(sketch, "E4180", {"start": v(71.4, -127.67) * mm, "end": v(71.87, -127.76) * mm});
            skLineSegment(sketch, "E4181", {"start": v(71.87, -127.76) * mm, "end": v(72.04, -127.77) * mm});
            skLineSegment(sketch, "E4182", {"start": v(72.04, -127.77) * mm, "end": v(72.26, -127.77) * mm});
            skLineSegment(sketch, "E4183", {"start": v(72.26, -127.77) * mm, "end": v(74.46, -128.1) * mm});
            skLineSegment(sketch, "E4184", {"start": v(74.46, -128.1) * mm, "end": v(74.68, -128.14) * mm});
            skLineSegment(sketch, "E4185", {"start": v(74.68, -128.14) * mm, "end": v(74.78, -128.15) * mm});
            skLineSegment(sketch, "E4186", {"start": v(74.78, -128.15) * mm, "end": v(75.1, -128.22) * mm});
            skLineSegment(sketch, "E4187", {"start": v(75.1, -128.22) * mm, "end": v(75.46, -128.38) * mm});
            skLineSegment(sketch, "E4188", {"start": v(75.46, -128.38) * mm, "end": v(75.7, -128.66) * mm});
            skLineSegment(sketch, "E4189", {"start": v(75.7, -128.66) * mm, "end": v(75.81, -128.97) * mm});
            skLineSegment(sketch, "E4190", {"start": v(75.81, -128.97) * mm, "end": v(75.82, -129.08) * mm});
            skLineSegment(sketch, "E4191", {"start": v(75.82, -129.08) * mm, "end": v(75.82, -129.2) * mm});
            skLineSegment(sketch, "E4192", {"start": v(75.82, -129.2) * mm, "end": v(75.73, -129.6) * mm});
            skLineSegment(sketch, "E4193", {"start": v(75.73, -129.6) * mm, "end": v(75.45, -129.89) * mm});
            skLineSegment(sketch, "E4194", {"start": v(75.45, -129.89) * mm, "end": v(75.04, -130.04) * mm});
            skLineSegment(sketch, "E4195", {"start": v(75.04, -130.04) * mm, "end": v(74.69, -130.1) * mm});
            skLineSegment(sketch, "E4196", {"start": v(74.69, -130.1) * mm, "end": v(74.57, -130.11) * mm});
            skLineSegment(sketch, "E4197", {"start": v(74.57, -130.11) * mm, "end": v(74.35, -130.14) * mm});
            skLineSegment(sketch, "E4198", {"start": v(74.35, -130.14) * mm, "end": v(72.14, -130.4) * mm});
            skLineSegment(sketch, "E4199", {"start": v(72.14, -130.4) * mm, "end": v(71.92, -130.42) * mm});
            skLineSegment(sketch, "E4200", {"start": v(71.92, -130.42) * mm, "end": v(70.89, -130.48) * mm});
            skLineSegment(sketch, "E4201", {"start": v(70.89, -130.48) * mm, "end": v(65.83, -131.36) * mm});
            skLineSegment(sketch, "E4202", {"start": v(65.83, -131.36) * mm, "end": v(60.85, -132.6) * mm});
            skLineSegment(sketch, "E4203", {"start": v(60.85, -132.6) * mm, "end": v(59.86, -132.86) * mm});
            skLineSegment(sketch, "E4204", {"start": v(59.86, -132.86) * mm, "end": v(59.72, -132.89) * mm});
            skLineSegment(sketch, "E4205", {"start": v(59.72, -132.89) * mm, "end": v(59.33, -133.02) * mm});
            skLineSegment(sketch, "E4206", {"start": v(59.33, -133.02) * mm, "end": v(58.79, -133.14) * mm});
            skLineSegment(sketch, "E4207", {"start": v(58.79, -133.14) * mm, "end": v(58.3, -133.03) * mm});
            skLineSegment(sketch, "E4208", {"start": v(58.3, -133.03) * mm, "end": v(58, -132.66) * mm});
            skLineSegment(sketch, "E4209", {"start": v(58, -132.66) * mm, "end": v(57.95, -132.52) * mm});
            skLineSegment(sketch, "E4210", {"start": v(57.95, -132.52) * mm, "end": v(57.9, -132.36) * mm});
            skLineSegment(sketch, "E4211", {"start": v(57.9, -132.36) * mm, "end": v(57.88, -131.85) * mm});
            skLineSegment(sketch, "E4212", {"start": v(57.88, -131.85) * mm, "end": v(58.15, -131.37) * mm});
            skLineSegment(sketch, "E4213", {"start": v(58.15, -131.37) * mm, "end": v(58.63, -131.03) * mm});
            skLineSegment(sketch, "E4214", {"start": v(58.63, -131.03) * mm, "end": v(59.07, -130.82) * mm});
            skLineSegment(sketch, "E4215", {"start": v(59.07, -130.82) * mm, "end": v(59.22, -130.76) * mm});
            skLineSegment(sketch, "E4216", {"start": v(59.22, -130.76) * mm, "end": v(59.52, -130.63) * mm});
            skLineSegment(sketch, "E4217", {"start": v(59.52, -130.63) * mm, "end": v(60.42, -130.24) * mm});
            skLineSegment(sketch, "E4218", {"start": v(60.42, -130.24) * mm, "end": v(61.33, -129.8) * mm});
            skLineSegment(sketch, "E4219", {"start": v(61.33, -129.8) * mm, "end": v(62, -129.38) * mm});
            skLineSegment(sketch, "E4220", {"start": v(62, -129.38) * mm, "end": v(62.43, -128.91) * mm});
            skLineSegment(sketch, "E4221", {"start": v(62.43, -128.91) * mm, "end": v(62.69, -128.33) * mm});
            skLineSegment(sketch, "E4222", {"start": v(62.69, -128.33) * mm, "end": v(62.8, -127.57) * mm});
            skLineSegment(sketch, "E4223", {"start": v(62.8, -127.57) * mm, "end": v(62.78, -126.57) * mm});
            skLineSegment(sketch, "E4224", {"start": v(62.78, -126.57) * mm, "end": v(62.72, -125.6) * mm});
            skLineSegment(sketch, "E4225", {"start": v(62.72, -125.6) * mm, "end": v(62.7, -125.27) * mm});
            skLineSegment(sketch, "E4226", {"start": v(62.7, -125.27) * mm, "end": v(62.6, -123.97) * mm});
            skLineSegment(sketch, "E4227", {"start": v(62.6, -123.97) * mm, "end": v(62.1, -117.49) * mm});
            skLineSegment(sketch, "E4228", {"start": v(62.1, -117.49) * mm, "end": v(61.48, -111.01) * mm});
            skLineSegment(sketch, "E4229", {"start": v(61.48, -111.01) * mm, "end": v(61.3, -109.72) * mm});
            skLineSegment(sketch, "E4230", {"start": v(61.3, -109.72) * mm, "end": v(61.26, -109.47) * mm});
            skLineSegment(sketch, "E4231", {"start": v(61.26, -109.47) * mm, "end": v(61.04, -106.82) * mm});
            skLineSegment(sketch, "E4232", {"start": v(61.04, -106.82) * mm, "end": v(61.01, -106.54) * mm});
            skLineSegment(sketch, "E4233", {"start": v(138.32, -105) * mm, "end": v(138.45, -105.06) * mm});
            skLineSegment(sketch, "E4234", {"start": v(138.45, -105.06) * mm, "end": v(138.9, -105.16) * mm});
            skLineSegment(sketch, "E4235", {"start": v(138.9, -105.16) * mm, "end": v(139.44, -105.04) * mm});
            skLineSegment(sketch, "E4236", {"start": v(139.44, -105.04) * mm, "end": v(139.94, -104.74) * mm});
            skLineSegment(sketch, "E4237", {"start": v(139.94, -104.74) * mm, "end": v(140.31, -104.45) * mm});
            skLineSegment(sketch, "E4238", {"start": v(140.31, -104.45) * mm, "end": v(140.43, -104.36) * mm});
            skLineSegment(sketch, "E4239", {"start": v(140.43, -104.36) * mm, "end": v(140.58, -104.24) * mm});
            skLineSegment(sketch, "E4240", {"start": v(140.58, -104.24) * mm, "end": v(142.04, -103.06) * mm});
            skLineSegment(sketch, "E4241", {"start": v(142.04, -103.06) * mm, "end": v(142.2, -102.95) * mm});
            skLineSegment(sketch, "E4242", {"start": v(142.2, -102.95) * mm, "end": v(142.34, -102.85) * mm});
            skLineSegment(sketch, "E4243", {"start": v(142.34, -102.85) * mm, "end": v(142.71, -102.47) * mm});
            skLineSegment(sketch, "E4244", {"start": v(142.71, -102.47) * mm, "end": v(142.97, -101.93) * mm});
            skLineSegment(sketch, "E4245", {"start": v(142.97, -101.93) * mm, "end": v(143, -101.33) * mm});
            skLineSegment(sketch, "E4246", {"start": v(143, -101.33) * mm, "end": v(142.87, -100.8) * mm});
            skLineSegment(sketch, "E4247", {"start": v(142.87, -100.8) * mm, "end": v(142.81, -100.64) * mm});
            skLineSegment(sketch, "E4248", {"start": v(142.81, -100.64) * mm, "end": v(142.2, -99.1) * mm});
            skLineSegment(sketch, "E4249", {"start": v(142.2, -99.1) * mm, "end": v(136.23, -83.62) * mm});
            skLineSegment(sketch, "E4250", {"start": v(136.23, -83.62) * mm, "end": v(135.64, -82.07) * mm});
            skLineSegment(sketch, "E4251", {"start": v(135.64, -82.07) * mm, "end": v(135.57, -81.88) * mm});
            skLineSegment(sketch, "E4252", {"start": v(135.57, -81.88) * mm, "end": v(135.05, -81.28) * mm});
            skLineSegment(sketch, "E4253", {"start": v(135.05, -81.28) * mm, "end": v(134.27, -81.15) * mm});
            skLineSegment(sketch, "E4254", {"start": v(134.27, -81.15) * mm, "end": v(134.07, -81.19) * mm});
            skLineSegment(sketch, "E4255", {"start": v(134.07, -81.19) * mm, "end": v(133.47, -81.31) * mm});
            skLineSegment(sketch, "E4256", {"start": v(133.47, -81.31) * mm, "end": v(131.7, -81.89) * mm});
            skLineSegment(sketch, "E4257", {"start": v(131.7, -81.89) * mm, "end": v(129.62, -82.99) * mm});
            skLineSegment(sketch, "E4258", {"start": v(129.62, -82.99) * mm, "end": v(127.84, -84.52) * mm});
            skLineSegment(sketch, "E4259", {"start": v(127.84, -84.52) * mm, "end": v(126.7, -85.98) * mm});
            skLineSegment(sketch, "E4260", {"start": v(126.7, -85.98) * mm, "end": v(126.4, -86.5) * mm});
            skLineSegment(sketch, "E4261", {"start": v(126.4, -86.5) * mm, "end": v(126.06, -87.09) * mm});
            skLineSegment(sketch, "E4262", {"start": v(126.06, -87.09) * mm, "end": v(122.94, -92.98) * mm});
            skLineSegment(sketch, "E4263", {"start": v(122.94, -92.98) * mm, "end": v(122.63, -93.57) * mm});
            skLineSegment(sketch, "E4264", {"start": v(122.63, -93.57) * mm, "end": v(122.52, -93.78) * mm});
            skLineSegment(sketch, "E4265", {"start": v(122.52, -93.78) * mm, "end": v(122.21, -94.43) * mm});
            skLineSegment(sketch, "E4266", {"start": v(122.21, -94.43) * mm, "end": v(122.14, -94.97) * mm});
            skLineSegment(sketch, "E4267", {"start": v(122.14, -94.97) * mm, "end": v(122.47, -95.42) * mm});
            skLineSegment(sketch, "E4268", {"start": v(122.47, -95.42) * mm, "end": v(123.06, -95.85) * mm});
            skLineSegment(sketch, "E4269", {"start": v(123.06, -95.85) * mm, "end": v(123.26, -96) * mm});
            skLineSegment(sketch, "E4270", {"start": v(123.26, -96) * mm, "end": v(124.29, -96.68) * mm});
            skLineSegment(sketch, "E4271", {"start": v(124.29, -96.68) * mm, "end": v(134.5, -103.55) * mm});
            skLineSegment(sketch, "E4272", {"start": v(134.5, -103.55) * mm, "end": v(135.53, -104.24) * mm});
            skLineSegment(sketch, "E4273", {"start": v(135.53, -104.24) * mm, "end": v(135.73, -104.38) * mm});
            skLineSegment(sketch, "E4274", {"start": v(135.73, -104.38) * mm, "end": v(136.8, -104.9) * mm});
            skLineSegment(sketch, "E4275", {"start": v(136.8, -104.9) * mm, "end": v(138.04, -105.04) * mm});
            skLineSegment(sketch, "E4276", {"start": v(138.04, -105.04) * mm, "end": v(138.32, -105) * mm});
            skLineSegment(sketch, "E4277", {"start": v(156.26, -95.05) * mm, "end": v(156.55, -94.82) * mm});
            skLineSegment(sketch, "E4278", {"start": v(156.55, -94.82) * mm, "end": v(157.27, -93.9) * mm});
            skLineSegment(sketch, "E4279", {"start": v(157.27, -93.9) * mm, "end": v(157.8, -92.58) * mm});
            skLineSegment(sketch, "E4280", {"start": v(157.8, -92.58) * mm, "end": v(158.1, -91.16) * mm});
            skLineSegment(sketch, "E4281", {"start": v(158.1, -91.16) * mm, "end": v(158.28, -90.08) * mm});
            skLineSegment(sketch, "E4282", {"start": v(158.28, -90.08) * mm, "end": v(158.36, -89.72) * mm});
            skLineSegment(sketch, "E4283", {"start": v(158.36, -89.72) * mm, "end": v(158.38, -89.64) * mm});
            skLineSegment(sketch, "E4284", {"start": v(158.38, -89.64) * mm, "end": v(158.37, -88.78) * mm});
            skLineSegment(sketch, "E4285", {"start": v(158.37, -88.78) * mm, "end": v(158.38, -88.7) * mm});
            skLineSegment(sketch, "E4286", {"start": v(158.38, -88.7) * mm, "end": v(158.38, -88.52) * mm});
            skLineSegment(sketch, "E4287", {"start": v(158.38, -88.52) * mm, "end": v(158.7, -87.83) * mm});
            skLineSegment(sketch, "E4288", {"start": v(158.7, -87.83) * mm, "end": v(159.33, -87.45) * mm});
            skLineSegment(sketch, "E4289", {"start": v(159.33, -87.45) * mm, "end": v(159.48, -87.43) * mm});
            skLineSegment(sketch, "E4290", {"start": v(159.48, -87.43) * mm, "end": v(159.56, -87.42) * mm});
            skLineSegment(sketch, "E4291", {"start": v(159.56, -87.42) * mm, "end": v(159.84, -87.5) * mm});
            skLineSegment(sketch, "E4292", {"start": v(159.84, -87.5) * mm, "end": v(160.06, -87.77) * mm});
            skLineSegment(sketch, "E4293", {"start": v(160.06, -87.77) * mm, "end": v(160.18, -88.13) * mm});
            skLineSegment(sketch, "E4294", {"start": v(160.18, -88.13) * mm, "end": v(160.23, -88.38) * mm});
            skLineSegment(sketch, "E4295", {"start": v(160.23, -88.38) * mm, "end": v(160.25, -88.46) * mm});
            skLineSegment(sketch, "E4296", {"start": v(160.25, -88.46) * mm, "end": v(160.35, -88.93) * mm});
            skLineSegment(sketch, "E4297", {"start": v(160.35, -88.93) * mm, "end": v(161.17, -93.62) * mm});
            skLineSegment(sketch, "E4298", {"start": v(161.17, -93.62) * mm, "end": v(161.26, -94.09) * mm});
            skLineSegment(sketch, "E4299", {"start": v(161.26, -94.09) * mm, "end": v(161.29, -94.25) * mm});
            skLineSegment(sketch, "E4300", {"start": v(161.29, -94.25) * mm, "end": v(161.15, -94.88) * mm});
            skLineSegment(sketch, "E4301", {"start": v(161.15, -94.88) * mm, "end": v(160.72, -95.36) * mm});
            skLineSegment(sketch, "E4302", {"start": v(160.72, -95.36) * mm, "end": v(160.61, -95.45) * mm});
            skLineSegment(sketch, "E4303", {"start": v(160.61, -95.45) * mm, "end": v(160.32, -95.7) * mm});
            skLineSegment(sketch, "E4304", {"start": v(160.32, -95.7) * mm, "end": v(158.68, -96.61) * mm});
            skLineSegment(sketch, "E4305", {"start": v(158.68, -96.61) * mm, "end": v(157, -97.44) * mm});
            skLineSegment(sketch, "E4306", {"start": v(157, -97.44) * mm, "end": v(156.68, -97.64) * mm});
            skLineSegment(sketch, "E4307", {"start": v(156.68, -97.64) * mm, "end": v(155.72, -97.98) * mm});
            skLineSegment(sketch, "E4308", {"start": v(155.72, -97.98) * mm, "end": v(151.13, -100.07) * mm});
            skLineSegment(sketch, "E4309", {"start": v(151.13, -100.07) * mm, "end": v(146.72, -102.5) * mm});
            skLineSegment(sketch, "E4310", {"start": v(146.72, -102.5) * mm, "end": v(145.85, -103.02) * mm});
            skLineSegment(sketch, "E4311", {"start": v(145.85, -103.02) * mm, "end": v(145, -103.52) * mm});
            skLineSegment(sketch, "E4312", {"start": v(145, -103.52) * mm, "end": v(140.73, -105.83) * mm});
            skLineSegment(sketch, "E4313", {"start": v(140.73, -105.83) * mm, "end": v(136.26, -107.74) * mm});
            skLineSegment(sketch, "E4314", {"start": v(136.26, -107.74) * mm, "end": v(135.33, -108.05) * mm});
            skLineSegment(sketch, "E4315", {"start": v(135.33, -108.05) * mm, "end": v(134.8, -108.22) * mm});
            skLineSegment(sketch, "E4316", {"start": v(134.8, -108.22) * mm, "end": v(129.6, -110.43) * mm});
            skLineSegment(sketch, "E4317", {"start": v(129.6, -110.43) * mm, "end": v(129.1, -110.7) * mm});
            skLineSegment(sketch, "E4318", {"start": v(129.1, -110.7) * mm, "end": v(129.01, -110.76) * mm});
            skLineSegment(sketch, "E4319", {"start": v(129.01, -110.76) * mm, "end": v(128.73, -110.94) * mm});
            skLineSegment(sketch, "E4320", {"start": v(128.73, -110.94) * mm, "end": v(128.31, -111.14) * mm});
            skLineSegment(sketch, "E4321", {"start": v(128.31, -111.14) * mm, "end": v(127.9, -111.16) * mm});
            skLineSegment(sketch, "E4322", {"start": v(127.9, -111.16) * mm, "end": v(127.57, -110.92) * mm});
            skLineSegment(sketch, "E4323", {"start": v(127.57, -110.92) * mm, "end": v(127.5, -110.82) * mm});
            skLineSegment(sketch, "E4324", {"start": v(127.5, -110.82) * mm, "end": v(127.44, -110.72) * mm});
            skLineSegment(sketch, "E4325", {"start": v(127.44, -110.72) * mm, "end": v(127.36, -110.37) * mm});
            skLineSegment(sketch, "E4326", {"start": v(127.36, -110.37) * mm, "end": v(127.47, -109.95) * mm});
            skLineSegment(sketch, "E4327", {"start": v(127.47, -109.95) * mm, "end": v(127.72, -109.56) * mm});
            skLineSegment(sketch, "E4328", {"start": v(127.72, -109.56) * mm, "end": v(127.96, -109.28) * mm});
            skLineSegment(sketch, "E4329", {"start": v(127.96, -109.28) * mm, "end": v(128.03, -109.2) * mm});
            skLineSegment(sketch, "E4330", {"start": v(128.03, -109.2) * mm, "end": v(128.08, -109.14) * mm});
            skLineSegment(sketch, "E4331", {"start": v(128.08, -109.14) * mm, "end": v(128.57, -108.66) * mm});
            skLineSegment(sketch, "E4332", {"start": v(128.57, -108.66) * mm, "end": v(128.62, -108.61) * mm});
            skLineSegment(sketch, "E4333", {"start": v(128.62, -108.61) * mm, "end": v(128.78, -108.44) * mm});
            skLineSegment(sketch, "E4334", {"start": v(128.78, -108.44) * mm, "end": v(129.23, -107.88) * mm});
            skLineSegment(sketch, "E4335", {"start": v(129.23, -107.88) * mm, "end": v(129.4, -107.3) * mm});
            skLineSegment(sketch, "E4336", {"start": v(129.4, -107.3) * mm, "end": v(129.13, -106.8) * mm});
            skLineSegment(sketch, "E4337", {"start": v(129.13, -106.8) * mm, "end": v(128.58, -106.43) * mm});
            skLineSegment(sketch, "E4338", {"start": v(128.58, -106.43) * mm, "end": v(128.38, -106.34) * mm});
            skLineSegment(sketch, "E4339", {"start": v(128.38, -106.34) * mm, "end": v(127.65, -106.01) * mm});
            skLineSegment(sketch, "E4340", {"start": v(127.65, -106.01) * mm, "end": v(124.39, -103.85) * mm});
            skLineSegment(sketch, "E4341", {"start": v(124.39, -103.85) * mm, "end": v(121.17, -101.62) * mm});
            skLineSegment(sketch, "E4342", {"start": v(121.17, -101.62) * mm, "end": v(120.48, -101.25) * mm});
            skLineSegment(sketch, "E4343", {"start": v(120.48, -101.25) * mm, "end": v(120.32, -101.17) * mm});
            skLineSegment(sketch, "E4344", {"start": v(120.32, -101.17) * mm, "end": v(119.53, -100.7) * mm});
            skLineSegment(sketch, "E4345", {"start": v(119.53, -100.7) * mm, "end": v(118.7, -100.31) * mm});
            skLineSegment(sketch, "E4346", {"start": v(118.7, -100.31) * mm, "end": v(118.52, -100.28) * mm});
            skLineSegment(sketch, "E4347", {"start": v(118.52, -100.28) * mm, "end": v(118.45, -100.42) * mm});
            skLineSegment(sketch, "E4348", {"start": v(118.45, -100.42) * mm, "end": v(118.37, -101.06) * mm});
            skLineSegment(sketch, "E4349", {"start": v(118.37, -101.06) * mm, "end": v(118.5, -101.65) * mm});
            skLineSegment(sketch, "E4350", {"start": v(118.5, -101.65) * mm, "end": v(118.54, -101.76) * mm});
            skLineSegment(sketch, "E4351", {"start": v(118.54, -101.76) * mm, "end": v(118.76, -102.41) * mm});
            skLineSegment(sketch, "E4352", {"start": v(118.76, -102.41) * mm, "end": v(120.79, -108.96) * mm});
            skLineSegment(sketch, "E4353", {"start": v(120.79, -108.96) * mm, "end": v(120.93, -109.63) * mm});
            skLineSegment(sketch, "E4354", {"start": v(120.93, -109.63) * mm, "end": v(120.97, -109.79) * mm});
            skLineSegment(sketch, "E4355", {"start": v(120.97, -109.79) * mm, "end": v(121.16, -110.25) * mm});
            skLineSegment(sketch, "E4356", {"start": v(121.16, -110.25) * mm, "end": v(121.54, -110.65) * mm});
            skLineSegment(sketch, "E4357", {"start": v(121.54, -110.65) * mm, "end": v(122.05, -110.85) * mm});
            skLineSegment(sketch, "E4358", {"start": v(122.05, -110.85) * mm, "end": v(122.55, -110.88) * mm});
            skLineSegment(sketch, "E4359", {"start": v(122.55, -110.88) * mm, "end": v(122.7, -110.87) * mm});
            skLineSegment(sketch, "E4360", {"start": v(122.7, -110.87) * mm, "end": v(122.84, -110.85) * mm});
            skLineSegment(sketch, "E4361", {"start": v(122.84, -110.85) * mm, "end": v(124.21, -110.84) * mm});
            skLineSegment(sketch, "E4362", {"start": v(124.21, -110.84) * mm, "end": v(124.35, -110.85) * mm});
            skLineSegment(sketch, "E4363", {"start": v(124.35, -110.85) * mm, "end": v(124.46, -110.85) * mm});
            skLineSegment(sketch, "E4364", {"start": v(124.46, -110.85) * mm, "end": v(124.94, -110.97) * mm});
            skLineSegment(sketch, "E4365", {"start": v(124.94, -110.97) * mm, "end": v(125.27, -111.33) * mm});
            skLineSegment(sketch, "E4366", {"start": v(125.27, -111.33) * mm, "end": v(125.3, -111.46) * mm});
            skLineSegment(sketch, "E4367", {"start": v(125.3, -111.46) * mm, "end": v(125.32, -111.6) * mm});
            skLineSegment(sketch, "E4368", {"start": v(125.32, -111.6) * mm, "end": v(125.23, -112.15) * mm});
            skLineSegment(sketch, "E4369", {"start": v(125.23, -112.15) * mm, "end": v(124.81, -112.53) * mm});
            skLineSegment(sketch, "E4370", {"start": v(124.81, -112.53) * mm, "end": v(124.68, -112.59) * mm});
            skLineSegment(sketch, "E4371", {"start": v(124.68, -112.59) * mm, "end": v(124.31, -112.73) * mm});
            skLineSegment(sketch, "E4372", {"start": v(124.31, -112.73) * mm, "end": v(120.64, -114.16) * mm});
            skLineSegment(sketch, "E4373", {"start": v(120.64, -114.16) * mm, "end": v(120.27, -114.3) * mm});
            skLineSegment(sketch, "E4374", {"start": v(120.27, -114.3) * mm, "end": v(119.67, -114.5) * mm});
            skLineSegment(sketch, "E4375", {"start": v(119.67, -114.5) * mm, "end": v(116.77, -115.77) * mm});
            skLineSegment(sketch, "E4376", {"start": v(116.77, -115.77) * mm, "end": v(113.9, -117.12) * mm});
            skLineSegment(sketch, "E4377", {"start": v(113.9, -117.12) * mm, "end": v(113.32, -117.37) * mm});
            skLineSegment(sketch, "E4378", {"start": v(113.32, -117.37) * mm, "end": v(113.22, -117.42) * mm});
            skLineSegment(sketch, "E4379", {"start": v(113.22, -117.42) * mm, "end": v(112.93, -117.57) * mm});
            skLineSegment(sketch, "E4380", {"start": v(112.93, -117.57) * mm, "end": v(112.53, -117.73) * mm});
            skLineSegment(sketch, "E4381", {"start": v(112.53, -117.73) * mm, "end": v(112.13, -117.7) * mm});
            skLineSegment(sketch, "E4382", {"start": v(112.13, -117.7) * mm, "end": v(111.8, -117.4) * mm});
            skLineSegment(sketch, "E4383", {"start": v(111.8, -117.4) * mm, "end": v(111.74, -117.29) * mm});
            skLineSegment(sketch, "E4384", {"start": v(111.74, -117.29) * mm, "end": v(111.64, -117.11) * mm});
            skLineSegment(sketch, "E4385", {"start": v(111.64, -117.11) * mm, "end": v(111.59, -116.4) * mm});
            skLineSegment(sketch, "E4386", {"start": v(111.59, -116.4) * mm, "end": v(111.98, -115.79) * mm});
            skLineSegment(sketch, "E4387", {"start": v(111.98, -115.79) * mm, "end": v(112.1, -115.67) * mm});
            skLineSegment(sketch, "E4388", {"start": v(112.1, -115.67) * mm, "end": v(112.28, -115.5) * mm});
            skLineSegment(sketch, "E4389", {"start": v(112.28, -115.5) * mm, "end": v(114, -113.84) * mm});
            skLineSegment(sketch, "E4390", {"start": v(114, -113.84) * mm, "end": v(114.2, -113.69) * mm});
            skLineSegment(sketch, "E4391", {"start": v(114.2, -113.69) * mm, "end": v(114.4, -113.5) * mm});
            skLineSegment(sketch, "E4392", {"start": v(114.4, -113.5) * mm, "end": v(115, -112.52) * mm});
            skLineSegment(sketch, "E4393", {"start": v(115, -112.52) * mm, "end": v(115.04, -111.37) * mm});
            skLineSegment(sketch, "E4394", {"start": v(115.04, -111.37) * mm, "end": v(114.97, -111.11) * mm});
            skLineSegment(sketch, "E4395", {"start": v(114.97, -111.11) * mm, "end": v(114.68, -110.04) * mm});
            skLineSegment(sketch, "E4396", {"start": v(114.68, -110.04) * mm, "end": v(111.72, -99.3) * mm});
            skLineSegment(sketch, "E4397", {"start": v(111.72, -99.3) * mm, "end": v(111.42, -98.24) * mm});
            skLineSegment(sketch, "E4398", {"start": v(111.42, -98.24) * mm, "end": v(111.3, -97.76) * mm});
            skLineSegment(sketch, "E4399", {"start": v(111.3, -97.76) * mm, "end": v(109.98, -92.98) * mm});
            skLineSegment(sketch, "E4400", {"start": v(109.98, -92.98) * mm, "end": v(109.82, -92.51) * mm});
            skLineSegment(sketch, "E4401", {"start": v(109.82, -92.51) * mm, "end": v(109.72, -92.2) * mm});
            skLineSegment(sketch, "E4402", {"start": v(109.72, -92.2) * mm, "end": v(109.36, -91.32) * mm});
            skLineSegment(sketch, "E4403", {"start": v(109.36, -91.32) * mm, "end": v(108.8, -90.65) * mm});
            skLineSegment(sketch, "E4404", {"start": v(108.8, -90.65) * mm, "end": v(107.99, -90.34) * mm});
            skLineSegment(sketch, "E4405", {"start": v(107.99, -90.34) * mm, "end": v(107.04, -90.25) * mm});
            skLineSegment(sketch, "E4406", {"start": v(107.04, -90.25) * mm, "end": v(106.72, -90.24) * mm});
            skLineSegment(sketch, "E4407", {"start": v(106.72, -90.24) * mm, "end": v(106.6, -90.24) * mm});
            skLineSegment(sketch, "E4408", {"start": v(106.6, -90.24) * mm, "end": v(105.4, -90.25) * mm});
            skLineSegment(sketch, "E4409", {"start": v(105.4, -90.25) * mm, "end": v(105.28, -90.24) * mm});
            skLineSegment(sketch, "E4410", {"start": v(105.28, -90.24) * mm, "end": v(105.17, -90.24) * mm});
            skLineSegment(sketch, "E4411", {"start": v(105.17, -90.24) * mm, "end": v(104.7, -90.1) * mm});
            skLineSegment(sketch, "E4412", {"start": v(104.7, -90.1) * mm, "end": v(104.41, -89.72) * mm});
            skLineSegment(sketch, "E4413", {"start": v(104.41, -89.72) * mm, "end": v(104.4, -89.59) * mm});
            skLineSegment(sketch, "E4414", {"start": v(104.4, -89.59) * mm, "end": v(104.38, -89.47) * mm});
            skLineSegment(sketch, "E4415", {"start": v(104.38, -89.47) * mm, "end": v(104.44, -88.98) * mm});
            skLineSegment(sketch, "E4416", {"start": v(104.44, -88.98) * mm, "end": v(104.77, -88.62) * mm});
            skLineSegment(sketch, "E4417", {"start": v(104.77, -88.62) * mm, "end": v(104.88, -88.58) * mm});
            skLineSegment(sketch, "E4418", {"start": v(104.88, -88.58) * mm, "end": v(105.01, -88.53) * mm});
            skLineSegment(sketch, "E4419", {"start": v(105.01, -88.53) * mm, "end": v(106.3, -88.04) * mm});
            skLineSegment(sketch, "E4420", {"start": v(106.3, -88.04) * mm, "end": v(106.43, -88.01) * mm});
            skLineSegment(sketch, "E4421", {"start": v(106.43, -88.01) * mm, "end": v(107.28, -87.83) * mm});
            skLineSegment(sketch, "E4422", {"start": v(107.28, -87.83) * mm, "end": v(111.47, -86.58) * mm});
            skLineSegment(sketch, "E4423", {"start": v(111.47, -86.58) * mm, "end": v(115.6, -85.16) * mm});
            skLineSegment(sketch, "E4424", {"start": v(115.6, -85.16) * mm, "end": v(116.43, -84.9) * mm});
            skLineSegment(sketch, "E4425", {"start": v(116.43, -84.9) * mm, "end": v(116.5, -84.88) * mm});
            skLineSegment(sketch, "E4426", {"start": v(116.5, -84.88) * mm, "end": v(117.32, -84.6) * mm});
            skLineSegment(sketch, "E4427", {"start": v(117.32, -84.6) * mm, "end": v(117.4, -84.57) * mm});
            skLineSegment(sketch, "E4428", {"start": v(117.4, -84.57) * mm, "end": v(117.5, -84.54) * mm});
            skLineSegment(sketch, "E4429", {"start": v(117.5, -84.54) * mm, "end": v(118, -84.5) * mm});
            skLineSegment(sketch, "E4430", {"start": v(118, -84.5) * mm, "end": v(118.42, -84.73) * mm});
            skLineSegment(sketch, "E4431", {"start": v(118.42, -84.73) * mm, "end": v(118.5, -84.84) * mm});
            skLineSegment(sketch, "E4432", {"start": v(118.5, -84.84) * mm, "end": v(118.58, -84.97) * mm});
            skLineSegment(sketch, "E4433", {"start": v(118.58, -84.97) * mm, "end": v(118.61, -85.54) * mm});
            skLineSegment(sketch, "E4434", {"start": v(118.61, -85.54) * mm, "end": v(118.26, -85.99) * mm});
            skLineSegment(sketch, "E4435", {"start": v(118.26, -85.99) * mm, "end": v(118.15, -86.06) * mm});
            skLineSegment(sketch, "E4436", {"start": v(118.15, -86.06) * mm, "end": v(117.98, -86.17) * mm});
            skLineSegment(sketch, "E4437", {"start": v(117.98, -86.17) * mm, "end": v(116.23, -87.25) * mm});
            skLineSegment(sketch, "E4438", {"start": v(116.23, -87.25) * mm, "end": v(116.06, -87.36) * mm});
            skLineSegment(sketch, "E4439", {"start": v(116.06, -87.36) * mm, "end": v(115.95, -87.43) * mm});
            skLineSegment(sketch, "E4440", {"start": v(115.95, -87.43) * mm, "end": v(115.64, -87.68) * mm});
            skLineSegment(sketch, "E4441", {"start": v(115.64, -87.68) * mm, "end": v(115.3, -88.05) * mm});
            skLineSegment(sketch, "E4442", {"start": v(115.3, -88.05) * mm, "end": v(115.13, -88.5) * mm});
            skLineSegment(sketch, "E4443", {"start": v(115.13, -88.5) * mm, "end": v(115.13, -88.92) * mm});
            skLineSegment(sketch, "E4444", {"start": v(115.13, -88.92) * mm, "end": v(115.17, -89.05) * mm});
            skLineSegment(sketch, "E4445", {"start": v(115.17, -89.05) * mm, "end": v(115.37, -89.78) * mm});
            skLineSegment(sketch, "E4446", {"start": v(115.37, -89.78) * mm, "end": v(116.4, -93.5) * mm});
            skLineSegment(sketch, "E4447", {"start": v(116.4, -93.5) * mm, "end": v(117.52, -97.48) * mm});
            skLineSegment(sketch, "E4448", {"start": v(117.52, -97.48) * mm, "end": v(117.76, -98.34) * mm});
            skLineSegment(sketch, "E4449", {"start": v(117.76, -98.34) * mm, "end": v(118.05, -97.78) * mm});
            skLineSegment(sketch, "E4450", {"start": v(118.05, -97.78) * mm, "end": v(119.36, -95.25) * mm});
            skLineSegment(sketch, "E4451", {"start": v(119.36, -95.25) * mm, "end": v(120.55, -92.93) * mm});
            skLineSegment(sketch, "E4452", {"start": v(120.55, -92.93) * mm, "end": v(120.77, -92.48) * mm});
            skLineSegment(sketch, "E4453", {"start": v(120.77, -92.48) * mm, "end": v(121.01, -91.98) * mm});
            skLineSegment(sketch, "E4454", {"start": v(121.01, -91.98) * mm, "end": v(123.35, -87.05) * mm});
            skLineSegment(sketch, "E4455", {"start": v(123.35, -87.05) * mm, "end": v(123.6, -86.56) * mm});
            skLineSegment(sketch, "E4456", {"start": v(123.6, -86.56) * mm, "end": v(123.66, -86.42) * mm});
            skLineSegment(sketch, "E4457", {"start": v(123.66, -86.42) * mm, "end": v(124.02, -85.71) * mm});
            skLineSegment(sketch, "E4458", {"start": v(124.02, -85.71) * mm, "end": v(124.05, -85) * mm});
            skLineSegment(sketch, "E4459", {"start": v(124.05, -85) * mm, "end": v(123.96, -84.86) * mm});
            skLineSegment(sketch, "E4460", {"start": v(123.96, -84.86) * mm, "end": v(123.9, -84.77) * mm});
            skLineSegment(sketch, "E4461", {"start": v(123.9, -84.77) * mm, "end": v(123.62, -84.6) * mm});
            skLineSegment(sketch, "E4462", {"start": v(123.62, -84.6) * mm, "end": v(123.24, -84.62) * mm});
            skLineSegment(sketch, "E4463", {"start": v(123.24, -84.62) * mm, "end": v(122.83, -84.75) * mm});
            skLineSegment(sketch, "E4464", {"start": v(122.83, -84.75) * mm, "end": v(122.53, -84.85) * mm});
            skLineSegment(sketch, "E4465", {"start": v(122.53, -84.85) * mm, "end": v(122.43, -84.87) * mm});
            skLineSegment(sketch, "E4466", {"start": v(122.43, -84.87) * mm, "end": v(122.26, -84.9) * mm});
            skLineSegment(sketch, "E4467", {"start": v(122.26, -84.9) * mm, "end": v(121.74, -84.94) * mm});
            skLineSegment(sketch, "E4468", {"start": v(121.74, -84.94) * mm, "end": v(121.12, -84.85) * mm});
            skLineSegment(sketch, "E4469", {"start": v(121.12, -84.85) * mm, "end": v(120.62, -84.51) * mm});
            skLineSegment(sketch, "E4470", {"start": v(120.62, -84.51) * mm, "end": v(120.31, -84.04) * mm});
            skLineSegment(sketch, "E4471", {"start": v(120.31, -84.04) * mm, "end": v(120.26, -83.87) * mm});
            skLineSegment(sketch, "E4472", {"start": v(120.26, -83.87) * mm, "end": v(120.36, -83.78) * mm});
            skLineSegment(sketch, "E4473", {"start": v(120.36, -83.78) * mm, "end": v(120.93, -83.48) * mm});
            skLineSegment(sketch, "E4474", {"start": v(120.93, -83.48) * mm, "end": v(121.56, -83.28) * mm});
            skLineSegment(sketch, "E4475", {"start": v(121.56, -83.28) * mm, "end": v(121.7, -83.25) * mm});
            skLineSegment(sketch, "E4476", {"start": v(121.7, -83.25) * mm, "end": v(122.08, -83.14) * mm});
            skLineSegment(sketch, "E4477", {"start": v(122.08, -83.14) * mm, "end": v(125.8, -81.88) * mm});
            skLineSegment(sketch, "E4478", {"start": v(125.8, -81.88) * mm, "end": v(126.17, -81.75) * mm});
            skLineSegment(sketch, "E4479", {"start": v(126.17, -81.75) * mm, "end": v(126.7, -81.55) * mm});
            skLineSegment(sketch, "E4480", {"start": v(126.7, -81.55) * mm, "end": v(129.27, -80.52) * mm});
            skLineSegment(sketch, "E4481", {"start": v(129.27, -80.52) * mm, "end": v(131.95, -79.7) * mm});
            skLineSegment(sketch, "E4482", {"start": v(131.95, -79.7) * mm, "end": v(132.52, -79.62) * mm});
            skLineSegment(sketch, "E4483", {"start": v(132.52, -79.62) * mm, "end": v(133.15, -79.52) * mm});
            skLineSegment(sketch, "E4484", {"start": v(133.15, -79.52) * mm, "end": v(136.1, -78.42) * mm});
            skLineSegment(sketch, "E4485", {"start": v(136.1, -78.42) * mm, "end": v(138.95, -76.97) * mm});
            skLineSegment(sketch, "E4486", {"start": v(138.95, -76.97) * mm, "end": v(139.53, -76.7) * mm});
            skLineSegment(sketch, "E4487", {"start": v(139.53, -76.7) * mm, "end": v(140.44, -76.27) * mm});
            skLineSegment(sketch, "E4488", {"start": v(140.44, -76.27) * mm, "end": v(145.04, -74.18) * mm});
            skLineSegment(sketch, "E4489", {"start": v(145.04, -74.18) * mm, "end": v(149.6, -71.99) * mm});
            skLineSegment(sketch, "E4490", {"start": v(149.6, -71.99) * mm, "end": v(150.48, -71.5) * mm});
            skLineSegment(sketch, "E4491", {"start": v(150.48, -71.5) * mm, "end": v(150.74, -71.41) * mm});
            skLineSegment(sketch, "E4492", {"start": v(150.74, -71.41) * mm, "end": v(151.5, -71.16) * mm});
            skLineSegment(sketch, "E4493", {"start": v(151.5, -71.16) * mm, "end": v(152.11, -71.13) * mm});
            skLineSegment(sketch, "E4494", {"start": v(152.11, -71.13) * mm, "end": v(152.5, -71.52) * mm});
            skLineSegment(sketch, "E4495", {"start": v(152.5, -71.52) * mm, "end": v(152.8, -72.17) * mm});
            skLineSegment(sketch, "E4496", {"start": v(152.8, -72.17) * mm, "end": v(152.88, -72.4) * mm});
            skLineSegment(sketch, "E4497", {"start": v(152.88, -72.4) * mm, "end": v(153, -72.68) * mm});
            skLineSegment(sketch, "E4498", {"start": v(153, -72.68) * mm, "end": v(154.07, -75.52) * mm});
            skLineSegment(sketch, "E4499", {"start": v(154.07, -75.52) * mm, "end": v(154.16, -75.81) * mm});
            skLineSegment(sketch, "E4500", {"start": v(154.16, -75.81) * mm, "end": v(154.22, -75.98) * mm});
            skLineSegment(sketch, "E4501", {"start": v(154.22, -75.98) * mm, "end": v(154.35, -76.51) * mm});
            skLineSegment(sketch, "E4502", {"start": v(154.35, -76.51) * mm, "end": v(154.27, -76.93) * mm});
            skLineSegment(sketch, "E4503", {"start": v(154.27, -76.93) * mm, "end": v(153.84, -77.2) * mm});
            skLineSegment(sketch, "E4504", {"start": v(153.84, -77.2) * mm, "end": v(153.2, -77.4) * mm});
            skLineSegment(sketch, "E4505", {"start": v(153.2, -77.4) * mm, "end": v(152.98, -77.46) * mm});
            skLineSegment(sketch, "E4506", {"start": v(152.98, -77.46) * mm, "end": v(152.84, -77.18) * mm});
            skLineSegment(sketch, "E4507", {"start": v(152.84, -77.18) * mm, "end": v(151.93, -76.08) * mm});
            skLineSegment(sketch, "E4508", {"start": v(151.93, -76.08) * mm, "end": v(150.84, -75.13) * mm});
            skLineSegment(sketch, "E4509", {"start": v(150.84, -75.13) * mm, "end": v(150.62, -74.94) * mm});
            skLineSegment(sketch, "E4510", {"start": v(150.62, -74.94) * mm, "end": v(150.48, -74.82) * mm});
            skLineSegment(sketch, "E4511", {"start": v(150.48, -74.82) * mm, "end": v(149.74, -74.51) * mm});
            skLineSegment(sketch, "E4512", {"start": v(149.74, -74.51) * mm, "end": v(148.92, -74.56) * mm});
            skLineSegment(sketch, "E4513", {"start": v(148.92, -74.56) * mm, "end": v(148.73, -74.62) * mm});
            skLineSegment(sketch, "E4514", {"start": v(148.73, -74.62) * mm, "end": v(148.09, -74.81) * mm});
            skLineSegment(sketch, "E4515", {"start": v(148.09, -74.81) * mm, "end": v(145, -76.02) * mm});
            skLineSegment(sketch, "E4516", {"start": v(145, -76.02) * mm, "end": v(141.98, -77.41) * mm});
            skLineSegment(sketch, "E4517", {"start": v(141.98, -77.41) * mm, "end": v(141.38, -77.7) * mm});
            skLineSegment(sketch, "E4518", {"start": v(141.38, -77.7) * mm, "end": v(141.23, -77.76) * mm});
            skLineSegment(sketch, "E4519", {"start": v(141.23, -77.76) * mm, "end": v(140.84, -78.03) * mm});
            skLineSegment(sketch, "E4520", {"start": v(140.84, -78.03) * mm, "end": v(140.55, -78.44) * mm});
            skLineSegment(sketch, "E4521", {"start": v(140.55, -78.44) * mm, "end": v(140.49, -78.92) * mm});
            skLineSegment(sketch, "E4522", {"start": v(140.49, -78.92) * mm, "end": v(140.58, -79.36) * mm});
            skLineSegment(sketch, "E4523", {"start": v(140.58, -79.36) * mm, "end": v(140.63, -79.5) * mm});
            skLineSegment(sketch, "E4524", {"start": v(140.63, -79.5) * mm, "end": v(140.86, -80.1) * mm});
            skLineSegment(sketch, "E4525", {"start": v(140.86, -80.1) * mm, "end": v(143.2, -86.14) * mm});
            skLineSegment(sketch, "E4526", {"start": v(143.2, -86.14) * mm, "end": v(143.43, -86.75) * mm});
            skLineSegment(sketch, "E4527", {"start": v(143.43, -86.75) * mm, "end": v(143.5, -86.94) * mm});
            skLineSegment(sketch, "E4528", {"start": v(143.5, -86.94) * mm, "end": v(143.98, -87.46) * mm});
            skLineSegment(sketch, "E4529", {"start": v(143.98, -87.46) * mm, "end": v(144.67, -87.42) * mm});
            skLineSegment(sketch, "E4530", {"start": v(144.67, -87.42) * mm, "end": v(144.84, -87.33) * mm});
            skLineSegment(sketch, "E4531", {"start": v(144.84, -87.33) * mm, "end": v(145.16, -87.17) * mm});
            skLineSegment(sketch, "E4532", {"start": v(145.16, -87.17) * mm, "end": v(148.36, -85.55) * mm});
            skLineSegment(sketch, "E4533", {"start": v(148.36, -85.55) * mm, "end": v(148.67, -85.37) * mm});
            skLineSegment(sketch, "E4534", {"start": v(148.67, -85.37) * mm, "end": v(148.92, -85.22) * mm});
            skLineSegment(sketch, "E4535", {"start": v(148.92, -85.22) * mm, "end": v(149.65, -84.66) * mm});
            skLineSegment(sketch, "E4536", {"start": v(149.65, -84.66) * mm, "end": v(150.3, -83.79) * mm});
            skLineSegment(sketch, "E4537", {"start": v(150.3, -83.79) * mm, "end": v(150.53, -82.74) * mm});
            skLineSegment(sketch, "E4538", {"start": v(150.53, -82.74) * mm, "end": v(150.4, -81.78) * mm});
            skLineSegment(sketch, "E4539", {"start": v(150.4, -81.78) * mm, "end": v(150.28, -81.49) * mm});
            skLineSegment(sketch, "E4540", {"start": v(150.28, -81.49) * mm, "end": v(150.26, -81.4) * mm});
            skLineSegment(sketch, "E4541", {"start": v(150.26, -81.4) * mm, "end": v(150.14, -80.56) * mm});
            skLineSegment(sketch, "E4542", {"start": v(150.14, -80.56) * mm, "end": v(150.14, -80.48) * mm});
            skLineSegment(sketch, "E4543", {"start": v(150.14, -80.48) * mm, "end": v(150.13, -80.38) * mm});
            skLineSegment(sketch, "E4544", {"start": v(150.13, -80.38) * mm, "end": v(150.28, -80) * mm});
            skLineSegment(sketch, "E4545", {"start": v(150.28, -80) * mm, "end": v(150.62, -79.74) * mm});
            skLineSegment(sketch, "E4546", {"start": v(150.62, -79.74) * mm, "end": v(150.7, -79.7) * mm});
            skLineSegment(sketch, "E4547", {"start": v(150.7, -79.7) * mm, "end": v(150.8, -79.67) * mm});
            skLineSegment(sketch, "E4548", {"start": v(150.8, -79.67) * mm, "end": v(151.17, -79.74) * mm});
            skLineSegment(sketch, "E4549", {"start": v(151.17, -79.74) * mm, "end": v(151.45, -80.05) * mm});
            skLineSegment(sketch, "E4550", {"start": v(151.45, -80.05) * mm, "end": v(151.5, -80.13) * mm});
            skLineSegment(sketch, "E4551", {"start": v(151.5, -80.13) * mm, "end": v(151.54, -80.22) * mm});
            skLineSegment(sketch, "E4552", {"start": v(151.54, -80.22) * mm, "end": v(151.7, -80.7) * mm});
            skLineSegment(sketch, "E4553", {"start": v(151.7, -80.7) * mm, "end": v(151.96, -81.13) * mm});
            skLineSegment(sketch, "E4554", {"start": v(151.96, -81.13) * mm, "end": v(152.06, -81.2) * mm});
            skLineSegment(sketch, "E4555", {"start": v(152.06, -81.2) * mm, "end": v(152.26, -81.72) * mm});
            skLineSegment(sketch, "E4556", {"start": v(152.26, -81.72) * mm, "end": v(154.2, -86.97) * mm});
            skLineSegment(sketch, "E4557", {"start": v(154.2, -86.97) * mm, "end": v(154.4, -87.5) * mm});
            skLineSegment(sketch, "E4558", {"start": v(154.4, -87.5) * mm, "end": v(154.45, -87.61) * mm});
            skLineSegment(sketch, "E4559", {"start": v(154.45, -87.61) * mm, "end": v(154.6, -87.96) * mm});
            skLineSegment(sketch, "E4560", {"start": v(154.6, -87.96) * mm, "end": v(154.77, -88.42) * mm});
            skLineSegment(sketch, "E4561", {"start": v(154.77, -88.42) * mm, "end": v(154.82, -88.9) * mm});
            skLineSegment(sketch, "E4562", {"start": v(154.82, -88.9) * mm, "end": v(154.69, -89.3) * mm});
            skLineSegment(sketch, "E4563", {"start": v(154.69, -89.3) * mm, "end": v(154.61, -89.4) * mm});
            skLineSegment(sketch, "E4564", {"start": v(154.61, -89.4) * mm, "end": v(154.45, -89.44) * mm});
            skLineSegment(sketch, "E4565", {"start": v(154.45, -89.44) * mm, "end": v(153.72, -89.33) * mm});
            skLineSegment(sketch, "E4566", {"start": v(153.72, -89.33) * mm, "end": v(153.15, -88.85) * mm});
            skLineSegment(sketch, "E4567", {"start": v(153.15, -88.85) * mm, "end": v(153.06, -88.7) * mm});
            skLineSegment(sketch, "E4568", {"start": v(153.06, -88.7) * mm, "end": v(153, -88.58) * mm});
            skLineSegment(sketch, "E4569", {"start": v(153, -88.58) * mm, "end": v(152.26, -87.43) * mm});
            skLineSegment(sketch, "E4570", {"start": v(152.26, -87.43) * mm, "end": v(152.2, -87.31) * mm});
            skLineSegment(sketch, "E4571", {"start": v(152.2, -87.31) * mm, "end": v(152.07, -87.1) * mm});
            skLineSegment(sketch, "E4572", {"start": v(152.07, -87.1) * mm, "end": v(151.3, -86.49) * mm});
            skLineSegment(sketch, "E4573", {"start": v(151.3, -86.49) * mm, "end": v(150.34, -86.52) * mm});
            skLineSegment(sketch, "E4574", {"start": v(150.34, -86.52) * mm, "end": v(150.12, -86.62) * mm});
            skLineSegment(sketch, "E4575", {"start": v(150.12, -86.62) * mm, "end": v(149.72, -86.82) * mm});
            skLineSegment(sketch, "E4576", {"start": v(149.72, -86.82) * mm, "end": v(145.76, -88.83) * mm});
            skLineSegment(sketch, "E4577", {"start": v(145.76, -88.83) * mm, "end": v(145.37, -89.03) * mm});
            skLineSegment(sketch, "E4578", {"start": v(145.37, -89.03) * mm, "end": v(145.18, -89.12) * mm});
            skLineSegment(sketch, "E4579", {"start": v(145.18, -89.12) * mm, "end": v(144.67, -89.74) * mm});
            skLineSegment(sketch, "E4580", {"start": v(144.67, -89.74) * mm, "end": v(144.68, -90.55) * mm});
            skLineSegment(sketch, "E4581", {"start": v(144.68, -90.55) * mm, "end": v(144.75, -90.74) * mm});
            skLineSegment(sketch, "E4582", {"start": v(144.75, -90.74) * mm, "end": v(144.97, -91.33) * mm});
            skLineSegment(sketch, "E4583", {"start": v(144.97, -91.33) * mm, "end": v(147.22, -97.23) * mm});
            skLineSegment(sketch, "E4584", {"start": v(147.22, -97.23) * mm, "end": v(147.45, -97.82) * mm});
            skLineSegment(sketch, "E4585", {"start": v(147.45, -97.82) * mm, "end": v(147.53, -98) * mm});
            skLineSegment(sketch, "E4586", {"start": v(147.53, -98) * mm, "end": v(147.84, -98.55) * mm});
            skLineSegment(sketch, "E4587", {"start": v(147.84, -98.55) * mm, "end": v(148.31, -98.94) * mm});
            skLineSegment(sketch, "E4588", {"start": v(148.31, -98.94) * mm, "end": v(148.92, -99.02) * mm});
            skLineSegment(sketch, "E4589", {"start": v(148.92, -99.02) * mm, "end": v(149.52, -98.87) * mm});
            skLineSegment(sketch, "E4590", {"start": v(149.52, -98.87) * mm, "end": v(149.71, -98.79) * mm});
            skLineSegment(sketch, "E4591", {"start": v(149.71, -98.79) * mm, "end": v(150.3, -98.54) * mm});
            skLineSegment(sketch, "E4592", {"start": v(150.3, -98.54) * mm, "end": v(153.13, -97.17) * mm});
            skLineSegment(sketch, "E4593", {"start": v(153.13, -97.17) * mm, "end": v(155.77, -95.46) * mm});
            skLineSegment(sketch, "E4594", {"start": v(155.77, -95.46) * mm, "end": v(156.26, -95.05) * mm});
            skLineSegment(sketch, "E4595", {"start": v(88.72, -101.64) * mm, "end": v(88.57, -102.42) * mm});
            skLineSegment(sketch, "E4596", {"start": v(88.57, -102.42) * mm, "end": v(87.21, -109.64) * mm});
            skLineSegment(sketch, "E4597", {"start": v(87.21, -109.64) * mm, "end": v(87.1, -110.34) * mm});
            skLineSegment(sketch, "E4598", {"start": v(87.1, -110.34) * mm, "end": v(87.07, -110.45) * mm});
            skLineSegment(sketch, "E4599", {"start": v(87.07, -110.45) * mm, "end": v(87.1, -110.81) * mm});
            skLineSegment(sketch, "E4600", {"start": v(87.1, -110.81) * mm, "end": v(87.29, -111.1) * mm});
            skLineSegment(sketch, "E4601", {"start": v(87.29, -111.1) * mm, "end": v(87.63, -111.2) * mm});
            skLineSegment(sketch, "E4602", {"start": v(87.63, -111.2) * mm, "end": v(87.97, -111.18) * mm});
            skLineSegment(sketch, "E4603", {"start": v(87.97, -111.18) * mm, "end": v(88.08, -111.15) * mm});
            skLineSegment(sketch, "E4604", {"start": v(88.08, -111.15) * mm, "end": v(88.49, -111.05) * mm});
            skLineSegment(sketch, "E4605", {"start": v(88.49, -111.05) * mm, "end": v(92.61, -110.01) * mm});
            skLineSegment(sketch, "E4606", {"start": v(92.61, -110.01) * mm, "end": v(93.02, -109.9) * mm});
            skLineSegment(sketch, "E4607", {"start": v(93.02, -109.9) * mm, "end": v(93.17, -109.87) * mm});
            skLineSegment(sketch, "E4608", {"start": v(93.17, -109.87) * mm, "end": v(93.62, -109.54) * mm});
            skLineSegment(sketch, "E4609", {"start": v(93.62, -109.54) * mm, "end": v(93.62, -109) * mm});
            skLineSegment(sketch, "E4610", {"start": v(93.62, -109) * mm, "end": v(93.54, -108.86) * mm});
            skLineSegment(sketch, "E4611", {"start": v(93.54, -108.86) * mm, "end": v(93.19, -108.26) * mm});
            skLineSegment(sketch, "E4612", {"start": v(93.19, -108.26) * mm, "end": v(91.37, -105.26) * mm});
            skLineSegment(sketch, "E4613", {"start": v(91.37, -105.26) * mm, "end": v(89.23, -102.24) * mm});
            skLineSegment(sketch, "E4614", {"start": v(89.23, -102.24) * mm, "end": v(88.72, -101.64) * mm});
            skLineSegment(sketch, "E4615", {"start": v(77.93, -128.9) * mm, "end": v(77.8, -128.7) * mm});
            skLineSegment(sketch, "E4616", {"start": v(77.8, -128.7) * mm, "end": v(77.51, -128.05) * mm});
            skLineSegment(sketch, "E4617", {"start": v(77.51, -128.05) * mm, "end": v(77.47, -127.38) * mm});
            skLineSegment(sketch, "E4618", {"start": v(77.47, -127.38) * mm, "end": v(77.8, -126.85) * mm});
            skLineSegment(sketch, "E4619", {"start": v(77.8, -126.85) * mm, "end": v(78.31, -126.53) * mm});
            skLineSegment(sketch, "E4620", {"start": v(78.31, -126.53) * mm, "end": v(78.5, -126.46) * mm});
            skLineSegment(sketch, "E4621", {"start": v(78.5, -126.46) * mm, "end": v(78.9, -126.3) * mm});
            skLineSegment(sketch, "E4622", {"start": v(78.9, -126.3) * mm, "end": v(80.03, -125.6) * mm});
            skLineSegment(sketch, "E4623", {"start": v(80.03, -125.6) * mm, "end": v(81.13, -124.42) * mm});
            skLineSegment(sketch, "E4624", {"start": v(81.13, -124.42) * mm, "end": v(81.85, -122.96) * mm});
            skLineSegment(sketch, "E4625", {"start": v(81.85, -122.96) * mm, "end": v(82.21, -121.71) * mm});
            skLineSegment(sketch, "E4626", {"start": v(82.21, -121.71) * mm, "end": v(82.29, -121.29) * mm});
            skLineSegment(sketch, "E4627", {"start": v(82.29, -121.29) * mm, "end": v(82.58, -119.69) * mm});
            skLineSegment(sketch, "E4628", {"start": v(82.58, -119.69) * mm, "end": v(85.54, -103.7) * mm});
            skLineSegment(sketch, "E4629", {"start": v(85.54, -103.7) * mm, "end": v(85.84, -102.1) * mm});
            skLineSegment(sketch, "E4630", {"start": v(85.84, -102.1) * mm, "end": v(85.97, -101.41) * mm});
            skLineSegment(sketch, "E4631", {"start": v(85.97, -101.41) * mm, "end": v(87.27, -94.52) * mm});
            skLineSegment(sketch, "E4632", {"start": v(87.27, -94.52) * mm, "end": v(87.38, -93.82) * mm});
            skLineSegment(sketch, "E4633", {"start": v(87.38, -93.82) * mm, "end": v(87.41, -93.65) * mm});
            skLineSegment(sketch, "E4634", {"start": v(87.41, -93.65) * mm, "end": v(87.52, -93.15) * mm});
            skLineSegment(sketch, "E4635", {"start": v(87.52, -93.15) * mm, "end": v(87.76, -92.6) * mm});
            skLineSegment(sketch, "E4636", {"start": v(87.76, -92.6) * mm, "end": v(88.18, -92.2) * mm});
            skLineSegment(sketch, "E4637", {"start": v(88.18, -92.2) * mm, "end": v(88.69, -91.97) * mm});
            skLineSegment(sketch, "E4638", {"start": v(88.69, -91.97) * mm, "end": v(88.86, -91.94) * mm});
            skLineSegment(sketch, "E4639", {"start": v(88.86, -91.94) * mm, "end": v(89.05, -91.9) * mm});
            skLineSegment(sketch, "E4640", {"start": v(89.05, -91.9) * mm, "end": v(89.63, -91.9) * mm});
            skLineSegment(sketch, "E4641", {"start": v(89.63, -91.9) * mm, "end": v(90.24, -92.1) * mm});
            skLineSegment(sketch, "E4642", {"start": v(90.24, -92.1) * mm, "end": v(90.75, -92.52) * mm});
            skLineSegment(sketch, "E4643", {"start": v(90.75, -92.52) * mm, "end": v(91.1, -92.95) * mm});
            skLineSegment(sketch, "E4644", {"start": v(91.1, -92.95) * mm, "end": v(91.2, -93.1) * mm});
            skLineSegment(sketch, "E4645", {"start": v(91.2, -93.1) * mm, "end": v(91.75, -93.94) * mm});
            skLineSegment(sketch, "E4646", {"start": v(91.75, -93.94) * mm, "end": v(97.32, -102.17) * mm});
            skLineSegment(sketch, "E4647", {"start": v(97.32, -102.17) * mm, "end": v(97.87, -103) * mm});
            skLineSegment(sketch, "E4648", {"start": v(97.87, -103) * mm, "end": v(98.52, -104) * mm});
            skLineSegment(sketch, "E4649", {"start": v(98.52, -104) * mm, "end": v(101.86, -108.88) * mm});
            skLineSegment(sketch, "E4650", {"start": v(101.86, -108.88) * mm, "end": v(105.05, -113.85) * mm});
            skLineSegment(sketch, "E4651", {"start": v(105.05, -113.85) * mm, "end": v(105.63, -114.88) * mm});
            skLineSegment(sketch, "E4652", {"start": v(105.63, -114.88) * mm, "end": v(105.76, -115.1) * mm});
            skLineSegment(sketch, "E4653", {"start": v(105.76, -115.1) * mm, "end": v(106.21, -115.73) * mm});
            skLineSegment(sketch, "E4654", {"start": v(106.21, -115.73) * mm, "end": v(106.9, -116.33) * mm});
            skLineSegment(sketch, "E4655", {"start": v(106.9, -116.33) * mm, "end": v(107.74, -116.64) * mm});
            skLineSegment(sketch, "E4656", {"start": v(107.74, -116.64) * mm, "end": v(108.52, -116.67) * mm});
            skLineSegment(sketch, "E4657", {"start": v(108.52, -116.67) * mm, "end": v(108.77, -116.62) * mm});
            skLineSegment(sketch, "E4658", {"start": v(108.77, -116.62) * mm, "end": v(108.86, -116.6) * mm});
            skLineSegment(sketch, "E4659", {"start": v(108.86, -116.6) * mm, "end": v(109.71, -116.6) * mm});
            skLineSegment(sketch, "E4660", {"start": v(109.71, -116.6) * mm, "end": v(109.8, -116.6) * mm});
            skLineSegment(sketch, "E4661", {"start": v(109.8, -116.6) * mm, "end": v(109.97, -116.6) * mm});
            skLineSegment(sketch, "E4662", {"start": v(109.97, -116.6) * mm, "end": v(110.55, -116.9) * mm});
            skLineSegment(sketch, "E4663", {"start": v(110.55, -116.9) * mm, "end": v(110.84, -117.49) * mm});
            skLineSegment(sketch, "E4664", {"start": v(110.84, -117.49) * mm, "end": v(110.86, -117.64) * mm});
            skLineSegment(sketch, "E4665", {"start": v(110.86, -117.64) * mm, "end": v(110.87, -117.73) * mm});
            skLineSegment(sketch, "E4666", {"start": v(110.87, -117.73) * mm, "end": v(110.82, -118.03) * mm});
            skLineSegment(sketch, "E4667", {"start": v(110.82, -118.03) * mm, "end": v(110.63, -118.3) * mm});
            skLineSegment(sketch, "E4668", {"start": v(110.63, -118.3) * mm, "end": v(110.32, -118.47) * mm});
            skLineSegment(sketch, "E4669", {"start": v(110.32, -118.47) * mm, "end": v(110.06, -118.55) * mm});
            skLineSegment(sketch, "E4670", {"start": v(110.06, -118.55) * mm, "end": v(109.97, -118.56) * mm});
            skLineSegment(sketch, "E4671", {"start": v(109.97, -118.56) * mm, "end": v(108.87, -118.78) * mm});
            skLineSegment(sketch, "E4672", {"start": v(108.87, -118.78) * mm, "end": v(103.53, -120.34) * mm});
            skLineSegment(sketch, "E4673", {"start": v(103.53, -120.34) * mm, "end": v(98.29, -122.2) * mm});
            skLineSegment(sketch, "E4674", {"start": v(98.29, -122.2) * mm, "end": v(97.24, -122.57) * mm});
            skLineSegment(sketch, "E4675", {"start": v(97.24, -122.57) * mm, "end": v(97.15, -122.6) * mm});
            skLineSegment(sketch, "E4676", {"start": v(97.15, -122.6) * mm, "end": v(96.89, -122.7) * mm});
            skLineSegment(sketch, "E4677", {"start": v(96.89, -122.7) * mm, "end": v(96.54, -122.77) * mm});
            skLineSegment(sketch, "E4678", {"start": v(96.54, -122.77) * mm, "end": v(96.22, -122.7) * mm});
            skLineSegment(sketch, "E4679", {"start": v(96.22, -122.7) * mm, "end": v(96, -122.51) * mm});
            skLineSegment(sketch, "E4680", {"start": v(96, -122.51) * mm, "end": v(95.96, -122.43) * mm});
            skLineSegment(sketch, "E4681", {"start": v(95.96, -122.43) * mm, "end": v(95.86, -122.26) * mm});
            skLineSegment(sketch, "E4682", {"start": v(95.86, -122.26) * mm, "end": v(95.87, -121.55) * mm});
            skLineSegment(sketch, "E4683", {"start": v(95.87, -121.55) * mm, "end": v(96.37, -121) * mm});
            skLineSegment(sketch, "E4684", {"start": v(96.37, -121) * mm, "end": v(96.53, -120.9) * mm});
            skLineSegment(sketch, "E4685", {"start": v(96.53, -120.9) * mm, "end": v(96.7, -120.81) * mm});
            skLineSegment(sketch, "E4686", {"start": v(96.7, -120.81) * mm, "end": v(98.3, -119.82) * mm});
            skLineSegment(sketch, "E4687", {"start": v(98.3, -119.82) * mm, "end": v(98.46, -119.72) * mm});
            skLineSegment(sketch, "E4688", {"start": v(98.46, -119.72) * mm, "end": v(98.64, -119.6) * mm});
            skLineSegment(sketch, "E4689", {"start": v(98.64, -119.6) * mm, "end": v(99.15, -119.18) * mm});
            skLineSegment(sketch, "E4690", {"start": v(99.15, -119.18) * mm, "end": v(99.47, -118.67) * mm});
            skLineSegment(sketch, "E4691", {"start": v(99.47, -118.67) * mm, "end": v(99.44, -118.1) * mm});
            skLineSegment(sketch, "E4692", {"start": v(99.44, -118.1) * mm, "end": v(99.19, -117.53) * mm});
            skLineSegment(sketch, "E4693", {"start": v(99.19, -117.53) * mm, "end": v(99.08, -117.36) * mm});
            skLineSegment(sketch, "E4694", {"start": v(99.08, -117.36) * mm, "end": v(98.84, -116.97) * mm});
            skLineSegment(sketch, "E4695", {"start": v(98.84, -116.97) * mm, "end": v(96.28, -113.1) * mm});
            skLineSegment(sketch, "E4696", {"start": v(96.28, -113.1) * mm, "end": v(96.03, -112.72) * mm});
            skLineSegment(sketch, "E4697", {"start": v(96.03, -112.72) * mm, "end": v(95.92, -112.54) * mm});
            skLineSegment(sketch, "E4698", {"start": v(95.92, -112.54) * mm, "end": v(95.25, -112.06) * mm});
            skLineSegment(sketch, "E4699", {"start": v(95.25, -112.06) * mm, "end": v(94.45, -112.03) * mm});
            skLineSegment(sketch, "E4700", {"start": v(94.45, -112.03) * mm, "end": v(94.26, -112.09) * mm});
            skLineSegment(sketch, "E4701", {"start": v(94.26, -112.09) * mm, "end": v(93.69, -112.25) * mm});
            skLineSegment(sketch, "E4702", {"start": v(93.69, -112.25) * mm, "end": v(87.92, -113.88) * mm});
            skLineSegment(sketch, "E4703", {"start": v(87.92, -113.88) * mm, "end": v(87.34, -114.03) * mm});
            skLineSegment(sketch, "E4704", {"start": v(87.34, -114.03) * mm, "end": v(87.17, -114.08) * mm});
            skLineSegment(sketch, "E4705", {"start": v(87.17, -114.08) * mm, "end": v(86.53, -114.44) * mm});
            skLineSegment(sketch, "E4706", {"start": v(86.53, -114.44) * mm, "end": v(86.17, -115.07) * mm});
            skLineSegment(sketch, "E4707", {"start": v(86.17, -115.07) * mm, "end": v(86.14, -115.24) * mm});
            skLineSegment(sketch, "E4708", {"start": v(86.14, -115.24) * mm, "end": v(86.05, -115.82) * mm});
            skLineSegment(sketch, "E4709", {"start": v(86.05, -115.82) * mm, "end": v(85.14, -121.56) * mm});
            skLineSegment(sketch, "E4710", {"start": v(85.14, -121.56) * mm, "end": v(85.07, -122.13) * mm});
            skLineSegment(sketch, "E4711", {"start": v(85.07, -122.13) * mm, "end": v(85.05, -122.3) * mm});
            skLineSegment(sketch, "E4712", {"start": v(85.05, -122.3) * mm, "end": v(85.09, -122.82) * mm});
            skLineSegment(sketch, "E4713", {"start": v(85.09, -122.82) * mm, "end": v(85.34, -123.26) * mm});
            skLineSegment(sketch, "E4714", {"start": v(85.34, -123.26) * mm, "end": v(85.84, -123.49) * mm});
            skLineSegment(sketch, "E4715", {"start": v(85.84, -123.49) * mm, "end": v(86.4, -123.54) * mm});
            skLineSegment(sketch, "E4716", {"start": v(86.4, -123.54) * mm, "end": v(86.58, -123.53) * mm});
            skLineSegment(sketch, "E4717", {"start": v(86.58, -123.53) * mm, "end": v(86.73, -123.52) * mm});
            skLineSegment(sketch, "E4718", {"start": v(86.73, -123.52) * mm, "end": v(88.24, -123.26) * mm});
            skLineSegment(sketch, "E4719", {"start": v(88.24, -123.26) * mm, "end": v(88.4, -123.24) * mm});
            skLineSegment(sketch, "E4720", {"start": v(88.4, -123.24) * mm, "end": v(88.52, -123.22) * mm});
            skLineSegment(sketch, "E4721", {"start": v(88.52, -123.22) * mm, "end": v(88.88, -123.21) * mm});
            skLineSegment(sketch, "E4722", {"start": v(88.88, -123.21) * mm, "end": v(89.3, -123.32) * mm});
            skLineSegment(sketch, "E4723", {"start": v(89.3, -123.32) * mm, "end": v(89.61, -123.58) * mm});
            skLineSegment(sketch, "E4724", {"start": v(89.61, -123.58) * mm, "end": v(89.8, -123.93) * mm});
            skLineSegment(sketch, "E4725", {"start": v(89.8, -123.93) * mm, "end": v(89.82, -124.05) * mm});
            skLineSegment(sketch, "E4726", {"start": v(89.82, -124.05) * mm, "end": v(89.85, -124.17) * mm});
            skLineSegment(sketch, "E4727", {"start": v(89.85, -124.17) * mm, "end": v(89.86, -124.57) * mm});
            skLineSegment(sketch, "E4728", {"start": v(89.86, -124.57) * mm, "end": v(89.68, -124.92) * mm});
            skLineSegment(sketch, "E4729", {"start": v(89.68, -124.92) * mm, "end": v(89.33, -125.14) * mm});
            skLineSegment(sketch, "E4730", {"start": v(89.33, -125.14) * mm, "end": v(88.97, -125.25) * mm});
            skLineSegment(sketch, "E4731", {"start": v(88.97, -125.25) * mm, "end": v(88.86, -125.27) * mm});
            skLineSegment(sketch, "E4732", {"start": v(88.86, -125.27) * mm, "end": v(88.67, -125.3) * mm});
            skLineSegment(sketch, "E4733", {"start": v(88.67, -125.3) * mm, "end": v(86.84, -125.77) * mm});
            skLineSegment(sketch, "E4734", {"start": v(86.84, -125.77) * mm, "end": v(86.66, -125.8) * mm});
            skLineSegment(sketch, "E4735", {"start": v(86.66, -125.8) * mm, "end": v(85.9, -125.95) * mm});
            skLineSegment(sketch, "E4736", {"start": v(85.9, -125.95) * mm, "end": v(82.23, -127.1) * mm});
            skLineSegment(sketch, "E4737", {"start": v(82.23, -127.1) * mm, "end": v(78.64, -128.6) * mm});
            skLineSegment(sketch, "E4738", {"start": v(78.64, -128.6) * mm, "end": v(77.93, -128.9) * mm});
            skLineSegment(sketch, "E4739", {"start": v(183.12, -79.65) * mm, "end": v(182.43, -80.33) * mm});
            skLineSegment(sketch, "E4740", {"start": v(182.43, -80.33) * mm, "end": v(178.72, -83.48) * mm});
            skLineSegment(sketch, "E4741", {"start": v(178.72, -83.48) * mm, "end": v(174.87, -86.6) * mm});
            skLineSegment(sketch, "E4742", {"start": v(174.87, -86.6) * mm, "end": v(174.1, -87.26) * mm});
            skLineSegment(sketch, "E4743", {"start": v(174.1, -87.26) * mm, "end": v(174.06, -87.11) * mm});
            skLineSegment(sketch, "E4744", {"start": v(174.06, -87.11) * mm, "end": v(174.02, -86.65) * mm});
            skLineSegment(sketch, "E4745", {"start": v(174.02, -86.65) * mm, "end": v(174.16, -86.23) * mm});
            skLineSegment(sketch, "E4746", {"start": v(174.16, -86.23) * mm, "end": v(174.43, -85.93) * mm});
            skLineSegment(sketch, "E4747", {"start": v(174.43, -85.93) * mm, "end": v(174.64, -85.73) * mm});
            skLineSegment(sketch, "E4748", {"start": v(174.64, -85.73) * mm, "end": v(174.7, -85.67) * mm});
            skLineSegment(sketch, "E4749", {"start": v(174.7, -85.67) * mm, "end": v(174.89, -85.47) * mm});
            skLineSegment(sketch, "E4750", {"start": v(174.89, -85.47) * mm, "end": v(175.34, -84.8) * mm});
            skLineSegment(sketch, "E4751", {"start": v(175.34, -84.8) * mm, "end": v(175.64, -83.9) * mm});
            skLineSegment(sketch, "E4752", {"start": v(175.64, -83.9) * mm, "end": v(175.63, -82.93) * mm});
            skLineSegment(sketch, "E4753", {"start": v(175.63, -82.93) * mm, "end": v(175.41, -82.14) * mm});
            skLineSegment(sketch, "E4754", {"start": v(175.41, -82.14) * mm, "end": v(175.3, -81.9) * mm});
            skLineSegment(sketch, "E4755", {"start": v(175.3, -81.9) * mm, "end": v(174.7, -80.54) * mm});
            skLineSegment(sketch, "E4756", {"start": v(174.7, -80.54) * mm, "end": v(168.73, -66.91) * mm});
            skLineSegment(sketch, "E4757", {"start": v(168.73, -66.91) * mm, "end": v(168.13, -65.55) * mm});
            skLineSegment(sketch, "E4758", {"start": v(168.13, -65.55) * mm, "end": v(168.1, -65.49) * mm});
            skLineSegment(sketch, "E4759", {"start": v(168.1, -65.49) * mm, "end": v(167.79, -64.88) * mm});
            skLineSegment(sketch, "E4760", {"start": v(167.79, -64.88) * mm, "end": v(167.76, -64.82) * mm});
            skLineSegment(sketch, "E4761", {"start": v(167.76, -64.82) * mm, "end": v(167.63, -64.6) * mm});
            skLineSegment(sketch, "E4762", {"start": v(167.63, -64.6) * mm, "end": v(167.17, -63.98) * mm});
            skLineSegment(sketch, "E4763", {"start": v(167.17, -63.98) * mm, "end": v(166.59, -63.57) * mm});
            skLineSegment(sketch, "E4764", {"start": v(166.59, -63.57) * mm, "end": v(165.88, -63.56) * mm});
            skLineSegment(sketch, "E4765", {"start": v(165.88, -63.56) * mm, "end": v(165.16, -63.8) * mm});
            skLineSegment(sketch, "E4766", {"start": v(165.16, -63.8) * mm, "end": v(164.94, -63.9) * mm});
            skLineSegment(sketch, "E4767", {"start": v(164.94, -63.9) * mm, "end": v(164.86, -63.94) * mm});
            skLineSegment(sketch, "E4768", {"start": v(164.86, -63.94) * mm, "end": v(164.5, -64.15) * mm});
            skLineSegment(sketch, "E4769", {"start": v(164.5, -64.15) * mm, "end": v(164.1, -64.23) * mm});
            skLineSegment(sketch, "E4770", {"start": v(164.1, -64.23) * mm, "end": v(164, -64.2) * mm});
            skLineSegment(sketch, "E4771", {"start": v(164, -64.2) * mm, "end": v(164, -64.2) * mm});
            skLineSegment(sketch, "E4772", {"start": v(164, -64.2) * mm, "end": v(163.78, -64.03) * mm});
            skLineSegment(sketch, "E4773", {"start": v(163.78, -64.03) * mm, "end": v(163.74, -64) * mm});
            skLineSegment(sketch, "E4774", {"start": v(163.74, -64) * mm, "end": v(163.82, -63.83) * mm});
            skLineSegment(sketch, "E4775", {"start": v(163.82, -63.83) * mm, "end": v(164.19, -63.37) * mm});
            skLineSegment(sketch, "E4776", {"start": v(164.19, -63.37) * mm, "end": v(164.77, -62.9) * mm});
            skLineSegment(sketch, "E4777", {"start": v(164.77, -62.9) * mm, "end": v(165.41, -62.55) * mm});
            skLineSegment(sketch, "E4778", {"start": v(165.41, -62.55) * mm, "end": v(165.9, -62.34) * mm});
            skLineSegment(sketch, "E4779", {"start": v(165.9, -62.34) * mm, "end": v(166.06, -62.27) * mm});
            skLineSegment(sketch, "E4780", {"start": v(166.06, -62.27) * mm, "end": v(166.74, -61.97) * mm});
            skLineSegment(sketch, "E4781", {"start": v(166.74, -61.97) * mm, "end": v(169.98, -60.08) * mm});
            skLineSegment(sketch, "E4782", {"start": v(169.98, -60.08) * mm, "end": v(173.3, -58.34) * mm});
            skLineSegment(sketch, "E4783", {"start": v(173.3, -58.34) * mm, "end": v(174.01, -58.1) * mm});
            skLineSegment(sketch, "E4784", {"start": v(174.01, -58.1) * mm, "end": v(173.84, -58.3) * mm});
            skLineSegment(sketch, "E4785", {"start": v(173.84, -58.3) * mm, "end": v(173.35, -58.88) * mm});
            skLineSegment(sketch, "E4786", {"start": v(173.35, -58.88) * mm, "end": v(172.87, -59.49) * mm});
            skLineSegment(sketch, "E4787", {"start": v(172.87, -59.49) * mm, "end": v(172.56, -60) * mm});
            skLineSegment(sketch, "E4788", {"start": v(172.56, -60) * mm, "end": v(172.41, -60.5) * mm});
            skLineSegment(sketch, "E4789", {"start": v(172.41, -60.5) * mm, "end": v(172.42, -61) * mm});
            skLineSegment(sketch, "E4790", {"start": v(172.42, -61) * mm, "end": v(172.58, -61.6) * mm});
            skLineSegment(sketch, "E4791", {"start": v(172.58, -61.6) * mm, "end": v(172.87, -62.36) * mm});
            skLineSegment(sketch, "E4792", {"start": v(172.87, -62.36) * mm, "end": v(173.2, -63.08) * mm});
            skLineSegment(sketch, "E4793", {"start": v(173.2, -63.08) * mm, "end": v(173.3, -63.32) * mm});
            skLineSegment(sketch, "E4794", {"start": v(173.3, -63.32) * mm, "end": v(173.8, -64.43) * mm});
            skLineSegment(sketch, "E4795", {"start": v(173.8, -64.43) * mm, "end": v(178.8, -75.5) * mm});
            skLineSegment(sketch, "E4796", {"start": v(178.8, -75.5) * mm, "end": v(179.3, -76.6) * mm});
            skLineSegment(sketch, "E4797", {"start": v(179.3, -76.6) * mm, "end": v(179.37, -76.76) * mm});
            skLineSegment(sketch, "E4798", {"start": v(179.37, -76.76) * mm, "end": v(180.12, -78.3) * mm});
            skLineSegment(sketch, "E4799", {"start": v(180.12, -78.3) * mm, "end": v(180.2, -78.44) * mm});
            skLineSegment(sketch, "E4800", {"start": v(180.2, -78.44) * mm, "end": v(180.32, -78.67) * mm});
            skLineSegment(sketch, "E4801", {"start": v(180.32, -78.67) * mm, "end": v(180.72, -79.32) * mm});
            skLineSegment(sketch, "E4802", {"start": v(180.72, -79.32) * mm, "end": v(181.2, -79.73) * mm});
            skLineSegment(sketch, "E4803", {"start": v(181.2, -79.73) * mm, "end": v(181.87, -79.74) * mm});
            skLineSegment(sketch, "E4804", {"start": v(181.87, -79.74) * mm, "end": v(182.69, -79.54) * mm});
            skLineSegment(sketch, "E4805", {"start": v(182.69, -79.54) * mm, "end": v(182.96, -79.46) * mm});
            skLineSegment(sketch, "E4806", {"start": v(182.96, -79.46) * mm, "end": v(182.97, -79.47) * mm});
            skLineSegment(sketch, "E4807", {"start": v(182.97, -79.47) * mm, "end": v(183.1, -79.64) * mm});
            skLineSegment(sketch, "E4808", {"start": v(183.1, -79.64) * mm, "end": v(183.12, -79.65) * mm});
            skLineSegment(sketch, "E4809", {"start": v(189.76, -49) * mm, "end": v(190, -49.38) * mm});
            skLineSegment(sketch, "E4810", {"start": v(190, -49.38) * mm, "end": v(191, -51.34) * mm});
            skLineSegment(sketch, "E4811", {"start": v(191, -51.34) * mm, "end": v(191.74, -53.39) * mm});
            skLineSegment(sketch, "E4812", {"start": v(191.74, -53.39) * mm, "end": v(191.85, -53.82) * mm});
            skLineSegment(sketch, "E4813", {"start": v(191.85, -53.82) * mm, "end": v(191.75, -53.73) * mm});
            skLineSegment(sketch, "E4814", {"start": v(191.75, -53.73) * mm, "end": v(190.72, -52.8) * mm});
            skLineSegment(sketch, "E4815", {"start": v(190.72, -52.8) * mm, "end": v(190.62, -52.7) * mm});
            skLineSegment(sketch, "E4816", {"start": v(190.62, -52.7) * mm, "end": v(190.5, -52.58) * mm});
            skLineSegment(sketch, "E4817", {"start": v(190.5, -52.58) * mm, "end": v(189.82, -52.06) * mm});
            skLineSegment(sketch, "E4818", {"start": v(189.82, -52.06) * mm, "end": v(189.05, -51.7) * mm});
            skLineSegment(sketch, "E4819", {"start": v(189.05, -51.7) * mm, "end": v(188.89, -51.65) * mm});
            skLineSegment(sketch, "E4820", {"start": v(188.89, -51.65) * mm, "end": v(188.72, -51.6) * mm});
            skLineSegment(sketch, "E4821", {"start": v(188.72, -51.6) * mm, "end": v(188.18, -51.6) * mm});
            skLineSegment(sketch, "E4822", {"start": v(188.18, -51.6) * mm, "end": v(187.37, -51.77) * mm});
            skLineSegment(sketch, "E4823", {"start": v(187.37, -51.77) * mm, "end": v(186.62, -52.11) * mm});
            skLineSegment(sketch, "E4824", {"start": v(186.62, -52.11) * mm, "end": v(186.19, -52.42) * mm});
            skLineSegment(sketch, "E4825", {"start": v(186.19, -52.42) * mm, "end": v(186.09, -52.55) * mm});
            skLineSegment(sketch, "E4826", {"start": v(186.09, -52.55) * mm, "end": v(186, -52.66) * mm});
            skLineSegment(sketch, "E4827", {"start": v(186, -52.66) * mm, "end": v(185.87, -53.08) * mm});
            skLineSegment(sketch, "E4828", {"start": v(185.87, -53.08) * mm, "end": v(185.97, -53.55) * mm});
            skLineSegment(sketch, "E4829", {"start": v(185.97, -53.55) * mm, "end": v(186.22, -54) * mm});
            skLineSegment(sketch, "E4830", {"start": v(186.22, -54) * mm, "end": v(186.41, -54.3) * mm});
            skLineSegment(sketch, "E4831", {"start": v(186.41, -54.3) * mm, "end": v(186.47, -54.41) * mm});
            skLineSegment(sketch, "E4832", {"start": v(186.47, -54.41) * mm, "end": v(186.99, -55.51) * mm});
            skLineSegment(sketch, "E4833", {"start": v(186.99, -55.51) * mm, "end": v(192.3, -66.46) * mm});
            skLineSegment(sketch, "E4834", {"start": v(192.3, -66.46) * mm, "end": v(192.82, -67.56) * mm});
            skLineSegment(sketch, "E4835", {"start": v(192.82, -67.56) * mm, "end": v(192.9, -67.73) * mm});
            skLineSegment(sketch, "E4836", {"start": v(192.9, -67.73) * mm, "end": v(193.16, -68.27) * mm});
            skLineSegment(sketch, "E4837", {"start": v(193.16, -68.27) * mm, "end": v(193.46, -68.8) * mm});
            skLineSegment(sketch, "E4838", {"start": v(193.46, -68.8) * mm, "end": v(193.74, -69.17) * mm});
            skLineSegment(sketch, "E4839", {"start": v(193.74, -69.17) * mm, "end": v(194.05, -69.4) * mm});
            skLineSegment(sketch, "E4840", {"start": v(194.05, -69.4) * mm, "end": v(194.44, -69.49) * mm});
            skLineSegment(sketch, "E4841", {"start": v(194.44, -69.49) * mm, "end": v(194.95, -69.49) * mm});
            skLineSegment(sketch, "E4842", {"start": v(194.95, -69.49) * mm, "end": v(195.64, -69.4) * mm});
            skLineSegment(sketch, "E4843", {"start": v(195.64, -69.4) * mm, "end": v(196.3, -69.28) * mm});
            skLineSegment(sketch, "E4844", {"start": v(196.3, -69.28) * mm, "end": v(196.53, -69.24) * mm});
            skLineSegment(sketch, "E4845", {"start": v(196.53, -69.24) * mm, "end": v(195.83, -69.8) * mm});
            skLineSegment(sketch, "E4846", {"start": v(195.83, -69.8) * mm, "end": v(192.54, -72.45) * mm});
            skLineSegment(sketch, "E4847", {"start": v(192.54, -72.45) * mm, "end": v(189.41, -74.96) * mm});
            skLineSegment(sketch, "E4848", {"start": v(189.41, -74.96) * mm, "end": v(188.8, -75.46) * mm});
            skLineSegment(sketch, "E4849", {"start": v(188.8, -75.46) * mm, "end": v(188.7, -75.37) * mm});
            skLineSegment(sketch, "E4850", {"start": v(188.7, -75.37) * mm, "end": v(188.52, -74.98) * mm});
            skLineSegment(sketch, "E4851", {"start": v(188.52, -74.98) * mm, "end": v(188.65, -74.68) * mm});
            skLineSegment(sketch, "E4852", {"start": v(188.65, -74.68) * mm, "end": v(188.7, -74.64) * mm});
            skLineSegment(sketch, "E4853", {"start": v(188.7, -74.64) * mm, "end": v(188.92, -74.45) * mm});
            skLineSegment(sketch, "E4854", {"start": v(188.92, -74.45) * mm, "end": v(189.43, -73.75) * mm});
            skLineSegment(sketch, "E4855", {"start": v(189.43, -73.75) * mm, "end": v(189.73, -72.81) * mm});
            skLineSegment(sketch, "E4856", {"start": v(189.73, -72.81) * mm, "end": v(189.65, -71.8) * mm});
            skLineSegment(sketch, "E4857", {"start": v(189.65, -71.8) * mm, "end": v(189.38, -71) * mm});
            skLineSegment(sketch, "E4858", {"start": v(189.38, -71) * mm, "end": v(189.25, -70.74) * mm});
            skLineSegment(sketch, "E4859", {"start": v(189.25, -70.74) * mm, "end": v(188.67, -69.54) * mm});
            skLineSegment(sketch, "E4860", {"start": v(188.67, -69.54) * mm, "end": v(182.94, -57.46) * mm});
            skLineSegment(sketch, "E4861", {"start": v(182.94, -57.46) * mm, "end": v(182.37, -56.26) * mm});
            skLineSegment(sketch, "E4862", {"start": v(182.37, -56.26) * mm, "end": v(182.28, -56.07) * mm});
            skLineSegment(sketch, "E4863", {"start": v(182.28, -56.07) * mm, "end": v(181.98, -55.52) * mm});
            skLineSegment(sketch, "E4864", {"start": v(181.98, -55.52) * mm, "end": v(181.63, -55.23) * mm});
            skLineSegment(sketch, "E4865", {"start": v(181.63, -55.23) * mm, "end": v(181.15, -55.3) * mm});
            skLineSegment(sketch, "E4866", {"start": v(181.15, -55.3) * mm, "end": v(180.58, -55.6) * mm});
            skLineSegment(sketch, "E4867", {"start": v(180.58, -55.6) * mm, "end": v(180.4, -55.7) * mm});
            skLineSegment(sketch, "E4868", {"start": v(180.4, -55.7) * mm, "end": v(180.1, -55.86) * mm});
            skLineSegment(sketch, "E4869", {"start": v(180.1, -55.86) * mm, "end": v(179.32, -56.55) * mm});
            skLineSegment(sketch, "E4870", {"start": v(179.32, -56.55) * mm, "end": v(178.7, -57.59) * mm});
            skLineSegment(sketch, "E4871", {"start": v(178.7, -57.59) * mm, "end": v(178.43, -58.78) * mm});
            skLineSegment(sketch, "E4872", {"start": v(178.43, -58.78) * mm, "end": v(178.4, -59.77) * mm});
            skLineSegment(sketch, "E4873", {"start": v(178.4, -59.77) * mm, "end": v(178.42, -60.1) * mm});
            skLineSegment(sketch, "E4874", {"start": v(178.42, -60.1) * mm, "end": v(178.43, -60.29) * mm});
            skLineSegment(sketch, "E4875", {"start": v(178.43, -60.29) * mm, "end": v(178.5, -61.25) * mm});
            skLineSegment(sketch, "E4876", {"start": v(178.5, -61.25) * mm, "end": v(178.5, -62.23) * mm});
            skLineSegment(sketch, "E4877", {"start": v(178.5, -62.23) * mm, "end": v(178.47, -62.43) * mm});
            skLineSegment(sketch, "E4878", {"start": v(178.47, -62.43) * mm, "end": v(178.17, -62.06) * mm});
            skLineSegment(sketch, "E4879", {"start": v(178.17, -62.06) * mm, "end": v(177.03, -60.07) * mm});
            skLineSegment(sketch, "E4880", {"start": v(177.03, -60.07) * mm, "end": v(176.08, -58.02) * mm});
            skLineSegment(sketch, "E4881", {"start": v(176.08, -58.02) * mm, "end": v(175.9, -57.61) * mm});
            skLineSegment(sketch, "E4882", {"start": v(175.9, -57.61) * mm, "end": v(175.84, -57.5) * mm});
            skLineSegment(sketch, "E4883", {"start": v(175.84, -57.5) * mm, "end": v(175.8, -57.14) * mm});
            skLineSegment(sketch, "E4884", {"start": v(175.8, -57.14) * mm, "end": v(175.97, -56.83) * mm});
            skLineSegment(sketch, "E4885", {"start": v(175.97, -56.83) * mm, "end": v(176.3, -56.61) * mm});
            skLineSegment(sketch, "E4886", {"start": v(176.3, -56.61) * mm, "end": v(176.57, -56.48) * mm});
            skLineSegment(sketch, "E4887", {"start": v(176.57, -56.48) * mm, "end": v(176.66, -56.43) * mm});
            skLineSegment(sketch, "E4888", {"start": v(176.66, -56.43) * mm, "end": v(177.22, -56.1) * mm});
            skLineSegment(sketch, "E4889", {"start": v(177.22, -56.1) * mm, "end": v(182.88, -52.89) * mm});
            skLineSegment(sketch, "E4890", {"start": v(182.88, -52.89) * mm, "end": v(183.45, -52.57) * mm});
            skLineSegment(sketch, "E4891", {"start": v(183.45, -52.57) * mm, "end": v(183.97, -52.27) * mm});
            skLineSegment(sketch, "E4892", {"start": v(183.97, -52.27) * mm, "end": v(189.22, -49.3) * mm});
            skLineSegment(sketch, "E4893", {"start": v(189.22, -49.3) * mm, "end": v(189.76, -49) * mm});
            skLineSegment(sketch, "E4894", {"start": v(182.96, -79.46) * mm, "end": v(182.97, -79.38) * mm});
            skLineSegment(sketch, "E4895", {"start": v(182.97, -79.38) * mm, "end": v(183.14, -79.13) * mm});
            skLineSegment(sketch, "E4896", {"start": v(183.14, -79.13) * mm, "end": v(183.43, -79) * mm});
            skLineSegment(sketch, "E4897", {"start": v(183.43, -79) * mm, "end": v(183.5, -78.98) * mm});
            skLineSegment(sketch, "E4898", {"start": v(183.5, -78.98) * mm, "end": v(183.5, -78.98) * mm});
            skLineSegment(sketch, "E4899", {"start": v(183.5, -78.98) * mm, "end": v(183.6, -79.07) * mm});
            skLineSegment(sketch, "E4900", {"start": v(183.6, -79.07) * mm, "end": v(183.68, -79.19) * mm});
            skLineSegment(sketch, "E4901", {"start": v(183.68, -79.19) * mm, "end": v(183.67, -79.2) * mm});
            skLineSegment(sketch, "E4902", {"start": v(183.67, -79.2) * mm, "end": v(183.66, -79.28) * mm});
            skLineSegment(sketch, "E4903", {"start": v(183.66, -79.28) * mm, "end": v(183.48, -79.52) * mm});
            skLineSegment(sketch, "E4904", {"start": v(183.48, -79.52) * mm, "end": v(183.19, -79.64) * mm});
            skLineSegment(sketch, "E4905", {"start": v(183.19, -79.64) * mm, "end": v(183.12, -79.65) * mm});
            skLineSegment(sketch, "E4906", {"start": v(183.12, -79.65) * mm, "end": v(183.1, -79.64) * mm});
            skLineSegment(sketch, "E4907", {"start": v(183.1, -79.64) * mm, "end": v(182.97, -79.47) * mm});
            skLineSegment(sketch, "E4908", {"start": v(182.97, -79.47) * mm, "end": v(182.96, -79.46) * mm});
            skLineSegment(sketch, "E4909", {"start": v(79.25, 4.8) * mm, "end": v(78.8, 4.92) * mm});
            skLineSegment(sketch, "E4910", {"start": v(78.8, 4.92) * mm, "end": v(74.3, 5.8) * mm});
            skLineSegment(sketch, "E4911", {"start": v(74.3, 5.8) * mm, "end": v(73.84, 5.86) * mm});
            skLineSegment(sketch, "E4912", {"start": v(73.84, 5.86) * mm, "end": v(73.49, 5.92) * mm});
            skLineSegment(sketch, "E4913", {"start": v(73.49, 5.92) * mm, "end": v(71.7, 6.35) * mm});
            skLineSegment(sketch, "E4914", {"start": v(71.7, 6.35) * mm, "end": v(69.9, 6.9) * mm});
            skLineSegment(sketch, "E4915", {"start": v(69.9, 6.9) * mm, "end": v(69.55, 7) * mm});
            skLineSegment(sketch, "E4916", {"start": v(69.55, 7) * mm, "end": v(69.5, 7.02) * mm});
            skLineSegment(sketch, "E4917", {"start": v(69.5, 7.02) * mm, "end": v(69.32, 7.17) * mm});
            skLineSegment(sketch, "E4918", {"start": v(69.32, 7.17) * mm, "end": v(69.27, 7.42) * mm});
            skLineSegment(sketch, "E4919", {"start": v(69.27, 7.42) * mm, "end": v(69.3, 7.48) * mm});
            skLineSegment(sketch, "E4920", {"start": v(69.3, 7.48) * mm, "end": v(69.3, 7.53) * mm});
            skLineSegment(sketch, "E4921", {"start": v(69.3, 7.53) * mm, "end": v(69.44, 7.73) * mm});
            skLineSegment(sketch, "E4922", {"start": v(69.44, 7.73) * mm, "end": v(69.67, 7.8) * mm});
            skLineSegment(sketch, "E4923", {"start": v(69.67, 7.8) * mm, "end": v(69.73, 7.8) * mm});
            skLineSegment(sketch, "E4924", {"start": v(69.73, 7.8) * mm, "end": v(69.74, 7.8) * mm});
            skLineSegment(sketch, "E4925", {"start": v(69.74, 7.8) * mm, "end": v(69.92, 7.8) * mm});
            skLineSegment(sketch, "E4926", {"start": v(69.92, 7.8) * mm, "end": v(69.94, 7.8) * mm});
            skLineSegment(sketch, "E4927", {"start": v(69.94, 7.8) * mm, "end": v(70.17, 7.8) * mm});
            skLineSegment(sketch, "E4928", {"start": v(70.17, 7.8) * mm, "end": v(70.9, 7.84) * mm});
            skLineSegment(sketch, "E4929", {"start": v(70.9, 7.84) * mm, "end": v(71.64, 7.9) * mm});
            skLineSegment(sketch, "E4930", {"start": v(71.64, 7.9) * mm, "end": v(72.2, 8.04) * mm});
            skLineSegment(sketch, "E4931", {"start": v(72.2, 8.04) * mm, "end": v(72.63, 8.27) * mm});
            skLineSegment(sketch, "E4932", {"start": v(72.63, 8.27) * mm, "end": v(72.94, 8.63) * mm});
            skLineSegment(sketch, "E4933", {"start": v(72.94, 8.63) * mm, "end": v(73.18, 9.14) * mm});
            skLineSegment(sketch, "E4934", {"start": v(73.18, 9.14) * mm, "end": v(73.4, 9.84) * mm});
            skLineSegment(sketch, "E4935", {"start": v(73.4, 9.84) * mm, "end": v(73.56, 10.53) * mm});
            skLineSegment(sketch, "E4936", {"start": v(73.56, 10.53) * mm, "end": v(73.61, 10.77) * mm});
            skLineSegment(sketch, "E4937", {"start": v(73.61, 10.77) * mm, "end": v(73.98, 12.47) * mm});
            skLineSegment(sketch, "E4938", {"start": v(73.98, 12.47) * mm, "end": v(77.6, 29.57) * mm});
            skLineSegment(sketch, "E4939", {"start": v(77.6, 29.57) * mm, "end": v(77.96, 31.27) * mm});
            skLineSegment(sketch, "E4940", {"start": v(77.96, 31.27) * mm, "end": v(77.98, 31.36) * mm});
            skLineSegment(sketch, "E4941", {"start": v(77.98, 31.36) * mm, "end": v(77.98, 31.8) * mm});
            skLineSegment(sketch, "E4942", {"start": v(77.98, 31.8) * mm, "end": v(77.81, 32.3) * mm});
            skLineSegment(sketch, "E4943", {"start": v(77.81, 32.3) * mm, "end": v(77.74, 32.43) * mm});
            skLineSegment(sketch, "E4944", {"start": v(77.74, 32.43) * mm, "end": v(76.51, 30.43) * mm});
            skLineSegment(sketch, "E4945", {"start": v(76.51, 30.43) * mm, "end": v(70.33, 20.38) * mm});
            skLineSegment(sketch, "E4946", {"start": v(70.33, 20.38) * mm, "end": v(64, 10.12) * mm});
            skLineSegment(sketch, "E4947", {"start": v(64, 10.12) * mm, "end": v(62.71, 8) * mm});
            skLineSegment(sketch, "E4948", {"start": v(62.71, 8) * mm, "end": v(62.49, 8.87) * mm});
            skLineSegment(sketch, "E4949", {"start": v(62.49, 8.87) * mm, "end": v(61.77, 12.97) * mm});
            skLineSegment(sketch, "E4950", {"start": v(61.77, 12.97) * mm, "end": v(61.26, 16.85) * mm});
            skLineSegment(sketch, "E4951", {"start": v(61.26, 16.85) * mm, "end": v(61.14, 17.61) * mm});
            skLineSegment(sketch, "E4952", {"start": v(61.14, 17.61) * mm, "end": v(61.01, 18.4) * mm});
            skLineSegment(sketch, "E4953", {"start": v(61.01, 18.4) * mm, "end": v(59.9, 26.38) * mm});
            skLineSegment(sketch, "E4954", {"start": v(59.9, 26.38) * mm, "end": v(59.78, 27.18) * mm});
            skLineSegment(sketch, "E4955", {"start": v(59.78, 27.18) * mm, "end": v(59.67, 27.95) * mm});
            skLineSegment(sketch, "E4956", {"start": v(59.67, 27.95) * mm, "end": v(58.5, 35.68) * mm});
            skLineSegment(sketch, "E4957", {"start": v(58.5, 35.68) * mm, "end": v(58.39, 36.45) * mm});
            skLineSegment(sketch, "E4958", {"start": v(58.39, 36.45) * mm, "end": v(58.35, 36.45) * mm});
            skLineSegment(sketch, "E4959", {"start": v(58.35, 36.45) * mm, "end": v(58.02, 36.45) * mm});
            skLineSegment(sketch, "E4960", {"start": v(58.02, 36.45) * mm, "end": v(57.98, 36.45) * mm});
            skLineSegment(sketch, "E4961", {"start": v(57.98, 36.45) * mm, "end": v(57.85, 35.82) * mm});
            skLineSegment(sketch, "E4962", {"start": v(57.85, 35.82) * mm, "end": v(56.48, 29.46) * mm});
            skLineSegment(sketch, "E4963", {"start": v(56.48, 29.46) * mm, "end": v(56.34, 28.82) * mm});
            skLineSegment(sketch, "E4964", {"start": v(56.34, 28.82) * mm, "end": v(56.1, 27.7) * mm});
            skLineSegment(sketch, "E4965", {"start": v(56.1, 27.7) * mm, "end": v(53.77, 16.46) * mm});
            skLineSegment(sketch, "E4966", {"start": v(53.77, 16.46) * mm, "end": v(53.54, 15.34) * mm});
            skLineSegment(sketch, "E4967", {"start": v(53.54, 15.34) * mm, "end": v(53.46, 14.94) * mm});
            skLineSegment(sketch, "E4968", {"start": v(53.46, 14.94) * mm, "end": v(53.33, 13.73) * mm});
            skLineSegment(sketch, "E4969", {"start": v(53.33, 13.73) * mm, "end": v(53.54, 12.6) * mm});
            skLineSegment(sketch, "E4970", {"start": v(53.54, 12.6) * mm, "end": v(54.27, 11.7) * mm});
            skLineSegment(sketch, "E4971", {"start": v(54.27, 11.7) * mm, "end": v(55.25, 11.04) * mm});
            skLineSegment(sketch, "E4972", {"start": v(55.25, 11.04) * mm, "end": v(55.6, 10.86) * mm});
            skLineSegment(sketch, "E4973", {"start": v(55.6, 10.86) * mm, "end": v(55.65, 10.83) * mm});
            skLineSegment(sketch, "E4974", {"start": v(55.65, 10.83) * mm, "end": v(55.83, 10.76) * mm});
            skLineSegment(sketch, "E4975", {"start": v(55.83, 10.76) * mm, "end": v(56.06, 10.66) * mm});
            skLineSegment(sketch, "E4976", {"start": v(56.06, 10.66) * mm, "end": v(56.22, 10.5) * mm});
            skLineSegment(sketch, "E4977", {"start": v(56.22, 10.5) * mm, "end": v(56.25, 10.28) * mm});
            skLineSegment(sketch, "E4978", {"start": v(56.25, 10.28) * mm, "end": v(56.24, 10.21) * mm});
            skLineSegment(sketch, "E4979", {"start": v(56.24, 10.21) * mm, "end": v(56.23, 10.14) * mm});
            skLineSegment(sketch, "E4980", {"start": v(56.23, 10.14) * mm, "end": v(56.11, 9.95) * mm});
            skLineSegment(sketch, "E4981", {"start": v(56.11, 9.95) * mm, "end": v(55.9, 9.85) * mm});
            skLineSegment(sketch, "E4982", {"start": v(55.9, 9.85) * mm, "end": v(55.66, 9.87) * mm});
            skLineSegment(sketch, "E4983", {"start": v(55.66, 9.87) * mm, "end": v(55.47, 9.9) * mm});
            skLineSegment(sketch, "E4984", {"start": v(55.47, 9.9) * mm, "end": v(55.41, 9.92) * mm});
            skLineSegment(sketch, "E4985", {"start": v(55.41, 9.92) * mm, "end": v(54.8, 10.05) * mm});
            skLineSegment(sketch, "E4986", {"start": v(54.8, 10.05) * mm, "end": v(48.6, 11.4) * mm});
            skLineSegment(sketch, "E4987", {"start": v(48.6, 11.4) * mm, "end": v(47.98, 11.53) * mm});
            skLineSegment(sketch, "E4988", {"start": v(47.98, 11.53) * mm, "end": v(47.93, 11.54) * mm});
            skLineSegment(sketch, "E4989", {"start": v(47.93, 11.54) * mm, "end": v(47.72, 11.68) * mm});
            skLineSegment(sketch, "E4990", {"start": v(47.72, 11.68) * mm, "end": v(47.61, 12.01) * mm});
            skLineSegment(sketch, "E4991", {"start": v(47.61, 12.01) * mm, "end": v(47.61, 12.12) * mm});
            skLineSegment(sketch, "E4992", {"start": v(47.61, 12.12) * mm, "end": v(47.61, 12.17) * mm});
            skLineSegment(sketch, "E4993", {"start": v(47.61, 12.17) * mm, "end": v(47.8, 12.3) * mm});
            skLineSegment(sketch, "E4994", {"start": v(47.8, 12.3) * mm, "end": v(48.13, 12.33) * mm});
            skLineSegment(sketch, "E4995", {"start": v(48.13, 12.33) * mm, "end": v(48.2, 12.33) * mm});
            skLineSegment(sketch, "E4996", {"start": v(48.2, 12.33) * mm, "end": v(48.58, 12.36) * mm});
            skLineSegment(sketch, "E4997", {"start": v(48.58, 12.36) * mm, "end": v(49.73, 12.57) * mm});
            skLineSegment(sketch, "E4998", {"start": v(49.73, 12.57) * mm, "end": v(50.8, 13.11) * mm});
            skLineSegment(sketch, "E4999", {"start": v(50.8, 13.11) * mm, "end": v(51.53, 14.06) * mm});
            skLineSegment(sketch, "E5000", {"start": v(51.53, 14.06) * mm, "end": v(51.92, 15.15) * mm});
            skLineSegment(sketch, "E5001", {"start": v(51.92, 15.15) * mm, "end": v(52, 15.52) * mm});
            skLineSegment(sketch, "E5002", {"start": v(52, 15.52) * mm, "end": v(52.15, 16.15) * mm});
            skLineSegment(sketch, "E5003", {"start": v(52.15, 16.15) * mm, "end": v(53.5, 22.52) * mm});
            skLineSegment(sketch, "E5004", {"start": v(53.5, 22.52) * mm, "end": v(53.63, 23.16) * mm});
            skLineSegment(sketch, "E5005", {"start": v(53.63, 23.16) * mm, "end": v(53.86, 24.26) * mm});
            skLineSegment(sketch, "E5006", {"start": v(53.86, 24.26) * mm, "end": v(56.17, 35.33) * mm});
            skLineSegment(sketch, "E5007", {"start": v(56.17, 35.33) * mm, "end": v(56.4, 36.44) * mm});
            skLineSegment(sketch, "E5008", {"start": v(56.4, 36.44) * mm, "end": v(56.42, 36.5) * mm});
            skLineSegment(sketch, "E5009", {"start": v(56.42, 36.5) * mm, "end": v(56.55, 37.18) * mm});
            skLineSegment(sketch, "E5010", {"start": v(56.55, 37.18) * mm, "end": v(56.56, 37.24) * mm});
            skLineSegment(sketch, "E5011", {"start": v(56.56, 37.24) * mm, "end": v(56.61, 37.58) * mm});
            skLineSegment(sketch, "E5012", {"start": v(56.61, 37.58) * mm, "end": v(56.66, 38.6) * mm});
            skLineSegment(sketch, "E5013", {"start": v(56.66, 38.6) * mm, "end": v(56.41, 39.5) * mm});
            skLineSegment(sketch, "E5014", {"start": v(56.41, 39.5) * mm, "end": v(55.7, 40.16) * mm});
            skLineSegment(sketch, "E5015", {"start": v(55.7, 40.16) * mm, "end": v(54.75, 40.63) * mm});
            skLineSegment(sketch, "E5016", {"start": v(54.75, 40.63) * mm, "end": v(54.43, 40.76) * mm});
            skLineSegment(sketch, "E5017", {"start": v(54.43, 40.76) * mm, "end": v(54.36, 40.78) * mm});
            skLineSegment(sketch, "E5018", {"start": v(54.36, 40.78) * mm, "end": v(54.18, 40.84) * mm});
            skLineSegment(sketch, "E5019", {"start": v(54.18, 40.84) * mm, "end": v(53.95, 40.93) * mm});
            skLineSegment(sketch, "E5020", {"start": v(53.95, 40.93) * mm, "end": v(53.8, 41.1) * mm});
            skLineSegment(sketch, "E5021", {"start": v(53.8, 41.1) * mm, "end": v(53.78, 41.3) * mm});
            skLineSegment(sketch, "E5022", {"start": v(53.78, 41.3) * mm, "end": v(53.8, 41.37) * mm});
            skLineSegment(sketch, "E5023", {"start": v(53.8, 41.37) * mm, "end": v(53.81, 41.44) * mm});
            skLineSegment(sketch, "E5024", {"start": v(53.81, 41.44) * mm, "end": v(53.94, 41.62) * mm});
            skLineSegment(sketch, "E5025", {"start": v(53.94, 41.62) * mm, "end": v(54.15, 41.7) * mm});
            skLineSegment(sketch, "E5026", {"start": v(54.15, 41.7) * mm, "end": v(54.4, 41.67) * mm});
            skLineSegment(sketch, "E5027", {"start": v(54.4, 41.67) * mm, "end": v(54.59, 41.63) * mm});
            skLineSegment(sketch, "E5028", {"start": v(54.59, 41.63) * mm, "end": v(54.65, 41.61) * mm});
            skLineSegment(sketch, "E5029", {"start": v(54.65, 41.61) * mm, "end": v(55.39, 41.47) * mm});
            skLineSegment(sketch, "E5030", {"start": v(55.39, 41.47) * mm, "end": v(62.77, 39.95) * mm});
            skLineSegment(sketch, "E5031", {"start": v(62.77, 39.95) * mm, "end": v(63.5, 39.8) * mm});
            skLineSegment(sketch, "E5032", {"start": v(63.5, 39.8) * mm, "end": v(63.63, 39.78) * mm});
            skLineSegment(sketch, "E5033", {"start": v(63.63, 39.78) * mm, "end": v(63.97, 39.62) * mm});
            skLineSegment(sketch, "E5034", {"start": v(63.97, 39.62) * mm, "end": v(64.24, 39.3) * mm});
            skLineSegment(sketch, "E5035", {"start": v(64.24, 39.3) * mm, "end": v(64.38, 38.9) * mm});
            skLineSegment(sketch, "E5036", {"start": v(64.38, 38.9) * mm, "end": v(64.44, 38.56) * mm});
            skLineSegment(sketch, "E5037", {"start": v(64.44, 38.56) * mm, "end": v(64.46, 38.44) * mm});
            skLineSegment(sketch, "E5038", {"start": v(64.46, 38.44) * mm, "end": v(64.66, 37.02) * mm});
            skLineSegment(sketch, "E5039", {"start": v(64.66, 37.02) * mm, "end": v(66.68, 22.76) * mm});
            skLineSegment(sketch, "E5040", {"start": v(66.68, 22.76) * mm, "end": v(66.88, 21.34) * mm});
            skLineSegment(sketch, "E5041", {"start": v(66.88, 21.34) * mm, "end": v(66.9, 21.14) * mm});
            skLineSegment(sketch, "E5042", {"start": v(66.9, 21.14) * mm, "end": v(67.04, 20.13) * mm});
            skLineSegment(sketch, "E5043", {"start": v(67.04, 20.13) * mm, "end": v(67.3, 19.14) * mm});
            skLineSegment(sketch, "E5044", {"start": v(67.3, 19.14) * mm, "end": v(67.4, 18.94) * mm});
            skLineSegment(sketch, "E5045", {"start": v(67.4, 18.94) * mm, "end": v(67.5, 18.98) * mm});
            skLineSegment(sketch, "E5046", {"start": v(67.5, 18.98) * mm, "end": v(67.82, 19.18) * mm});
            skLineSegment(sketch, "E5047", {"start": v(67.82, 19.18) * mm, "end": v(68.1, 19.53) * mm});
            skLineSegment(sketch, "E5048", {"start": v(68.1, 19.53) * mm, "end": v(68.32, 19.94) * mm});
            skLineSegment(sketch, "E5049", {"start": v(68.32, 19.94) * mm, "end": v(68.47, 20.24) * mm});
            skLineSegment(sketch, "E5050", {"start": v(68.47, 20.24) * mm, "end": v(68.53, 20.33) * mm});
            skLineSegment(sketch, "E5051", {"start": v(68.53, 20.33) * mm, "end": v(69.29, 21.58) * mm});
            skLineSegment(sketch, "E5052", {"start": v(69.29, 21.58) * mm, "end": v(76.82, 34.05) * mm});
            skLineSegment(sketch, "E5053", {"start": v(76.82, 34.05) * mm, "end": v(77.56, 35.3) * mm});
            skLineSegment(sketch, "E5054", {"start": v(77.56, 35.3) * mm, "end": v(77.66, 35.48) * mm});
            skLineSegment(sketch, "E5055", {"start": v(77.66, 35.48) * mm, "end": v(78.04, 35.97) * mm});
            skLineSegment(sketch, "E5056", {"start": v(78.04, 35.97) * mm, "end": v(78.57, 36.35) * mm});
            skLineSegment(sketch, "E5057", {"start": v(78.57, 36.35) * mm, "end": v(79.2, 36.48) * mm});
            skLineSegment(sketch, "E5058", {"start": v(79.2, 36.48) * mm, "end": v(79.82, 36.4) * mm});
            skLineSegment(sketch, "E5059", {"start": v(79.82, 36.4) * mm, "end": v(80.02, 36.35) * mm});
            skLineSegment(sketch, "E5060", {"start": v(80.02, 36.35) * mm, "end": v(80.46, 36.23) * mm});
            skLineSegment(sketch, "E5061", {"start": v(80.46, 36.23) * mm, "end": v(82.7, 35.7) * mm});
            skLineSegment(sketch, "E5062", {"start": v(82.7, 35.7) * mm, "end": v(84.98, 35.35) * mm});
            skLineSegment(sketch, "E5063", {"start": v(84.98, 35.35) * mm, "end": v(85.44, 35.32) * mm});
            skLineSegment(sketch, "E5064", {"start": v(85.44, 35.32) * mm, "end": v(85.67, 35.2) * mm});
            skLineSegment(sketch, "E5065", {"start": v(85.67, 35.2) * mm, "end": v(86.9, 34.87) * mm});
            skLineSegment(sketch, "E5066", {"start": v(86.9, 34.87) * mm, "end": v(88.15, 34.62) * mm});
            skLineSegment(sketch, "E5067", {"start": v(88.15, 34.62) * mm, "end": v(88.38, 34.53) * mm});
            skLineSegment(sketch, "E5068", {"start": v(88.38, 34.53) * mm, "end": v(88.44, 34.5) * mm});
            skLineSegment(sketch, "E5069", {"start": v(88.44, 34.5) * mm, "end": v(88.7, 34.13) * mm});
            skLineSegment(sketch, "E5070", {"start": v(88.7, 34.13) * mm, "end": v(88.7, 34.08) * mm});
            skLineSegment(sketch, "E5071", {"start": v(88.7, 34.08) * mm, "end": v(88.7, 34.01) * mm});
            skLineSegment(sketch, "E5072", {"start": v(88.7, 34.01) * mm, "end": v(88.56, 33.81) * mm});
            skLineSegment(sketch, "E5073", {"start": v(88.56, 33.81) * mm, "end": v(88.34, 33.72) * mm});
            skLineSegment(sketch, "E5074", {"start": v(88.34, 33.72) * mm, "end": v(88.3, 33.7) * mm});
            skLineSegment(sketch, "E5075", {"start": v(88.3, 33.7) * mm, "end": v(88.28, 33.7) * mm});
            skLineSegment(sketch, "E5076", {"start": v(88.28, 33.7) * mm, "end": v(88.1, 33.7) * mm});
            skLineSegment(sketch, "E5077", {"start": v(88.1, 33.7) * mm, "end": v(88.1, 33.7) * mm});
            skLineSegment(sketch, "E5078", {"start": v(88.1, 33.7) * mm, "end": v(87.84, 33.7) * mm});
            skLineSegment(sketch, "E5079", {"start": v(87.84, 33.7) * mm, "end": v(87.1, 33.63) * mm});
            skLineSegment(sketch, "E5080", {"start": v(87.1, 33.63) * mm, "end": v(86.33, 33.54) * mm});
            skLineSegment(sketch, "E5081", {"start": v(86.33, 33.54) * mm, "end": v(85.75, 33.38) * mm});
            skLineSegment(sketch, "E5082", {"start": v(85.75, 33.38) * mm, "end": v(85.32, 33.14) * mm});
            skLineSegment(sketch, "E5083", {"start": v(85.32, 33.14) * mm, "end": v(85, 32.77) * mm});
            skLineSegment(sketch, "E5084", {"start": v(85, 32.77) * mm, "end": v(84.76, 32.24) * mm});
            skLineSegment(sketch, "E5085", {"start": v(84.76, 32.24) * mm, "end": v(84.55, 31.52) * mm});
            skLineSegment(sketch, "E5086", {"start": v(84.55, 31.52) * mm, "end": v(84.38, 30.81) * mm});
            skLineSegment(sketch, "E5087", {"start": v(84.38, 30.81) * mm, "end": v(84.33, 30.58) * mm});
            skLineSegment(sketch, "E5088", {"start": v(84.33, 30.58) * mm, "end": v(83.95, 28.78) * mm});
            skLineSegment(sketch, "E5089", {"start": v(83.95, 28.78) * mm, "end": v(80.16, 10.75) * mm});
            skLineSegment(sketch, "E5090", {"start": v(80.16, 10.75) * mm, "end": v(79.79, 8.95) * mm});
            skLineSegment(sketch, "E5091", {"start": v(79.79, 8.95) * mm, "end": v(79.72, 8.61) * mm});
            skLineSegment(sketch, "E5092", {"start": v(79.72, 8.61) * mm, "end": v(79.62, 7.59) * mm});
            skLineSegment(sketch, "E5093", {"start": v(79.62, 7.59) * mm, "end": v(79.86, 6.65) * mm});
            skLineSegment(sketch, "E5094", {"start": v(79.86, 6.65) * mm, "end": v(80.6, 5.95) * mm});
            skLineSegment(sketch, "E5095", {"start": v(80.6, 5.95) * mm, "end": v(81.6, 5.44) * mm});
            skLineSegment(sketch, "E5096", {"start": v(81.6, 5.44) * mm, "end": v(81.95, 5.3) * mm});
            skLineSegment(sketch, "E5097", {"start": v(81.95, 5.3) * mm, "end": v(82.03, 5.27) * mm});
            skLineSegment(sketch, "E5098", {"start": v(82.03, 5.27) * mm, "end": v(82.4, 5.1) * mm});
            skLineSegment(sketch, "E5099", {"start": v(82.4, 5.1) * mm, "end": v(82.54, 4.74) * mm});
            skLineSegment(sketch, "E5100", {"start": v(82.54, 4.74) * mm, "end": v(82.51, 4.65) * mm});
            skLineSegment(sketch, "E5101", {"start": v(82.51, 4.65) * mm, "end": v(82.49, 4.55) * mm});
            skLineSegment(sketch, "E5102", {"start": v(82.49, 4.55) * mm, "end": v(82.15, 4.34) * mm});
            skLineSegment(sketch, "E5103", {"start": v(82.15, 4.34) * mm, "end": v(81.74, 4.4) * mm});
            skLineSegment(sketch, "E5104", {"start": v(81.74, 4.4) * mm, "end": v(81.66, 4.42) * mm});
            skLineSegment(sketch, "E5105", {"start": v(81.66, 4.42) * mm, "end": v(81.46, 4.45) * mm});
            skLineSegment(sketch, "E5106", {"start": v(81.46, 4.45) * mm, "end": v(79.46, 4.77) * mm});
            skLineSegment(sketch, "E5107", {"start": v(79.46, 4.77) * mm, "end": v(79.25, 4.8) * mm});
            skLineSegment(sketch, "E5108", {"start": v(41.97, 116.25) * mm, "end": v(65.77, 143.52) * mm});
            skLineSegment(sketch, "E5109", {"start": v(46.64, 152.37) * mm, "end": v(40.33, 116.74) * mm});
            skLineSegment(sketch, "E5110", {"start": v(46.57, 154.33) * mm, "end": v(46.7, 154.36) * mm});
            skLineSegment(sketch, "E5111", {"start": v(46.76, 154.23) * mm, "end": v(46.7, 154.36) * mm});
            skSolve(sketch);
        }
        {
            var Q0;
            Q0=qCreatedBy(makeId("Top.planeOp"),FACE);
            var sketch = newSketch(context, id + "F1", { "sketchPlane" : qUnion([Q0])});
            skFitSpline(sketch, "E5112", {"points": [v(-135.15, 61.73) * mm, v(-32.27, 142.17) * mm], "startDerivative": vector(42.8, 100.08) * mm, "endDerivative": vector(161.98, 28.93) * mm});
            skFitSpline(sketch, "E5113", {"points": [v(-32.27, 142.17) * mm, v(11.5, 103.8) * mm], "startDerivative": vector(40.5, -21.4) * mm, "endDerivative": vector(39.92, -57.85) * mm});
            skLineSegment(sketch, "E5114", {"start": v(11.5, 103.8) * mm, "end": v(-25.14, 74.68) * mm});
            skLineSegment(sketch, "E5115", {"start": v(-25.14, 74.68) * mm, "end": v(115.8, 43.94) * mm});
            skLineSegment(sketch, "E5116", {"start": v(115.8, 43.94) * mm, "end": v(143.25, 182.24) * mm});
            skLineSegment(sketch, "E5117", {"start": v(143.25, 182.24) * mm, "end": v(106.44, 161.58) * mm});
            skFitSpline(sketch, "E5118", {"points": [v(106.44, 161.58) * mm, v(-38.8, 217.94) * mm], "startDerivative": vector(-76.94, 75.7) * mm, "endDerivative": vector(-192.69, -0.71) * mm});
            skFitSpline(sketch, "E5119", {"points": [v(-38.8, 217.94) * mm, v(-141.1, 169.94) * mm], "startDerivative": vector(-85.45, -4.73) * mm, "endDerivative": vector(-77.18, -85.23) * mm});
            skFitSpline(sketch, "E5120", {"points": [v(-141.1, 169.94) * mm, v(-195.68, 40.3) * mm], "startDerivative": vector(-66.63, -61.85) * mm, "endDerivative": vector(2.59, -182.42) * mm});
            skFitSpline(sketch, "E5121", {"points": [v(-141.1, 169.94) * mm, v(-32.27, 142.17) * mm], "startDerivative": vector(88.28, 8.52) * mm, "endDerivative": vector(112.7, -68.73) * mm});
            skFitSpline(sketch, "E5122", {"points": [v(-80.26, 124.15) * mm, v(-65.08, 158.18) * mm], "startDerivative": vector(8.78, 37.13) * mm, "endDerivative": vector(23.77, 32.97) * mm});
            skLineSegment(sketch, "E5123", {"start": v(-227.19, 29.18) * mm, "end": v(-94.36, 76.15) * mm});
            skLineSegment(sketch, "E5124", {"start": v(-94.36, 76.15) * mm, "end": v(-49.11, -63.29) * mm});
            skLineSegment(sketch, "E5125", {"start": v(-227.19, 29.18) * mm, "end": v(-190.8, 6.84) * mm});
            skLineSegment(sketch, "E5126", {"start": v(-49.11, -63.29) * mm, "end": v(-93.54, -44.71) * mm});
            skFitSpline(sketch, "E5127", {"points": [v(-93.54, -44.71) * mm, v(-73.59, -211.05) * mm], "startDerivative": vector(-40.96, -87.47) * mm, "endDerivative": vector(121.39, -157.26) * mm});
            skFitSpline(sketch, "E5128", {"points": [v(-190.8, 6.84) * mm, v(-73.59, -211.05) * mm], "startDerivative": vector(-65.36, -261.96) * mm, "endDerivative": vector(284.41, -67.12) * mm});
            skLineSegment(sketch, "E5129", {"start": v(90.56, -170.52) * mm, "end": v(90.56, -213.2) * mm});
            skLineSegment(sketch, "E5130", {"start": v(90.56, -213.2) * mm, "end": v(-16.4, -121.68) * mm});
            skLineSegment(sketch, "E5131", {"start": v(-16.4, -121.68) * mm, "end": v(81.06, -13.07) * mm});
            skLineSegment(sketch, "E5132", {"start": v(81.06, -13.07) * mm, "end": v(88.06, -60.14) * mm});
            skFitSpline(sketch, "E5133", {"points": [v(-73.59, -211.05) * mm, v(64.84, -191.2) * mm], "startDerivative": vector(178.97, -56.05) * mm, "endDerivative": vector(41, 36.97) * mm});
            skFitSpline(sketch, "E5134", {"points": [v(-104.04, -114.9) * mm, v(22.15, -154.67) * mm], "startDerivative": vector(98.02, -87.39) * mm, "endDerivative": vector(156.83, 15.77) * mm});
            skFitSpline(sketch, "E5135", {"points": [v(-101.47, -141.93) * mm, v(-69.49, -138.78) * mm], "startDerivative": vector(22.85, -1.08) * mm, "endDerivative": vector(31.76, 10.16) * mm});
            skFitSpline(sketch, "E5136", {"points": [v(90.56, -170.52) * mm, v(222, 39.27) * mm], "startDerivative": vector(285.1, 93.56) * mm, "endDerivative": vector(-84.04, 282.69) * mm});
            skFitSpline(sketch, "E5137", {"points": [v(88.06, -60.14) * mm, v(222, 39.27) * mm], "startDerivative": vector(72.24, 7.07) * mm, "endDerivative": vector(109.85, 217.02) * mm});
            skFitSpline(sketch, "E5138", {"points": [v(222, 39.27) * mm, v(136.58, 148.62) * mm], "startDerivative": vector(-39.22, 157.98) * mm, "endDerivative": vector(-101.6, 45.77) * mm});
            skFitSpline(sketch, "E5139", {"points": [v(146.2, -39.08) * mm, v(122.98, 80.08) * mm], "startDerivative": vector(30.5, 117.25) * mm, "endDerivative": vector(-57.3, 73.82) * mm});
            skFitSpline(sketch, "E5140", {"points": [v(172.92, -20.96) * mm, v(148.33, 9.59) * mm], "startDerivative": vector(-12.28, 30.4) * mm, "endDerivative": vector(-30.07, 26.13) * mm});
            skSolve(sketch);
        }
        {
            var Q0;
            {var subQ19=sQuery(id+"F1.wireOp",EDGE,"E5113");Q0=makeQuery(id+"F1.imprint","IMPRINT",FACE,{"disambiguationData":[TD([[makeQuery(id+"F1.imprint","IMPRINT",EDGE,{"derivedFrom":subQ19}),-1.0]])]});}
            extrude(context, id + "F2", {"entities" : qUnion([Q0]), "depth" : 25.4 * mm, "offsetDistance" : 25.4 * mm});
        }
        {
            var Q0;
            Q0=qCreatedBy(makeId("Front.planeOp"),FACE);
            var sketch = newSketch(context, id + "F3", { "sketchPlane" : qUnion([Q0])});
            skLineSegment(sketch, "E5141", {"start": v(0, 0) * mm, "end": v(0, 25.4) * mm, "construction": true});
            skFitSpline(sketch, "E5142", {"points": [v(158.9, 0) * mm, v(0, 25.4) * mm], "startDerivative": vector(-49.55, 40.69) * mm, "endDerivative": vector(-36.7, -2.73) * mm});
            skLineSegment(sketch, "E5143", {"start": v(0, 25.4) * mm, "end": v(0, 0) * mm});
            skLineSegment(sketch, "E5144", {"start": v(0, 25.4) * mm, "end": v(158.9, 25.4) * mm});
            skLineSegment(sketch, "E5145", {"start": v(158.9, 0) * mm, "end": v(158.9, 25.4) * mm});
            skSolve(sketch);
        }
        {
            var Q0;
            {var subQ0=sQuery(id+"F3.wireOp",EDGE,"E5145");Q0=makeQuery(id+"F3.imprint","IMPRINT",FACE,{"disambiguationData":[TD([[makeQuery(id+"F3.imprint","IMPRINT",EDGE,{"derivedFrom":subQ0}),1.0]])]});}
            var Q1;
            Q1=sQuery(id+"F3.wireOp",EDGE,"E5143");
            revolve(context, id + "F4", {"operationType" : NewBodyOperationType.REMOVE, "surfaceOperationType" : NewSurfaceOperationType.NEW, "entities" : qUnion([Q0]), "axis" : qUnion([Q1]), "revolveType" : RevolveType.FULL, "oppositeDirection" : true});
        }
        {
            var Q0;
            {var subQ0=sQuery(id+"F1.wireOp",EDGE,"E5124");Q0=makeQuery(id+"F1.imprint","IMPRINT",FACE,{"disambiguationData":[TD([[makeQuery(id+"F1.imprint","IMPRINT",EDGE,{"derivedFrom":subQ0}),-1.0]])]});}
            var Q1;
            {var subQ7=sQuery(id+"F1.wireOp",EDGE,"E5113");Q1=makeQuery(id+"F1.imprint","IMPRINT",FACE,{"disambiguationData":[TD([[makeQuery(id+"F1.imprint","IMPRINT",EDGE,{"derivedFrom":subQ7}),1.0]])]});}
            var Q2;
            {var subQ7=sQuery(id+"F1.wireOp",EDGE,"E5129");Q2=makeQuery(id+"F1.imprint","IMPRINT",FACE,{"disambiguationData":[TD([[makeQuery(id+"F1.imprint","IMPRINT",EDGE,{"derivedFrom":subQ7}),-1.0]])]});}
            extrude(context, id + "F5", {"entities" : qUnion([Q0, Q1, Q2]), "depth" : 25.4 * mm, "offsetDistance" : 25.4 * mm});
        }
        {
            var Q0;
            Q0=qCreatedBy(makeId("Front.planeOp"),FACE);
            var sketch = newSketch(context, id + "F6", { "sketchPlane" : qUnion([Q0])});
            skLineSegment(sketch, "E5146", {"start": v(0, 0) * mm, "end": v(0, 25.4) * mm});
            skLineSegment(sketch, "E5147", {"start": v(254, 25.4) * mm, "end": v(254, 0) * mm});
            skLineSegment(sketch, "E5148", {"start": v(0, 25.4) * mm, "end": v(66.04, 25.4) * mm});
            skLineSegment(sketch, "E5149", {"start": v(66.04, 25.4) * mm, "end": v(254, 25.4) * mm});
            skFitSpline(sketch, "E5150", {"points": [v(66.04, 25.4) * mm, v(254, 0) * mm], "startDerivative": vector(214.35, 0) * mm, "endDerivative": vector(80.17, -36.72) * mm});
            skSolve(sketch);
        }
        {
            var Q0;
            Q0=qSketchRegion(id+"F6",true);
            var Q1;
            Q1=sQuery(id+"F3.wireOp",EDGE,"E5143");
            revolve(context, id + "F7", {"operationType" : NewBodyOperationType.REMOVE, "surfaceOperationType" : NewSurfaceOperationType.NEW, "entities" : qUnion([Q0]), "axis" : qUnion([Q1]), "revolveType" : RevolveType.FULL, "oppositeDirection" : true});
        }
        {
            var Q0;
            {var subQ0=sQuery(id+"F1.wireOp",EDGE,"E5122");Q0=makeQuery(id+"F1.imprint","IMPRINT",FACE,{"disambiguationData":[TD([[makeQuery(id+"F1.imprint","IMPRINT",EDGE,{"derivedFrom":subQ0}),1.0]])]});}
            var Q1;
            {var subQ0=sQuery(id+"F1.wireOp",EDGE,"E5133");Q1=makeQuery(id+"F1.imprint","IMPRINT",FACE,{"disambiguationData":[TD([[makeQuery(id+"F1.imprint","IMPRINT",EDGE,{"derivedFrom":subQ0}),1.0]])]});}
            var Q2;
            {var subQ0=sQuery(id+"F1.wireOp",EDGE,"E5138");Q2=makeQuery(id+"F1.imprint","IMPRINT",FACE,{"disambiguationData":[TD([[makeQuery(id+"F1.imprint","IMPRINT",EDGE,{"derivedFrom":subQ0}),1.0]])]});}
            extrude(context, id + "F8", {"entities" : qUnion([Q0, Q1, Q2]), "depth" : 8.9 * mm, "offsetDistance" : 25.4 * mm});
        }
        {
            var Q0;
            Q0=qCreatedBy(makeId("Front.planeOp"),FACE);
            var sketch = newSketch(context, id + "F9", { "sketchPlane" : qUnion([Q0])});
            skFitSpline(sketch, "E5151", {"points": [v(145.47, 3.3) * mm, v(229.32, 10.98) * mm], "startDerivative": vector(99.34, -0.88) * mm, "endDerivative": vector(22.91, 23.21) * mm});
            skLineSegment(sketch, "E5152", {"start": v(229.25, 10.9) * mm, "end": v(145.47, 10.9) * mm});
            skLineSegment(sketch, "E5153", {"start": v(145.47, 3.3) * mm, "end": v(145.47, 10.9) * mm});
            skSolve(sketch);
        }
        {
            var Q0;
            Q0=makeQuery(id+"F9.imprint","IMPRINT",FACE,{"disambiguationData":[TD([[makeQuery(id+"F9.imprint","IMPRINT",EDGE,{"derivedFrom":sQuery(id+"F9.wireOp",EDGE,"E5151")}),1.0]])]});
            var Q1;
            Q1=sQuery(id+"F6.wireOp",EDGE,"E5146");
            revolve(context, id + "F10", {"operationType" : NewBodyOperationType.REMOVE, "surfaceOperationType" : NewSurfaceOperationType.NEW, "entities" : qUnion([Q0]), "axis" : qUnion([Q1]), "revolveType" : RevolveType.FULL, "oppositeDirection" : true});
        }
        {
            var Q0;
            Q0=makeQuery(id+"F0.imprint","IMPRINT",FACE,{"disambiguationData":[TD([[makeQuery(id+"F0.imprint","IMPRINT",EDGE,{"derivedFrom":sQuery(id+"F0.wireOp",EDGE,"E858")}),-1.0]])]});
            var Q1;
            Q1=makeQuery(id+"F0.imprint","IMPRINT",FACE,{"disambiguationData":[TD([[makeQuery(id+"F0.imprint","IMPRINT",EDGE,{"derivedFrom":sQuery(id+"F0.wireOp",EDGE,"E1334")}),-1.0]])]});
            var Q2;
            Q2=makeQuery(id+"F0.imprint","IMPRINT",FACE,{"disambiguationData":[TD([[makeQuery(id+"F0.imprint","IMPRINT",EDGE,{"derivedFrom":sQuery(id+"F0.wireOp",EDGE,"E684")}),-1.0]])]});
            var Q3;
            Q3=makeQuery(id+"F0.imprint","IMPRINT",FACE,{"disambiguationData":[TD([[makeQuery(id+"F0.imprint","IMPRINT",EDGE,{"derivedFrom":sQuery(id+"F0.wireOp",EDGE,"E1196")}),-1.0]])]});
            var Q4;
            Q4=makeQuery(id+"F0.imprint","IMPRINT",FACE,{"disambiguationData":[TD([[makeQuery(id+"F0.imprint","IMPRINT",EDGE,{"derivedFrom":sQuery(id+"F0.wireOp",EDGE,"E995")}),-1.0]])]});
            var Q5;
            Q5=makeQuery(id+"F0.imprint","IMPRINT",FACE,{"disambiguationData":[TD([[makeQuery(id+"F0.imprint","IMPRINT",EDGE,{"derivedFrom":sQuery(id+"F0.wireOp",EDGE,"E1436")}),-1.0]])]});
            var Q6;
            Q6=makeQuery(id+"F2.opExtrude","CAP_FACE",FACE,{"disambiguationData":[OSD([sQuery(id+"F1.wireOp",EDGE,"E5112"),sQuery(id+"F1.wireOp",EDGE,"E5113"),sQuery(id+"F1.wireOp",EDGE,"E5114"),sQuery(id+"F1.wireOp",EDGE,"E5115"),sQuery(id+"F1.wireOp",EDGE,"E5116"),sQuery(id+"F1.wireOp",EDGE,"E5123"),sQuery(id+"F1.wireOp",EDGE,"E5124"),sQuery(id+"F1.wireOp",EDGE,"E5126"),sQuery(id+"F1.wireOp",EDGE,"E5127"),sQuery(id+"F1.wireOp",EDGE,"E5130"),sQuery(id+"F1.wireOp",EDGE,"E5131"),sQuery(id+"F1.wireOp",EDGE,"E5132"),sQuery(id+"F1.wireOp",EDGE,"E5134"),sQuery(id+"F1.wireOp",EDGE,"E5137"),sQuery(id+"F1.wireOp",EDGE,"E5139")])],"isStart":false});
            extrude(context, id + "F11", {"entities" : qUnion([Q0, Q1, Q2, Q3, Q4, Q5]), "operationType" : NewBodyOperationType.REMOVE, "endBound" : BoundingType.UP_TO_SURFACE, "depth" : 25.4 * mm, "endBoundEntityFace" : qUnion([Q6]), "offsetDistance" : 25.4 * mm});
        }
        {
            var Q0;
            Q0=makeQuery(id+"F0.imprint","IMPRINT",FACE,{"disambiguationData":[TD([[makeQuery(id+"F0.imprint","IMPRINT",EDGE,{"derivedFrom":sQuery(id+"F0.wireOp",EDGE,"E4809")}),-1.0]])]});
            var Q1;
            Q1=makeQuery(id+"F0.imprint","IMPRINT",FACE,{"disambiguationData":[TD([[makeQuery(id+"F0.imprint","IMPRINT",EDGE,{"derivedFrom":sQuery(id+"F0.wireOp",EDGE,"E4739")}),-1.0]])]});
            var Q2;
            Q2=makeQuery(id+"F0.imprint","IMPRINT",FACE,{"disambiguationData":[TD([[makeQuery(id+"F0.imprint","IMPRINT",EDGE,{"derivedFrom":sQuery(id+"F0.wireOp",EDGE,"E4233")}),-1.0]])]});
            var Q3;
            Q3=makeQuery(id+"F0.imprint","IMPRINT",FACE,{"disambiguationData":[TD([[makeQuery(id+"F0.imprint","IMPRINT",EDGE,{"derivedFrom":sQuery(id+"F0.wireOp",EDGE,"E4595")}),-1.0]])]});
            var Q4;
            Q4=makeQuery(id+"F0.imprint","IMPRINT",FACE,{"disambiguationData":[TD([[makeQuery(id+"F0.imprint","IMPRINT",EDGE,{"derivedFrom":sQuery(id+"F0.wireOp",EDGE,"E4004")}),-1.0]])]});
            extrude(context, id + "F12", {"entities" : qUnion([Q0, Q1, Q2, Q3, Q4]), "operationType" : NewBodyOperationType.REMOVE, "depth" : 25.4 * mm, "offsetDistance" : 25.4 * mm});
        }
        {
            var Q0;
            Q0=makeQuery(id+"F0.imprint","IMPRINT",FACE,{"disambiguationData":[TD([[makeQuery(id+"F0.imprint","IMPRINT",EDGE,{"derivedFrom":sQuery(id+"F0.wireOp",EDGE,"E149")}),-1.0]])]});
            var Q1;
            Q1=makeQuery(id+"F0.imprint","IMPRINT",FACE,{"disambiguationData":[TD([[makeQuery(id+"F0.imprint","IMPRINT",EDGE,{"derivedFrom":sQuery(id+"F0.wireOp",EDGE,"E587")}),-1.0]])]});
            var Q2;
            Q2=makeQuery(id+"F0.imprint","IMPRINT",FACE,{"disambiguationData":[TD([[makeQuery(id+"F0.imprint","IMPRINT",EDGE,{"derivedFrom":sQuery(id+"F0.wireOp",EDGE,"E433")}),-1.0]])]});
            var Q3;
            Q3=makeQuery(id+"F0.imprint","IMPRINT",FACE,{"disambiguationData":[TD([[makeQuery(id+"F0.imprint","IMPRINT",EDGE,{"derivedFrom":sQuery(id+"F0.wireOp",EDGE,"E2759")}),-1.0]])]});
            var Q4;
            Q4=makeQuery(id+"F0.imprint","IMPRINT",FACE,{"disambiguationData":[TD([[makeQuery(id+"F0.imprint","IMPRINT",EDGE,{"derivedFrom":sQuery(id+"F0.wireOp",EDGE,"E2469")}),-1.0]])]});
            var Q5;
            Q5=makeQuery(id+"F0.imprint","IMPRINT",FACE,{"disambiguationData":[TD([[makeQuery(id+"F0.imprint","IMPRINT",EDGE,{"derivedFrom":sQuery(id+"F0.wireOp",EDGE,"E2609")}),-1.0]])]});
            var Q6;
            Q6=makeQuery(id+"F0.imprint","IMPRINT",FACE,{"disambiguationData":[TD([[makeQuery(id+"F0.imprint","IMPRINT",EDGE,{"derivedFrom":sQuery(id+"F0.wireOp",EDGE,"E2359")}),-1.0]])]});
            var Q7;
            Q7=makeQuery(id+"F0.imprint","IMPRINT",FACE,{"disambiguationData":[TD([[makeQuery(id+"F0.imprint","IMPRINT",EDGE,{"derivedFrom":sQuery(id+"F0.wireOp",EDGE,"E292")}),-1.0]])]});
            var Q8;
            Q8=makeQuery(id+"F2.opExtrude","CAP_FACE",FACE,{"disambiguationData":[OSD([sQuery(id+"F1.wireOp",EDGE,"E5112"),sQuery(id+"F1.wireOp",EDGE,"E5113"),sQuery(id+"F1.wireOp",EDGE,"E5114"),sQuery(id+"F1.wireOp",EDGE,"E5115"),sQuery(id+"F1.wireOp",EDGE,"E5116"),sQuery(id+"F1.wireOp",EDGE,"E5123"),sQuery(id+"F1.wireOp",EDGE,"E5124"),sQuery(id+"F1.wireOp",EDGE,"E5126"),sQuery(id+"F1.wireOp",EDGE,"E5127"),sQuery(id+"F1.wireOp",EDGE,"E5130"),sQuery(id+"F1.wireOp",EDGE,"E5131"),sQuery(id+"F1.wireOp",EDGE,"E5132"),sQuery(id+"F1.wireOp",EDGE,"E5134"),sQuery(id+"F1.wireOp",EDGE,"E5137"),sQuery(id+"F1.wireOp",EDGE,"E5139")])],"isStart":false});
            extrude(context, id + "F13", {"entities" : qUnion([Q0, Q1, Q2, Q3, Q4, Q5, Q6, Q7]), "operationType" : NewBodyOperationType.REMOVE, "endBound" : BoundingType.UP_TO_SURFACE, "depth" : 25.4 * mm, "endBoundEntityFace" : qUnion([Q8]), "offsetDistance" : 25.4 * mm});
        }
        {
            var Q0;
            Q0=makeQuery(id+"F0.imprint","IMPRINT",FACE,{"disambiguationData":[TD([[makeQuery(id+"F0.imprint","IMPRINT",EDGE,{"derivedFrom":sQuery(id+"F0.wireOp",EDGE,"E1585")}),-1.0]])]});
            var Q1;
            Q1=makeQuery(id+"F0.imprint","IMPRINT",FACE,{"disambiguationData":[TD([[makeQuery(id+"F0.imprint","IMPRINT",EDGE,{"derivedFrom":sQuery(id+"F0.wireOp",EDGE,"E1793")}),-1.0]])]});
            var Q2;
            Q2=makeQuery(id+"F0.imprint","IMPRINT",FACE,{"disambiguationData":[TD([[makeQuery(id+"F0.imprint","IMPRINT",EDGE,{"derivedFrom":sQuery(id+"F0.wireOp",EDGE,"E2008")}),-1.0]])]});
            var Q3;
            Q3=makeQuery(id+"F0.imprint","IMPRINT",FACE,{"disambiguationData":[TD([[makeQuery(id+"F0.imprint","IMPRINT",EDGE,{"derivedFrom":sQuery(id+"F0.wireOp",EDGE,"E2856")}),-1.0]])]});
            var Q4;
            Q4=makeQuery(id+"F2.opExtrude","CAP_FACE",FACE,{"disambiguationData":[OSD([sQuery(id+"F1.wireOp",EDGE,"E5112"),sQuery(id+"F1.wireOp",EDGE,"E5113"),sQuery(id+"F1.wireOp",EDGE,"E5114"),sQuery(id+"F1.wireOp",EDGE,"E5115"),sQuery(id+"F1.wireOp",EDGE,"E5116"),sQuery(id+"F1.wireOp",EDGE,"E5123"),sQuery(id+"F1.wireOp",EDGE,"E5124"),sQuery(id+"F1.wireOp",EDGE,"E5126"),sQuery(id+"F1.wireOp",EDGE,"E5127"),sQuery(id+"F1.wireOp",EDGE,"E5130"),sQuery(id+"F1.wireOp",EDGE,"E5131"),sQuery(id+"F1.wireOp",EDGE,"E5132"),sQuery(id+"F1.wireOp",EDGE,"E5134"),sQuery(id+"F1.wireOp",EDGE,"E5137"),sQuery(id+"F1.wireOp",EDGE,"E5139")])],"isStart":false});
            extrude(context, id + "F14", {"entities" : qUnion([Q0, Q1, Q2, Q3]), "operationType" : NewBodyOperationType.REMOVE, "depth" : 12.7 * mm, "endBoundEntityFace" : qUnion([Q4]), "offsetDistance" : 25.4 * mm});
        }
        {
            var Q0;
            Q0=makeQuery(id+"F0.imprint","IMPRINT",FACE,{"disambiguationData":[TD([[makeQuery(id+"F0.imprint","IMPRINT",EDGE,{"derivedFrom":sQuery(id+"F0.wireOp",EDGE,"E3771")}),-1.0]])]});
            var Q1;
            Q1=makeQuery(id+"F0.imprint","IMPRINT",FACE,{"disambiguationData":[TD([[makeQuery(id+"F0.imprint","IMPRINT",EDGE,{"derivedFrom":sQuery(id+"F0.wireOp",EDGE,"E3443")}),-1.0]])]});
            var Q2;
            Q2=makeQuery(id+"F0.imprint","IMPRINT",FACE,{"disambiguationData":[TD([[makeQuery(id+"F0.imprint","IMPRINT",EDGE,{"derivedFrom":sQuery(id+"F0.wireOp",EDGE,"E3883")}),-1.0]])]});
            var Q3;
            Q3=makeQuery(id+"F0.imprint","IMPRINT",FACE,{"disambiguationData":[TD([[makeQuery(id+"F0.imprint","IMPRINT",EDGE,{"derivedFrom":sQuery(id+"F0.wireOp",EDGE,"E4909")}),-1.0]])]});
            var Q4;
            Q4=makeQuery(id+"F0.imprint","IMPRINT",FACE,{"disambiguationData":[TD([[makeQuery(id+"F0.imprint","IMPRINT",EDGE,{"derivedFrom":sQuery(id+"F0.wireOp",EDGE,"E3335")}),-1.0]])]});
            var Q5;
            Q5=makeQuery(id+"F0.imprint","IMPRINT",FACE,{"disambiguationData":[TD([[makeQuery(id+"F0.imprint","IMPRINT",EDGE,{"derivedFrom":sQuery(id+"F0.wireOp",EDGE,"E3223")}),-1.0]])]});
            extrude(context, id + "F15", {"entities" : qUnion([Q0, Q1, Q2, Q3, Q4, Q5]), "operationType" : NewBodyOperationType.REMOVE, "depth" : 25.4 * mm, "offsetDistance" : 25.4 * mm});
        }
        {
            var Q0;
            Q0=makeQuery(id+"F0.imprint","IMPRINT",FACE,{"disambiguationData":[TD([[makeQuery(id+"F0.imprint","IMPRINT",EDGE,{"derivedFrom":sQuery(id+"F0.wireOp",EDGE,"E858")}),-1.0]])]});
            var Q1;
            Q1=makeQuery(id+"F0.imprint","IMPRINT",FACE,{"disambiguationData":[TD([[makeQuery(id+"F0.imprint","IMPRINT",EDGE,{"derivedFrom":sQuery(id+"F0.wireOp",EDGE,"E1334")}),-1.0]])]});
            var Q2;
            Q2=makeQuery(id+"F0.imprint","IMPRINT",FACE,{"disambiguationData":[TD([[makeQuery(id+"F0.imprint","IMPRINT",EDGE,{"derivedFrom":sQuery(id+"F0.wireOp",EDGE,"E684")}),-1.0]])]});
            var Q3;
            Q3=makeQuery(id+"F0.imprint","IMPRINT",FACE,{"disambiguationData":[TD([[makeQuery(id+"F0.imprint","IMPRINT",EDGE,{"derivedFrom":sQuery(id+"F0.wireOp",EDGE,"E1196")}),-1.0]])]});
            var Q4;
            Q4=makeQuery(id+"F0.imprint","IMPRINT",FACE,{"disambiguationData":[TD([[makeQuery(id+"F0.imprint","IMPRINT",EDGE,{"derivedFrom":sQuery(id+"F0.wireOp",EDGE,"E995")}),-1.0]])]});
            var Q5;
            Q5=makeQuery(id+"F0.imprint","IMPRINT",FACE,{"disambiguationData":[TD([[makeQuery(id+"F0.imprint","IMPRINT",EDGE,{"derivedFrom":sQuery(id+"F0.wireOp",EDGE,"E1436")}),-1.0]])]});
            var Q6;
            Q6=makeQuery(id+"F0.imprint","IMPRINT",FACE,{"disambiguationData":[TD([[makeQuery(id+"F0.imprint","IMPRINT",EDGE,{"derivedFrom":sQuery(id+"F0.wireOp",EDGE,"E4004")}),-1.0]])]});
            var Q7;
            Q7=makeQuery(id+"F0.imprint","IMPRINT",FACE,{"disambiguationData":[TD([[makeQuery(id+"F0.imprint","IMPRINT",EDGE,{"derivedFrom":sQuery(id+"F0.wireOp",EDGE,"E1793")}),-1.0]])]});
            var Q8;
            Q8=makeQuery(id+"F0.imprint","IMPRINT",FACE,{"disambiguationData":[TD([[makeQuery(id+"F0.imprint","IMPRINT",EDGE,{"derivedFrom":sQuery(id+"F0.wireOp",EDGE,"E1585")}),-1.0]])]});
            var Q9;
            Q9=makeQuery(id+"F0.imprint","IMPRINT",FACE,{"disambiguationData":[TD([[makeQuery(id+"F0.imprint","IMPRINT",EDGE,{"derivedFrom":sQuery(id+"F0.wireOp",EDGE,"E4595")}),-1.0]])]});
            var Q10;
            Q10=makeQuery(id+"F0.imprint","IMPRINT",FACE,{"disambiguationData":[TD([[makeQuery(id+"F0.imprint","IMPRINT",EDGE,{"derivedFrom":sQuery(id+"F0.wireOp",EDGE,"E4809")}),-1.0]])]});
            var Q11;
            Q11=makeQuery(id+"F0.imprint","IMPRINT",FACE,{"disambiguationData":[TD([[makeQuery(id+"F0.imprint","IMPRINT",EDGE,{"derivedFrom":sQuery(id+"F0.wireOp",EDGE,"E4739")}),-1.0]])]});
            var Q12;
            Q12=makeQuery(id+"F0.imprint","IMPRINT",FACE,{"disambiguationData":[TD([[makeQuery(id+"F0.imprint","IMPRINT",EDGE,{"derivedFrom":sQuery(id+"F0.wireOp",EDGE,"E4233")}),-1.0]])]});
            var Q13;
            Q13=makeQuery(id+"F0.imprint","IMPRINT",FACE,{"disambiguationData":[TD([[makeQuery(id+"F0.imprint","IMPRINT",EDGE,{"derivedFrom":sQuery(id+"F0.wireOp",EDGE,"E3223")}),-1.0]])]});
            var Q14;
            Q14=makeQuery(id+"F0.imprint","IMPRINT",FACE,{"disambiguationData":[TD([[makeQuery(id+"F0.imprint","IMPRINT",EDGE,{"derivedFrom":sQuery(id+"F0.wireOp",EDGE,"E3335")}),-1.0]])]});
            var Q15;
            Q15=makeQuery(id+"F0.imprint","IMPRINT",FACE,{"disambiguationData":[TD([[makeQuery(id+"F0.imprint","IMPRINT",EDGE,{"derivedFrom":sQuery(id+"F0.wireOp",EDGE,"E4909")}),-1.0]])]});
            var Q16;
            Q16=makeQuery(id+"F0.imprint","IMPRINT",FACE,{"disambiguationData":[TD([[makeQuery(id+"F0.imprint","IMPRINT",EDGE,{"derivedFrom":sQuery(id+"F0.wireOp",EDGE,"E3883")}),-1.0]])]});
            var Q17;
            Q17=makeQuery(id+"F0.imprint","IMPRINT",FACE,{"disambiguationData":[TD([[makeQuery(id+"F0.imprint","IMPRINT",EDGE,{"derivedFrom":sQuery(id+"F0.wireOp",EDGE,"E3443")}),-1.0]])]});
            var Q18;
            Q18=makeQuery(id+"F0.imprint","IMPRINT",FACE,{"disambiguationData":[TD([[makeQuery(id+"F0.imprint","IMPRINT",EDGE,{"derivedFrom":sQuery(id+"F0.wireOp",EDGE,"E3771")}),-1.0]])]});
            var Q19;
            Q19=makeQuery(id+"F0.imprint","IMPRINT",FACE,{"disambiguationData":[TD([[makeQuery(id+"F0.imprint","IMPRINT",EDGE,{"derivedFrom":sQuery(id+"F0.wireOp",EDGE,"E2359")}),-1.0]])]});
            var Q20;
            Q20=makeQuery(id+"F0.imprint","IMPRINT",FACE,{"disambiguationData":[TD([[makeQuery(id+"F0.imprint","IMPRINT",EDGE,{"derivedFrom":sQuery(id+"F0.wireOp",EDGE,"E2609")}),-1.0]])]});
            var Q21;
            Q21=makeQuery(id+"F0.imprint","IMPRINT",FACE,{"disambiguationData":[TD([[makeQuery(id+"F0.imprint","IMPRINT",EDGE,{"derivedFrom":sQuery(id+"F0.wireOp",EDGE,"E2469")}),-1.0]])]});
            var Q22;
            Q22=makeQuery(id+"F0.imprint","IMPRINT",FACE,{"disambiguationData":[TD([[makeQuery(id+"F0.imprint","IMPRINT",EDGE,{"derivedFrom":sQuery(id+"F0.wireOp",EDGE,"E2759")}),-1.0]])]});
            var Q23;
            Q23=makeQuery(id+"F0.imprint","IMPRINT",FACE,{"disambiguationData":[TD([[makeQuery(id+"F0.imprint","IMPRINT",EDGE,{"derivedFrom":sQuery(id+"F0.wireOp",EDGE,"E433")}),-1.0]])]});
            var Q24;
            Q24=makeQuery(id+"F0.imprint","IMPRINT",FACE,{"disambiguationData":[TD([[makeQuery(id+"F0.imprint","IMPRINT",EDGE,{"derivedFrom":sQuery(id+"F0.wireOp",EDGE,"E292")}),-1.0]])]});
            var Q25;
            Q25=makeQuery(id+"F0.imprint","IMPRINT",FACE,{"disambiguationData":[TD([[makeQuery(id+"F0.imprint","IMPRINT",EDGE,{"derivedFrom":sQuery(id+"F0.wireOp",EDGE,"E587")}),-1.0]])]});
            var Q26;
            Q26=makeQuery(id+"F0.imprint","IMPRINT",FACE,{"disambiguationData":[TD([[makeQuery(id+"F0.imprint","IMPRINT",EDGE,{"derivedFrom":sQuery(id+"F0.wireOp",EDGE,"E149")}),-1.0]])]});
            var Q27;
            Q27=makeQuery(id+"F0.imprint","IMPRINT",FACE,{"disambiguationData":[TD([[makeQuery(id+"F0.imprint","IMPRINT",EDGE,{"derivedFrom":sQuery(id+"F0.wireOp",EDGE,"E2008")}),-1.0]])]});
            var Q28;
            Q28=makeQuery(id+"F0.imprint","IMPRINT",FACE,{"disambiguationData":[TD([[makeQuery(id+"F0.imprint","IMPRINT",EDGE,{"derivedFrom":sQuery(id+"F0.wireOp",EDGE,"E2856")}),-1.0]])]});
            extrude(context, id + "F16", {"entities" : qUnion([Q0, Q1, Q2, Q3, Q4, Q5, Q6, Q7, Q8, Q9, Q10, Q11, Q12, Q13, Q14, Q15, Q16, Q17, Q18, Q19, Q20, Q21, Q22, Q23, Q24, Q25, Q26, Q27, Q28]), "operationType" : NewBodyOperationType.ADD, "depth" : 2.54 * mm, "offsetDistance" : 25.4 * mm});
        }
    });
